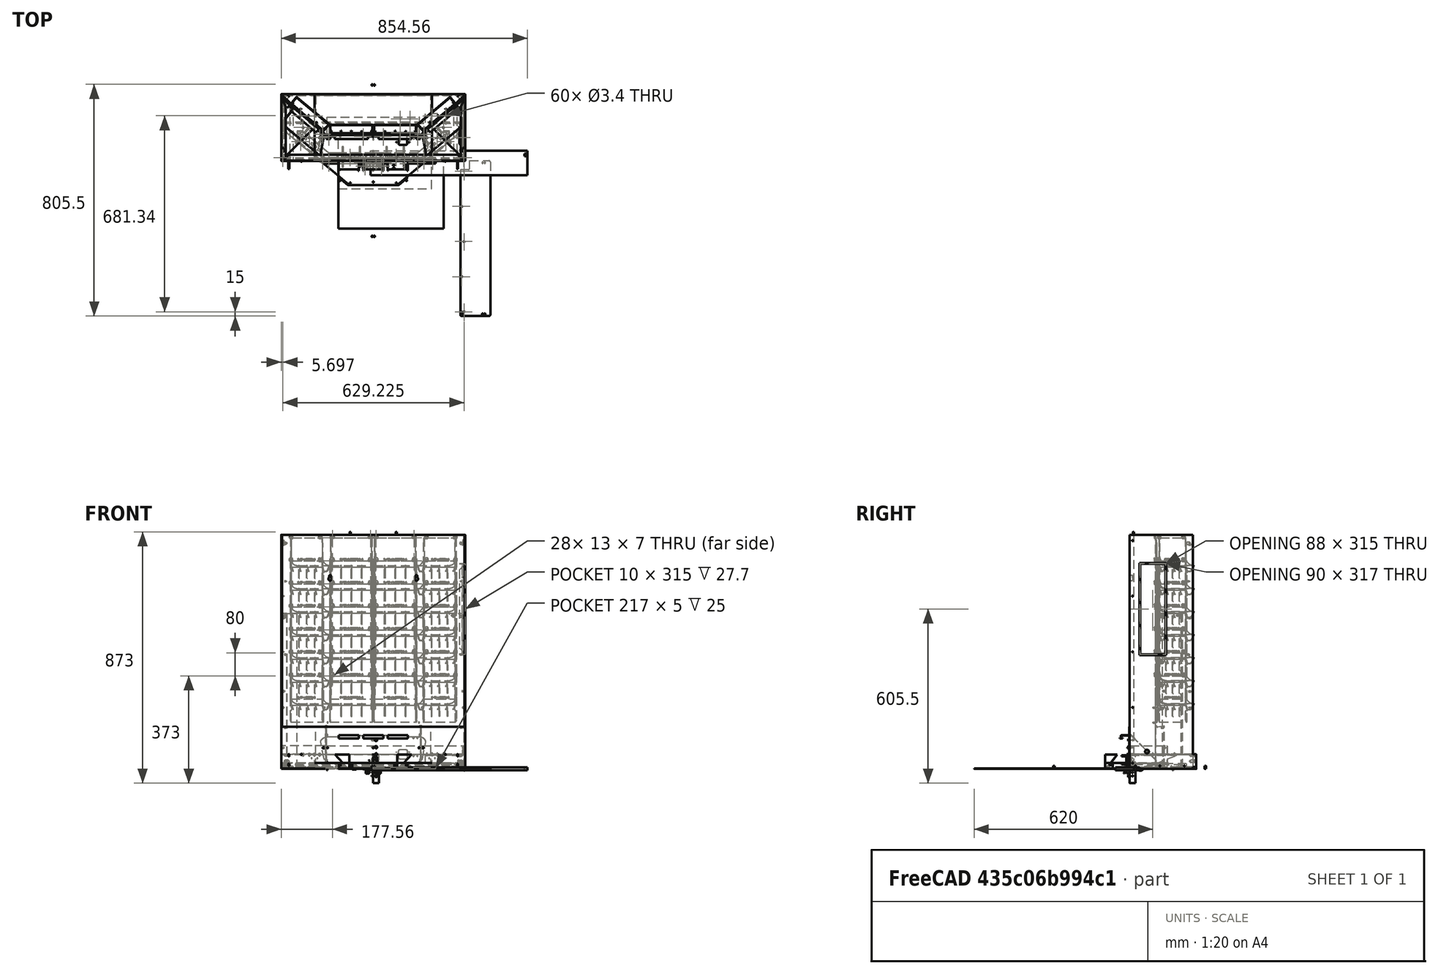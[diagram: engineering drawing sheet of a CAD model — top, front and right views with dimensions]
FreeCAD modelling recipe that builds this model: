
FCSTD DOCUMENT  (FreeCAD 0.22R37100 (Git))
Label: composit_stand10
License: All rights reserved
LicenseURL: http://en.wikipedia.org/wiki/All_rights_reserved
objects: Part::FeaturePython×149, Sketcher::SketchObject×121, PartDesign::CoordinateSystem×34, Part::Compound×33, PartDesign::SubShapeBinder×30, Part::Mirroring×28, Part::Extrusion×27, PartDesign::FeaturePython×26, PartDesign::Body×23, PartDesign::Boolean×23, PartDesign::Pocket×23, TechDraw::DrawViewDimension×21, PartDesign::Pad×18, App::DocumentObjectGroup×18, Path::FeaturePython×13, TechDraw::DrawViewPart×12, Part::Cylinder×5, PartDesign::Mirrored×5, TechDraw::DrawViewBalloon×5, TechDraw::DrawPage×5, +15 more types
note: 661 computed .brp shape members not serialized (recipe doc carries the construction recipe); baked Part::Feature solids carry a one-line shape summary decoded from their .brp
EXTERNAL_REF file=../module.FCStd obj=Spreadsheet
EXTERNAL_REF file=../module.FCStd obj=Sketch
EXTERNAL_REF file=../dropper.FCStd obj=Sketch007
EXTERNAL_REF file=../dropper.FCStd obj=Sketch008
EXTERNAL_REF file=../dropper.FCStd obj=Connect
EXTERNAL_REF file=../ULZ-P03-10W.FCStd obj=Sketch
EXTERNAL_REF file=../dropper.FCStd obj=Sketch
EXTERNAL_REF file=../magnet_fix.FCStd obj=Spreadsheet
EXTERNAL_REF file=../magnet_fix.FCStd obj=Sketch002
EXTERNAL_REF file=../module.FCStd obj=Body
EXTERNAL_REF file=../composit_electric_shield.FCStd obj=Body002
EXTERNAL_REF file=../composit_electric_shield.FCStd obj=Extrude002
EXTERNAL_REF file=composit_stand10_model.FCStd obj=Assembly
EXTERNAL_REF file=../magnet_fix.FCStd obj=Sketch006

FEATURE [Sketcher::SketchObject] Sketch
  FullyConstrained = true
  expr: Constraints[17] = module#<<Properties>>.module_width + 2 mm
  sketch-geometry (12):
    g0: LineSegment StartX=1 StartY=0 StartZ=0 EndX=151 EndY=0 EndZ=0
    g1: LineSegment StartX=151 StartY=0 StartZ=0 EndX=151 EndY=36 EndZ=0
    g2: LineSegment StartX=151 StartY=36 StartZ=0 EndX=1 EndY=36 EndZ=0
    g3: LineSegment StartX=1 StartY=36 StartZ=0 EndX=1 EndY=0 EndZ=0
    g4: LineSegment StartX=175.08 StartY=8.76442 StartZ=0 EndX=289.987 EndY=105.183 EndZ=0
    g5: LineSegment StartX=289.987 StartY=105.183 StartZ=0 EndX=266.846 EndY=132.76 EndZ=0
    g6: LineSegment StartX=266.846 StartY=132.76 StartZ=0 EndX=151.94 EndY=36.342 EndZ=0
    g7: LineSegment StartX=151.94 StartY=36.342 StartZ=0 EndX=175.08 EndY=8.76442 EndZ=0
    g8: LineSegment StartX=151 StartY=36 StartZ=0 EndX=151.532 EndY=36 EndZ=0
    g9: LineSegment StartX=151.94 StartY=36.342 StartZ=0 EndX=151.532 EndY=36 EndZ=0
    g10: LineSegment StartX=151 StartY=0 StartZ=0 EndX=164.635 EndY=0 EndZ=0
    g11: LineSegment StartX=175.08 StartY=8.76442 StartZ=0 EndX=164.635 EndY=0 EndZ=0
  constraints (34):
    c: Coincident(g0,g1)
    c: Coincident(g1,g2)
    c: Coincident(g2,g3)
    c: Coincident(g3,g0)
    c: Horizontal(g0)
    c: Horizontal(g2)
    c: Vertical(g1)
    c: Vertical(g3)
    c: Coincident(g4,g5)
    c: Coincident(g5,g6)
    c: Coincident(g6,g7)
    c: Coincident(g7,g4)
    c: Parallel(g4,g6)
    c: Parallel(g5,g7)
    c: Perpendicular(g5,g4)
    c: Equal(g2,g6)
    c: Equal(g1,g7)
    c: DistanceX(g2,g2) = 150
    c: DistanceY(g3,g3) = 36
    c: Coincident(g8,g1)
    c: Horizontal(g8)
    c: Coincident(g9,g6)
    c: Coincident(g9,g8)
    c: Coincident(g10,g0)
    c: Horizontal(g10)
    c: Coincident(g11,g4)
    c: Coincident(g11,g10)
    c: Parallel(g11,g4)
    c: Equal(g11,g10)
    c: Parallel(g9,g6)
    c: Angle(g4) = 0.698132
    c: DistanceX(g0) = 1
    c: Distance(g1,g6) = 1
    c: PointOnObject(g0,g-1)
FEATURE [Sketcher::SketchObject] Sketch001  label="base_sketch"
  ExternalGeometry = -> [Sketch]
  FullyConstrained = true
  sketch-geometry (4):
    g0: LineSegment StartX=0 StartY=0 StartZ=0 EndX=164.635 EndY=0 EndZ=0
    g1: LineSegment StartX=164.635 StartY=0 StartZ=0 EndX=319.563 EndY=130 EndZ=0
    g2: GeomPoint X=-164.635 Y=0 Z=0
    g3: GeomPoint X=-319.563 Y=130 Z=0
  constraints (12):
    c: PointOnObject(g0,g-2)
    c: Horizontal(g0)
    c: Coincident(g1,g0)
    c: PointOnObject(g-4,g1)
    c: PointOnObject(g-4,g1)
    c: PointOnObject(g-3,g0)
    c: Symmetric(g2,g0,g-2)
    c: DistanceX(g2,g0) = 329.27  'face_width'
    c: Symmetric(g3,g1,g-2)
    c: DistanceX(g3,g1) = 639.126  'total_width'
    c: DistanceY(g1) = 130  'total_depth'
    c: DistanceY(g0,g1) = 130
FEATURE [PartDesign::SubShapeBinder] Binder
  BindCopyOnChange = 0
  BindMode = 0
  ClaimChildren = true
  Context = -> Body [Binder.]
  Fuse = false
  MakeFace = true
  OffsetFill = false
  OffsetIntersection = false
  OffsetJoinType = 0
  OffsetOpenResult = false
  PartialLoad = false
  Relative = false
  Support = -> [Connect]
  _Version = 2
FEATURE [PartDesign::FeaturePython] BaseBend  # WARN: FeaturePython — macro-defined, semantics opaque (R4)
  BendSide = 0
  BendSketch = -> Binder
  MidPlane = false
  Reverse = false
  Suppressed = false
  length = 813
  radius = 0.1
  thickness = 0.3
FEATURE [PartDesign::SubShapeBinder] Binder001
  BindCopyOnChange = 0
  BindMode = 0
  ClaimChildren = true
  Context = -> Body001 [Binder001.]
  Fuse = false
  MakeFace = true
  OffsetFill = false
  OffsetIntersection = false
  OffsetJoinType = 0
  OffsetOpenResult = false
  PartialLoad = false
  Relative = false
  Support = -> [Connect001]
  _Version = 2
FEATURE [PartDesign::FeaturePython] BaseBend001  # WARN: FeaturePython — macro-defined, semantics opaque (R4)
  BendSide = 1
  BendSketch = -> Binder001
  MidPlane = false
  Reverse = false
  Suppressed = false
  length = 813
  radius = 0.1
  thickness = 0.3
  expr: length = <<BaseBend>>.length
FEATURE [Part::FeaturePython] Placment  # WARN: FeaturePython — macro-defined, semantics opaque (R4)
  AttacherType = Attacher::AttachEngine3D
  AttachmentOffset = pos=(0,0,0) rot=(-0.57735,-0.57735,-0.57735;2.0944rad)
  ExposePlacement = true
  MapMode = 45
  MarkerShape = 1
  MarkerSize = 50
  NumElements = 1
  Placement = pos=(76,0,0) rot=(0,0,1;0rad)
  Type = lattice2AttachablePlacement.AttachablePlacement
  isLattice = 1
FEATURE [Part::FeaturePython] Placment001  # WARN: FeaturePython — macro-defined, semantics opaque (R4)
  AttacherType = Attacher::AttachEngine3D
  AttachmentOffset = pos=(0,0,0) rot=(-0.57735,-0.57735,-0.57735;2.0944rad)
  ExposePlacement = true
  MapMode = 45
  MarkerShape = 1
  MarkerSize = 50
  NumElements = 1
  Placement = pos=(232.533,56.9735,0) rot=(0,0,1;0.698132rad)
  Type = lattice2AttachablePlacement.AttachablePlacement
  isLattice = 1
FEATURE [Part::FeaturePython] LinearArray002  # WARN: FeaturePython — macro-defined, semantics opaque (R4)
  Alignment = 0
  CellStart = A1
  Count = 2
  Dir = (1,0,0)
  DirIsDriven = true
  DistributionLaw = 0
  DrivenProperty = 1
  EndInclusive = true
  ExposePlacement = false
  GeneratorMode = 0
  MarkerShape = 1
  MarkerSize = 0
  NumElements = 2
  OrientMode = 1
  Placement = pos=(-30,13.8,0) rot=(0,0,1;0rad)
  Point = (0,0,0)
  PointIsDriven = true
  Reverse = false
  SpanEnd = 60
  SpanStart = 0
  Step = 60
  Type = lattice2LinearArray.LinearArray
  VSGVersion = 1
  Values = 0.0 | 60.0
  ValuesSource = 2
  isLattice = 1
  expr: .Placement.Base.x = -SpanEnd / 2
FEATURE [PartDesign::SubShapeBinder] Binder002
  BindCopyOnChange = 0
  BindMode = 0
  ClaimChildren = false
  Fuse = false
  MakeFace = true
  OffsetFill = false
  OffsetIntersection = false
  OffsetJoinType = 0
  OffsetOpenResult = false
  PartialLoad = false
  Relative = true
  Support = -> [<external ../module.FCStd>#Sketch]
  _Version = 2
  expr: Support = module#<<module_holes>>._self
FEATURE [Part::Extrusion] Extrude
  Base = -> Binder002
  Dir = (0,0,1)
  DirMode = 2
  FaceMakerClass = Part::FaceMakerBullseye
  LengthFwd = 3
  LengthRev = 0
  Reversed = true
  Solid = false
  Symmetric = false
FEATURE [Part::FeaturePython] LinearArray  # WARN: FeaturePython — macro-defined, semantics opaque (R4)
  Alignment = 0
  CellStart = A1
  Count = 7
  Dir = (0,-1,0)
  DirIsDriven = true
  DistributionLaw = 0
  DrivenProperty = 1
  EndInclusive = true
  ExposePlacement = false
  GeneratorMode = 1
  MarkerShape = 1
  MarkerSize = 0
  NumElements = 7
  OrientMode = 0
  Placement = pos=(0,0,0) rot=(0,0.707107,0.707107;3.14159rad)
  Point = (0,0,0)
  PointIsDriven = true
  Reverse = false
  SpanEnd = 50
  SpanStart = 0
  Step = 80
  Type = lattice2LinearArray.LinearArray
  VSGVersion = 1
  Values = 0.0 | 80.0 | 160.0 | 240.0 | 320.0 | 400.0 | 480.0
  ValuesSource = 2
  isLattice = 1
FEATURE [Part::FeaturePython] Placment002  # WARN: FeaturePython — macro-defined, semantics opaque (R4)
  AttacherType = Attacher::AttachEngine3D
  ExposePlacement = true
  MarkerShape = 1
  MarkerSize = 50
  NumElements = 1
  Placement = pos=(-76,0,0) rot=(0,0,1;0rad)
  Type = lattice2AttachablePlacement.AttachablePlacement
  isLattice = 1
  expr: .Placement.Base.x = -<<Placment>>.Placement.Base.x
  expr: .Placement.Base.y = <<Placment>>.Placement.Base.y
FEATURE [Part::FeaturePython] Placment003  # WARN: FeaturePython — macro-defined, semantics opaque (R4)
  AttacherType = Attacher::AttachEngine3D
  ExposePlacement = true
  MarkerShape = 1
  MarkerSize = 50
  NumElements = 1
  Placement = pos=(-232.533,56.9735,0) rot=(0,0,-1;0.698132rad)
  Type = lattice2AttachablePlacement.AttachablePlacement
  isLattice = 1
  expr: .Placement.Base.x = -<<Placment001>>.Placement.Base.x
  expr: .Placement.Base.y = <<Placment001>>.Placement.Base.y
  expr: .Placement.Rotation.Angle = -<<Placment001>>.Placement.Rotation.Angle
  expr: .Placement.Rotation.Axis = <<Placment001>>.Placement.Rotation.Axis
FEATURE [Part::FeaturePython] Join  # WARN: FeaturePython — macro-defined, semantics opaque (R4)
  ExposePlacement = false
  Interleave = false
  Links = -> [Placment,Placment001,Placment002,Placment003]
  MarkerShape = 1
  MarkerSize = 0
  NumElements = 4
  Type = lattice2JoinArrays.JoinArrays
  isLattice = 1
FEATURE [Part::FeaturePython] Populate  label="Populate Join with LinearArray"  # WARN: FeaturePython — macro-defined, semantics opaque (R4)
  Copying = 0
  ExposePlacement = false
  MarkerShape = 1
  MarkerSize = 0
  NumElements = 28
  Object = -> LinearArray
  OutputCompounding = 0
  Placement = pos=(0,90,803) rot=(0,0,1;0rad)
  PlacementsTo = -> Join
  Referencing = 0
  Type = lattice2PopulateCopies.LatticePopulateCopies
  isLattice = 1
  expr: .Placement.Base.y = <<Dimensions_sketch>>.Constraints.offset
  expr: .Placement.Base.z = <<BaseBend>>.length - 10 mm
FEATURE [Part::FeaturePython] Populate001  label="Populate Populate Join with LinearArray with Extrude"  # WARN: FeaturePython — macro-defined, semantics opaque (R4)
  Copying = 0
  ExposePlacement = false
  MarkerShape = 1
  MarkerSize = 0
  NumElements = 0
  Object = -> Extrude
  OutputCompounding = 1
  PlacementsTo = -> Populate
  Referencing = 0
  Type = lattice2PopulateCopies.LatticePopulateCopies
  isLattice = 0
FEATURE [PartDesign::SubShapeBinder] Binder003
  BindCopyOnChange = 0
  BindMode = 0
  ClaimChildren = true
  Fuse = false
  MakeFace = true
  OffsetFill = false
  OffsetIntersection = false
  OffsetJoinType = 0
  OffsetOpenResult = false
  PartialLoad = false
  Relative = true
  Support = -> [<external ../dropper.FCStd>#Sketch007]
  _Version = 2
  expr: Support = <<dropper>>#<<base>>._self
FEATURE [PartDesign::SubShapeBinder] Binder004
  BindCopyOnChange = 0
  BindMode = 0
  ClaimChildren = false
  Fuse = false
  MakeFace = true
  OffsetFill = false
  OffsetIntersection = false
  OffsetJoinType = 0
  OffsetOpenResult = false
  PartialLoad = false
  Relative = true
  Support = -> [<external ../dropper.FCStd>#Sketch008]
  _Version = 2
  expr: Support = dropper#<<feed>>._self
FEATURE [PartDesign::SubShapeBinder] Binder005
  BindCopyOnChange = 0
  BindMode = 0
  ClaimChildren = false
  Fuse = false
  MakeFace = true
  OffsetFill = false
  OffsetIntersection = false
  OffsetJoinType = 0
  OffsetOpenResult = false
  PartialLoad = false
  Relative = true
  Support = -> [<external ../dropper.FCStd>#Connect]
  _Version = 2
  expr: Support = dropper#<<fix>>._self
FEATURE [Part::Extrusion] Extrude001
  Base = -> Binder003
  Dir = (0,0,1)
  DirMode = 2
  FaceMakerClass = Part::FaceMakerBullseye
  LengthFwd = 5
  LengthRev = 0
  Solid = false
  Symmetric = false
FEATURE [Part::Extrusion] Extrude002
  Base = -> Binder005
  Dir = (0,0,1)
  DirMode = 2
  FaceMakerClass = Part::FaceMakerBullseye
  LengthFwd = 2.5
  LengthRev = 0
  Solid = false
  Symmetric = false
FEATURE [Part::Extrusion] Extrude003
  Base = -> Binder004
  Dir = (0,0,1)
  DirMode = 2
  FaceMakerClass = Part::FaceMakerBullseye
  LengthFwd = 5
  LengthRev = 0
  Solid = false
  Symmetric = false
FEATURE [Part::FeaturePython] Populate002  label="Populate Join with LinearArray002"  # WARN: FeaturePython — macro-defined, semantics opaque (R4)
  Copying = 0
  ExposePlacement = false
  MarkerShape = 1
  MarkerSize = 0
  NumElements = 8
  Object = -> LinearArray002
  OutputCompounding = 0
  PlacementsTo = -> Join
  Referencing = 0
  Type = lattice2PopulateCopies.LatticePopulateCopies
  isLattice = 1
FEATURE [Part::FeaturePython] Populate003  label="Populate Populate Join with LinearArray002 with Fusion"  # WARN: FeaturePython — macro-defined, semantics opaque (R4)
  Copying = 0
  ExposePlacement = false
  MarkerShape = 1
  MarkerSize = 0
  NumElements = 0
  Object = -> Extrude001
  OutputCompounding = 1
  PlacementsTo = -> Populate002
  Referencing = 0
  Type = lattice2PopulateCopies.LatticePopulateCopies
  isLattice = 0
FEATURE [PartDesign::FeaturePython] Extend  # WARN: FeaturePython — macro-defined, semantics opaque (R4)
  BaseFeature = -> BaseBend
  Offset = 0.02
  Refine = true
  Suppressed = false
  UseSubtraction = false
  baseObject = -> BaseBend [Face1]
  gap1 = 0
  gap2 = 0
  length = 0
FEATURE [PartDesign::FeaturePython] Bend  # WARN: FeaturePython — macro-defined, semantics opaque (R4)
  AutoMiter = false
  BaseFeature = -> Extend
  BendType = 0
  LengthList = [0.1]
  LengthSpec = 0
  ReliefFactor = 0.7
  Suppressed = false
  UseReliefFactor = false
  angle = 90
  baseObject = -> Extend [Edge4,Edge17,Edge75,Edge46,Edge63]
  bendAList = [90]
  extend1 = 0
  extend2 = 0
  gap1 = 0
  gap2 = 0
  invert = true
  kfactor = 0.5
  length = 0.1
  maxExtendDist = 2.5
  minGap = 0.1
  minReliefGap = 1.5
  miterangle1 = 0
  miterangle2 = 0
  offset = 0
  radius = 0.1
  reliefType = 0
  reliefd = 1
  reliefw = 0.8
  sketchflip = false
  sketchinvert = false
  unfold = false
  expr: radius = BaseBend.radius
FEATURE [Sketcher::SketchObject] Sketch007
  ExternalGeometry = -> [Sketch001]
  FullyConstrained = true
  sketch-geometry (9):
    g0: LineSegment StartX=299.876 StartY=113.48 StartZ=0 EndX=319.563 EndY=130 EndZ=0
    g1: LineSegment StartX=319.563 StartY=130 StartZ=0 EndX=274.703 EndY=183.462 EndZ=0
    g2: LineSegment StartX=274.703 StartY=183.462 StartZ=0 EndX=264.242 EndY=179.655 EndZ=0
    g3: LineSegment StartX=264.482 StartY=178.997 StartZ=0 EndX=274.482 EndY=182.637 EndZ=0
    g4: LineSegment StartX=274.482 StartY=182.637 StartZ=0 EndX=319.477 EndY=129.014 EndZ=0
    g5: LineSegment StartX=319.477 StartY=129.014 StartZ=0 EndX=300.326 EndY=112.944 EndZ=0
    g6: LineSegment StartX=300.326 StartY=112.944 StartZ=0 EndX=299.876 EndY=113.48 EndZ=0
    g7: LineSegment StartX=264.482 StartY=178.997 StartZ=0 EndX=264.242 EndY=179.655 EndZ=0
    g8: LineSegment StartX=319.477 StartY=129.014 StartZ=0 EndX=320.013 EndY=129.464 EndZ=0
  constraints (26):
    c: Coincident(g0,g1)
    c: Coincident(g1,g2)
    c: Coincident(g0,g-3)
    c: PointOnObject(g0,g-3)
    c: Angle(g1) = 2.26893
    c: Angle(g2,g1) = 1.91986
    c: Coincident(g3,g4)
    c: Coincident(g4,g5)
    c: Coincident(g5,g6)
    c: Coincident(g6,g0)
    c: Coincident(g3,g7)
    c: Coincident(g7,g2)
    c: Perpendicular(g2,g7)
    c: Perpendicular(g3,g7)
    c: Perpendicular(g5,g6)
    c: Perpendicular(g0,g6)
    c: Distance(g6) = 0.7
    c: Coincident(g8,g4)
    c: PointOnObject(g8,g1)
    c: Perpendicular(g4,g8)
    c: Equal(g7,g8)
    c: Equal(g8,g6)
    c: Distance(g5) = 25
    c: DistanceX(g3,g3) = 10
    c: Parallel(g4,g1)
    c: Distance(g4) = 70
FEATURE [PartDesign::SubShapeBinder] Binder006
  BindCopyOnChange = 0
  BindMode = 0
  ClaimChildren = true
  Context = -> Body003 [Binder006.]
  Fuse = false
  MakeFace = true
  OffsetFill = false
  OffsetIntersection = false
  OffsetJoinType = 0
  OffsetOpenResult = false
  PartialLoad = false
  Relative = false
  Support = -> [Sketch007]
  _Version = 2
FEATURE [PartDesign::FeaturePython] BaseBend002  # WARN: FeaturePython — macro-defined, semantics opaque (R4)
  BendSide = 1
  BendSketch = -> Binder006
  MidPlane = false
  Reverse = false
  Suppressed = false
  length = 540
  radius = 2
  thickness = 0.7
FEATURE [PartDesign::SubShapeBinder] Binder007
  BindCopyOnChange = 0
  BindMode = 0
  ClaimChildren = true
  Context = -> Body004 [Binder007.]
  Fuse = false
  MakeFace = true
  OffsetFill = false
  OffsetIntersection = false
  OffsetJoinType = 0
  OffsetOpenResult = false
  PartialLoad = false
  Relative = false
  Support = -> [Connect006]
  _Version = 2
FEATURE [PartDesign::Pad] Pad
  Direction = (0,0,1)
  Length = 5
  Length2 = 10
  Profile = -> Binder007
  Suppressed = false
  Type = 0
FEATURE [Sketcher::SketchObject] Sketch008  label="dropper_fix_composit_base_sketch"
  ExternalGeometry = -> [Sketch001]
  FullyConstrained = true
  expr: Constraints[31] = -<<Dimensions_sketch>>.Constraints.offset + 5.4 mm
  sketch-geometry (10):
    g0: LineSegment StartX=0 StartY=-84.6 StartZ=0 EndX=83.1036 EndY=-84.6 EndZ=0
    g1: LineSegment StartX=83.1036 StartY=-84.6 StartZ=0 EndX=313.563 EndY=108.778 EndZ=0
    g2: LineSegment StartX=313.563 StartY=108.778 StartZ=0 EndX=313.563 EndY=130 EndZ=0
    g3: LineSegment StartX=313.563 StartY=130 StartZ=0 EndX=0 EndY=130 EndZ=0
    g4: LineSegment StartX=164.635 StartY=0 StartZ=0 EndX=164.635 EndY=-3 EndZ=0
    g5: LineSegment StartX=164.635 StartY=-3 StartZ=0 EndX=164.635 EndY=-4 EndZ=0
    g6: LineSegment StartX=164.635 StartY=-4 StartZ=0 EndX=164.635 EndY=-7.4 EndZ=0
    g7: LineSegment StartX=164.635 StartY=-7.4 StartZ=0 EndX=164.635 EndY=-12.4 EndZ=0
    g8: LineSegment StartX=0 StartY=0 StartZ=0 EndX=0 EndY=-12.4 EndZ=0
    g9: LineSegment StartX=164.635 StartY=0 StartZ=0 EndX=172.606 EndY=-9.49895 EndZ=0
  constraints (33):
    c: PointOnObject(g0,g-2)
    c: Horizontal(g0)
    c: Coincident(g1,g2)
    c: Vertical(g2)
    c: Coincident(g2,g3)
    c: PointOnObject(g3,g-2)
    c: Horizontal(g3)
    c: PointOnObject(g-3,g3)
    c: Parallel(g1,g-3)
    c: Coincident(g4,g-3)
    c: Coincident(g5,g4)
    c: Vertical(g5)
    c: Coincident(g6,g5)
    c: Coincident(g7,g6)
    c: Vertical(g7)
    c: Vertical(g6)
    c: Vertical(g4)
    c: DistanceY(g4,g4) = 3
    c: DistanceY(g6,g6) = 3.4
    c: DistanceY(g5,g5) = 1
    c: DistanceY(g7,g7) = 5
    c: Vertical(g8)
    c: Horizontal(g4,g8)
    c: Coincident(g9,g4)
    c: Equal(g9,g8)
    c: DistanceX(g2,g-3) = 6
    c: Angle(g1) = 0.698132  'angle'
    c: PointOnObject(g9,g1)
    c: Perpendicular(g1,g9)
    c: Coincident(g0,g1)
    c: Horizontal(g8,g7)
    c: DistanceY(g0) = -84.6
    c: PointOnObject(g8,g-2)
FEATURE [PartDesign::Body] Body005  label="dummy_body"
  Origin = -> Origin005
FEATURE [Part::Extrusion] Extrude004
  Base = -> Binder003
  Dir = (0,0,1)
  DirMode = 2
  FaceMakerClass = Part::FaceMakerBullseye
  LengthFwd = 2.5
  LengthRev = 0
  Solid = false
  Symmetric = false
FEATURE [Part::Mirroring] Part__Mirroring003  label="Sketch008 (Mirror #4)"
  Base = (0,0,0)
  Normal = (1,0,0)
  Source = -> Sketch008
FEATURE [Part::FeaturePython] Connect003  # WARN: FeaturePython — macro-defined, semantics opaque (R4)
  Objects = -> [Sketch008,Part__Mirroring003]
  Tolerance = 0
FEATURE [PartDesign::SubShapeBinder] Binder008
  BindCopyOnChange = 0
  BindMode = 0
  ClaimChildren = true
  Context = -> Body006 [Binder008.]
  Fuse = false
  MakeFace = true
  OffsetFill = false
  OffsetIntersection = false
  OffsetJoinType = 0
  OffsetOpenResult = false
  PartialLoad = false
  Relative = false
  Support = -> [Connect003]
  _Version = 2
FEATURE [PartDesign::FeaturePython] BaseBend003  # WARN: FeaturePython — macro-defined, semantics opaque (R4)
  BendSide = 0
  BendSketch = -> Binder008
  MidPlane = false
  Reverse = false
  Suppressed = false
  length = 100
  radius = 0.1
  thickness = 0.3
FEATURE [PartDesign::FeaturePython] Extend001  # WARN: FeaturePython — macro-defined, semantics opaque (R4)
  BaseFeature = -> BaseBend003
  Offset = 0.02
  Refine = true
  Suppressed = false
  UseSubtraction = false
  baseObject = -> BaseBend003 [Face1]
  gap1 = 0
  gap2 = 0
  length = 0
FEATURE [PartDesign::FeaturePython] Bend001  # WARN: FeaturePython — macro-defined, semantics opaque (R4)
  AutoMiter = true
  BaseFeature = -> Extend001
  BendType = 0
  LengthList = [20]
  LengthSpec = 0
  ReliefFactor = 0.7
  Suppressed = false
  UseReliefFactor = false
  angle = 90
  baseObject = -> Extend001 [Edge11,Edge9,Edge8,Edge6]
  bendAList = [90]
  extend1 = 0
  extend2 = 0
  gap1 = 0
  gap2 = 0
  invert = true
  kfactor = 0.5
  length = 20
  maxExtendDist = 5
  minGap = 0.2
  minReliefGap = 1
  miterangle1 = 0
  miterangle2 = 0
  offset = 0
  radius = 0.1
  reliefType = 0
  reliefd = 1
  reliefw = 0.8
  sketchflip = false
  sketchinvert = false
  unfold = false
  expr: radius = BaseBend003.radius
FEATURE [Sketcher::SketchObject] Sketch011
  FullyConstrained = true
  sketch-geometry (3):
    g0: ArcOfCircle CenterX=-2 CenterY=-2 CenterZ=0 NormalX=0 NormalY=0 NormalZ=1 AngleXU=0 Radius=2 StartAngle=0 EndAngle=1.5708
    g1: LineSegment StartX=-2 StartY=0 StartZ=0 EndX=0 EndY=0 EndZ=0
    g2: LineSegment StartX=0 StartY=0 StartZ=0 EndX=0 EndY=-2 EndZ=0
  constraints (7):
    c: PointOnObject(g0,g-2)
    c: PointOnObject(g0,g-1)
    c: Coincident(g1,g2)
    c: Tangent(g2,g0) = 1.5708
    c: Tangent(g0,g1) = 1.5708
    c: Coincident(g1,g-1)
    c: Radius(g0) = 2
FEATURE [Part::Extrusion] Extrude005
  Base = -> Sketch011
  Dir = (0,0,1)
  DirMode = 2
  FaceMakerClass = Part::FaceMakerBullseye
  LengthFwd = 10
  LengthRev = 0
  Solid = true
  Symmetric = true
FEATURE [Part::FeaturePython] Placment004  # WARN: FeaturePython — macro-defined, semantics opaque (R4)
  AttacherType = Attacher::AttachEngine3D
  AttachmentOffset = pos=(0,0,0) rot=(-0.707107,0,0.707107;3.14159rad)
  ExposePlacement = true
  MapMode = 7
  MarkerShape = 1
  MarkerSize = 20
  NumElements = 1
  Placement = pos=(264.242,179.655,0) rot=(-0.123724,0.701674,-0.701674;2.8954rad)
  Type = lattice2AttachablePlacement.AttachablePlacement
  isLattice = 1
FEATURE [Part::FeaturePython] Placment005  # WARN: FeaturePython — macro-defined, semantics opaque (R4)
  AttacherType = Attacher::AttachEngine3D
  AttachmentOffset = pos=(0,0,0) rot=(0.707107,0,0.707107;3.14159rad)
  ExposePlacement = true
  MapMode = 7
  MarkerShape = 1
  MarkerSize = 10
  NumElements = 1
  Placement = pos=(299.876,113.48,0) rot=(-0.249244,0.684791,-0.684791;2.65306rad)
  Type = lattice2AttachablePlacement.AttachablePlacement
  isLattice = 1
FEATURE [Part::FeaturePython] Join001  # WARN: FeaturePython — macro-defined, semantics opaque (R4)
  ExposePlacement = false
  Interleave = false
  Links = -> [Placment004,Placment005]
  MarkerShape = 1
  MarkerSize = 0
  NumElements = 2
  Type = lattice2JoinArrays.JoinArrays
  isLattice = 1
FEATURE [Part::FeaturePython] Populate005  label="Populate Join001 with Extrude005"  # WARN: FeaturePython — macro-defined, semantics opaque (R4)
  Copying = 0
  ExposePlacement = false
  MarkerShape = 1
  MarkerSize = 0
  NumElements = 0
  Object = -> Extrude005
  OutputCompounding = 1
  PlacementsTo = -> Join001
  Referencing = 0
  Type = lattice2PopulateCopies.LatticePopulateCopies
  isLattice = 0
FEATURE [Part::FeaturePython] Mirror  label="Mirror of Populate Join001 with Extrude005"  # WARN: FeaturePython — macro-defined, semantics opaque (R4)
  ExposePlacement = false
  FlipX = false
  FlipY = false
  FlipZ = true
  MarkerShape = 1
  MarkerSize = 0
  NumElements = 0
  Object = -> Populate005
  ObjectTraversal = 0
  PivotPlacement = pos=(0,0,270) rot=(0,0,1;0rad)
  Type = lattice2Mirror.LatticeMirror
  isLattice = 0
  expr: .PivotPlacement.Base.z = <<BaseBend002>>.length / 2
FEATURE [PartDesign::SubShapeBinder] Binder010
  BindCopyOnChange = 0
  BindMode = 0
  ClaimChildren = false
  Fuse = false
  MakeFace = true
  OffsetFill = false
  OffsetIntersection = false
  OffsetJoinType = 0
  OffsetOpenResult = false
  PartialLoad = false
  Relative = true
  Support = -> [<external ../ULZ-P03-10W.FCStd>#Sketch]
  _Version = 2
  expr: Support = <<ULZ-P03-10W>>#<<Sketch>>._self
FEATURE [Sketcher::SketchObject] Sketch012
  ExternalGeometry = -> [Binder010]
  FullyConstrained = true
  sketch-geometry (12):
    g0: ArcOfCircle CenterX=3.95 CenterY=-263.8 CenterZ=0 NormalX=0 NormalY=0 NormalZ=1 AngleXU=0 Radius=1.7 StartAngle=3.14159 EndAngle=6.28319
    g1: ArcOfCircle CenterX=3.95 CenterY=-262.2 CenterZ=0 NormalX=0 NormalY=0 NormalZ=1 AngleXU=0 Radius=1.7 StartAngle=2.911e-13 EndAngle=3.14159
    g2: LineSegment StartX=2.25 StartY=-263.8 StartZ=0 EndX=2.25 EndY=-262.2 EndZ=0
    g3: LineSegment StartX=5.65 StartY=-263.8 StartZ=0 EndX=5.65 EndY=-262.2 EndZ=0
    g4: GeomPoint X=3.95 Y=-260.5 Z=0
    g5: GeomPoint X=3.95 Y=-265.5 Z=0
    g6: ArcOfCircle CenterX=-3.95 CenterY=262.2 CenterZ=0 NormalX=0 NormalY=0 NormalZ=1 AngleXU=0 Radius=1.7 StartAngle=3.14159 EndAngle=6.28319
    g7: ArcOfCircle CenterX=-3.95 CenterY=263.8 CenterZ=0 NormalX=0 NormalY=0 NormalZ=1 AngleXU=0 Radius=1.7 StartAngle=1.26e-14 EndAngle=3.14159
    g8: LineSegment StartX=-5.65 StartY=262.2 StartZ=0 EndX=-5.65 EndY=263.8 EndZ=0
    g9: LineSegment StartX=-2.25 StartY=262.2 StartZ=0 EndX=-2.25 EndY=263.8 EndZ=0
    g10: GeomPoint X=-3.95 Y=265.5 Z=0
    g11: GeomPoint X=-3.95 Y=260.5 Z=0
  constraints (26):
    c: Tangent(g0,g2) = 1.5708
    c: Tangent(g0,g3) = -1.5708
    c: Tangent(g1,g2) = 1.5708
    c: Tangent(g1,g3) = -1.5708
    c: Equal(g0,g1)
    c: Vertical(g2)
    c: Symmetric(g0,g1,g-4)
    c: Equal(g1,g-4)
    c: PointOnObject(g4,g1)
    c: PointOnObject(g5,g0)
    c: Vertical(g5,g0)
    c: Vertical(g4,g1)
    c: DistanceY(g5,g4) = 5
    c: Tangent(g6,g8) = 1.5708
    c: Tangent(g6,g9) = -1.5708
    c: Tangent(g7,g8) = 1.5708
    c: Tangent(g7,g9) = -1.5708
    c: Equal(g6,g7)
    c: Vertical(g8)
    c: Symmetric(g6,g7,g-3)
    c: PointOnObject(g10,g7)
    c: PointOnObject(g11,g6)
    c: Vertical(g11,g-3)
    c: Vertical(g-3,g10)
    c: Equal(g-3,g7)
    c: DistanceY(g11,g10) = 5
FEATURE [Part::Extrusion] Extrude006
  Base = -> Sketch012
  Dir = (0,0,1)
  DirMode = 2
  FaceMakerClass = Part::FaceMakerBullseye
  LengthFwd = 10
  LengthRev = 0
  Solid = true
  Symmetric = false
FEATURE [Part::Mirroring] Part__Mirroring004  label="Extrude006 (Mirror #5)"
  Base = (0,0,0)
  Normal = (1,0,0)
  Source = -> Extrude006
FEATURE [Part::Compound] Compound005
  Links = -> [Extrude006,Part__Mirroring004]
FEATURE [Part::FeaturePython] Placment006  # WARN: FeaturePython — macro-defined, semantics opaque (R4)
  AttacherType = Attacher::AttachEngine3D
  AttachmentOffset = pos=(0,270,13) rot=(0,-1,0;1.5708rad)
  ExposePlacement = true
  MapMode = 7
  MarkerShape = 1
  MarkerSize = 20
  NumElements = 1
  Placement = pos=(283.059,173.504,270) rot=(0.834817,-0.389282,-0.389282;1.75037rad)
  Type = lattice2AttachablePlacement.AttachablePlacement
  isLattice = 1
  expr: .AttachmentOffset.Base.y = <<BaseBend002>>.length / 2
FEATURE [Part::FeaturePython] Populate006  label="Populate Placment006 with Compound005"  # WARN: FeaturePython — macro-defined, semantics opaque (R4)
  Copying = 0
  ExposePlacement = false
  MarkerShape = 1
  MarkerSize = 0
  NumElements = 0
  Object = -> Compound005
  OutputCompounding = 2
  PlacementsTo = -> Placment006
  Referencing = 0
  Type = lattice2PopulateCopies.LatticePopulateCopies
  isLattice = 0
FEATURE [Part::FeaturePython] Placment007  # WARN: FeaturePython — macro-defined, semantics opaque (R4)
  AttacherType = Attacher::AttachEngine3D
  ExposePlacement = true
  MarkerShape = 1
  MarkerSize = 50
  NumElements = 1
  Placement = pos=(0,13,0) rot=(0,0,1;0rad)
  Type = lattice2AttachablePlacement.AttachablePlacement
  isLattice = 1
FEATURE [Part::FeaturePython] Placment008  # WARN: FeaturePython — macro-defined, semantics opaque (R4)
  AttacherType = Attacher::AttachEngine3D
  ExposePlacement = true
  MarkerShape = 1
  MarkerSize = 50
  NumElements = 1
  Placement = pos=(127.5,21,0) rot=(0,0,1;0rad)
  Type = lattice2AttachablePlacement.AttachablePlacement
  isLattice = 1
  expr: .Placement.Base.x = <<LinearArray003>>.Step / 2
FEATURE [Part::FeaturePython] Join002  # WARN: FeaturePython — macro-defined, semantics opaque (R4)
  ExposePlacement = false
  Interleave = false
  Links = -> [Placment007,Placment008]
  MarkerShape = 1
  MarkerSize = 0
  NumElements = 2
  Type = lattice2JoinArrays.JoinArrays
  isLattice = 1
FEATURE [Part::FeaturePython] LinearArray003  # WARN: FeaturePython — macro-defined, semantics opaque (R4)
  Alignment = 0
  CellStart = A1
  Count = 3
  Dir = (1,0,0)
  DirIsDriven = true
  DistributionLaw = 0
  DrivenProperty = 1
  EndInclusive = true
  ExposePlacement = false
  GeneratorMode = 0
  MarkerShape = 1
  MarkerSize = 0
  NumElements = 3
  OrientMode = 1
  Point = (0,0,0)
  PointIsDriven = true
  Reverse = false
  SpanEnd = 525
  SpanStart = 15
  Step = 255
  Type = lattice2LinearArray.LinearArray
  VSGVersion = 1
  Values = 15.0 | 270.0 | 525.0
  ValuesSource = 2
  isLattice = 1
  expr: SpanEnd = <<BaseBend002>>.length - 15 mm
FEATURE [Part::Box] Box  label="Cube"
  AttacherType = Attacher::AttachEngine3D
  Height = 10
  Length = 545
  Placement = pos=(-10,-50,-5) rot=(0,0,1;0rad)
  Width = 84
  expr: Length = <<LinearArray003>>.SpanEnd + 20 mm
FEATURE [Part::FeaturePython] Populate007  label="Populate LinearArray003 with Join002"  # WARN: FeaturePython — macro-defined, semantics opaque (R4)
  Copying = 0
  ExposePlacement = false
  MarkerShape = 1
  MarkerSize = 0
  NumElements = 6
  Object = -> Join002
  OutputCompounding = 0
  PlacementsTo = -> LinearArray003
  Referencing = 0
  Type = lattice2PopulateCopies.LatticePopulateCopies
  isLattice = 1
FEATURE [Part::FeaturePython] ArrayFilter  # WARN: FeaturePython — macro-defined, semantics opaque (R4)
  Base = -> Populate007
  ExposePlacement = false
  FilterType = 2
  Invert = false
  MarkerShape = 1
  MarkerSize = 0
  NumElements = 5
  Stencil = -> Box
  Type = lattice2ArrayFilter.LatticeArrayFilter
  WindowFrom = 0
  WindowTo = 1
  isLattice = 1
FEATURE [Part::FeaturePython] Placment009  # WARN: FeaturePython — macro-defined, semantics opaque (R4)
  AttacherType = Attacher::AttachEngine3D
  AttachmentOffset = pos=(-1,0,0) rot=(0.57735,0.57735,0.57735;2.0944rad)
  ExposePlacement = true
  MapMode = 7
  MarkerShape = 1
  MarkerSize = 20
  NumElements = 1
  Placement = pos=(318.92,130.766,0) rot=(0.671543,-0.313146,0.671543;2.53465rad)
  Type = lattice2AttachablePlacement.AttachablePlacement
  isLattice = 1
FEATURE [Part::FeaturePython] Populate008  label="Populate Placment009 with ArrayFilter"  # WARN: FeaturePython — macro-defined, semantics opaque (R4)
  Copying = 0
  ExposePlacement = false
  MarkerShape = 1
  MarkerSize = 0
  NumElements = 5
  Object = -> ArrayFilter
  OutputCompounding = 0
  PlacementsTo = -> Placment009
  Referencing = 0
  Type = lattice2PopulateCopies.LatticePopulateCopies
  isLattice = 1
FEATURE [Part::Cylinder] Cylinder001
  Angle = 360
  AttacherType = Attacher::AttachEngine3D
  FirstAngle = 0
  Height = 10
  Radius = 1.7
  SecondAngle = 0
FEATURE [Part::FeaturePython] Populate009  label="Populate Populate Placment009 with ArrayFilter with Cylinder001"  # WARN: FeaturePython — macro-defined, semantics opaque (R4)
  Copying = 0
  ExposePlacement = false
  MarkerShape = 1
  MarkerSize = 0
  NumElements = 0
  Object = -> Cylinder001
  OutputCompounding = 1
  PlacementsTo = -> Populate008
  Referencing = 0
  Type = lattice2PopulateCopies.LatticePopulateCopies
  isLattice = 0
FEATURE [Part::FeaturePython] LinearArray004  # WARN: FeaturePython — macro-defined, semantics opaque (R4)
  Alignment = 0
  CellStart = A1
  Count = 2
  Dir = (1,0,0)
  DirIsDriven = true
  DistributionLaw = 0
  DrivenProperty = 1
  EndInclusive = true
  ExposePlacement = false
  GeneratorMode = 0
  MarkerShape = 1
  MarkerSize = 0
  NumElements = 2
  OrientMode = 1
  Placement = pos=(0,20,0) rot=(0,0,1;0rad)
  Point = (0,0,0)
  PointIsDriven = true
  Reverse = false
  SpanEnd = 530
  SpanStart = 10
  Step = 520
  Type = lattice2LinearArray.LinearArray
  VSGVersion = 1
  Values = 10.0 | 530.0
  ValuesSource = 2
  isLattice = 1
  expr: SpanEnd = <<BaseBend002>>.length - SpanStart
FEATURE [Part::Cylinder] Cylinder002
  Angle = 360
  AttacherType = Attacher::AttachEngine3D
  FirstAngle = 0
  Height = 10
  Radius = 4
  SecondAngle = 0
FEATURE [Part::FeaturePython] Populate010  label="Populate Placment009 with LinearArray004"  # WARN: FeaturePython — macro-defined, semantics opaque (R4)
  Copying = 0
  ExposePlacement = false
  MarkerShape = 1
  MarkerSize = 0
  NumElements = 2
  Object = -> LinearArray004
  OutputCompounding = 0
  PlacementsTo = -> Placment009
  Referencing = 0
  Type = lattice2PopulateCopies.LatticePopulateCopies
  isLattice = 1
FEATURE [Part::FeaturePython] Populate011  label="Populate Populate Placment009 with LinearArray004 with Cylinder002"  # WARN: FeaturePython — macro-defined, semantics opaque (R4)
  Copying = 0
  ExposePlacement = false
  MarkerShape = 1
  MarkerSize = 0
  NumElements = 0
  Object = -> Cylinder002
  OutputCompounding = 1
  PlacementsTo = -> Populate010
  Referencing = 0
  Type = lattice2PopulateCopies.LatticePopulateCopies
  isLattice = 0
FEATURE [Part::Compound] Compound004
  Links = -> [Populate005,Mirror,Populate006,Populate009,Populate011]
FEATURE [PartDesign::Boolean] Boolean003
  BaseFeature = -> BaseBend002
  Group = -> [Compound004]
  Suppressed = false
  Type = 1
  UsePlacement = true
FEATURE [Sketcher::SketchObject] Sketch013  label="pump_holder_base_sketch"
  FullyConstrained = true
  Placement = pos=(0,0,0) rot=(0.57735,0.57735,0.57735;2.0944rad)
  sketch-geometry (7):
    g0: LineSegment StartX=0 StartY=116 StartZ=0 EndX=5 EndY=116 EndZ=0
    g1: LineSegment StartX=5 StartY=116 StartZ=0 EndX=90 EndY=31 EndZ=0
    g2: LineSegment StartX=90 StartY=31 StartZ=0 EndX=90 EndY=0 EndZ=0
    g3: LineSegment StartX=90 StartY=0 StartZ=0 EndX=151 EndY=0 EndZ=0
    g4: LineSegment StartX=-2e-16 StartY=0 StartZ=0 EndX=10 EndY=-10 EndZ=0
    g5: ArcOfCircle CenterX=-1.90919 CenterY=-1.90919 CenterZ=0 NormalX=0 NormalY=0 NormalZ=1 AngleXU=0 Radius=2.7 StartAngle=0.785398 EndAngle=1.5708
    g6: LineSegment StartX=-2.00919 StartY=0.790812 StartZ=0 EndX=-1.90919 EndY=0.790812 EndZ=0
  constraints (24):
    c: Horizontal(g0)
    c: Coincident(g0,g1)
    c: Coincident(g1,g2)
    c: PointOnObject(g2,g-1)
    c: Vertical(g2)
    c: Coincident(g2,g3)
    c: PointOnObject(g3,g-1)
    c: DistanceX(g3,g3) = 61
    c: DistanceY(g0) = 116
    c: DistanceX(g2) = 90
    c: DistanceY(g1) = 31
    c: Angle(g1,g-1) = 0.785398  'angle'
    c: Coincident(g4,g-1)
    c: Parallel(g4,g1)
    c: DistanceX(g4) = 10
    c: Radius(g5) = 2.7
    c: Tangent(g5,g4) = 1.5708
    c: Horizontal(g6)
    c: Tangent(g6,g5) = 1.5708
    c: DistanceX(g6,g6) = 0.1
    c: DistanceX(g6,g5) = 2.00919  'bend_length'
    c: DistanceY(g5,g6) = 0.790812  'bend_height'
    c: DistanceX(g0) = 5
    c: DistanceX(g0) = 0
FEATURE [PartDesign::SubShapeBinder] Binder011
  BindCopyOnChange = 0
  BindMode = 0
  ClaimChildren = true
  Context = -> Body008 [Binder011.]
  Fuse = false
  MakeFace = true
  OffsetFill = false
  OffsetIntersection = false
  OffsetJoinType = 0
  OffsetOpenResult = false
  PartialLoad = false
  Placement = pos=(0,0,0) rot=(0.57735,0.57735,0.57735;2.0944rad)
  Relative = false
  Support = -> [Sketch013]
  _Version = 2
  expr: Placement = <<pump_holder_base_sketch>>.Placement
FEATURE [PartDesign::FeaturePython] BaseBend005  label="pump_holder_BaseBend"  # WARN: FeaturePython — macro-defined, semantics opaque (R4)
  BendSide = 1
  BendSketch = -> Binder011
  MidPlane = true
  Reverse = false
  Suppressed = false
  length = 322
  radius = 2
  thickness = 0.7
FEATURE [Part::FeaturePython] Placment010  # WARN: FeaturePython — macro-defined, semantics opaque (R4)
  AttacherType = Attacher::AttachEngine3D
  AttachmentOffset = pos=(0,0,0) rot=(-0.57735,0.57735,0.57735;2.0944rad)
  AttachmentSupport = -> [Sketch013]
  ExposePlacement = true
  MapMode = 7
  MarkerShape = 1
  MarkerSize = 20
  NumElements = 1
  Placement = pos=(0,151,0) rot=(0,0,1;1.5708rad)
  Type = lattice2AttachablePlacement.AttachablePlacement
  isLattice = 1
FEATURE [Part::FeaturePython] Placment011  # WARN: FeaturePython — macro-defined, semantics opaque (R4)
  AttacherType = Attacher::AttachEngine3D
  AttachmentOffset = pos=(0,0,0) rot=(0.57735,-0.57735,0.57735;2.0944rad)
  AttachmentSupport = -> [Sketch013]
  ExposePlacement = true
  MapMode = 7
  MarkerShape = 1
  MarkerSize = 5
  NumElements = 1
  Placement = pos=(0,0,116) rot=(0.707107,-0.707107,0;3.14159rad)
  Type = lattice2AttachablePlacement.AttachablePlacement
  isLattice = 1
FEATURE [Part::FeaturePython] Join003  # WARN: FeaturePython — macro-defined, semantics opaque (R4)
  ExposePlacement = false
  Interleave = false
  Links = -> [Placment010,Placment011]
  MarkerShape = 1
  MarkerSize = 0
  NumElements = 2
  Type = lattice2JoinArrays.JoinArrays
  isLattice = 1
FEATURE [Part::FeaturePython] Populate012  label="Populate Join003 with Extrude005"  # WARN: FeaturePython — macro-defined, semantics opaque (R4)
  Copying = 0
  ExposePlacement = false
  MarkerShape = 1
  MarkerSize = 0
  NumElements = 0
  Object = -> Extrude005
  OutputCompounding = 1
  Placement = pos=(-161,0,0) rot=(0,0,1;0rad)
  PlacementsTo = -> Join003
  Referencing = 0
  Type = lattice2PopulateCopies.LatticePopulateCopies
  isLattice = 0
  expr: .Placement.Base.x = -<<pump_holder_BaseBend>>.length / 2
FEATURE [Part::FeaturePython] Mirror001  label="Mirror001 of Populate Join003 with Extrude005"  # WARN: FeaturePython — macro-defined, semantics opaque (R4)
  ExposePlacement = false
  FlipX = true
  FlipY = false
  FlipZ = false
  MarkerShape = 1
  MarkerSize = 0
  NumElements = 0
  Object = -> Populate012
  ObjectTraversal = 0
  Type = lattice2Mirror.LatticeMirror
  isLattice = 0
FEATURE [Sketcher::SketchObject] Sketch015
  AttachmentOffset = pos=(161,0,42) rot=(0,0.707107,0.707107;3.14159rad)
  FullyConstrained = true
  MapMode = 7
  Placement = pos=(205,43.3015,70.6985) rot=(0,0.382683,0.92388;3.14159rad)
  expr: .AttachmentOffset.Base.x = <<pump_holder_BaseBend>>.length / 2
  sketch-geometry (8):
    g0: LineSegment StartX=19 StartY=-25 StartZ=0 EndX=19 EndY=0 EndZ=0
    g1: LineSegment StartX=0 StartY=0 StartZ=0 EndX=0 EndY=-35 EndZ=0
    g2: LineSegment StartX=19 StartY=0 StartZ=0 EndX=0 EndY=0 EndZ=0
    g3: GeomPoint X=19 Y=0 Z=0
    g4: LineSegment StartX=5 StartY=-30 StartZ=0 EndX=14 EndY=-30 EndZ=0
    g5: ArcOfCircle CenterX=5 CenterY=-35 CenterZ=0 NormalX=0 NormalY=0 NormalZ=1 AngleXU=0 Radius=5 StartAngle=1.5708 EndAngle=3.14159
    g6: ArcOfCircle CenterX=14 CenterY=-25 CenterZ=0 NormalX=0 NormalY=0 NormalZ=1 AngleXU=0 Radius=5 StartAngle=4.71239 EndAngle=6.28319
    g7: GeomPoint X=19 Y=-30 Z=0
  constraints (20):
    c: Vertical(g0)
    c: Vertical(g1)
    c: DistanceX(g1,g7) = 19
    c: Horizontal(g2)
    c: PointOnObject(g3,g0)
    c: PointOnObject(g3,g2)
    c: Coincident(g1,g2)
    c: Horizontal(g4)
    c: Tangent(g1,g5) = -1.5708
    c: Tangent(g5,g4) = 1.5708
    c: PointOnObject(g1,g-2)
    c: Coincident(g0,g2)
    c: Tangent(g0,g6) = -1.5708
    c: Tangent(g4,g6) = -1.5708
    c: Equal(g6,g5)
    c: Radius(g6) = 5
    c: PointOnObject(g7,g4)
    c: PointOnObject(g7,g0)
    c: DistanceY(g7,g0) = 30
    c: PointOnObject(g0,g-1)
FEATURE [App::FeaturePython] SetupSheet  # Path/CAM operation (typed FeaturePython)
  ClearanceHeightExpression = OpStockZMax+SetupSheet.ClearanceHeightOffset
  ClearanceHeightOffset = 5
  CoolantMode = 0
  CoolantModes = None | Flood | Mist
  FinalDepthExpression = -0.1 mm
  HorizRapid = 0
  ProfileDirection = 1
  ProfileSide = 0
  ProfileUseComp = true
  ProfileprocessCircles = true
  ProfileprocessHoles = true
  ProfileprocessPerimeter = true
  SafeHeightExpression = OpStockZMax+SetupSheet.SafeHeightOffset
  SafeHeightOffset = 3
  StartDepthExpression = 3 mm
  StepDownExpression = 4 mm
  VertRapid = 0
FEATURE [Part::FeaturePython] ToolBit  label="3.175mm Endmill"  # Path/CAM toolbit (typed FeaturePython)
  BitPropertyNames = Chipload | CuttingEdgeHeight | Diameter | Flutes | Length | Material | ShankDiameter | SpindleDirection
  BitShape = <path>
  Chipload = 0
  CuttingEdgeHeight = 30
  Diameter = 3.175
  Flutes = 0
  Length = 10
  Material = 0
  ShankDiameter = 3
  ShapeName = endmill
  SpindleDirection = 0
FEATURE [Path::FeaturePython] __175mm_Endmill  label="3.175mm Endmill001"  # Path/CAM operation (typed FeaturePython)
  HorizFeed = 33.3333
  HorizRapid = 0
  SpindleDir = 0
  SpindleSpeed = 18000
  Tool = -> ToolBit
  ToolNumber = 1
  VertFeed = 8.33333
  VertRapid = 0
  expr: HorizRapid = SetupSheet.HorizRapid
  expr: VertRapid = SetupSheet.VertRapid
FEATURE [App::DocumentObjectGroup] Tools
  Group = -> [__175mm_Endmill]
FEATURE [App::FeaturePython] SetupSheet001  # Path/CAM operation (typed FeaturePython)
  ClearanceHeightExpression = OpStockZMax+SetupSheet001.ClearanceHeightOffset
  ClearanceHeightOffset = 5
  CoolantMode = 0
  CoolantModes = None | Flood | Mist
  DeburrExtraDepth = 0
  DeburrWidth = 2.7
  FinalDepthExpression = 0.6 mm
  HorizRapid = 0
  ProfileDirection = 1
  ProfileprocessCircles = true
  ProfileprocessHoles = true
  ProfileprocessPerimeter = true
  SafeHeightExpression = OpStockZMax+SetupSheet001.SafeHeightOffset
  SafeHeightOffset = 3
  StartDepthExpression = 3 mm
  StepDownExpression = OpToolDiameter
  VertRapid = 0
FEATURE [Part::FeaturePython] ToolBit001  label="NZV6109015"  # Path/CAM toolbit (typed FeaturePython)
  BitPropertyNames = Chipload | CuttingEdgeAngle | CuttingEdgeHeight | Diameter | Flutes | Length | Material | ShankDiameter | TipDiameter
  BitShape = <path>
  Chipload = 0
  CuttingEdgeAngle = 90
  CuttingEdgeHeight = 4
  Diameter = 10
  Flutes = 0
  Length = 50
  Material = 0
  ShankDiameter = 6
  ShapeName = chamfer
  TipDiameter = 1
FEATURE [Path::FeaturePython] NZV6109015  label="NZV6109016"  # Path/CAM operation (typed FeaturePython)
  HorizFeed = 51.6667
  HorizRapid = 0
  SpindleDir = 0
  SpindleSpeed = 18000
  Tool = -> ToolBit001
  ToolNumber = 2
  VertFeed = 16.6667
  VertRapid = 0
  expr: HorizRapid = SetupSheet001.HorizRapid
  expr: VertRapid = SetupSheet001.VertRapid
FEATURE [App::DocumentObjectGroup] Tools001
  Group = -> [NZV6109015]
FEATURE [Part::FeaturePython] Placment012  label="electric_shield_placement"  # WARN: FeaturePython — macro-defined, semantics opaque (R4)
  AttacherType = Attacher::AttachEngine3D
  ExposePlacement = true
  MarkerShape = 1
  MarkerSize = 100
  NumElements = 1
  Placement = pos=(319.563,80,555.5) rot=(0.57735,0.57735,0.57735;2.0944rad)
  Type = lattice2AttachablePlacement.AttachablePlacement
  isLattice = 1
  expr: .Placement.Base.x = <<Dimensions_sketch>>.Constraints.total_width / 2
FEATURE [Sketcher::SketchObject] Sketch016
  ExternalGeometry = -> [Sketch001,Sketch]
  FullyConstrained = true
  sketch-geometry (20):
    g0: LineSegment StartX=319.563 StartY=130 StartZ=0 EndX=319.563 EndY=0 EndZ=0
    g1: LineSegment StartX=166.259 StartY=0.709717 StartZ=0 EndX=318.972 EndY=128.852 EndZ=0
    g2: LineSegment StartX=164.635 StartY=0 StartZ=0 EndX=225.255 EndY=-72.2441 EndZ=0
    g3: LineSegment StartX=225.255 StartY=-72.2441 StartZ=0 EndX=319.563 EndY=-72.2441 EndZ=0
    g4: LineSegment StartX=319.563 StartY=130 StartZ=0 EndX=225.255 EndY=-72.2441 EndZ=0
    g5: LineSegment StartX=166.259 StartY=0.709717 StartZ=0 EndX=175.579 EndY=-10.3979 EndZ=0
    g6: LineSegment StartX=304.472 StartY=97.7563 StartZ=0 EndX=318.972 EndY=128.852 EndZ=0
    g7: LineSegment StartX=164.635 StartY=0 StartZ=0 EndX=165.937 EndY=1.09274 EndZ=0
    g8: LineSegment StartX=165.937 StartY=1.09274 StartZ=0 EndX=166.259 EndY=0.709717 EndZ=0
    g9: LineSegment StartX=175.579 StartY=-10.3979 StartZ=0 EndX=185.871 EndY=-1.76207 EndZ=0
    g10: LineSegment StartX=185.871 StartY=-1.76207 StartZ=0 EndX=178.157 EndY=7.43047 EndZ=0
    g11: LineSegment StartX=178.157 StartY=7.43047 StartZ=0 EndX=190.414 EndY=17.7151 EndZ=0
    g12: LineSegment StartX=190.414 StartY=17.7151 StartZ=0 EndX=198.128 EndY=8.52254 EndZ=0
    g13: LineSegment StartX=298.479 StartY=92.7277 StartZ=0 EndX=304.472 EndY=97.7563 EndZ=0
    g14: LineSegment StartX=290.766 StartY=101.92 StartZ=0 EndX=298.479 EndY=92.7277 EndZ=0
    g15: LineSegment StartX=278.509 StartY=91.6356 StartZ=0 EndX=290.766 EndY=101.92 EndZ=0
    g16: LineSegment StartX=198.128 StartY=8.52254 StartZ=0 EndX=286.223 EndY=82.4431 EndZ=0
    g17: LineSegment StartX=286.223 StartY=82.4431 StartZ=0 EndX=278.509 EndY=91.6356 EndZ=0
    g18: LineSegment StartX=175.08 StartY=8.76442 StartZ=0 EndX=178.157 EndY=7.43047 EndZ=0
    g19: LineSegment StartX=290.766 StartY=101.92 StartZ=0 EndX=289.987 EndY=105.183 EndZ=0
  constraints (56):
    c: Coincident(g0,g-3)
    c: PointOnObject(g0,g-1)
    c: Vertical(g0)
    c: Parallel(g1,g-3)
    c: Coincident(g3,g2)
    c: Horizontal(g3)
    c: PointOnObject(g3,g0)
    c: Perpendicular(g-3,g2)
    c: Equal(g2,g3)
    c: Coincident(g4,g0)
    c: Coincident(g4,g2)
    c: Coincident(g5,g1)
    c: Coincident(g9,g5)
    c: Coincident(g6,g13)
    c: Coincident(g6,g1)
    c: Parallel(g6,g4)
    c: Distance(g13,g4) = 0.05
    c: Coincident(g2,g-3)
    c: Coincident(g2,g7)
    c: PointOnObject(g7,g-3)
    c: Coincident(g7,g8)
    c: Coincident(g8,g1)
    c: Distance(g7) = 1.7
    c: Perpendicular(g7,g8)
    c: Distance(g8) = 0.5
    c: Perpendicular(g1,g5)
    c: Distance(g5,g-3) = 15
    c: Coincident(g9,g10)
    c: Perpendicular(g5,g9)
    c: Coincident(g10,g11)
    c: Coincident(g11,g12)
    c: Perpendicular(g5,g11)
    c: Coincident(g12,g16)
    c: Coincident(g14,g13)
    c: Perpendicular(g5,g13)
    c: Coincident(g15,g14)
    c: Coincident(g17,g15)
    c: Perpendicular(g5,g15)
    c: Coincident(g16,g17)
    c: Perpendicular(g5,g16)
    c: Perpendicular(g17,g15)
    c: Perpendicular(g14,g15)
    c: PointOnObject(g16,g13)
    c: Perpendicular(g10,g11)
    c: Perpendicular(g12,g11)
    c: Distance(g-4,g11) = 3
    c: PointOnObject(g11,g15)
    c: PointOnObject(g9,g16)
    c: Equal(g11,g15)
    c: Coincident(g18,g10)
    c: Coincident(g19,g14)
    c: Coincident(g19,g-4)
    c: Equal(g19,g18)
    c: Distance(g10,g14) = 147
    c: Distance(g11,g15) = 115
    c: Coincident(g18,g-4)
FEATURE [Sketcher::SketchObject] Sketch017
  ExternalGeometry = -> [Sketch001,Sketch]
  FullyConstrained = true
  sketch-geometry (13):
    g0: LineSegment StartX=0 StartY=-0.5 StartZ=0 EndX=0 EndY=-3 EndZ=0
    g1: LineSegment StartX=162.935 StartY=-15 StartZ=0 EndX=162.935 EndY=-0.5 EndZ=0
    g2: LineSegment StartX=162.935 StartY=-0.5 StartZ=0 EndX=0 EndY=-0.5 EndZ=0
    g3: LineSegment StartX=0 StartY=-3 StartZ=0 EndX=2.5 EndY=-3 EndZ=0
    g4: LineSegment StartX=2.5 StartY=-3 StartZ=0 EndX=18.5 EndY=-3 EndZ=0
    g5: LineSegment StartX=18.5 StartY=-3 StartZ=0 EndX=18.5 EndY=-15 EndZ=0
    g6: LineSegment StartX=18.5 StartY=-15 StartZ=0 EndX=133.5 EndY=-15 EndZ=0
    g7: LineSegment StartX=133.5 StartY=-15 StartZ=0 EndX=133.5 EndY=-3 EndZ=0
    g8: LineSegment StartX=133.5 StartY=-3 StartZ=0 EndX=149.5 EndY=-3 EndZ=0
    g9: LineSegment StartX=149.5 StartY=-3 StartZ=0 EndX=149.5 EndY=-15 EndZ=0
    g10: LineSegment StartX=149.5 StartY=-15 StartZ=0 EndX=162.935 EndY=-15 EndZ=0
    g11: LineSegment StartX=151 StartY=0 StartZ=0 EndX=149.5 EndY=-3 EndZ=0
    g12: LineSegment StartX=2.5 StartY=-3 StartZ=0 EndX=1 EndY=0 EndZ=0
  constraints (37):
    c: Coincident(g0,g3)
    c: Coincident(g10,g1)
    c: Coincident(g1,g2)
    c: Coincident(g2,g0)
    c: Vertical(g0)
    c: Vertical(g1)
    c: Horizontal(g2)
    c: PointOnObject(g0,g-2)
    c: DistanceY(g2,g-3) = 0.5
    c: DistanceX(g1,g-3) = 1.7
    c: Horizontal(g3)
    c: Coincident(g4,g5)
    c: Horizontal(g4)
    c: Coincident(g5,g6)
    c: Coincident(g6,g7)
    c: Horizontal(g6)
    c: Coincident(g7,g8)
    c: Coincident(g8,g9)
    c: Horizontal(g8)
    c: Coincident(g9,g10)
    c: Horizontal(g10)
    c: Perpendicular(g5,g4)
    c: Perpendicular(g7,g8)
    c: Perpendicular(g9,g8)
    c: Coincident(g11,g-4)
    c: Coincident(g11,g8)
    c: Coincident(g12,g-4)
    c: Equal(g12,g11)
    c: DistanceY(g4,g12) = 3
    c: Distance(g4,g8) = 147
    c: Equal(g8,g4)
    c: Horizontal(g4,g7)
    c: DistanceX(g4,g7) = 115
    c: Horizontal(g6,g9)
    c: DistanceY(g5) = -15
    c: Coincident(g3,g4)
    c: Coincident(g3,g12)
FEATURE [Sketcher::SketchObject] Sketch019
  ExternalGeometry = -> [Sketch001]
  FullyConstrained = true
  expr: Constraints[3] = 3.4 / 2 + 3 + 1
  sketch-geometry (2):
    g0: LineSegment StartX=319.563 StartY=130 StartZ=0 EndX=319.563 EndY=0 EndZ=0
    g1: Circle CenterX=313.863 CenterY=10 CenterZ=0 NormalX=0 NormalY=0 NormalZ=1 AngleXU=0 Radius=1.7
  constraints (6):
    c: Coincident(g0,g-3)
    c: PointOnObject(g0,g-1)
    c: Vertical(g0)
    c: DistanceX(g1,g0) = 5.7
    c: Diameter(g1) = 3.4
    c: DistanceY(g1) = 10
FEATURE [Sketcher::SketchObject] Sketch021
  ExternalGeometry = -> [Sketch008,Populate002]
  FullyConstrained = true
  expr: Constraints[11] = <<dropper>>#<<fix_sketch>>.Constraints.length
  expr: Constraints[12] = <<dropper>>#<<base>>.Constraints.r * 2
  sketch-geometry (19):
    g0: LineSegment StartX=0 StartY=-10 StartZ=0 EndX=167.341 EndY=-10 EndZ=0
    g1: LineSegment StartX=264.568 StartY=103.413 StartZ=0 EndX=246.496 EndY=103.413 EndZ=0
    g2: LineSegment StartX=154.953 StartY=26.6 StartZ=0 EndX=0 EndY=26.6 EndZ=0
    g3: LineSegment StartX=167.341 StartY=-84.6 StartZ=0 EndX=167.341 EndY=-10 EndZ=0
    g4: LineSegment StartX=167.341 StartY=-10 StartZ=0 EndX=169.27 EndY=-12.2981 EndZ=0
    g5: Ellipse CenterX=246.644 CenterY=86.8285 CenterZ=0 NormalX=0 NormalY=0 NormalZ=1 MajorRadius=19.75 MinorRadius=11.8 AngleXU=0.698132
    g6: LineSegment StartX=261.774 StartY=99.5236 StartZ=0 EndX=231.515 EndY=74.1335 EndZ=0
    g7: LineSegment StartX=239.059 StartY=95.8679 StartZ=0 EndX=254.229 EndY=77.7892 EndZ=0
    g8: GeomPoint X=258.776 Y=97.0086 Z=0
    g9: GeomPoint X=234.512 Y=76.6485 Z=0
    g10: LineSegment StartX=263.568 StartY=94.1261 StartZ=0 EndX=264.568 EndY=94.1261 EndZ=0
    g11: GeomPoint X=263.568 Y=94.1261 Z=0
    g12: LineSegment StartX=239.059 StartY=95.8679 StartZ=0 EndX=238.417 EndY=96.6339 EndZ=0
    g13: LineSegment StartX=254.569 StartY=102.413 StartZ=0 EndX=254.569 EndY=103.413 EndZ=0
    g14: GeomPoint X=254.569 Y=102.413 Z=0
    g15: LineSegment StartX=46 StartY=2 StartZ=0 EndX=46 EndY=25.6 EndZ=0
    g16: LineSegment StartX=154.953 StartY=26.6 StartZ=0 EndX=246.496 EndY=103.413 EndZ=0
    g17: LineSegment StartX=264.568 StartY=103.413 StartZ=0 EndX=264.568 EndY=71.5833 EndZ=0
    g18: LineSegment StartX=264.568 StartY=71.5833 StartZ=0 EndX=167.341 EndY=-10 EndZ=0
  constraints (48):
    c: PointOnObject(g0,g-2)
    c: Horizontal(g0)
    c: Horizontal(g1)
    c: PointOnObject(g2,g-2)
    c: Horizontal(g2)
    c: Coincident(g3,g0)
    c: Coincident(g3,g4)
    c: InternalAlignment(g6-g9 -> g5) x4
    c: Distance(g6) = 39.5
    c: Distance(g7) = 23.6
    c: PointOnObject(g10,g5)
    c: PointOnObject(g11,g5)
    c: PointOnObject(g11,g10)
    c: Perpendicular(g5,g10,g11) = 4.71239
    c: Coincident(g12,g7)
    c: Equal(g12,g10)
    c: PointOnObject(g13,g5)
    c: PointOnObject(g13,g1)
    c: Vertical(g13)
    c: PointOnObject(g14,g5)
    c: PointOnObject(g14,g13)
    c: Perpendicular(g5,g13,g14) = 4.71239
    c: Equal(g13,g12)
    c: Vertical(g15)
    c: Equal(g15,g7)
    c: DistanceY(g15,g2) = 1
    c: Coincident(g2,g16)
    c: Coincident(g16,g1)
    c: PointOnObject(g12,g16)
    c: Perpendicular(g16,g12)
    c: Parallel(g6,g-3)
    c: Coincident(g1,g17)
    c: Vertical(g17)
    c: Coincident(g17,g18)
    c: Coincident(g18,g0)
    c: Coincident(g5,g-4)
    c: PointOnObject(g10,g17)
    c: Perpendicular(g17,g10)
    c: DistanceY(g13,g13) = 1
    c: Parallel(g-3,g18)
    c: Parallel(g16,g-3)
    c: Vertical(g3)
    c: Symmetric(g15,g15,g-5)
    c: Horizontal(g3,g-3)
    c: PointOnObject(g4,g-3)
    c: Perpendicular(g-3,g4)
    c: Distance(g4) = 3
    c: DistanceY(g0) = -10
FEATURE [Sketcher::SketchObject] Sketch020
  ExternalGeometry = -> [Sketch001,Sketch021]
  FullyConstrained = true
  sketch-geometry (10):
    g0: Circle CenterX=175.959 CenterY=2.06142 CenterZ=0 NormalX=0 NormalY=0 NormalZ=1 AngleXU=0 Radius=1.7
    g1: Circle CenterX=252.564 CenterY=66.3402 CenterZ=0 NormalX=0 NormalY=0 NormalZ=1 AngleXU=0 Radius=1.7
    g2: LineSegment StartX=164.635 StartY=0 StartZ=0 EndX=168.299 EndY=-4.36645 EndZ=0
    g3: LineSegment StartX=168.299 StartY=-4.36645 StartZ=0 EndX=175.959 EndY=2.06142 EndZ=0
    g4: LineSegment StartX=175.959 StartY=2.06142 StartZ=0 EndX=252.564 EndY=66.3402 EndZ=0
    g5: LineSegment StartX=248.9 StartY=70.7066 StartZ=0 EndX=252.564 EndY=66.3402 EndZ=0
    g6: LineSegment StartX=252.564 StartY=66.3402 StartZ=0 EndX=264.568 EndY=66.3402 EndZ=0
    g7: Circle CenterX=154.635 CenterY=-5.7 CenterZ=0 NormalX=0 NormalY=0 NormalZ=1 AngleXU=0 Radius=1.7
    g8: Circle CenterX=35 CenterY=-5.7 CenterZ=0 NormalX=0 NormalY=0 NormalZ=1 AngleXU=0 Radius=1.7
    g9: LineSegment StartX=154.635 StartY=0 StartZ=0 EndX=154.635 EndY=-5.7 EndZ=0
  constraints (28):
    c: Diameter(g0) = 3.4
    c: Equal(g0,g1)
    c: Coincident(g-3,g2)
    c: Coincident(g2,g3)
    c: Coincident(g3,g0)
    c: Coincident(g3,g4)
    c: Coincident(g4,g1)
    c: Perpendicular(g3,g2)
    c: Parallel(g3,g4)
    c: Perpendicular(g-3,g2)
    c: Distance(g2,g0) = 10
    c: Distance(g4) = 100
    c: Distance(g2) = 5.7
    c: PointOnObject(g5,g-3)
    c: Coincident(g5,g1)
    c: Coincident(g5,g6)
    c: PointOnObject(g6,g-4)
    c: Horizontal(g6)
    c: Perpendicular(g-3,g5)
    c: PointOnObject(g9,g-1)
    c: Coincident(g9,g7)
    c: Vertical(g9)
    c: Equal(g9,g2)
    c: Equal(g0,g7)
    c: Equal(g7,g8)
    c: Horizontal(g8,g7)
    c: DistanceX(g9,g2) = 10
    c: DistanceX(g8) = 35
FEATURE [Part::Mirroring] Part__Mirroring008  label="Sketch021 (Mirror #9)"
  Base = (0,0,0)
  Normal = (1,0,0)
  Source = -> Sketch021
FEATURE [Part::FeaturePython] Connect006  # WARN: FeaturePython — macro-defined, semantics opaque (R4)
  Objects = -> [Sketch021,Part__Mirroring008]
  Tolerance = 0
FEATURE [Sketcher::SketchObject] Sketch022
  ExternalGeometry = -> [Binder008]
  FullyConstrained = true
  MapMode = 5
  sketch-geometry (5):
    g0: LineSegment StartX=313.563 StartY=108.778 StartZ=0 EndX=313.82 EndY=108.472 EndZ=0
    g1: LineSegment StartX=313.82 StartY=108.472 StartZ=0 EndX=313.563 EndY=108.256 EndZ=0
    g2: LineSegment StartX=313.563 StartY=108.256 StartZ=0 EndX=313.563 EndY=108.778 EndZ=0
    g3: LineSegment StartX=313.563 StartY=108.256 StartZ=0 EndX=313.306 EndY=108.563 EndZ=0
    g4: LineSegment StartX=313.306 StartY=108.563 StartZ=0 EndX=313.563 EndY=108.778 EndZ=0
  constraints (13):
    c: Coincident(g0,g-3)
    c: Coincident(g1,g0)
    c: Coincident(g2,g1)
    c: Coincident(g2,g0)
    c: Vertical(g2)
    c: Distance(g0) = 0.4
    c: Coincident(g1,g3)
    c: PointOnObject(g3,g-3)
    c: Coincident(g3,g4)
    c: Coincident(g4,g0)
    c: Perpendicular(g4,g3)
    c: Perpendicular(g0,g1)
    c: Perpendicular(g0,g4)
FEATURE [Sketcher::SketchObject] Sketch023
  AttachmentSupport = -> [XY_Plane006]
  ExternalGeometry = -> [Binder008]
  FullyConstrained = true
  MapMode = 5
  sketch-geometry (7):
    g0: LineSegment StartX=313.563 StartY=108.778 StartZ=0 EndX=313.563 EndY=127 EndZ=0
    g1: LineSegment StartX=313.563 StartY=127 StartZ=0 EndX=310.563 EndY=127 EndZ=0
    g2: LineSegment StartX=310.563 StartY=127 StartZ=0 EndX=310.563 EndY=106.261 EndZ=0
    g3: LineSegment StartX=310.563 StartY=106.261 StartZ=0 EndX=310.82 EndY=105.955 EndZ=0
    g4: LineSegment StartX=310.82 StartY=105.955 StartZ=0 EndX=313.563 EndY=108.256 EndZ=0
    g5: LineSegment StartX=313.563 StartY=108.256 StartZ=0 EndX=313.563 EndY=108.778 EndZ=0
    g6: LineSegment StartX=313.563 StartY=127 StartZ=0 EndX=313.563 EndY=130 EndZ=0
  constraints (19):
    c: Coincident(g-4,g0)
    c: PointOnObject(g0,g-3)
    c: Coincident(g0,g1)
    c: Coincident(g1,g2)
    c: PointOnObject(g2,g-4)
    c: Vertical(g2)
    c: Coincident(g2,g3)
    c: Coincident(g3,g4)
    c: Coincident(g4,g5)
    c: Coincident(g5,g0)
    c: DistanceY(g0,g-3) = 3
    c: Coincident(g6,g0)
    c: Coincident(g6,g-3)
    c: Equal(g6,g1)
    c: Distance(g3) = 0.4
    c: Vertical(g5)
    c: Horizontal(g1)
    c: Perpendicular(g4,g3)
    c: Perpendicular(g-4,g3)
FEATURE [Sketcher::SketchObject] Sketch024  label="cap_base_sketch"
  ExternalGeometry = -> [Sketch001]
  FullyConstrained = true
  expr: .Constraints.depth = <<Dimensions_sketch>>.Constraints.total_depth + 11 mm
  expr: Constraints[10] = .Constraints.depth / 2 - 0.05 mm
  sketch-geometry (5):
    g0: LineSegment StartX=204.113 StartY=0 StartZ=0 EndX=319.563 EndY=0 EndZ=0
    g1: LineSegment StartX=319.563 StartY=0 StartZ=0 EndX=319.563 EndY=231 EndZ=0
    g2: LineSegment StartX=319.563 StartY=231 StartZ=0 EndX=0 EndY=231 EndZ=0
    g3: GeomPoint X=-204.113 Y=0 Z=0
    g4: GeomPoint X=-319.563 Y=231 Z=0
  constraints (14):
    c: PointOnObject(g0,g-1)
    c: PointOnObject(g0,g-1)
    c: Coincident(g0,g1)
    c: Vertical(g1)
    c: Coincident(g1,g2)
    c: PointOnObject(g2,g-2)
    c: Horizontal(g2)
    c: Symmetric(g3,g0,g-2)
    c: Symmetric(g4,g1,g-2)
    c: DistanceY(g1,g1) = 231  'depth'
    c: DistanceX(g0,g0) = 115.45
    c: DistanceX(g4,g1) = 639.126  'total_width'
    c: PointOnObject(g-3,g1)
    c: DistanceX(g3,g0) = 408.226  'inner_width'
FEATURE [Sketcher::SketchObject] Sketch025
  ExternalGeometry = -> [Sketch024]
  FullyConstrained = true
  Placement = pos=(0,0,0) rot=(0.57735,0.57735,0.57735;2.0944rad)
  expr: Constraints[8] = <<cap_outer_BaseBend>>.length + 0.4 mm
  sketch-geometry (3):
    g0: LineSegment StartX=0 StartY=0 StartZ=0 EndX=0 EndY=50.4 EndZ=0
    g1: LineSegment StartX=0 StartY=50.4 StartZ=0 EndX=231 EndY=50.4 EndZ=0
    g2: LineSegment StartX=231 StartY=50.4 StartZ=0 EndX=231 EndY=0 EndZ=0
  constraints (9):
    c: Coincident(g-1,g0)
    c: PointOnObject(g0,g-2)
    c: Coincident(g0,g1)
    c: Horizontal(g1)
    c: Coincident(g1,g2)
    c: PointOnObject(g2,g-1)
    c: Vertical(g2)
    c: PointOnObject(g-3,g2)
    c: DistanceY(g2,g2) = 50.4
FEATURE [Part::FeaturePython] BaseBend006  # WARN: FeaturePython — macro-defined, semantics opaque (R4)
  BendSide = 0
  BendSketch = -> Sketch025
  MidPlane = true
  Reverse = false
  length = 408.176
  radius = 0.1
  thickness = 0.3
  expr: length = <<cap_base_sketch>>.Constraints.inner_width - 0.05 mm
FEATURE [Part::Mirroring] Part__Mirroring009  label="cap_base_sketch (Mirror #9)"
  Base = (0,0,0)
  Normal = (1,0,0)
  Source = -> Sketch024
FEATURE [Part::FeaturePython] Connect007  # WARN: FeaturePython — macro-defined, semantics opaque (R4)
  Objects = -> [Sketch024,Part__Mirroring009]
  Tolerance = 0
FEATURE [PartDesign::SubShapeBinder] Binder012
  BindCopyOnChange = 0
  BindMode = 0
  ClaimChildren = true
  Context = -> Body010 [Binder012.]
  Fuse = false
  MakeFace = true
  OffsetFill = false
  OffsetIntersection = false
  OffsetJoinType = 0
  OffsetOpenResult = false
  PartialLoad = false
  Relative = false
  Support = -> [Connect007]
  _Version = 2
FEATURE [PartDesign::FeaturePython] BaseBend007  label="cap_outer_BaseBend"  # WARN: FeaturePython — macro-defined, semantics opaque (R4)
  BendSide = 1
  BendSketch = -> Binder012
  MidPlane = false
  Reverse = false
  Suppressed = false
  length = 50
  radius = 0.1
  thickness = 0.3
FEATURE [PartDesign::FeaturePython] Extend002  # WARN: FeaturePython — macro-defined, semantics opaque (R4)
  BaseFeature = -> BaseBend007
  Offset = 0.02
  Refine = true
  Suppressed = false
  UseSubtraction = false
  baseObject = -> BaseBend007 [Face1]
  gap1 = 0
  gap2 = 0
  length = 0
FEATURE [PartDesign::FeaturePython] Bend005  # WARN: FeaturePython — macro-defined, semantics opaque (R4)
  AutoMiter = true
  BaseFeature = -> Extend002
  BendType = 0
  LengthList = [115.5]
  LengthSpec = 1
  ReliefFactor = 0.7
  Suppressed = false
  UseReliefFactor = false
  angle = 90
  baseObject = -> Extend002 [Edge14,Edge29,Edge76,Edge58,Edge73]
  bendAList = [90]
  extend1 = 0
  extend2 = 0
  gap1 = 0
  gap2 = 0
  invert = true
  kfactor = 0.5
  length = 115.5
  maxExtendDist = 5
  minGap = 0.025
  minReliefGap = 0.2
  miterangle1 = 0
  miterangle2 = 0
  offset = 0
  radius = 0.1
  reliefType = 0
  reliefd = 1
  reliefw = 0.8
  sketchflip = false
  sketchinvert = false
  unfold = false
  expr: length = <<cap_base_sketch>>.Constraints.depth / 2
  expr: radius = BaseBend007.radius
FEATURE [PartDesign::Boolean] Boolean008
  BaseFeature = -> Bend005
  Group = -> [BaseBend006]
  Refine = true
  Suppressed = false
  Type = 0
  UsePlacement = true
FEATURE [Sketcher::SketchObject] Sketch026
  ExternalGeometry = -> [Sketch024]
  FullyConstrained = true
  sketch-geometry (14):
    g0: LineSegment StartX=319.563 StartY=231 StartZ=0 EndX=204.063 EndY=115.5 EndZ=0
    g1: LineSegment StartX=204.063 StartY=115.5 StartZ=0 EndX=319.563 EndY=0 EndZ=0
    g2: Circle CenterX=204.063 CenterY=115.5 CenterZ=0 NormalX=0 NormalY=0 NormalZ=1 AngleXU=0 Radius=2
    g3: Circle CenterX=244.063 CenterY=115.5 CenterZ=0 NormalX=0 NormalY=0 NormalZ=1 AngleXU=0 Radius=1.7
    g4: LineSegment StartX=204.063 StartY=115.5 StartZ=0 EndX=204.063 EndY=0 EndZ=0
    g5: LineSegment StartX=204.063 StartY=0 StartZ=0 EndX=261.813 EndY=0 EndZ=0
    g6: LineSegment StartX=261.813 StartY=0 StartZ=0 EndX=319.563 EndY=0 EndZ=0
    g7: LineSegment StartX=204.063 StartY=115.5 StartZ=0 EndX=221.952 EndY=79.7229 EndZ=0
    g8: LineSegment StartX=204.063 StartY=115.5 StartZ=0 EndX=244.063 EndY=115.5 EndZ=0
    g9: LineSegment StartX=204.063 StartY=115.5 StartZ=0 EndX=204.063 EndY=155.5 EndZ=0
    g10: Circle CenterX=204.063 CenterY=155.5 CenterZ=0 NormalX=0 NormalY=0 NormalZ=1 AngleXU=0 Radius=1.7
    g11: Circle CenterX=221.952 CenterY=79.7229 CenterZ=0 NormalX=0 NormalY=0 NormalZ=1 AngleXU=0 Radius=1.7
    g12: LineSegment StartX=204.063 StartY=115.5 StartZ=0 EndX=186.174 EndY=79.7229 EndZ=0
    g13: Circle CenterX=186.174 CenterY=79.7229 CenterZ=0 NormalX=0 NormalY=0 NormalZ=1 AngleXU=0 Radius=1.7
  constraints (34):
    c: Coincident(g-3,g0)
    c: Coincident(g0,g1)
    c: Coincident(g1,g-3)
    c: Equal(g1,g0)
    c: Perpendicular(g0,g1)
    c: Coincident(g2,g0)
    c: Diameter(g2) = 4
    c: Coincident(g4,g2)
    c: PointOnObject(g4,g-1)
    c: Vertical(g4)
    c: Coincident(g5,g4)
    c: Coincident(g6,g5)
    c: Equal(g6,g5)
    c: Coincident(g6,g1)
    c: PointOnObject(g5,g-1)
    c: Coincident(g7,g2)
    c: Coincident(g8,g2)
    c: Coincident(g8,g3)
    c: Horizontal(g8)
    c: Coincident(g9,g2)
    c: Vertical(g9)
    c: Coincident(g10,g9)
    c: Coincident(g11,g7)
    c: PointOnObject(g5,g7)
    c: Equal(g11,g3)
    c: Equal(g11,g10)
    c: Diameter(g11) = 3.4
    c: Equal(g7,g8)
    c: Equal(g8,g9)
    c: DistanceX(g8,g8) = 40
    c: Coincident(g12,g2)
    c: Coincident(g13,g12)
    c: Equal(g13,g11)
    c: Symmetric(g13,g11,g4)
FEATURE [Part::Extrusion] Extrude011
  Base = -> Sketch026
  Dir = (0,0,1)
  DirMode = 2
  FaceMakerClass = Part::FaceMakerBullseye
  LengthFwd = 10
  LengthRev = 0
  Placement = pos=(0,0,44) rot=(0,0,1;0rad)
  Solid = true
  Symmetric = false
  expr: .Placement.Base.z = <<cap_outer_BaseBend>>.length - 6 mm
FEATURE [Sketcher::SketchObject] Sketch027
  FullyConstrained = true
  Placement = pos=(0,0,0) rot=(1,0,0;1.5708rad)
  expr: Constraints[1] = <<cap_base_sketch>>.Constraints.inner_width / 2
  expr: Constraints[2] = <<cap_outer_BaseBend>>.length - 3 mm
  sketch-geometry (7):
    g0: Circle CenterX=194.113 CenterY=10 CenterZ=0 NormalX=0 NormalY=0 NormalZ=1 AngleXU=0 Radius=1.7
    g1: Circle CenterX=214.113 CenterY=10 CenterZ=0 NormalX=0 NormalY=0 NormalZ=1 AngleXU=0 Radius=1.7
    g2: LineSegment StartX=204.113 StartY=0 StartZ=0 EndX=204.113 EndY=10 EndZ=0
    g3: LineSegment StartX=204.113 StartY=10 StartZ=0 EndX=204.113 EndY=37 EndZ=0
    g4: LineSegment StartX=204.113 StartY=37 StartZ=0 EndX=204.113 EndY=47 EndZ=0
    g5: Circle CenterX=214.113 CenterY=37 CenterZ=0 NormalX=0 NormalY=0 NormalZ=1 AngleXU=0 Radius=1.7
    g6: Circle CenterX=194.113 CenterY=37 CenterZ=0 NormalX=0 NormalY=0 NormalZ=1 AngleXU=0 Radius=1.7
  constraints (20):
    c: PointOnObject(g2,g-1)
    c: DistanceX(g4) = 204.113
    c: DistanceY(g4) = 47
    c: Coincident(g2,g3)
    c: Vertical(g2)
    c: Coincident(g3,g4)
    c: Vertical(g3)
    c: Vertical(g4)
    c: Symmetric(g1,g0,g2)
    c: Horizontal(g1,g2)
    c: Vertical(g1,g5)
    c: Symmetric(g5,g6,g3)
    c: Horizontal(g5,g3)
    c: Equal(g5,g6)
    c: Equal(g5,g0)
    c: Equal(g5,g1)
    c: Diameter(g5) = 3.4
    c: DistanceX(g6,g5) = 20
    c: Equal(g2,g4)
    c: DistanceY(g2,g2) = 10
FEATURE [Part::Extrusion] Extrude012
  Base = -> Sketch027
  Dir = (0,-1,2e-16)
  DirMode = 2
  FaceMakerClass = Part::FaceMakerBullseye
  LengthFwd = 10
  LengthRev = 0
  Reversed = true
  Solid = true
  Symmetric = false
FEATURE [Part::Compound] Compound012
  Links = -> [Extrude012,Extrude011]
FEATURE [Part::Mirroring] Part__Mirroring010  label="Extrude011 (Mirror #10)"
  Base = (0,0,0)
  Normal = (1,0,0)
  Source = -> Compound012
FEATURE [Part::Compound] Compound011
  Links = -> [Compound012,Part__Mirroring010]
FEATURE [PartDesign::Boolean] Boolean009
  BaseFeature = -> Boolean008
  Group = -> [Compound011]
  Suppressed = false
  Type = 1
  UsePlacement = true
FEATURE [Sketcher::SketchObject] Sketch028
  ExternalGeometry = -> [Sketch024]
  FullyConstrained = true
  sketch-geometry (6):
    g0: LineSegment StartX=179.563 StartY=163 StartZ=0 EndX=179.563 EndY=3 EndZ=0
    g1: LineSegment StartX=179.563 StartY=3 StartZ=0 EndX=316.563 EndY=3 EndZ=0
    g2: LineSegment StartX=316.563 StartY=3 StartZ=0 EndX=316.563 EndY=163 EndZ=0
    g3: LineSegment StartX=316.563 StartY=163 StartZ=0 EndX=179.563 EndY=163 EndZ=0
    g4: LineSegment StartX=319.563 StartY=0 StartZ=0 EndX=204.063 EndY=115.5 EndZ=0
    g5: LineSegment StartX=204.063 StartY=115.5 StartZ=0 EndX=319.563 EndY=231 EndZ=0
  constraints (17):
    c: Coincident(g0,g1)
    c: Coincident(g1,g2)
    c: Coincident(g2,g3)
    c: Coincident(g3,g0)
    c: Vertical(g0)
    c: Vertical(g2)
    c: Horizontal(g1)
    c: Horizontal(g3)
    c: Coincident(g-3,g4)
    c: Coincident(g4,g5)
    c: Coincident(g5,g-3)
    c: Perpendicular(g5,g4)
    c: Equal(g4,g5)
    c: DistanceX(g1,g4) = 3
    c: DistanceY(g1,g4) = -3
    c: DistanceX(g0,g2) = 137
    c: DistanceY(g0,g2) = 160
FEATURE [PartDesign::SubShapeBinder] Binder013
  BindCopyOnChange = 0
  BindMode = 0
  ClaimChildren = true
  Context = -> Body011 [Binder013.]
  Fuse = false
  MakeFace = true
  OffsetFill = false
  OffsetIntersection = false
  OffsetJoinType = 0
  OffsetOpenResult = false
  PartialLoad = false
  Placement = pos=(0,0,47.1) rot=(0,0,1;0rad)
  Relative = true
  Support = -> [Sketch028]
  _Version = 2
  expr: .Placement.Base.z = <<cap_outer_BaseBend>>.length + <<cap_outer_BaseBend>>.radius - 3 mm
FEATURE [PartDesign::FeaturePython] BaseBend008  # WARN: FeaturePython — macro-defined, semantics opaque (R4)
  BendSide = 0
  BendSketch = -> Binder013
  MidPlane = false
  Reverse = false
  Suppressed = false
  length = 100
  radius = 0.1
  thickness = 0.3
FEATURE [PartDesign::FeaturePython] Bend006  # WARN: FeaturePython — macro-defined, semantics opaque (R4)
  AutoMiter = false
  BaseFeature = -> BaseBend008
  BendType = 1
  LengthList = [47]
  LengthSpec = 0
  ReliefFactor = 0.7
  Suppressed = false
  UseReliefFactor = false
  angle = 90
  baseObject = -> BaseBend008 [Edge7,Edge10]
  bendAList = [90]
  extend1 = 0
  extend2 = 0
  gap1 = 0.4
  gap2 = 3
  invert = true
  kfactor = 0.5
  length = 47
  maxExtendDist = 5
  minGap = 0.2
  minReliefGap = 1
  miterangle1 = 0
  miterangle2 = 0
  offset = 0
  radius = 0.1
  reliefType = 0
  reliefd = 1
  reliefw = 0.8
  sketchflip = false
  sketchinvert = false
  unfold = false
  expr: length = <<cap_outer_BaseBend>>.length - 3 mm
  expr: radius = <<cap_outer_BaseBend>>.radius
FEATURE [Part::Compound] Compound013
  Links = -> [Compound012]
FEATURE [PartDesign::SubShapeBinder] Binder014
  BindCopyOnChange = 0
  BindMode = 0
  ClaimChildren = true
  Context = -> Body011 [Binder014.]
  Fuse = false
  MakeFace = true
  OffsetFill = false
  OffsetIntersection = false
  OffsetJoinType = 0
  OffsetOpenResult = false
  PartialLoad = false
  Relative = true
  Support = -> [Sketch009]
  _Version = 2
FEATURE [Sketcher::SketchObject] Sketch029
  AttachmentOffset = pos=(0,0,316.563) rot=(0,0,1;0rad)
  AttachmentSupport = -> [YZ_Plane011]
  ExternalGeometry = -> [Binder014]
  FullyConstrained = true
  MapMode = 5
  Placement = pos=(316.563,0,0) rot=(0.57735,0.57735,0.57735;2.0944rad)
  expr: .AttachmentOffset.Base.z = <<cap_base_sketch>>.Constraints.total_width / 2 - 3 mm
  sketch-geometry (10):
    g0: LineSegment StartX=30 StartY=0 StartZ=0 EndX=45 EndY=0 EndZ=0
    g1: LineSegment StartX=45 StartY=0 StartZ=0 EndX=45 EndY=-3 EndZ=0
    g2: LineSegment StartX=45 StartY=-3 StartZ=0 EndX=42 EndY=-6 EndZ=0
    g3: LineSegment StartX=42 StartY=-6 StartZ=0 EndX=33 EndY=-6 EndZ=0
    g4: LineSegment StartX=33 StartY=-6 StartZ=0 EndX=30 EndY=-3 EndZ=0
    g5: LineSegment StartX=30 StartY=-3 StartZ=0 EndX=30 EndY=0 EndZ=0
    g6: LineSegment StartX=30 StartY=-3 StartZ=0 EndX=37.5 EndY=-3 EndZ=0
    g7: LineSegment StartX=37.5 StartY=-3 StartZ=0 EndX=45 EndY=-3 EndZ=0
    g8: LineSegment StartX=37.5 StartY=-3 StartZ=0 EndX=42 EndY=-6 EndZ=0
    g9: LineSegment StartX=33 StartY=-6 StartZ=0 EndX=37.5 EndY=-3 EndZ=0
  constraints (25):
    c: Coincident(g0,g-3)
    c: Coincident(g0,g-4)
    c: Coincident(g0,g1)
    c: Vertical(g1)
    c: Coincident(g1,g2)
    c: Coincident(g2,g3)
    c: Horizontal(g3)
    c: Coincident(g3,g4)
    c: Coincident(g4,g5)
    c: Coincident(g5,g0)
    c: Vertical(g5)
    c: Equal(g5,g1)
    c: Coincident(g4,g6)
    c: Horizontal(g6)
    c: Coincident(g6,g7)
    c: Coincident(g7,g1)
    c: Coincident(g6,g8)
    c: Coincident(g8,g2)
    c: Coincident(g3,g9)
    c: Coincident(g9,g6)
    c: Equal(g7,g6)
    c: Equal(g9,g8)
    c: DistanceY(g1,g1) = 3
    c: DistanceY(g2,g1) = 3
    c: Angle(g2) = -2.35619
FEATURE [PartDesign::Pad] Pad001
  BaseFeature = -> Bend006
  Direction = (1,0,0)
  Length = 0.3
  Length2 = 10
  Profile = -> Sketch029
  ReferenceAxis = -> Sketch029 [N_Axis]
  Refine = true
  Reversed = true
  Suppressed = false
  Type = 0
FEATURE [Sketcher::SketchObject] Sketch030
  AttachmentOffset = pos=(0,0,316.563) rot=(0,0,1;0rad)
  ExternalGeometry = -> [Sketch029,Binder013]
  FullyConstrained = true
  MapMode = 5
  Placement = pos=(316.563,0,0) rot=(0.57735,0.57735,0.57735;2.0944rad)
  expr: AttachmentOffset = <<Sketch029>>.AttachmentOffset
  sketch-geometry (3):
    g0: LineSegment StartX=163 StartY=46.7 StartZ=0 EndX=45 EndY=0 EndZ=0
    g1: LineSegment StartX=45 StartY=0 StartZ=0 EndX=163 EndY=0 EndZ=0
    g2: LineSegment StartX=163 StartY=0 StartZ=0 EndX=163 EndY=46.7 EndZ=0
  constraints (8):
    c: Coincident(g0,g-3)
    c: Coincident(g0,g1)
    c: PointOnObject(g1,g-1)
    c: Coincident(g1,g2)
    c: Vertical(g2)
    c: Coincident(g2,g0)
    c: DistanceX(g0,g-4) = 0
    c: DistanceY(g0,g-4) = 0.4
FEATURE [PartDesign::Pocket] Pocket002
  BaseFeature = -> Pad001
  Direction = (-1,-1e-16,1e-16)
  Length = 5
  Length2 = 5
  Profile = -> Sketch030
  ReferenceAxis = -> Sketch030 [N_Axis]
  Suppressed = false
  Type = 0
FEATURE [PartDesign::Boolean] Boolean010
  BaseFeature = -> Pocket002
  Group = -> [Compound013]
  Suppressed = false
  Type = 1
  UsePlacement = true
FEATURE [Sketcher::SketchObject] Sketch031
  AttachmentOffset = pos=(0,813,0) rot=(0,0,1;0rad)
  AttachmentSupport = -> [YZ_Plane001]
  FullyConstrained = true
  MapMode = 5
  Placement = pos=(0,0,813) rot=(0.57735,0.57735,0.57735;2.0944rad)
  expr: .AttachmentOffset.Base.y = <<BaseBend001>>.length
  expr: Constraints[10] = <<back_base_sketch>>.Constraints.side
  sketch-geometry (4):
    g0: LineSegment StartX=3 StartY=0 StartZ=0 EndX=3 EndY=-3 EndZ=0
    g1: LineSegment StartX=3 StartY=-3 StartZ=0 EndX=15 EndY=-3 EndZ=0
    g2: LineSegment StartX=15 StartY=-3 StartZ=0 EndX=15 EndY=0 EndZ=0
    g3: LineSegment StartX=15 StartY=0 StartZ=0 EndX=3 EndY=0 EndZ=0
  constraints (12):
    c: Coincident(g0,g1)
    c: Coincident(g1,g2)
    c: Coincident(g2,g3)
    c: Coincident(g3,g0)
    c: Vertical(g0)
    c: Vertical(g2)
    c: Horizontal(g1)
    c: Horizontal(g3)
    c: PointOnObject(g0,g-1)
    c: DistanceX(g0) = 3
    c: DistanceX(g2) = 15
    c: DistanceY(g0) = -3
FEATURE [Part::FeaturePython] Placment013  label="lamp_holder_placement"  # WARN: FeaturePython — macro-defined, semantics opaque (R4)
  AttacherType = Attacher::AttachEngine3D
  ExposePlacement = true
  MarkerShape = 1
  MarkerSize = 50
  NumElements = 1
  Placement = pos=(0,90,254) rot=(0,0,1;0rad)
  Type = lattice2AttachablePlacement.AttachablePlacement
  isLattice = 1
  expr: .Placement.Base.y = <<Dimensions_sketch>>.Constraints.offset
FEATURE [Part::Box] Box001  label="Cube001"
  AttacherType = Attacher::AttachEngine3D
  Height = 10
  Length = 10
  Placement = pos=(525,15,-5) rot=(0,0,1;0rad)
  Width = 10
  expr: .Placement.Base.x = <<LinearArray004>>.SpanEnd - 5 mm
  expr: .Placement.Base.y = <<LinearArray004>>.Placement.Base.y - 5 mm
FEATURE [Part::FeaturePython] ArrayFilter001  # WARN: FeaturePython — macro-defined, semantics opaque (R4)
  Base = -> LinearArray004
  ExposePlacement = false
  FilterType = 2
  Invert = false
  MarkerShape = 1
  MarkerSize = 5
  NumElements = 1
  Stencil = -> Box001
  Type = lattice2ArrayFilter.LatticeArrayFilter
  WindowFrom = 0
  WindowTo = 1
  isLattice = 1
FEATURE [Part::FeaturePython] Populate016  label="Populate Placment009 with ArrayFilter001"  # WARN: FeaturePython — macro-defined, semantics opaque (R4)
  Copying = 0
  ExposePlacement = false
  MarkerShape = 1
  MarkerSize = 20
  NumElements = 1
  Object = -> ArrayFilter001
  OutputCompounding = 0
  PlacementsTo = -> Placment009
  Referencing = 0
  Type = lattice2PopulateCopies.LatticePopulateCopies
  isLattice = 1
FEATURE [Part::FeaturePython] Populate017  label="Populate Populate Placment009 with ArrayFilter001 with Cylinder002"  # WARN: FeaturePython — macro-defined, semantics opaque (R4)
  Copying = 0
  ExposePlacement = false
  MarkerShape = 1
  MarkerSize = 0
  NumElements = 0
  Object = -> Cylinder002
  OutputCompounding = 1
  PlacementsTo = -> Populate016
  Referencing = 0
  Type = lattice2PopulateCopies.LatticePopulateCopies
  isLattice = 0
FEATURE [Part::Compound] Compound014  label="lamp_holder_face_placement"
  Links = -> [Populate009,Populate017]
FEATURE [Part::Mirroring] Part__Mirroring011  label="lamp_holder_face_placement (Mirror #11)"
  Base = (0,0,0)
  Normal = (1,0,0)
  Source = -> Compound014
FEATURE [Part::Compound] Compound015
  Links = -> [Compound014,Part__Mirroring011]
FEATURE [Part::FeaturePython] Populate015  label="Populate lamp_holder_placement with Compound015"  # WARN: FeaturePython — macro-defined, semantics opaque (R4)
  Copying = 0
  ExposePlacement = false
  MarkerShape = 1
  MarkerSize = 0
  NumElements = 0
  Object = -> Compound015
  OutputCompounding = 2
  PlacementsTo = -> Placment013
  Referencing = 0
  Type = lattice2PopulateCopies.LatticePopulateCopies
  isLattice = 0
FEATURE [Sketcher::SketchObject] Sketch033
  ExternalGeometry = -> [Sketch001]
  FullyConstrained = true
  sketch-geometry (5):
    g0: LineSegment StartX=0 StartY=0 StartZ=0 EndX=200 EndY=0 EndZ=0
    g1: LineSegment StartX=200 StartY=0 StartZ=0 EndX=200 EndY=29.6747 EndZ=0
    g2: LineSegment StartX=200 StartY=29.6747 StartZ=0 EndX=0 EndY=29.6747 EndZ=0
    g3: LineSegment StartX=0 StartY=29.6747 StartZ=0 EndX=0 EndY=0 EndZ=0
    g4: LineSegment StartX=200 StartY=29.6747 StartZ=0 EndX=316.563 EndY=127.483 EndZ=0
  constraints (14):
    c: Coincident(g0,g1)
    c: Coincident(g1,g2)
    c: Coincident(g2,g3)
    c: Coincident(g3,g0)
    c: Horizontal(g0)
    c: Horizontal(g2)
    c: Vertical(g1)
    c: Vertical(g3)
    c: Coincident(g0,g-1)
    c: PointOnObject(g1,g-3)
    c: DistanceX(g0) = 200
    c: Coincident(g4,g1)
    c: PointOnObject(g4,g-3)
    c: DistanceX(g4,g-3) = 3
FEATURE [Sketcher::SketchObject] Sketch032  label="side_cut_sketch"
  AttachmentOffset = pos=(0,0,0) rot=(0,1,0;1.5708rad)
  AttachmentSupport = -> [Sketch001]
  ExternalGeometry = -> [Sketch033]
  FullyConstrained = true
  MapMode = 7
  Placement = pos=(164.635,0,0) rot=(0.889126,0.323616,0.323616;1.68804rad)
  expr: .Constraints.cut_height = <<sink_placement>>.Placement.Base.z + 5 mm
  sketch-geometry (10):
    g0: LineSegment StartX=-1.5 StartY=0 StartZ=0 EndX=198.328 EndY=-7.6e-15 EndZ=0
    g1: LineSegment StartX=-1.5 StartY=150 StartZ=0 EndX=-1.5 EndY=0 EndZ=0
    g2: LineSegment StartX=46.1657 StartY=148 StartZ=0 EndX=10.5778 EndY=145.017 EndZ=0
    g3: ArcOfCircle CenterX=1.5 CenterY=145 CenterZ=0 NormalX=0 NormalY=0 NormalZ=1 AngleXU=0 Radius=5 StartAngle=0.523599 EndAngle=1.5708
    g4: ArcOfCircle CenterX=10.1603 CenterY=150 CenterZ=0 NormalX=0 NormalY=0 NormalZ=1 AngleXU=0 Radius=5 StartAngle=3.66519 EndAngle=4.796
    g5: LineSegment StartX=-1.5 StartY=150 StartZ=0 EndX=1.5 EndY=150 EndZ=0
    g6: LineSegment StartX=0 StartY=145 StartZ=0 EndX=198.328 EndY=145 EndZ=0
    g7: LineSegment StartX=46.1657 StartY=6 StartZ=0 EndX=46.1657 EndY=148 EndZ=0
    g8: LineSegment StartX=198.328 StartY=-7.6e-15 StartZ=0 EndX=198.328 EndY=6 EndZ=0
    g9: LineSegment StartX=198.328 StartY=6 StartZ=0 EndX=46.1657 EndY=6 EndZ=0
  constraints (29):
    c: Coincident(g0,g8)
    c: Vertical(g1)
    c: Coincident(g2,g7)
    c: Tangent(g2,g4) = 1.5708
    c: Tangent(g4,g3) = 1.5708
    c: Coincident(g5,g1)
    c: Horizontal(g5)
    c: Tangent(g3,g5) = 1.5708
    c: PointOnObject(g6,g-2)
    c: Horizontal(g6)
    c: Tangent(g6,g4)
    c: DistanceY(g6) = 145  'cut_height'
    c: PointOnObject(g3,g6)
    c: DistanceX(g5,g5) = 3
    c: Radius(g3) = 5  'big_r'
    c: Radius(g4) = 5  'small_r'
    c: DistanceY(g6,g7) = 3
    c: Coincident(g0,g1)
    c: PointOnObject(g0,g-1)
    c: DistanceX(g0,g-1) = 1.5
    c: Coincident(g9,g7)
    c: Vertical(g7)
    c: Coincident(g8,g9)
    c: Vertical(g8)
    c: PointOnObject(g6,g8)
    c: Vertical(g7,g-3)
    c: DistanceY(g-3,g7) = 6
    c: Horizontal(g9)
    c: Coincident(g0,g-3)
FEATURE [Part::Extrusion] Extrude014
  Base = -> Sketch032
  Dir = (0.642788,-0.766044,0)
  DirMode = 2
  FaceMakerClass = Part::FaceMakerBullseye
  LengthFwd = 1
  LengthRev = 0
  Solid = true
  Symmetric = true
FEATURE [Sketcher::SketchObject] Sketch034
  ExternalGeometry = -> [Sketch001]
  FullyConstrained = true
  Placement = pos=(0,0,0) rot=(1,0,0;1.5708rad)
  expr: .Constraints.cut_height = <<side_cut_sketch>>.Constraints.cut_height
  expr: Constraints[12] = <<side_cut_sketch>>.Constraints.small_r
  sketch-geometry (7):
    g0: LineSegment StartX=166.135 StartY=150 StartZ=0 EndX=163.135 EndY=150 EndZ=0
    g1: LineSegment StartX=0 StartY=0 StartZ=0 EndX=166.135 EndY=0 EndZ=0
    g2: LineSegment StartX=166.135 StartY=0 StartZ=0 EndX=166.135 EndY=150 EndZ=0
    g3: LineSegment StartX=166.135 StartY=145 StartZ=0 EndX=154.475 EndY=145 EndZ=0
    g4: LineSegment StartX=154.475 StartY=145 StartZ=0 EndX=0 EndY=145 EndZ=0
    g5: ArcOfCircle CenterX=154.475 CenterY=150 CenterZ=0 NormalX=0 NormalY=0 NormalZ=1 AngleXU=0 Radius=5 StartAngle=4.71239 EndAngle=5.75959
    g6: ArcOfCircle CenterX=163.135 CenterY=145 CenterZ=0 NormalX=0 NormalY=0 NormalZ=1 AngleXU=0 Radius=5 StartAngle=1.5708 EndAngle=2.61799
  constraints (20):
    c: Horizontal(g0)
    c: PointOnObject(g4,g-2)
    c: Coincident(g-1,g1)
    c: Coincident(g3,g4)
    c: Horizontal(g3)
    c: Horizontal(g4)
    c: PointOnObject(g6,g3)
    c: DistanceY(g3) = 145  'cut_height'
    c: Tangent(g5,g4) = 1.5708
    c: Tangent(g6,g5) = 1.5708
    c: Tangent(g6,g0) = -1.5708
    c: DistanceX(g0,g0) = 3
    c: Radius(g5) = 5
    c: Coincident(g1,g2)
    c: PointOnObject(g1,g-1)
    c: Vertical(g2)
    c: Coincident(g0,g2)
    c: DistanceX(g-3,g1) = 1.5
    c: Radius(g6) = 5
    c: PointOnObject(g3,g2)
FEATURE [Part::Mirroring] Part__Mirroring012  label="Sketch034 (Mirror #12)"
  Base = (0,0,0)
  Normal = (1,0,0)
  Source = -> Sketch034
FEATURE [Part::FeaturePython] Connect008  # WARN: FeaturePython — macro-defined, semantics opaque (R4)
  Objects = -> [Sketch034,Part__Mirroring012]
  Tolerance = 0
FEATURE [Part::Extrusion] Extrude015
  Base = -> Connect008
  Dir = (0,1,0)
  DirMode = 2
  FaceMakerClass = Part::FaceMakerBullseye
  LengthFwd = 0.7
  LengthRev = 0
  Reversed = true
  Solid = true
  Symmetric = true
FEATURE [Part::Mirroring] Part__Mirroring013  label="Extrude014 (Mirror #13)"
  Base = (0,0,0)
  Normal = (1,0,0)
  Source = -> Extrude014
FEATURE [Part::MultiFuse] Fusion
  Placement = pos=(0,90,0) rot=(0,0,1;0rad)
  Refine = true
  Shapes = -> [Extrude014,Extrude015,Part__Mirroring013]
  expr: .Placement.Base.y = <<Dimensions_sketch>>.Constraints.offset
FEATURE [Sketcher::SketchObject] Sketch036
  AttachmentSupport = -> [XY_Plane006]
  ExternalGeometry = -> [Binder008]
  FullyConstrained = true
  MapMode = 5
  sketch-geometry (8):
    g0: LineSegment StartX=83.2492 StartY=-85 StartZ=0 EndX=86.8245 EndY=-82 EndZ=0
    g1: LineSegment StartX=82.0117 StartY=-81.6 StartZ=0 EndX=82.0117 EndY=-85 EndZ=0
    g2: LineSegment StartX=82.0117 StartY=-85 StartZ=0 EndX=83.2492 EndY=-85 EndZ=0
    g3: LineSegment StartX=83.1036 StartY=-85 StartZ=0 EndX=83.1036 EndY=-84.6 EndZ=0
    g4: LineSegment StartX=83.1036 StartY=-84.6 StartZ=0 EndX=83.3608 EndY=-84.9064 EndZ=0
    g5: LineSegment StartX=82.0117 StartY=-81.6 StartZ=0 EndX=83.2492 EndY=-85 EndZ=0
    g6: LineSegment StartX=86.8245 StartY=-82 StartZ=0 EndX=86.5674 EndY=-81.6936 EndZ=0
    g7: LineSegment StartX=86.5674 StartY=-81.6936 StartZ=0 EndX=82.0117 EndY=-81.6 EndZ=0
  constraints (23):
    c: Coincident(g7,g1)
    c: Vertical(g1)
    c: Coincident(g1,g2)
    c: Coincident(g2,g0)
    c: Horizontal(g2)
    c: Parallel(g0,g-3)
    c: DistanceY(g1,g1) = 3.4
    c: Distance(g0,g-3) = 0.4
    c: PointOnObject(g3,g2)
    c: Coincident(g3,g-3)
    c: Coincident(g3,g4)
    c: PointOnObject(g4,g0)
    c: Equal(g3,g4)
    c: Vertical(g3)
    c: Perpendicular(g-3,g4)
    c: Coincident(g5,g1)
    c: Coincident(g5,g0)
    c: PointOnObject(g3,g5)
    c: DistanceY(g0,g6) = 3
    c: Coincident(g0,g6)
    c: Coincident(g6,g7)
    c: Perpendicular(g-3,g6)
    c: PointOnObject(g6,g-3)
FEATURE [Sketcher::SketchObject] Sketch037
  FullyConstrained = true
  sketch-geometry (9):
    g0: LineSegment StartX=-24 StartY=-17 StartZ=0 EndX=24 EndY=-17 EndZ=0
    g1: LineSegment StartX=24 StartY=-17 StartZ=0 EndX=24 EndY=17 EndZ=0
    g2: LineSegment StartX=24 StartY=17 StartZ=0 EndX=-24 EndY=17 EndZ=0
    g3: LineSegment StartX=-24 StartY=17 StartZ=0 EndX=-24 EndY=-17 EndZ=0
    g4: GeomPoint X=0 Y=0 Z=0
    g5: Circle CenterX=24 CenterY=17 CenterZ=0 NormalX=0 NormalY=0 NormalZ=1 AngleXU=0 Radius=1.7
    g6: Circle CenterX=24 CenterY=-17 CenterZ=0 NormalX=0 NormalY=0 NormalZ=1 AngleXU=0 Radius=1.7
    g7: Circle CenterX=-24 CenterY=-17 CenterZ=0 NormalX=0 NormalY=0 NormalZ=1 AngleXU=0 Radius=1.7
    g8: Circle CenterX=-24 CenterY=17 CenterZ=0 NormalX=0 NormalY=0 NormalZ=1 AngleXU=0 Radius=1.7
  constraints (20):
    c: Coincident(g0,g1)
    c: Coincident(g1,g2)
    c: Coincident(g2,g3)
    c: Coincident(g3,g0)
    c: Horizontal(g0)
    c: Horizontal(g2)
    c: Vertical(g1)
    c: Vertical(g3)
    c: Symmetric(g2,g0,g4)
    c: Coincident(g4,g-1)
    c: Coincident(g5,g1)
    c: Coincident(g6,g0)
    c: Coincident(g7,g0)
    c: Coincident(g8,g2)
    c: Equal(g8,g5)
    c: Equal(g8,g6)
    c: Equal(g8,g7)
    c: Diameter(g8) = 3.4
    c: DistanceX(g0,g0) = 48
    c: DistanceY(g1,g1) = 34
FEATURE [Part::FeaturePython] Placment014  # WARN: FeaturePython — macro-defined, semantics opaque (R4)
  AttacherType = Attacher::AttachEngine3D
  AttachmentOffset = pos=(-111,0,0) rot=(-0.57735,-0.57735,-0.57735;2.0944rad)
  ExposePlacement = true
  MapMode = 45
  MarkerShape = 1
  MarkerSize = 20
  NumElements = 1
  Placement = pos=(111,120.5,0) rot=(0,0,1;1.5708rad)
  Type = lattice2AttachablePlacement.AttachablePlacement
  isLattice = 1
  expr: .AttachmentOffset.Base.x = -(<<pump_holder_BaseBend>>.length / 2 - 50 mm)
FEATURE [Part::Extrusion] Extrude016
  Base = -> Sketch037
  Dir = (0,0,1)
  DirMode = 2
  FaceMakerClass = Part::FaceMakerBullseye
  LengthFwd = 10
  LengthRev = 0
  Solid = true
  Symmetric = false
FEATURE [Part::FeaturePython] Populate018  label="Populate Placment014 with Extrude016"  # WARN: FeaturePython — macro-defined, semantics opaque (R4)
  Copying = 0
  ExposePlacement = false
  MarkerShape = 1
  MarkerSize = 0
  NumElements = 0
  Object = -> Extrude016
  OutputCompounding = 2
  PlacementsTo = -> Placment014
  Referencing = 0
  Type = lattice2PopulateCopies.LatticePopulateCopies
  isLattice = 0
FEATURE [Sketcher::SketchObject] Sketch038
  FullyConstrained = true
  sketch-geometry (2):
    g0: Circle CenterX=0 CenterY=-74 CenterZ=0 NormalX=0 NormalY=0 NormalZ=1 AngleXU=0 Radius=2
    g1: Circle CenterX=0 CenterY=74 CenterZ=0 NormalX=0 NormalY=0 NormalZ=1 AngleXU=0 Radius=2
  constraints (5):
    c: PointOnObject(g1,g-2)
    c: Symmetric(g1,g0,g-1)
    c: DistanceY(g0,g1) = 148
    c: Equal(g1,g0)
    c: Diameter(g1) = 4
FEATURE [Part::Extrusion] Extrude017
  Base = -> Sketch038
  Dir = (0,0,1)
  DirMode = 2
  FaceMakerClass = Part::FaceMakerBullseye
  LengthFwd = 10
  LengthRev = 0
  Solid = true
  Symmetric = false
FEATURE [Part::FeaturePython] Placment015  # WARN: FeaturePython — macro-defined, semantics opaque (R4)
  AttacherType = Attacher::AttachEngine3D
  AttachmentOffset = pos=(-40,1,0) rot=(0.57735,-0.57735,0.57735;2.0944rad)
  AttachmentSupport = -> [Sketch013]
  ExposePlacement = true
  MapMode = 45
  MarkerShape = 1
  MarkerSize = 20
  NumElements = 1
  Placement = pos=(-40,91,15.5) rot=(0.57735,-0.57735,0.57735;2.0944rad)
  Type = lattice2AttachablePlacement.AttachablePlacement
  isLattice = 1
FEATURE [Part::FeaturePython] Populate019  label="Populate Placment015 with Extrude017"  # WARN: FeaturePython — macro-defined, semantics opaque (R4)
  Copying = 0
  ExposePlacement = false
  MarkerShape = 1
  MarkerSize = 0
  NumElements = 0
  Object = -> Extrude017
  OutputCompounding = 2
  PlacementsTo = -> Placment015
  Referencing = 0
  Type = lattice2PopulateCopies.LatticePopulateCopies
  isLattice = 0
FEATURE [Sketcher::SketchObject] Sketch039
  AttachmentOffset = pos=(0,0,69.9077) rot=(0,0,1;0rad)
  ExternalGeometry = -> [Sketch015]
  FullyConstrained = true
  MapMode = 5
  Placement = pos=(0,0,69.9077) rot=(0,0,1;0rad)
  expr: .AttachmentOffset.Base.z = <<Sketch015>>.Placement.Base.z - <<pump_holder_base_sketch>>.Constraints.bend_height
  expr: Constraints[21] = <<pump_holder_base_sketch>>.Constraints.bend_length
  sketch-geometry (12):
    g0: LineSegment StartX=187 StartY=45.3107 StartZ=0 EndX=187 EndY=62.4357 EndZ=0
    g1: LineSegment StartX=190.75 StartY=62.4357 StartZ=0 EndX=190.75 EndY=56.3107 EndZ=0
    g2: LineSegment StartX=205 StartY=45.3107 StartZ=0 EndX=205 EndY=62.4357 EndZ=0
    g3: LineSegment StartX=201.25 StartY=62.4357 StartZ=0 EndX=201.25 EndY=56.3107 EndZ=0
    g4: ArcOfCircle CenterX=196 CenterY=56.3107 CenterZ=0 NormalX=0 NormalY=0 NormalZ=1 AngleXU=0 Radius=5.25 StartAngle=3.14159 EndAngle=6.28319
    g5: ArcOfCircle CenterX=203.125 CenterY=62.4357 CenterZ=0 NormalX=0 NormalY=0 NormalZ=1 AngleXU=0 Radius=1.875 StartAngle=-9e-16 EndAngle=3.14159
    g6: ArcOfCircle CenterX=188.875 CenterY=62.4357 CenterZ=0 NormalX=0 NormalY=0 NormalZ=1 AngleXU=0 Radius=1.875 StartAngle=-1.8e-15 EndAngle=3.14159
    g7: LineSegment StartX=203.125 StartY=64.3107 StartZ=0 EndX=188.875 EndY=64.3107 EndZ=0
    g8: LineSegment StartX=205 StartY=45.3107 StartZ=0 EndX=187 EndY=45.3107 EndZ=0
    g9: LineSegment StartX=186 StartY=43.3015 StartZ=0 EndX=186 EndY=45.3107 EndZ=0
    g10: LineSegment StartX=186 StartY=45.3107 StartZ=0 EndX=187 EndY=45.3107 EndZ=0
    g11: LineSegment StartX=205 StartY=43.3015 StartZ=0 EndX=205 EndY=45.3107 EndZ=0
  constraints (30):
    c: Tangent(g4,g3) = 1.5708
    c: Tangent(g4,g1) = -1.5708
    c: Tangent(g6,g0) = 1.5708
    c: Tangent(g6,g1) = 1.5708
    c: Tangent(g5,g3) = -1.5708
    c: Tangent(g5,g2) = -1.5708
    c: Equal(g6,g5)
    c: Diameter(g4) = 10.5
    c: Tangent(g7,g5) = -1.5708
    c: Coincident(g0,g8)
    c: Distance(g4,g7) = 8
    c: Parallel(g2,g0)
    c: Parallel(g0,g3)
    c: Parallel(g3,g1)
    c: Perpendicular(g2,g7)
    c: Perpendicular(g2,g8)
    c: Tangent(g7,g6) = -1.5708
    c: Coincident(g2,g8)
    c: Coincident(g-3,g9)
    c: Coincident(g9,g10)
    c: Coincident(g10,g0)
    c: DistanceY(g9,g9) = 2.00919
    c: Perpendicular(g10,g9)
    c: Parallel(g10,g8)
    c: Coincident(g11,g-3)
    c: Coincident(g2,g11)
    c: Equal(g11,g9)
    c: Parallel(g11,g9)
    c: Distance(g10) = 1
    c: Distance(g4,g8) = 11
FEATURE [Sketcher::SketchObject] Sketch040
  AttachmentOffset = pos=(0,0,0) rot=(1,0,0;1.5708rad)
  AttachmentSupport = -> [Binder011]
  FullyConstrained = true
  MapMode = 7
  Placement = pos=(0,90,31) rot=(1,0,0;2.35619rad)
  sketch-geometry (4):
    g0: ArcOfCircle CenterX=140 CenterY=18 CenterZ=0 NormalX=0 NormalY=0 NormalZ=1 AngleXU=0 Radius=1.5 StartAngle=3.14159 EndAngle=6.28319
    g1: ArcOfCircle CenterX=140 CenterY=21 CenterZ=0 NormalX=0 NormalY=0 NormalZ=1 AngleXU=0 Radius=1.5 StartAngle=1.1e-15 EndAngle=3.14159
    g2: LineSegment StartX=138.5 StartY=18 StartZ=0 EndX=138.5 EndY=21 EndZ=0
    g3: LineSegment StartX=141.5 StartY=18 StartZ=0 EndX=141.5 EndY=21 EndZ=0
  constraints (10):
    c: Tangent(g0,g2) = 1.5708
    c: Tangent(g0,g3) = -1.5708
    c: Tangent(g1,g2) = 1.5708
    c: Tangent(g1,g3) = -1.5708
    c: Equal(g0,g1)
    c: Vertical(g3)
    c: Radius(g1) = 1.5
    c: DistanceY(g3,g3) = 3
    c: DistanceX(g0) = 140
    c: DistanceY(g0) = 18
FEATURE [PartDesign::LinearPattern] LinearPattern
  Direction = -> Sketch040 [H_Axis]
  Length = 13
  Mode = 0
  Occurrences = 2
  Offset = 13
  Suppressed = false
FEATURE [PartDesign::LinearPattern] LinearPattern001
  Direction = -> Sketch040 [V_Axis]
  Length = 88
  Mode = 0
  Occurrences = 2
  Offset = 88
  Suppressed = false
FEATURE [Sketcher::SketchObject] Sketch041
  AttachmentSupport = -> [YZ_Plane008]
  ExternalGeometry = -> [Binder011,Sketch039]
  FullyConstrained = true
  MapMode = 5
  Placement = pos=(0,0,0) rot=(0.57735,0.57735,0.57735;2.0944rad)
  sketch-geometry (1):
    g0: LineSegment StartX=5 StartY=116 StartZ=0 EndX=5 EndY=0 EndZ=0
  constraints (5):
    c: Coincident(g0,g-3)
    c: PointOnObject(g0,g-1)
    c: Vertical(g0)
    c: Distance(g-4,g0) = 57.4357
    c: Distance(g-5,g0) = 46.0607
FEATURE [TechDraw::DrawSVGTemplate] Template
  Height = 210
  Orientation = 1
  Template = <path>
  Width = 297
FEATURE [TechDraw::DrawViewPart] View002
  CoarseView = false
  Direction = (0,0,1)
  Focus = 100
  HardHidden = false
  IsoCount = 0
  IsoHidden = false
  IsoVisible = false
  LockPosition = false
  Perspective = false
  Rotation = 0
  ScaleType = 0
  ScrubCount = 0
  SeamHidden = false
  SeamVisible = true
  SmoothHidden = false
  SmoothVisible = true
  Source = -> [Boolean003]
  X = 159.627
  XDirection = (1,0,0)
  Y = 94.8196
FEATURE [PartDesign::SubShapeBinder] Binder015
  BindCopyOnChange = 0
  BindMode = 0
  ClaimChildren = true
  Context = -> Body012 [Binder015.]
  Fuse = false
  MakeFace = true
  OffsetFill = false
  OffsetIntersection = false
  OffsetJoinType = 0
  OffsetOpenResult = false
  PartialLoad = false
  Relative = false
  Support = -> [Sketch001]
  _Version = 2
FEATURE [Part::Cylinder] Cylinder003  label="hole_3.4mm"
  Angle = 360
  AttacherType = Attacher::AttachEngine3D
  FirstAngle = 0
  Height = 9
  Radius = 1.7
  SecondAngle = 0
FEATURE [PartDesign::CoordinateSystem] Local_CS
  AttacherType = Attacher::AttachEngine3D
  AttachmentOffset = pos=(0,0,0) rot=(0,1,0;1.5708rad)
  AttachmentSupport = -> [Binder015]
  MapMode = 7
  Placement = pos=(164.635,0,0) rot=(0.889126,0.323616,0.323616;1.68804rad)
FEATURE [PartDesign::CoordinateSystem] Local_CS001
  AttacherType = Attacher::AttachEngine3D
  AttachmentOffset = pos=(0,0,0) rot=(1,0,0;0.152649rad)
  AttachmentSupport = -> [XY_Plane012]
  MapMode = 5
  Placement = pos=(0,0,0) rot=(1,0,0;0.152649rad)
  expr: .AttachmentOffset.Rotation.Angle = <<sink_front_bend_sketch>>.Constraints.angle
FEATURE [PartDesign::CoordinateSystem] Local_CS004  label="sink_LCS"
  AttacherType = Attacher::AttachEngine3D
  AttachmentSupport = -> [XY_Plane012]
  MapMode = 5
FEATURE [Part::FeaturePython] Placment018  # WARN: FeaturePython — macro-defined, semantics opaque (R4)
  AttacherType = Attacher::AttachEngine3D
  ExposePlacement = true
  MarkerShape = 1
  MarkerSize = 20
  NumElements = 1
  Placement = pos=(0,0.5,73) rot=(1,0,0;1.5708rad)
  Type = lattice2AttachablePlacement.AttachablePlacement
  isLattice = 1
FEATURE [Sketcher::SketchObject] Sketch005  label="sink_side_line"
  AttachmentSupport = -> [Local_CS]
  ExternalGeometry = -> [Binder015]
  FullyConstrained = true
  MapMode = 5
  Placement = pos=(164.635,0,0) rot=(0.889126,0.323616,0.323616;1.68804rad)
  sketch-geometry (1):
    g0: LineSegment StartX=-2.84e-14 StartY=0 StartZ=0 EndX=202.244 EndY=20 EndZ=0
  constraints (4):
    c: Coincident(g0,g-3)
    c: Vertical(g0,g-3)
    c: DistanceY(g0) = 20  'height'
    c: Angle(g0) = 0.0985699  'angle'
FEATURE [Sketcher::SketchObject] Sketch006  label="sink_front_bend_sketch"
  AttachmentSupport = -> [YZ_Plane012]
  ExternalGeometry = -> [Sketch005]
  FullyConstrained = true
  MapMode = 5
  Placement = pos=(0,0,0) rot=(0.57735,0.57735,0.57735;2.0944rad)
  sketch-geometry (3):
    g0: LineSegment StartX=0 StartY=2.91403 StartZ=0 EndX=-4e-15 EndY=0 EndZ=0
    g1: LineSegment StartX=-4e-15 StartY=0 StartZ=0 EndX=2.88014 EndY=0.443099 EndZ=0
    g2: ArcOfCircle CenterX=2.5 CenterY=2.91403 CenterZ=0 NormalX=0 NormalY=0 NormalZ=1 AngleXU=0 Radius=2.5 StartAngle=3.14159 EndAngle=4.86504
  constraints (8):
    c: PointOnObject(g0,g-2)
    c: Coincident(g0,g-3)
    c: Coincident(g0,g1)
    c: Tangent(g2,g1) = -1.5708
    c: Tangent(g2,g0) = -1.5708
    c: Radius(g2) = 2.5
    c: Angle(g1) = 0.152649  'angle'
    c: PointOnObject(g1,g-3)
FEATURE [Sketcher::SketchObject] Sketch044
  AttachmentSupport = -> [Sketch005]
  ExternalGeometry = -> [Binder015]
  FullyConstrained = true
  MapMode = 7
  Placement = pos=(164.635,0,-1.8e-15) rot=(0.846388,-0.394677,-0.357572;1.83324rad)
  sketch-geometry (3):
    g0: ArcOfCircle CenterX=-2.5 CenterY=2.81034 CenterZ=0 NormalX=0 NormalY=0 NormalZ=1 AngleXU=0 Radius=2.5 StartAngle=4.59564 EndAngle=6.28319
    g1: LineSegment StartX=-2.79121 StartY=0.327355 StartZ=0 EndX=0 EndY=0 EndZ=0
    g2: LineSegment StartX=0 StartY=0 StartZ=0 EndX=0 EndY=2.81034 EndZ=0
  constraints (7):
    c: PointOnObject(g0,g-2)
    c: Coincident(g1,g-1)
    c: Coincident(g2,g1)
    c: Tangent(g2,g0) = -1.5708
    c: Tangent(g1,g0) = -1.5708
    c: PointOnObject(g0,g-3)
    c: Radius(g0) = 2.5
FEATURE [Sketcher::SketchObject] Sketch045  label="sink_plane_sketch"
  AttachmentSupport = -> [Local_CS001]
  ExternalGeometry = -> [Sketch006,Sketch005,Sketch044]
  FullyConstrained = true
  MapMode = 5
  Placement = pos=(0,0,0) rot=(1,0,0;0.152649rad)
  sketch-geometry (4):
    g0: LineSegment StartX=-163.725 StartY=2.91403 StartZ=0 EndX=163.725 EndY=2.91403 EndZ=0
    g1: LineSegment StartX=163.725 StartY=2.91403 StartZ=0 EndX=317.576 EndY=133.529 EndZ=0
    g2: LineSegment StartX=317.576 StartY=133.529 StartZ=0 EndX=-317.576 EndY=133.529 EndZ=0
    g3: LineSegment StartX=-317.576 StartY=133.529 StartZ=0 EndX=-163.725 EndY=2.91403 EndZ=0
  constraints (14):
    c: Coincident(g0,g1)
    c: Coincident(g1,g2)
    c: Coincident(g2,g3)
    c: Coincident(g3,g0)
    c: Symmetric(g0,g0,g-2)
    c: Symmetric(g2,g1,g-2)
    c: Parallel(g1,g-4)
    c: PointOnObject(g-5,g1)
    c: PointOnObject(g-3,g0)
    c: Distance(g1) = 201.818  'rigth_side'
    c: Distance(g0) = 327.45  'front'
    c: Distance(g2) = 635.153  'end'
    c: Distance(g3) = 201.818  'left_side'
    c: DistanceY(g-4,g1) = 2
FEATURE [PartDesign::Pad] Pad003
  Direction = (0,-0.152057,0.988372)
  Length = 0.5
  Length2 = 10
  Placement = pos=(0,0,0) rot=(1,0,0;0.152649rad)
  Profile = -> Sketch045
  ReferenceAxis = -> Sketch045 [N_Axis]
  Suppressed = false
  Type = 0
FEATURE [Sketcher::SketchObject] Sketch046
  AttachmentSupport = -> [Sketch006]
  ExternalGeometry = -> [Sketch006]
  FullyConstrained = true
  MapMode = 2
  Placement = pos=(0,0,0) rot=(0.57735,0.57735,0.57735;2.0944rad)
  sketch-geometry (4):
    g0: ArcOfCircle CenterX=2.5 CenterY=2.91403 CenterZ=0 NormalX=0 NormalY=0 NormalZ=1 AngleXU=0 Radius=2.5 StartAngle=3.14159 EndAngle=4.86504
    g1: LineSegment StartX=2.88014 StartY=0.443099 StartZ=0 EndX=2.80411 EndY=0.937285 EndZ=0
    g2: LineSegment StartX=0 StartY=2.91403 StartZ=0 EndX=0.5 EndY=2.91403 EndZ=0
    g3: ArcOfCircle CenterX=2.5 CenterY=2.91403 CenterZ=0 NormalX=0 NormalY=0 NormalZ=1 AngleXU=0 Radius=2 StartAngle=3.14159 EndAngle=4.86504
  constraints (10):
    c: Coincident(g0,g-3)
    c: Tangent(g0,g-3) = -1.5708
    c: Coincident(g0,g1)
    c: Coincident(g0,g2)
    c: Coincident(g3,g0)
    c: Coincident(g3,g2)
    c: Coincident(g3,g1)
    c: Perpendicular(g3,g1)
    c: Distance(g1) = 0.5
    c: Perpendicular(g3,g2)
FEATURE [Sketcher::SketchObject] Sketch047
  AttachmentSupport = -> [Sketch045]
  ExternalGeometry = -> [Sketch044]
  FullyConstrained = true
  MapMode = 7
  Placement = pos=(163.725,2.88014,0.443099) rot=(0.846388,-0.394677,-0.357572;1.83324rad)
  sketch-geometry (4):
    g0: ArcOfCircle CenterX=0.291206 CenterY=2.48298 CenterZ=0 NormalX=0 NormalY=0 NormalZ=1 AngleXU=0 Radius=2.5 StartAngle=4.59564 EndAngle=6.28319
    g1: LineSegment StartX=3.47e-14 StartY=1.55e-14 StartZ=0 EndX=0.0582413 EndY=0.496596 EndZ=0
    g2: LineSegment StartX=2.79121 StartY=2.48298 StartZ=0 EndX=2.29121 EndY=2.48298 EndZ=0
    g3: ArcOfCircle CenterX=0.291206 CenterY=2.48298 CenterZ=0 NormalX=0 NormalY=0 NormalZ=1 AngleXU=0 Radius=2 StartAngle=4.59564 EndAngle=6.28319
  constraints (10):
    c: Coincident(g0,g-3)
    c: Tangent(g0,g-3) = -1.5708
    c: Coincident(g1,g0)
    c: Coincident(g2,g0)
    c: Coincident(g3,g0)
    c: Coincident(g3,g1)
    c: Coincident(g3,g2)
    c: Distance(g1) = 0.5
    c: Perpendicular(g3,g1)
    c: Perpendicular(g3,g2)
FEATURE [PartDesign::Pad] Pad004
  BaseFeature = -> Pad003
  Direction = (-0.762326,-0.639667,-0.0984104)
  Length = 201.818
  Length2 = 10
  Placement = pos=(0,0,0) rot=(1,0,0;0.152649rad)
  Profile = -> Sketch047
  ReferenceAxis = -> Sketch047 [N_Axis]
  Reversed = true
  Suppressed = false
  Type = 0
  expr: Length = <<sink_plane_sketch>>.Constraints.rigth_side
FEATURE [Sketcher::SketchObject] Sketch048
  AttachmentSupport = -> [Sketch045]
  ExternalGeometry = -> [Sketch045]
  FullyConstrained = true
  MapMode = 7
  Placement = pos=(-163.725,2.88014,0.443099) rot=(-0.298783,0.640743,0.707232;3.7787rad)
  sketch-geometry (4):
    g0: ArcOfCircle CenterX=0.291206 CenterY=2.48298 CenterZ=0 NormalX=0 NormalY=0 NormalZ=1 AngleXU=0 Radius=2 StartAngle=4.59564 EndAngle=6.28319
    g1: ArcOfCircle CenterX=0.291206 CenterY=2.48298 CenterZ=0 NormalX=0 NormalY=0 NormalZ=1 AngleXU=0 Radius=2.5 StartAngle=4.59564 EndAngle=6.28319
    g2: LineSegment StartX=-4e-16 StartY=0 StartZ=0 EndX=0.0582413 EndY=0.496596 EndZ=0
    g3: LineSegment StartX=2.29121 StartY=2.48298 StartZ=0 EndX=2.79121 EndY=2.48298 EndZ=0
  constraints (12):
    c: Coincident(g1,g0)
    c: Coincident(g1,g-1)
    c: Coincident(g2,g1)
    c: Coincident(g2,g0)
    c: Coincident(g3,g0)
    c: Coincident(g3,g1)
    c: Perpendicular(g0,g3)
    c: Perpendicular(g0,g2)
    c: Perpendicular(g2,g-3)
    c: Horizontal(g3)
    c: Radius(g0) = 2
    c: Distance(g2) = 0.5
FEATURE [PartDesign::Pad] Pad005
  BaseFeature = -> Pad004
  Direction = (-0.762326,0.639667,0.0984104)
  Length = 201.818
  Length2 = 10
  Placement = pos=(0,0,0) rot=(1,0,0;0.152649rad)
  Profile = -> Sketch048
  ReferenceAxis = -> Sketch048 [N_Axis]
  Suppressed = false
  Type = 0
  expr: Length = <<sink_plane_sketch>>.Constraints.left_side
FEATURE [PartDesign::Pad] Pad006
  BaseFeature = -> Pad005
  Direction = (1,0,0)
  Length = 327.45
  Length2 = 10
  Midplane = true
  Placement = pos=(0,0,0) rot=(1,0,0;0.152649rad)
  Profile = -> Sketch046
  ReferenceAxis = -> Sketch046 [N_Axis]
  Suppressed = false
  Type = 0
  expr: Length = <<sink_plane_sketch>>.Constraints.front
FEATURE [Sketcher::SketchObject] Sketch050
  AttachmentSupport = -> [XZ_Plane012]
  ExternalGeometry = -> [Sketch045,Sketch046]
  FullyConstrained = true
  MapMode = 5
  Placement = pos=(0,0,0) rot=(1,0,0;1.5708rad)
  sketch-geometry (6):
    g0: LineSegment StartX=-163.725 StartY=2.91403 StartZ=0 EndX=-163.725 EndY=80 EndZ=0
    g1: LineSegment StartX=-163.725 StartY=80 StartZ=0 EndX=163.725 EndY=80 EndZ=0
    g2: LineSegment StartX=163.725 StartY=80 StartZ=0 EndX=163.725 EndY=2.91403 EndZ=0
    g3: LineSegment StartX=163.725 StartY=2.91403 StartZ=0 EndX=-163.725 EndY=2.91403 EndZ=0
    g4: LineSegment StartX=-163.725 StartY=0.443099 StartZ=0 EndX=-163.725 EndY=2.91403 EndZ=0
    g5: LineSegment StartX=163.725 StartY=0.443099 StartZ=0 EndX=163.725 EndY=2.91403 EndZ=0
  constraints (16):
    c: Vertical(g0)
    c: Coincident(g0,g1)
    c: Horizontal(g1)
    c: Coincident(g1,g2)
    c: Vertical(g2)
    c: Coincident(g2,g3)
    c: Coincident(g3,g0)
    c: Horizontal(g3)
    c: PointOnObject(g-4,g3)
    c: Coincident(g4,g-3)
    c: Coincident(g4,g0)
    c: Perpendicular(g3,g4)
    c: Coincident(g5,g-3)
    c: Coincident(g5,g2)
    c: Perpendicular(g3,g5)
    c: DistanceY(g1) = 80
FEATURE [PartDesign::Pad] Pad007
  BaseFeature = -> Pad006
  Direction = (0,-1,2e-16)
  Length = 0.5
  Length2 = 10
  Placement = pos=(0,0,0) rot=(1,0,0;0.152649rad)
  Profile = -> Sketch050
  ReferenceAxis = -> Sketch050 [N_Axis]
  Reversed = true
  Suppressed = false
  Type = 0
FEATURE [Sketcher::SketchObject] Sketch049
  AttachmentSupport = -> [Local_CS]
  ExternalGeometry = -> [Sketch045,Sketch047,Sketch050]
  FullyConstrained = true
  MapMode = 5
  Placement = pos=(164.635,0,0) rot=(0.889126,0.323616,0.323616;1.68804rad)
  sketch-geometry (4):
    g0: LineSegment StartX=0.909926 StartY=2.91403 StartZ=0 EndX=201.749 EndY=22.775 EndZ=0
    g1: LineSegment StartX=0.909926 StartY=2.91403 StartZ=0 EndX=0.909926 EndY=80 EndZ=0
    g2: LineSegment StartX=0.909926 StartY=80 StartZ=0 EndX=201.749 EndY=80 EndZ=0
    g3: LineSegment StartX=201.749 StartY=80 StartZ=0 EndX=201.749 EndY=22.775 EndZ=0
  constraints (11):
    c: Coincident(g0,g-4)
    c: Parallel(g-3,g0)
    c: Equal(g0,g-3)
    c: Coincident(g0,g1)
    c: Vertical(g1)
    c: Coincident(g1,g2)
    c: Horizontal(g2)
    c: Coincident(g2,g3)
    c: Coincident(g3,g0)
    c: Vertical(g3)
    c: Horizontal(g-5,g1)
FEATURE [PartDesign::Pad] Pad008
  BaseFeature = -> Pad007
  Direction = (0.642788,-0.766044,-3e-16)
  Length = 0.5
  Length2 = 10
  Placement = pos=(0,0,0) rot=(1,0,0;0.152649rad)
  Profile = -> Sketch049
  ReferenceAxis = -> Sketch049 [N_Axis]
  Reversed = true
  Suppressed = false
  Type = 0
FEATURE [Sketcher::SketchObject] Sketch051
  AttachmentSupport = -> [XY_Plane012]
  ExternalGeometry = -> [Binder015]
  FullyConstrained = true
  MapMode = 5
  sketch-geometry (1):
    g0: LineSegment StartX=-319.563 StartY=130 StartZ=0 EndX=-164.635 EndY=0 EndZ=0
  constraints (2):
    c: Symmetric(g0,g-3,g-2)
    c: Symmetric(g0,g-3,g-2)
FEATURE [PartDesign::CoordinateSystem] Local_CS003
  AttacherType = Attacher::AttachEngine3D
  AttachmentOffset = pos=(0,0,0) rot=(0,1,0;1.5708rad)
  AttachmentSupport = -> [Sketch051]
  MapMode = 7
  Placement = pos=(-164.635,0,0) rot=(-0.889126,0.323616,0.323616;4.59514rad)
FEATURE [Sketcher::SketchObject] Sketch052
  AttachmentSupport = -> [Local_CS003]
  ExternalGeometry = -> [Sketch045,Sketch048,Sketch050]
  FullyConstrained = true
  MapMode = 5
  Placement = pos=(-164.635,-1.42e-14,0) rot=(0.889126,-0.323616,-0.323616;1.68804rad)
  sketch-geometry (5):
    g0: LineSegment StartX=-201.749 StartY=22.775 StartZ=0 EndX=-0.909926 EndY=2.91403 EndZ=0
    g1: LineSegment StartX=-0.909926 StartY=2.91403 StartZ=0 EndX=-0.909926 EndY=80 EndZ=0
    g2: LineSegment StartX=-0.909926 StartY=80 StartZ=0 EndX=-201.749 EndY=80 EndZ=0
    g3: LineSegment StartX=-201.749 StartY=80 StartZ=0 EndX=-201.749 EndY=22.775 EndZ=0
    g4: LineSegment StartX=-201.993 StartY=20.3041 StartZ=0 EndX=-201.749 EndY=22.775 EndZ=0
  constraints (13):
    c: Coincident(g0,g-4)
    c: Coincident(g1,g0)
    c: Vertical(g1)
    c: Coincident(g1,g2)
    c: Horizontal(g2)
    c: Coincident(g2,g3)
    c: Coincident(g3,g0)
    c: Vertical(g3)
    c: Coincident(g4,g-3)
    c: Coincident(g4,g0)
    c: Perpendicular(g-3,g4)
    c: Parallel(g-3,g0)
    c: Horizontal(g1,g-5)
FEATURE [PartDesign::Pad] Pad009
  BaseFeature = -> Pad008
  Direction = (-0.642788,-0.766044,1e-16)
  Length = 0.5
  Length2 = 10
  Placement = pos=(0,0,0) rot=(1,0,0;0.152649rad)
  Profile = -> Sketch052
  ReferenceAxis = -> Sketch052 [N_Axis]
  Reversed = true
  Suppressed = false
  Type = 0
FEATURE [Sketcher::SketchObject] Sketch053
  AttachmentSupport = -> [Local_CS001]
  ExternalGeometry = -> [Pad009]
  FullyConstrained = true
  MapMode = 5
  Placement = pos=(0,0,0) rot=(1,0,0;0.152649rad)
  sketch-geometry (28):
    g0: LineSegment StartX=0 StartY=2 StartZ=0 EndX=40.9313 EndY=2 EndZ=0
    g1: LineSegment StartX=40.9313 StartY=2 StartZ=0 EndX=81.8625 EndY=2 EndZ=0
    g2: LineSegment StartX=81.8625 StartY=2 StartZ=0 EndX=122.794 EndY=2 EndZ=0
    g3: LineSegment StartX=122.794 StartY=2 StartZ=0 EndX=163.725 EndY=2 EndZ=0
    g4: ArcOfCircle CenterX=-17 CenterY=2 CenterZ=0 NormalX=0 NormalY=0 NormalZ=1 AngleXU=0 Radius=3 StartAngle=1.5708 EndAngle=4.71239
    g5: ArcOfCircle CenterX=17 CenterY=2 CenterZ=0 NormalX=0 NormalY=0 NormalZ=1 AngleXU=0 Radius=3 StartAngle=4.71239 EndAngle=7.85398
    g6: LineSegment StartX=-17 StartY=5 StartZ=0 EndX=17 EndY=5 EndZ=0
    g7: LineSegment StartX=-17 StartY=-1 StartZ=0 EndX=17 EndY=-1 EndZ=0
    g8: GeomPoint X=-20 Y=2 Z=0
    g9: GeomPoint X=20 Y=2 Z=0
    g10: ArcOfCircle CenterX=106 CenterY=2 CenterZ=0 NormalX=0 NormalY=0 NormalZ=1 AngleXU=0 Radius=3 StartAngle=1.5708 EndAngle=4.71239
    g11: ArcOfCircle CenterX=140 CenterY=2 CenterZ=0 NormalX=0 NormalY=0 NormalZ=1 AngleXU=0 Radius=3 StartAngle=4.71239 EndAngle=7.85398
    g12: LineSegment StartX=106 StartY=5 StartZ=0 EndX=140 EndY=5 EndZ=0
    g13: LineSegment StartX=106 StartY=-1 StartZ=0 EndX=140 EndY=-1 EndZ=0
    g14: ArcOfCircle CenterX=-140 CenterY=2 CenterZ=0 NormalX=0 NormalY=0 NormalZ=1 AngleXU=0 Radius=3 StartAngle=1.5708 EndAngle=4.71239
    g15: ArcOfCircle CenterX=-106 CenterY=2 CenterZ=0 NormalX=0 NormalY=0 NormalZ=1 AngleXU=0 Radius=3 StartAngle=4.71239 EndAngle=7.85398
    g16: LineSegment StartX=-140 StartY=5 StartZ=0 EndX=-106 EndY=5 EndZ=0
    g17: LineSegment StartX=-140 StartY=-1 StartZ=0 EndX=-106 EndY=-1 EndZ=0
    g18: ArcOfCircle CenterX=-78.5 CenterY=2 CenterZ=0 NormalX=0 NormalY=0 NormalZ=1 AngleXU=0 Radius=3 StartAngle=1.5708 EndAngle=4.71239
    g19: ArcOfCircle CenterX=-44.5 CenterY=2 CenterZ=0 NormalX=0 NormalY=0 NormalZ=1 AngleXU=0 Radius=3 StartAngle=4.71239 EndAngle=7.85398
    g20: LineSegment StartX=-78.5 StartY=5 StartZ=0 EndX=-44.5 EndY=5 EndZ=0
    g21: LineSegment StartX=-78.5 StartY=-1 StartZ=0 EndX=-44.5 EndY=-1 EndZ=0
    g22: ArcOfCircle CenterX=44.5 CenterY=2 CenterZ=0 NormalX=0 NormalY=0 NormalZ=1 AngleXU=0 Radius=3 StartAngle=1.5708 EndAngle=4.71239
    g23: ArcOfCircle CenterX=78.5 CenterY=2 CenterZ=0 NormalX=0 NormalY=0 NormalZ=1 AngleXU=0 Radius=3 StartAngle=4.71239 EndAngle=7.85398
    g24: LineSegment StartX=44.5 StartY=5 StartZ=0 EndX=78.5 EndY=5 EndZ=0
    g25: LineSegment StartX=44.5 StartY=-1 StartZ=0 EndX=78.5 EndY=-1 EndZ=0
    g26: LineSegment StartX=17 StartY=-1 StartZ=0 EndX=44.5 EndY=-1 EndZ=0
    g27: LineSegment StartX=78.5 StartY=-1 StartZ=0 EndX=106 EndY=-1 EndZ=0
  constraints (67):
    c: PointOnObject(g0,g-2)
    c: Coincident(g0,g1)
    c: Horizontal(g1)
    c: Coincident(g1,g2)
    c: Coincident(g2,g3)
    c: Horizontal(g3)
    c: Vertical(g-3,g3)
    c: Horizontal(g0)
    c: Equal(g0,g1)
    c: Equal(g1,g2)
    c: Equal(g2,g3)
    c: DistanceY(g0) = 2
    c: Horizontal(g2)
    c: Tangent(g4,g6) = 1.5708
    c: Tangent(g4,g7) = -1.5708
    c: Tangent(g5,g6) = 1.5708
    c: Tangent(g5,g7) = -1.5708
    c: Equal(g4,g5)
    c: PointOnObject(g5,g0)
    c: Symmetric(g4,g5,g-2)
    c: Radius(g5) = 3
    c: PointOnObject(g8,g4)
    c: PointOnObject(g9,g5)
    c: Horizontal(g9,g8)
    c: Horizontal(g8,g0)
    c: DistanceX(g8,g9) = 40
    c: Tangent(g10,g12) = 1.5708
    c: Tangent(g10,g13) = -1.5708
    c: Tangent(g11,g12) = 1.5708
    c: Tangent(g11,g13) = -1.5708
    c: Equal(g10,g11)
    c: Tangent(g14,g16) = 1.5708
    c: Tangent(g14,g17) = -1.5708
    c: Tangent(g15,g16) = 1.5708
    c: Tangent(g15,g17) = -1.5708
    c: Equal(g14,g15)
    c: Tangent(g18,g20) = 1.5708
    c: Tangent(g18,g21) = -1.5708
    c: Tangent(g19,g20) = 1.5708
    c: Tangent(g19,g21) = -1.5708
    c: Equal(g18,g19)
    c: Tangent(g22,g24) = 1.5708
    c: Tangent(g22,g25) = -1.5708
    c: Tangent(g23,g24) = 1.5708
    c: Tangent(g23,g25) = -1.5708
    c: Equal(g22,g23)
    c: Horizontal(g14,g15)
    c: Horizontal(g18,g19)
    c: Horizontal(g22,g23)
    c: Horizontal(g10,g11)
    c: Equal(g11,g23)
    c: Equal(g23,g5)
    c: Equal(g5,g19)
    c: Equal(g19,g15)
    c: Equal(g16,g20)
    c: Equal(g20,g6)
    c: Equal(g6,g24)
    c: Equal(g12,g24)
    c: Horizontal(g10,g22)
    c: Symmetric(g19,g22,g-2)
    c: Symmetric(g10,g15,g-2)
    c: Tangent(g26,g5) = -1.5708
    c: Coincident(g26,g22)
    c: Coincident(g27,g23)
    c: Coincident(g27,g10)
    c: Equal(g26,g27)
    c: DistanceX(g11) = 140
FEATURE [Sketcher::SketchObject] Sketch054
  AttachmentSupport = -> [Local_CS]
  ExternalGeometry = -> [Sketch049]
  FullyConstrained = true
  MapMode = 5
  Placement = pos=(164.635,0,0) rot=(0.889126,0.323616,0.323616;1.68804rad)
  sketch-geometry (6):
    g0: LineSegment StartX=0.909926 StartY=78 StartZ=0 EndX=0.909926 EndY=80 EndZ=0
    g1: LineSegment StartX=0.909926 StartY=80 StartZ=0 EndX=2.90993 EndY=80 EndZ=0
    g2: LineSegment StartX=199.749 StartY=80 StartZ=0 EndX=201.749 EndY=80 EndZ=0
    g3: LineSegment StartX=201.749 StartY=80 StartZ=0 EndX=201.749 EndY=78 EndZ=0
    g4: ArcOfCircle CenterX=2.90993 CenterY=78 CenterZ=0 NormalX=0 NormalY=0 NormalZ=1 AngleXU=0 Radius=2 StartAngle=1.5708 EndAngle=3.14159
    g5: ArcOfCircle CenterX=199.749 CenterY=78 CenterZ=0 NormalX=0 NormalY=0 NormalZ=1 AngleXU=0 Radius=2 StartAngle=1.5e-15 EndAngle=1.5708
  constraints (14):
    c: Coincident(g0,g-3)
    c: Vertical(g0)
    c: Coincident(g0,g1)
    c: PointOnObject(g1,g-3)
    c: Coincident(g2,g-3)
    c: Coincident(g2,g3)
    c: Tangent(g5,g3) = 1.5708
    c: Tangent(g5,g2) = 1.5708
    c: Equal(g4,g5)
    c: Radius(g5) = 2
    c: Vertical(g3)
    c: PointOnObject(g2,g-3)
    c: Tangent(g4,g0) = 1.5708
    c: Tangent(g1,g4) = 1.5708
FEATURE [Sketcher::SketchObject] Sketch055
  AttachmentSupport = -> [Local_CS003]
  ExternalGeometry = -> [Sketch052]
  FullyConstrained = true
  MapMode = 2
  Placement = pos=(-164.635,-1.42e-14,0) rot=(0.889126,-0.323616,-0.323616;1.68804rad)
  sketch-geometry (6):
    g0: ArcOfCircle CenterX=-2.90993 CenterY=78 CenterZ=0 NormalX=0 NormalY=0 NormalZ=1 AngleXU=0 Radius=2 StartAngle=6.28318 EndAngle=7.85398
    g1: ArcOfCircle CenterX=-199.749 CenterY=78 CenterZ=0 NormalX=0 NormalY=0 NormalZ=1 AngleXU=0 Radius=2 StartAngle=1.5708 EndAngle=3.14159
    g2: LineSegment StartX=-201.749 StartY=78 StartZ=0 EndX=-201.749 EndY=80 EndZ=0
    g3: LineSegment StartX=-201.749 StartY=80 StartZ=0 EndX=-199.749 EndY=80 EndZ=0
    g4: LineSegment StartX=-2.90993 StartY=80 StartZ=0 EndX=-0.909926 EndY=80 EndZ=0
    g5: LineSegment StartX=-0.909926 StartY=80 StartZ=0 EndX=-0.909926 EndY=78 EndZ=0
  constraints (15):
    c: PointOnObject(g1,g-3)
    c: Coincident(g2,g3)
    c: Vertical(g2)
    c: Tangent(g1,g2) = 1.5708
    c: Tangent(g3,g1) = 1.5708
    c: Coincident(g4,g5)
    c: Coincident(g5,g0)
    c: Tangent(g5,g0)
    c: Tangent(g0,g4) = 1.5708
    c: Coincident(g4,g-3)
    c: Equal(g0,g1)
    c: Radius(g0) = 2
    c: Coincident(g2,g-3)
    c: PointOnObject(g0,g-3)
    c: Vertical(g5)
FEATURE [Sketcher::SketchObject] Sketch056
  AttachmentSupport = -> [XZ_Plane012]
  ExternalGeometry = -> [Sketch050]
  FullyConstrained = true
  MapMode = 5
  Placement = pos=(0,0,0) rot=(1,0,0;1.5708rad)
  sketch-geometry (6):
    g0: LineSegment StartX=161.725 StartY=80 StartZ=0 EndX=163.725 EndY=80 EndZ=0
    g1: LineSegment StartX=163.725 StartY=80 StartZ=0 EndX=163.725 EndY=78 EndZ=0
    g2: LineSegment StartX=-163.725 StartY=78 StartZ=0 EndX=-163.725 EndY=80 EndZ=0
    g3: LineSegment StartX=-163.725 StartY=80 StartZ=0 EndX=-161.725 EndY=80 EndZ=0
    g4: ArcOfCircle CenterX=-161.725 CenterY=78 CenterZ=0 NormalX=0 NormalY=0 NormalZ=1 AngleXU=0 Radius=2 StartAngle=1.5708 EndAngle=3.14159
    g5: ArcOfCircle CenterX=161.725 CenterY=78 CenterZ=0 NormalX=0 NormalY=0 NormalZ=1 AngleXU=0 Radius=2 StartAngle=-4.4e-15 EndAngle=1.5708
  constraints (14):
    c: Coincident(g0,g-3)
    c: Coincident(g0,g1)
    c: Coincident(g2,g-3)
    c: Coincident(g2,g3)
    c: Tangent(g5,g1) = 1.5708
    c: Tangent(g5,g0) = 1.5708
    c: Tangent(g4,g2) = 1.5708
    c: Tangent(g4,g3) = 1.5708
    c: Equal(g5,g4)
    c: Radius(g5) = 2
    c: PointOnObject(g3,g-3)
    c: Vertical(g2)
    c: PointOnObject(g0,g-3)
    c: Vertical(g1)
FEATURE [Sketcher::SketchObject] Sketch057
  AttachmentOffset = pos=(-0.5,0,0) rot=(0,1,0;1.5708rad)
  ExternalGeometry = -> [Sketch001]
  FullyConstrained = true
  MapMode = 7
  Placement = pos=(164.314,0.383022,0) rot=(0.889126,0.323616,0.323616;1.68804rad)
  sketch-geometry (6):
    g0: LineSegment StartX=-14.0901 StartY=73 StartZ=0 EndX=5.90993 EndY=73 EndZ=0
    g1: LineSegment StartX=5.90993 StartY=73 StartZ=0 EndX=5.90993 EndY=88 EndZ=0
    g2: LineSegment StartX=171.749 StartY=73 StartZ=0 EndX=191.749 EndY=73 EndZ=0
    g3: LineSegment StartX=191.749 StartY=73 StartZ=0 EndX=191.749 EndY=88 EndZ=0
    g4: LineSegment StartX=0 StartY=0 StartZ=0 EndX=5.90993 EndY=0 EndZ=0
    g5: LineSegment StartX=202.244 StartY=-7.8e-15 StartZ=0 EndX=191.749 EndY=-7.8e-15 EndZ=0
  constraints (20):
    c: Horizontal(g0)
    c: Coincident(g0,g1)
    c: Vertical(g1)
    c: Horizontal(g2)
    c: Coincident(g2,g3)
    c: Vertical(g3)
    c: Horizontal(g2,g0)
    c: Equal(g1,g3)
    c: Equal(g0,g2)
    c: DistanceY(g0) = 73
    c: PointOnObject(g4,g1)
    c: Horizontal(g4)
    c: PointOnObject(g5,g3)
    c: Horizontal(g5)
    c: DistanceX(g4,g4) = 5.90993
    c: DistanceX(g2,g2) = 20
    c: DistanceY(g3,g3) = 15
    c: DistanceX(g5,g5) = 10.4955
    c: Coincident(g5,g-3)
    c: Coincident(g4,g-3)
FEATURE [Part::FeaturePython] Placment016  # WARN: FeaturePython — macro-defined, semantics opaque (R4)
  AttacherType = Attacher::AttachEngine3D
  AttachmentSupport = -> [Sketch057]
  ExposePlacement = true
  MapMode = 49
  MarkerShape = 1
  MarkerSize = 20
  NumElements = 1
  Placement = pos=(168.841,4.18185,73) rot=(0.889126,0.323616,0.323616;1.68804rad)
  Type = lattice2AttachablePlacement.AttachablePlacement
  isLattice = 1
FEATURE [Part::FeaturePython] PlacementSubsequence001  # WARN: FeaturePython — macro-defined, semantics opaque (R4)
  Base = -> Placment016
  CycleMode = 0
  ExposePlacement = false
  MarkerShape = 1
  MarkerSize = 0
  NumElements = 2
  Type = lattice2AttachablePlacement.AttachedPlacementSubsequence
  isLattice = 1
FEATURE [Part::FeaturePython] Mirror002  label="Mirror of Join002"  # WARN: FeaturePython — macro-defined, semantics opaque (R4)
  ExposePlacement = false
  FlipX = true
  FlipY = false
  FlipZ = false
  MarkerShape = 1
  MarkerSize = 0
  NumElements = 2
  Object = -> PlacementSubsequence001
  ObjectTraversal = 0
  Type = lattice2Mirror.LatticeMirror
  isLattice = 1
FEATURE [Sketcher::SketchObject] Sketch058
  ExternalGeometry = -> [Sketch050]
  FullyConstrained = true
  Placement = pos=(0,0.5,0) rot=(1,0,0;1.5708rad)
  sketch-geometry (4):
    g0: LineSegment StartX=138.725 StartY=73 StartZ=0 EndX=158.725 EndY=73 EndZ=0
    g1: LineSegment StartX=158.725 StartY=73 StartZ=0 EndX=158.725 EndY=113 EndZ=0
    g2: LineSegment StartX=138.725 StartY=21 StartZ=0 EndX=158.725 EndY=21 EndZ=0
    g3: LineSegment StartX=158.725 StartY=21 StartZ=0 EndX=158.725 EndY=61 EndZ=0
  constraints (15):
    c: Horizontal(g0)
    c: Coincident(g0,g1)
    c: Vertical(g1)
    c: DistanceY(g0) = 73
    c: DistanceX(g0,g-3) = 5
    c: DistanceX(g0,g0) = 20
    c: DistanceY(g1,g1) = 40
    c: DistanceY(g0,g-3) = 7
    c: Horizontal(g2)
    c: Coincident(g2,g3)
    c: Vertical(g3)
    c: Vertical(g2,g0)
    c: Equal(g2,g0)
    c: Equal(g3,g1)
    c: DistanceY(g2,g0) = 52
FEATURE [Part::FeaturePython] Placment017  # WARN: FeaturePython — macro-defined, semantics opaque (R4)
  AttacherType = Attacher::AttachEngine3D
  AttachmentSupport = -> [Sketch058]
  ExposePlacement = true
  MapMode = 49
  MarkerShape = 1
  MarkerSize = 20
  NumElements = 1
  Placement = pos=(158.725,0.5,73) rot=(1,0,0;1.5708rad)
  Type = lattice2AttachablePlacement.AttachablePlacement
  isLattice = 1
FEATURE [Part::FeaturePython] PlacementSubsequence002  # WARN: FeaturePython — macro-defined, semantics opaque (R4)
  Base = -> Placment017
  CycleMode = 0
  ExposePlacement = false
  MarkerShape = 1
  MarkerSize = 0
  NumElements = 2
  Type = lattice2AttachablePlacement.AttachedPlacementSubsequence
  isLattice = 1
FEATURE [Part::FeaturePython] Mirror003  label="Mirror001 of PlacementSubsequence002"  # WARN: FeaturePython — macro-defined, semantics opaque (R4)
  ExposePlacement = false
  FlipX = true
  FlipY = false
  FlipZ = false
  MarkerShape = 1
  MarkerSize = 20
  NumElements = 2
  Object = -> PlacementSubsequence002
  ObjectTraversal = 0
  Type = lattice2Mirror.LatticeMirror
  isLattice = 1
FEATURE [Part::FeaturePython] Join006  label="sink_front_fix"  # WARN: FeaturePython — macro-defined, semantics opaque (R4)
  ExposePlacement = false
  Interleave = false
  Links = -> [Placment018,Mirror003,PlacementSubsequence002]
  MarkerShape = 1
  MarkerSize = 0
  NumElements = 5
  Type = lattice2JoinArrays.JoinArrays
  isLattice = 1
FEATURE [Part::FeaturePython] Join004  # WARN: FeaturePython — macro-defined, semantics opaque (R4)
  ExposePlacement = false
  Interleave = false
  Links = -> [Mirror002,Join006,PlacementSubsequence001]
  MarkerShape = 1
  MarkerSize = 0
  NumElements = 9
  Type = lattice2JoinArrays.JoinArrays
  isLattice = 1
FEATURE [Part::FeaturePython] Populate020  label="Populate Join003 with hole_3.4mm"  # WARN: FeaturePython — macro-defined, semantics opaque (R4)
  Copying = 0
  ExposePlacement = false
  MarkerShape = 1
  MarkerSize = 0
  NumElements = 0
  Object = -> Cylinder003
  OutputCompounding = 1
  PlacementsTo = -> Join004
  Referencing = 0
  Type = lattice2PopulateCopies.LatticePopulateCopies
  isLattice = 0
FEATURE [Part::Compound] Compound016
  Links = -> [Populate020]
FEATURE [Sketcher::SketchObject] Sketch059
  AttachmentSupport = -> [YZ_Plane012]
  ExternalGeometry = -> [Sketch045]
  FullyConstrained = true
  MapMode = 5
  Placement = pos=(0,0,0) rot=(0.57735,0.57735,0.57735;2.0944rad)
  sketch-geometry (7):
    g0: ArcOfCircle CenterX=132.281 CenterY=18.3274 CenterZ=0 NormalX=0 NormalY=0 NormalZ=1 AngleXU=0 Radius=2 StartAngle=5e-16 EndAngle=1.72345
    g1: ArcOfCircle CenterX=132.281 CenterY=18.3274 CenterZ=0 NormalX=0 NormalY=0 NormalZ=1 AngleXU=0 Radius=2.5 StartAngle=4.587e-13 EndAngle=1.72345
    g2: LineSegment StartX=131.977 StartY=20.3041 StartZ=0 EndX=131.901 EndY=20.7983 EndZ=0
    g3: LineSegment StartX=134.281 StartY=18.3274 StartZ=0 EndX=134.281 EndY=10.8274 EndZ=0
    g4: LineSegment StartX=134.281 StartY=10.8274 StartZ=0 EndX=134.781 EndY=10.8274 EndZ=0
    g5: LineSegment StartX=134.781 StartY=10.8274 StartZ=0 EndX=134.781 EndY=18.3274 EndZ=0
    g6: LineSegment StartX=134.781 StartY=20.8274 StartZ=0 EndX=0 EndY=20.8274 EndZ=0
  constraints (19):
    c: Coincident(g1,g0)
    c: Coincident(g2,g1)
    c: Vertical(g3)
    c: Coincident(g4,g3)
    c: Horizontal(g4)
    c: Coincident(g5,g4)
    c: Vertical(g5)
    c: Tangent(g0,g-3) = 1.5708
    c: Perpendicular(g2,g-3)
    c: Distance(g2) = 0.5
    c: Coincident(g2,g0)
    c: Radius(g0) = 2
    c: Horizontal(g6)
    c: Tangent(g6,g1)
    c: PointOnObject(g6,g-2)
    c: PointOnObject(g6,g5)
    c: Tangent(g3,g0) = 1.5708
    c: DistanceY(g4,g6) = 10
    c: Tangent(g5,g1) = -1.5708
FEATURE [Sketcher::SketchObject] Sketch060
  AttachmentSupport = -> [XZ_Plane012]
  ExternalGeometry = -> [Sketch059]
  FullyConstrained = true
  MapMode = 5
  Placement = pos=(0,0,0) rot=(1,0,0;1.5708rad)
  expr: Constraints[5] = <<sink_plane_sketch>>.Constraints.end / 2
  sketch-geometry (3):
    g0: ArcOfCircle CenterX=315.576 CenterY=12.8274 CenterZ=0 NormalX=0 NormalY=0 NormalZ=1 AngleXU=0 Radius=2 StartAngle=4.71239 EndAngle=6.28318
    g1: LineSegment StartX=315.576 StartY=10.8274 StartZ=0 EndX=317.576 EndY=10.8274 EndZ=0
    g2: LineSegment StartX=317.576 StartY=10.8274 StartZ=0 EndX=317.576 EndY=12.8274 EndZ=0
  constraints (9):
    c: Coincident(g1,g2)
    c: Coincident(g2,g0)
    c: Tangent(g2,g0)
    c: Vertical(g2)
    c: Horizontal(g1)
    c: DistanceX(g1) = 317.576
    c: Radius(g0) = 2
    c: Tangent(g0,g1) = -1.5708
    c: Horizontal(g-3,g1)
FEATURE [PartDesign::FeaturePython] SketchOnSheet  # WARN: FeaturePython — macro-defined, semantics opaque (R4)
  BaseFeature = -> Pad009
  Sketch = -> Sketch053
  Suppressed = false
  baseObject = -> Pad009 [Face14]
  kfactor = 0.5
FEATURE [PartDesign::FeaturePython] CornerRelief  # WARN: FeaturePython — macro-defined, semantics opaque (R4)
  BaseFeature = -> SketchOnSheet
  ReliefSketch = 0
  Size = 5
  SizeRatio = 1
  Suppressed = false
  XOffset = 0
  YOffset = 0
  baseObject = -> SketchOnSheet [Edge56,Edge57]
  kfactor = 0.5
FEATURE [PartDesign::FeaturePython] CornerRelief001  # WARN: FeaturePython — macro-defined, semantics opaque (R4)
  BaseFeature = -> CornerRelief
  ReliefSketch = 0
  Size = 5
  SizeRatio = 1
  Suppressed = false
  XOffset = 0
  YOffset = 0
  baseObject = -> CornerRelief [Edge17,Edge14]
  kfactor = 0.5
  expr: Size = <<CornerRelief>>.Size
FEATURE [PartDesign::Pocket] Pocket008
  BaseFeature = -> CornerRelief001
  Direction = (-0.642788,0.766044,3e-16)
  Length = 5
  Length2 = 5
  Midplane = true
  Profile = -> Sketch054
  ReferenceAxis = -> Sketch054 [N_Axis]
  Suppressed = false
  Type = 1
FEATURE [PartDesign::Pocket] Pocket009
  BaseFeature = -> Pocket008
  Direction = (0.642788,0.766044,3e-16)
  Length = 5
  Length2 = 5
  Midplane = true
  Profile = -> Sketch055
  ReferenceAxis = -> Sketch055 [N_Axis]
  Suppressed = false
  Type = 0
FEATURE [PartDesign::Pocket] Pocket010
  BaseFeature = -> Pocket009
  Direction = (0,1,-2e-16)
  Length = 5
  Length2 = 5
  Midplane = true
  Profile = -> Sketch056
  ReferenceAxis = -> Sketch056 [N_Axis]
  Suppressed = false
  Type = 1
FEATURE [PartDesign::Pad] Pad017
  BaseFeature = -> Pocket010
  Direction = (1,0,0)
  Length = 635.153
  Length2 = 10
  Midplane = true
  Profile = -> Sketch059
  ReferenceAxis = -> Sketch059 [N_Axis]
  Suppressed = false
  Type = 0
  expr: Length = <<sink_plane_sketch>>.Constraints.end
FEATURE [PartDesign::Pocket] Pocket011
  BaseFeature = -> Pad017
  Direction = (0,1,-2e-16)
  Length = 5
  Length2 = 5
  Midplane = true
  Profile = -> Sketch060
  ReferenceAxis = -> Sketch060 [N_Axis]
  Suppressed = false
  Type = 1
FEATURE [PartDesign::Mirrored] Mirrored002
  BaseFeature = -> Pocket011
  MirrorPlane = -> Sketch060 [V_Axis]
  Originals = -> [Pocket011]
  Suppressed = false
FEATURE [PartDesign::Boolean] Boolean011
  BaseFeature = -> Mirrored002
  Group = -> [Compound016]
  Suppressed = false
  Type = 1
  UsePlacement = true
FEATURE [PartDesign::Body] Body012  label="sink"
  Group = -> [Binder015,Local_CS,Sketch005,Sketch006,Sketch044,Local_CS001,Sketch045,Sketch046,Sketch047,Sketch048,Pad003,Pad004,Pad005,Pad006,Sketch049,Sketch050,Pad007,Pad008,Sketch051,Local_CS003,Sketch052,Pad009,Sketch053,SketchOnSheet,CornerRelief,CornerRelief001,Sketch054,Sketch055,Sketch056,Pocket008,Pocket009,Pocket010,Local_CS004,Sketch059,Pad017,Sketch060,Pocket011,Mirrored002,Boolean011]
  Origin = -> Origin012
  Tip = -> Boolean011
FEATURE [Part::FeaturePython] Placment019  label="sink_placement"  # WARN: FeaturePython — macro-defined, semantics opaque (R4)
  AttacherType = Attacher::AttachEngine3D
  ExposePlacement = true
  MarkerShape = 1
  MarkerSize = 20
  NumElements = 1
  Placement = pos=(0,90,140) rot=(0,0,1;0rad)
  Type = lattice2AttachablePlacement.AttachablePlacement
  isLattice = 1
  expr: .Placement.Base.y = <<Dimensions_sketch>>.Constraints.offset
  expr: .Placement.Base.z = 113 + 12 + 5 + 10
FEATURE [Part::FeaturePython] Populate021  label="Populate Placment019 with Populate Join003 with hole_3.4mm"  # WARN: FeaturePython — macro-defined, semantics opaque (R4)
  Copying = 0
  ExposePlacement = false
  MarkerShape = 1
  MarkerSize = 0
  NumElements = 0
  Object = -> Populate020
  OutputCompounding = 2
  PlacementsTo = -> Placment019
  Referencing = 0
  Type = lattice2PopulateCopies.LatticePopulateCopies
  isLattice = 0
FEATURE [Sketcher::SketchObject] Sketch061
  FullyConstrained = true
  sketch-geometry (4):
    g0: ArcOfCircle CenterX=0 CenterY=0 CenterZ=0 NormalX=0 NormalY=0 NormalZ=1 AngleXU=0 Radius=6 StartAngle=5.44212 EndAngle=7.85398
    g1: ArcOfCircle CenterX=6 CenterY=-6.7082 CenterZ=0 NormalX=0 NormalY=0 NormalZ=1 AngleXU=0 Radius=3 StartAngle=2.30052 EndAngle=3.14159
    g2: ArcOfCircle CenterX=0 CenterY=-10 CenterZ=0 NormalX=0 NormalY=0 NormalZ=1 AngleXU=0 Radius=3 StartAngle=4.71239 EndAngle=6.28319
    g3: LineSegment StartX=3 StartY=-10 StartZ=0 EndX=3 EndY=-6.7082 EndZ=0
  constraints (12):
    c: Coincident(g0,g-1)
    c: PointOnObject(g0,g-2)
    c: PointOnObject(g2,g-2)
    c: PointOnObject(g2,g-2)
    c: Tangent(g3,g2) = -1.5708
    c: Tangent(g3,g1) = 1.5708
    c: Tangent(g1,g0) = 1.5708
    c: Vertical(g3)
    c: Diameter(g0) = 12
    c: Diameter(g2) = 6
    c: Radius(g1) = 3
    c: DistanceY(g2,g0) = 10
FEATURE [Part::Mirroring] Part__Mirroring014  label="Sketch061 (Mirror #14)"
  Base = (0,0,0)
  Normal = (1,0,0)
  Source = -> Sketch061
FEATURE [Part::FeaturePython] Connect009  # WARN: FeaturePython — macro-defined, semantics opaque (R4)
  Objects = -> [Sketch061,Part__Mirroring014]
  Tolerance = 0
FEATURE [Part::Extrusion] Extrude018
  Base = -> Connect009
  Dir = (0,0,1)
  DirMode = 2
  FaceMakerClass = Part::FaceMakerBullseye
  LengthFwd = 10
  LengthRev = 0
  Solid = true
  Symmetric = false
FEATURE [Part::FeaturePython] LinearArray005  # WARN: FeaturePython — macro-defined, semantics opaque (R4)
  Alignment = 0
  CellStart = A1
  Count = 2
  Dir = (1,0,0)
  DirIsDriven = true
  DistributionLaw = 0
  DrivenProperty = 1
  EndInclusive = true
  ExposePlacement = false
  GeneratorMode = 0
  MarkerShape = 1
  MarkerSize = 0
  NumElements = 2
  OrientMode = 1
  Placement = pos=(-150,0,660) rot=(-1,0,0;1.5708rad)
  Point = (0,0,0)
  PointIsDriven = true
  Reverse = false
  SpanEnd = 300
  SpanStart = 0
  Step = 300
  Type = lattice2LinearArray.LinearArray
  VSGVersion = 1
  Values = 0.0 | 300.0
  ValuesSource = 2
  isLattice = 1
  expr: .Placement.Base.x = -SpanEnd / 2
FEATURE [Part::FeaturePython] Populate022  label="Populate LinearArray005 with Extrude018"  # WARN: FeaturePython — macro-defined, semantics opaque (R4)
  Copying = 0
  ExposePlacement = false
  MarkerShape = 1
  MarkerSize = 0
  NumElements = 0
  Object = -> Extrude018
  OutputCompounding = 1
  PlacementsTo = -> LinearArray005
  Referencing = 0
  Type = lattice2PopulateCopies.LatticePopulateCopies
  isLattice = 0
FEATURE [Part::FeaturePython] LinearArray006  # WARN: FeaturePython — macro-defined, semantics opaque (R4)
  Alignment = 0
  CellStart = A1
  Count = 5
  Dir = (1,0,0)
  DirIsDriven = true
  DistributionLaw = 0
  DrivenProperty = 1
  EndInclusive = true
  ExposePlacement = false
  GeneratorMode = 0
  MarkerShape = 1
  MarkerSize = 0
  NumElements = 5
  OrientMode = 1
  Placement = pos=(319.563,10,0) rot=(0,-1,0;1.5708rad)
  Point = (0,0,0)
  PointIsDriven = true
  Reverse = false
  SpanEnd = 793
  SpanStart = 20
  Step = 193.25
  Type = lattice2LinearArray.LinearArray
  VSGVersion = 1
  Values = 20.0 | 213.25 | 406.5 | 599.75 | 793.0
  ValuesSource = 2
  isLattice = 1
  expr: .Placement.Base.x = <<base_sketch>>.Constraints.total_width / 2
  expr: SpanEnd = <<BaseBend>>.length - SpanStart
FEATURE [Part::FeaturePython] Mirror004  label="Mirror004 of LinearArray006"  # WARN: FeaturePython — macro-defined, semantics opaque (R4)
  ExposePlacement = false
  FlipX = true
  FlipY = false
  FlipZ = false
  MarkerShape = 1
  MarkerSize = 0
  NumElements = 5
  Object = -> LinearArray006
  ObjectTraversal = 0
  Type = lattice2Mirror.LatticeMirror
  isLattice = 1
FEATURE [Part::FeaturePython] Join007  # WARN: FeaturePython — macro-defined, semantics opaque (R4)
  ExposePlacement = false
  Interleave = false
  Links = -> [LinearArray006,Mirror004]
  MarkerShape = 1
  MarkerSize = 0
  NumElements = 10
  Type = lattice2JoinArrays.JoinArrays
  isLattice = 1
FEATURE [Part::FeaturePython] Populate023  label="Populate Join007 with hole_3.4mm"  # WARN: FeaturePython — macro-defined, semantics opaque (R4)
  Copying = 0
  ExposePlacement = false
  MarkerShape = 1
  MarkerSize = 0
  NumElements = 0
  Object = -> Cylinder003
  OutputCompounding = 1
  PlacementsTo = -> Join007
  Referencing = 0
  Type = lattice2PopulateCopies.LatticePopulateCopies
  isLattice = 0
FEATURE [Part::FeaturePython] LinearArray007  # WARN: FeaturePython — macro-defined, semantics opaque (R4)
  Alignment = 0
  CellStart = A1
  Count = 5
  Dir = (1,0,0)
  DirIsDriven = true
  DistributionLaw = 0
  DrivenProperty = 1
  EndInclusive = true
  ExposePlacement = false
  GeneratorMode = 0
  MarkerShape = 1
  MarkerSize = 0
  NumElements = 5
  OrientMode = 1
  Placement = pos=(-250,0,10) rot=(-1,0,0;1.5708rad)
  Point = (0,0,0)
  PointIsDriven = true
  Reverse = false
  SpanEnd = 500
  SpanStart = 0
  Step = 125
  Type = lattice2LinearArray.LinearArray
  VSGVersion = 1
  Values = 0.0 | 125.0 | 250.0 | 375.0 | 500.0
  ValuesSource = 2
  isLattice = 1
  expr: .Placement.Base.x = -SpanEnd / 2
FEATURE [Part::FeaturePython] LinearArray008  # WARN: FeaturePython — macro-defined, semantics opaque (R4)
  Alignment = 0
  CellStart = A1
  Count = 3
  Dir = (1,0,0)
  DirIsDriven = true
  DistributionLaw = 0
  DrivenProperty = 1
  EndInclusive = true
  ExposePlacement = false
  GeneratorMode = 0
  MarkerShape = 1
  MarkerSize = 0
  NumElements = 3
  OrientMode = 1
  Placement = pos=(319.563,0,10) rot=(0.57735,0.57735,-0.57735;4.18879rad)
  Point = (0,0,0)
  PointIsDriven = true
  Reverse = false
  SpanEnd = 190
  SpanStart = 20
  Step = 85
  Type = lattice2LinearArray.LinearArray
  VSGVersion = 1
  Values = 20.0 | 104.99999999995704 | 189.99999999991408
  ValuesSource = 2
  isLattice = 1
  expr: .Placement.Base.x = <<base_sketch>>.Constraints.total_width / 2
  expr: .Placement.Base.z = <<LinearArray007>>.Placement.Base.z
  expr: SpanEnd = <<Dimensions_sketch>>.Constraints.total_depth - 30 mm
FEATURE [Part::FeaturePython] Mirror005  label="Mirror005 of LinearArray008"  # WARN: FeaturePython — macro-defined, semantics opaque (R4)
  ExposePlacement = false
  FlipX = true
  FlipY = false
  FlipZ = false
  MarkerShape = 1
  MarkerSize = 0
  NumElements = 3
  Object = -> LinearArray008
  ObjectTraversal = 0
  Type = lattice2Mirror.LatticeMirror
  isLattice = 1
FEATURE [Part::FeaturePython] Populate024  label="Populate LinearArray007 with hole_3.4mm"  # WARN: FeaturePython — macro-defined, semantics opaque (R4)
  Copying = 0
  ExposePlacement = false
  MarkerShape = 1
  MarkerSize = 0
  NumElements = 0
  Object = -> Cylinder003
  OutputCompounding = 1
  PlacementsTo = -> LinearArray007
  Referencing = 0
  Type = lattice2PopulateCopies.LatticePopulateCopies
  isLattice = 0
FEATURE [Part::FeaturePython] Join008  # WARN: FeaturePython — macro-defined, semantics opaque (R4)
  ExposePlacement = false
  Interleave = false
  Links = -> [LinearArray008,Mirror005]
  MarkerShape = 1
  MarkerSize = 0
  NumElements = 6
  Type = lattice2JoinArrays.JoinArrays
  isLattice = 1
FEATURE [Part::FeaturePython] Populate025  label="Populate Join008 with hole_3.4mm"  # WARN: FeaturePython — macro-defined, semantics opaque (R4)
  Copying = 0
  ExposePlacement = false
  MarkerShape = 1
  MarkerSize = 0
  NumElements = 0
  Object = -> Cylinder003
  OutputCompounding = 1
  PlacementsTo = -> Join008
  Referencing = 0
  Type = lattice2PopulateCopies.LatticePopulateCopies
  isLattice = 0
FEATURE [Sketcher::SketchObject] Sketch063
  FullyConstrained = true
  expr: Constraints[17] = <<Dimensions_sketch>>.Constraints.total_depth + 6 mm
  sketch-geometry (6):
    g0: LineSegment StartX=0 StartY=3 StartZ=0 EndX=0 EndY=226 EndZ=0
    g1: LineSegment StartX=0 StartY=226 StartZ=0 EndX=6 EndY=226 EndZ=0
    g2: LineSegment StartX=6 StartY=226 StartZ=0 EndX=6 EndY=9 EndZ=0
    g3: LineSegment StartX=6 StartY=9 StartZ=0 EndX=18 EndY=9 EndZ=0
    g4: LineSegment StartX=0 StartY=3 StartZ=0 EndX=18 EndY=3 EndZ=0
    g5: LineSegment StartX=18 StartY=3 StartZ=0 EndX=18 EndY=9 EndZ=0
  constraints (20):
    c: PointOnObject(g0,g-2)
    c: Coincident(g0,g1)
    c: Horizontal(g1)
    c: Coincident(g1,g2)
    c: Vertical(g2)
    c: Coincident(g2,g3)
    c: Horizontal(g3)
    c: DistanceX(g1,g1) = 6
    c: DistanceX(g3,g3) = 12
    c: Coincident(g5,g4)
    c: Coincident(g5,g3)
    c: Vertical(g5)
    c: Equal(g5,g1)
    c: Coincident(g0,g4)
    c: Horizontal(g4)
    c: PointOnObject(g0,g-2)
    c: DistanceY(g0) = 3
    c: DistanceY(g0) = 226
    c: DistanceX(g4) = 18  'fix_length'
    c: Distance(g2) = 217  'plane_length'
FEATURE [PartDesign::SubShapeBinder] Binder018
  BindCopyOnChange = 0
  BindMode = 0
  ClaimChildren = true
  Context = -> Body014 [Binder018.]
  Fuse = false
  MakeFace = true
  OffsetFill = false
  OffsetIntersection = false
  OffsetJoinType = 0
  OffsetOpenResult = false
  PartialLoad = false
  Placement = pos=(0,0,0) rot=(0,-1,0;1.5708rad)
  Relative = false
  Support = -> [Sketch063]
  _Version = 2
FEATURE [PartDesign::FeaturePython] BaseBend010  # WARN: FeaturePython — macro-defined, semantics opaque (R4)
  BendSide = 0
  BendSketch = -> Binder018
  MidPlane = true
  Reverse = false
  Suppressed = false
  length = 639.126
  radius = 0.1
  thickness = 0.3
  expr: length = <<base_sketch>>.Constraints.total_width
FEATURE [Sketcher::SketchObject] Sketch064
  FullyConstrained = false
  Placement = pos=(316.563,6,0) rot=(1,0,0;1.5708rad)
  expr: .Placement.Base.x = <<base_sketch>>.Constraints.total_width / 2 - 3 mm
  expr: Constraints[4] = <<Sketch063>>.Constraints.fix_length
  sketch-geometry (2):
    g0: LineSegment StartX=0 StartY=18 StartZ=0 EndX=0 EndY=0 EndZ=0
    g1: LineSegment StartX=0 StartY=0 StartZ=0 EndX=-37.4181 EndY=0 EndZ=0
  constraints (5):
    c: PointOnObject(g0,g-2)
    c: Coincident(g0,g-1)
    c: Coincident(g0,g1)
    c: PointOnObject(g1,g-1)
    c: DistanceY(g0,g0) = 18
FEATURE [Part::FeaturePython] BaseBend011  # WARN: FeaturePython — macro-defined, semantics opaque (R4)
  BendSide = 0
  BendSketch = -> Sketch064
  MidPlane = false
  Reverse = true
  length = 191
  radius = 0.1
  thickness = 0.3
  expr: length = <<Sketch067>>.Constraints.bend_length - 4 mm
FEATURE [Sketcher::SketchObject] Sketch065
  ExternalGeometry = -> [Sketch064]
  FullyConstrained = true
  Placement = pos=(-316.563,6,0) rot=(1,0,0;1.5708rad)
  expr: .Placement.Base.x = -<<Sketch064>>.Placement.Base.x
  expr: .Placement.Base.y = <<Sketch064>>.Placement.Base.y
  expr: .Placement.Rotation.Angle = <<Sketch064>>.Placement.Rotation.Angle
  expr: .Placement.Rotation.Axis = <<Sketch064>>.Placement.Rotation.Axis
  sketch-geometry (2):
    g0: LineSegment StartX=0 StartY=18 StartZ=0 EndX=0 EndY=0 EndZ=0
    g1: LineSegment StartX=0 StartY=0 StartZ=0 EndX=37.4181 EndY=0 EndZ=0
  constraints (6):
    c: PointOnObject(g0,g-2)
    c: Coincident(g0,g-1)
    c: Coincident(g1,g0)
    c: PointOnObject(g1,g-1)
    c: Equal(g1,g-4)
    c: Equal(g-3,g0)
FEATURE [Part::FeaturePython] BaseBend012  # WARN: FeaturePython — macro-defined, semantics opaque (R4)
  BendSide = 1
  BendSketch = -> Sketch065
  MidPlane = false
  Reverse = true
  length = 191
  radius = 0.1
  thickness = 0.3
  expr: length = <<BaseBend011>>.length
FEATURE [Sketcher::SketchObject] Sketch066
  ExternalGeometry = -> [Sketch064]
  FullyConstrained = false
  Placement = pos=(310.563,9.1,6) rot=(1,0,0;1.5708rad)
  expr: .Placement.Base.x = <<base_sketch>>.Constraints.total_width / 2 - 9 mm
  sketch-geometry (2):
    g0: LineSegment StartX=0 StartY=12 StartZ=0 EndX=0 EndY=0 EndZ=0
    g1: LineSegment StartX=0 StartY=0 StartZ=0 EndX=-20.1122 EndY=0 EndZ=0
  constraints (5):
    c: PointOnObject(g0,g-2)
    c: Coincident(g0,g-1)
    c: Coincident(g1,g0)
    c: PointOnObject(g1,g-1)
    c: Horizontal(g0,g-3)
FEATURE [Sketcher::SketchObject] Sketch067
  AttachmentOffset = pos=(319.563,0,0) rot=(0,0,1;0rad)
  AttachmentSupport = -> [XY_Plane014]
  FullyConstrained = true
  MapMode = 5
  Placement = pos=(319.563,0,0) rot=(0,0,1;0rad)
  expr: .AttachmentOffset.Base.x = <<BaseBend010>>.length / 2
  expr: .Constraints.length = <<Dimensions_sketch>>.Constraints.total_depth
  sketch-geometry (8):
    g0: LineSegment StartX=0 StartY=3 StartZ=0 EndX=-6 EndY=3 EndZ=0
    g1: LineSegment StartX=-6 StartY=3 StartZ=0 EndX=-6 EndY=6 EndZ=0
    g2: LineSegment StartX=-6 StartY=6 StartZ=0 EndX=-3.4 EndY=6 EndZ=0
    g3: LineSegment StartX=-3 StartY=220 StartZ=0 EndX=0 EndY=220 EndZ=0
    g4: LineSegment StartX=0 StartY=220 StartZ=0 EndX=0 EndY=3 EndZ=0
    g5: LineSegment StartX=-3.4 StartY=6 StartZ=0 EndX=-3.4 EndY=201 EndZ=0
    g6: LineSegment StartX=-3.4 StartY=201 StartZ=0 EndX=-3 EndY=201 EndZ=0
    g7: LineSegment StartX=-3 StartY=201 StartZ=0 EndX=-3 EndY=220 EndZ=0
  constraints (24):
    c: PointOnObject(g0,g-2)
    c: Horizontal(g0)
    c: Coincident(g0,g1)
    c: Vertical(g1)
    c: Coincident(g1,g2)
    c: Horizontal(g2)
    c: Coincident(g2,g5)
    c: Coincident(g7,g3)
    c: PointOnObject(g3,g-2)
    c: Coincident(g3,g4)
    c: Coincident(g4,g0)
    c: DistanceY(g0) = 3
    c: DistanceY(g0,g2) = 3
    c: DistanceX(g0,g0) = 6
    c: DistanceX(g2) = -3.4
    c: Horizontal(g3)
    c: DistanceY(g3) = 220  'length'
    c: Coincident(g5,g6)
    c: Vertical(g5)
    c: Coincident(g6,g7)
    c: Vertical(g7)
    c: Horizontal(g6)
    c: DistanceY(g5,g5) = 195  'bend_length'
    c: DistanceX(g6,g6) = 0.4
FEATURE [PartDesign::Pocket] Pocket012
  BaseFeature = -> BaseBend010
  Direction = (0,0,-1)
  Length = 5
  Length2 = 5
  Midplane = true
  Profile = -> Sketch067
  ReferenceAxis = -> Sketch067 [N_Axis]
  Suppressed = false
  Type = 1
FEATURE [Sketcher::SketchObject] Sketch068
  AttachmentOffset = pos=(319.563,0,6) rot=(0,0,1;0rad)
  AttachmentSupport = -> [XY_Plane014]
  FullyConstrained = true
  MapMode = 5
  Placement = pos=(319.563,0,6) rot=(0,0,1;0rad)
  expr: .AttachmentOffset.Base.x = <<Sketch067>>.AttachmentOffset.Base.x
  expr: Constraints[16] = <<Sketch067>>.Constraints.length
  expr: Constraints[23] = <<Sketch067>>.Constraints.bend_length + 6 mm
  sketch-geometry (8):
    g0: LineSegment StartX=8.3238e-12 StartY=6 StartZ=0 EndX=-9.1 EndY=6 EndZ=0
    g1: LineSegment StartX=-9.1 StartY=6 StartZ=0 EndX=-9.1 EndY=9.1 EndZ=0
    g2: LineSegment StartX=-9.1 StartY=9.1 StartZ=0 EndX=-9.1 EndY=9.1 EndZ=0
    g3: LineSegment StartX=-3 StartY=220 StartZ=0 EndX=0 EndY=220 EndZ=0
    g4: LineSegment StartX=0 StartY=220 StartZ=0 EndX=8.3238e-12 EndY=6 EndZ=0
    g5: LineSegment StartX=-9.1 StartY=9.1 StartZ=0 EndX=-9.1 EndY=201 EndZ=0
    g6: LineSegment StartX=-9.1 StartY=201 StartZ=0 EndX=-3 EndY=201 EndZ=0
    g7: LineSegment StartX=-3 StartY=201 StartZ=0 EndX=-3 EndY=220 EndZ=0
  constraints (24):
    c: PointOnObject(g0,g-2)
    c: Horizontal(g0)
    c: Coincident(g0,g1)
    c: Coincident(g1,g2)
    c: Coincident(g2,g5)
    c: Coincident(g7,g3)
    c: PointOnObject(g3,g-2)
    c: Horizontal(g3)
    c: Coincident(g3,g4)
    c: Coincident(g4,g0)
    c: DistanceX(g0,g0) = 9.1
    c: Vertical(g1)
    c: DistanceY(g0) = 6
    c: DistanceY(g1,g1) = 3.1
    c: Horizontal(g2)
    c: DistanceX(g2) = -9.1
    c: DistanceY(g3) = 220
    c: Coincident(g5,g6)
    c: Vertical(g5)
    c: Coincident(g6,g7)
    c: Vertical(g7)
    c: Horizontal(g6)
    c: DistanceX(g3,g3) = 3
    c: DistanceY(g-1,g6) = 201
FEATURE [PartDesign::Pocket] Pocket013
  BaseFeature = -> Pocket012
  Direction = (0,0,-1)
  Length = 3
  Length2 = 100
  Profile = -> Sketch068
  ReferenceAxis = -> Sketch068 [N_Axis]
  Suppressed = false
  Type = 4
FEATURE [Part::FeaturePython] BaseBend013  # WARN: FeaturePython — macro-defined, semantics opaque (R4)
  BendSide = 1
  BendSketch = -> Sketch066
  MidPlane = false
  Reverse = true
  length = 188
  radius = 0.1
  thickness = 0.3
  expr: length = <<BaseBend011>>.length - 3 mm
FEATURE [PartDesign::Mirrored] Mirrored003
  BaseFeature = -> Pocket013
  MirrorPlane = -> YZ_Plane014
  Originals = -> [Pocket012,Pocket013]
  Suppressed = false
FEATURE [Sketcher::SketchObject] Sketch069
  ExternalGeometry = -> [Sketch066]
  FullyConstrained = true
  Placement = pos=(-310.563,9.1,6) rot=(1,0,0;1.5708rad)
  expr: .Placement.Base.x = -<<Sketch066>>.Placement.Base.x
  expr: .Placement.Base.y = <<Sketch066>>.Placement.Base.y
  expr: .Placement.Base.z = <<Sketch066>>.Placement.Base.z
  expr: .Placement.Rotation.Angle = <<Sketch066>>.Placement.Rotation.Angle
  expr: .Placement.Rotation.Axis = <<Sketch066>>.Placement.Rotation.Axis
  sketch-geometry (2):
    g0: LineSegment StartX=0 StartY=12 StartZ=0 EndX=0 EndY=0 EndZ=0
    g1: LineSegment StartX=0 StartY=0 StartZ=0 EndX=20.1122 EndY=0 EndZ=0
  constraints (6):
    c: PointOnObject(g0,g-2)
    c: Coincident(g0,g-1)
    c: Coincident(g1,g0)
    c: PointOnObject(g1,g-1)
    c: Horizontal(g-3,g0)
    c: Equal(g-4,g1)
FEATURE [Part::FeaturePython] BaseBend014  # WARN: FeaturePython — macro-defined, semantics opaque (R4)
  BendSide = 0
  BendSketch = -> Sketch069
  MidPlane = false
  Reverse = true
  length = 188
  radius = 0.1
  thickness = 0.3
  expr: length = <<BaseBend013>>.length
FEATURE [Part::Compound] Compound018
  Links = -> [BaseBend011,BaseBend012,BaseBend013,BaseBend014]
FEATURE [PartDesign::Boolean] Boolean013
  BaseFeature = -> Mirrored003
  Group = -> [Compound018]
  Refine = true
  Suppressed = false
  Type = 0
  UsePlacement = true
FEATURE [Part::Compound] Compound019
  Links = -> [Populate025,Populate024]
FEATURE [PartDesign::Boolean] Boolean014
  BaseFeature = -> Boolean013
  Group = -> [Compound019]
  Suppressed = false
  Type = 1
  UsePlacement = true
FEATURE [Part::FeaturePython] LinearArray009  # WARN: FeaturePython — macro-defined, semantics opaque (R4)
  Alignment = 0
  CellStart = A1
  Count = 3
  Dir = (1,0,0)
  DirIsDriven = true
  DistributionLaw = 0
  DrivenProperty = 1
  EndInclusive = true
  ExposePlacement = false
  GeneratorMode = 0
  MarkerShape = 1
  MarkerSize = 0
  NumElements = 3
  OrientMode = 1
  Point = (0,0,0)
  PointIsDriven = true
  Reverse = false
  SpanEnd = 207
  SpanStart = 10
  Step = 98.5
  Type = lattice2LinearArray.LinearArray
  VSGVersion = 1
  Values = 10.0 | 108.49999999995704 | 206.99999999991408
  ValuesSource = 2
  isLattice = 1
  expr: SpanEnd = <<Sketch063>>.Constraints.plane_length - SpanStart
FEATURE [Sketcher::SketchObject] Sketch070  label="rail_base_sketch"
  FullyConstrained = true
  expr: .Constraints.length = <<Sketch063>>.Constraints.plane_length
  sketch-geometry (5):
    g0: LineSegment StartX=217 StartY=10 StartZ=0 EndX=0 EndY=10 EndZ=0
    g1: LineSegment StartX=0 StartY=10 StartZ=0 EndX=0 EndY=-10 EndZ=0
    g2: LineSegment StartX=0 StartY=-10 StartZ=0 EndX=217 EndY=-10 EndZ=0
    g3: LineSegment StartX=217 StartY=-10 StartZ=0 EndX=217 EndY=10 EndZ=0
    g4: GeomPoint X=108.5 Y=0 Z=0
  constraints (13):
    c: Coincident(g0,g1)
    c: Coincident(g1,g2)
    c: Coincident(g2,g3)
    c: Coincident(g3,g0)
    c: Horizontal(g0)
    c: Horizontal(g2)
    c: Vertical(g1)
    c: Vertical(g3)
    c: Symmetric(g2,g0,g4)
    c: PointOnObject(g4,g-1)
    c: PointOnObject(g1,g-2)
    c: DistanceX(g0,g0) = 217  'length'
    c: DistanceY(g1,g1) = 20  'width'
FEATURE [Sketcher::SketchObject] Sketch071
  AttachmentOffset = pos=(0,-6,0) rot=(0,0,1;0rad)
  FullyConstrained = true
  MapMode = 5
  Placement = pos=(0,-1e-15,-6) rot=(1,0,0;1.5708rad)
  sketch-geometry (6):
    g0: LineSegment StartX=0 StartY=0 StartZ=0 EndX=4 EndY=0 EndZ=0
    g1: LineSegment StartX=4 StartY=0 StartZ=0 EndX=4 EndY=3 EndZ=0
    g2: LineSegment StartX=4 StartY=3 StartZ=0 EndX=1.7 EndY=3 EndZ=0
    g3: LineSegment StartX=1.7 StartY=3 StartZ=0 EndX=1.7 EndY=6 EndZ=0
    g4: LineSegment StartX=1.7 StartY=6 StartZ=0 EndX=0 EndY=6 EndZ=0
    g5: LineSegment StartX=0 StartY=6 StartZ=0 EndX=0 EndY=0 EndZ=0
  constraints (17):
    c: Coincident(g-1,g0)
    c: Horizontal(g0)
    c: Coincident(g0,g1)
    c: Vertical(g1)
    c: Coincident(g1,g2)
    c: Horizontal(g2)
    c: Coincident(g2,g3)
    c: Vertical(g3)
    c: Coincident(g3,g4)
    c: PointOnObject(g4,g-2)
    c: Horizontal(g4)
    c: Coincident(g4,g5)
    c: Coincident(g5,g0)
    c: DistanceY(g1) = 3
    c: DistanceY(g4) = 6
    c: DistanceX(g3) = 1.7
    c: DistanceX(g0) = 4
FEATURE [PartDesign::Revolution] Revolution
  Angle = 360
  Angle2 = 60
  Axis = (0,2e-16,1)
  Base = (0,-1e-15,-6)
  Placement = pos=(0,-1e-15,-6) rot=(1,0,0;1.5708rad)
  Profile = -> Sketch071
  ReferenceAxis = -> Sketch071 [V_Axis]
  Reversed = true
  Suppressed = false
  Type = 0
FEATURE [PartDesign::Body] Body015  label="Body"
  Group = -> [Sketch071,Revolution]
  Origin = -> Origin015
  Tip = -> Revolution
FEATURE [Part::FeaturePython] LinearArray010  # WARN: FeaturePython — macro-defined, semantics opaque (R4)
  Alignment = 0
  CellStart = A1
  Count = 3
  Dir = (0,1,0)
  DirIsDriven = true
  DistributionLaw = 0
  DrivenProperty = 1
  EndInclusive = true
  ExposePlacement = false
  GeneratorMode = 0
  MarkerShape = 1
  MarkerSize = 0
  NumElements = 3
  OrientMode = 0
  Placement = pos=(200,9,6) rot=(0,0,1;1.5708rad)
  Point = (0,0,0)
  PointIsDriven = true
  Reverse = false
  SpanEnd = 400
  SpanStart = 0
  Step = 200
  Type = lattice2LinearArray.LinearArray
  VSGVersion = 1
  Values = 0.0 | 200.0 | 400.0
  ValuesSource = 2
  isLattice = 1
  expr: .Placement.Base.x = SpanEnd / 2
FEATURE [PartDesign::SubShapeBinder] Binder019
  BindCopyOnChange = 0
  BindMode = 0
  ClaimChildren = true
  Context = -> Body016 [Binder019.]
  Fuse = false
  MakeFace = true
  OffsetFill = false
  OffsetIntersection = false
  OffsetJoinType = 0
  OffsetOpenResult = false
  PartialLoad = false
  Relative = false
  Support = -> [Sketch070]
  _Version = 2
FEATURE [PartDesign::Pad] Pad018
  Direction = (0,0,1)
  Length = 5
  Length2 = 10
  Profile = -> Binder019
  Suppressed = false
  Type = 0
FEATURE [Sketcher::SketchObject] Sketch072
  FullyConstrained = true
  MapMode = 5
  Placement = pos=(0,0,0) rot=(1,0,0;1.5708rad)
  sketch-geometry (6):
    g0: LineSegment StartX=0 StartY=0 StartZ=0 EndX=1.7 EndY=0 EndZ=0
    g1: LineSegment StartX=1.7 StartY=0 StartZ=0 EndX=1.7 EndY=2.5 EndZ=0
    g2: LineSegment StartX=1.7 StartY=2.5 StartZ=0 EndX=4 EndY=2.5 EndZ=0
    g3: LineSegment StartX=4 StartY=2.5 StartZ=0 EndX=4 EndY=5 EndZ=0
    g4: LineSegment StartX=4 StartY=5 StartZ=0 EndX=0 EndY=5 EndZ=0
    g5: LineSegment StartX=0 StartY=5 StartZ=0 EndX=0 EndY=0 EndZ=0
  constraints (17):
    c: Coincident(g-1,g0)
    c: PointOnObject(g0,g-1)
    c: Coincident(g0,g1)
    c: Vertical(g1)
    c: Coincident(g1,g2)
    c: Horizontal(g2)
    c: Coincident(g2,g3)
    c: Vertical(g3)
    c: Coincident(g3,g4)
    c: Horizontal(g4)
    c: Coincident(g4,g5)
    c: Coincident(g5,g0)
    c: Vertical(g5)
    c: DistanceX(g0) = 1.7
    c: DistanceY(g5,g5) = 5
    c: DistanceY(g1,g1) = 2.5
    c: DistanceX(g4,g4) = 4
FEATURE [PartDesign::Revolution] Revolution001
  Angle = 360
  Angle2 = 60
  Axis = (0,2e-16,1)
  Base = (0,0,0)
  Placement = pos=(0,0,0) rot=(1,0,0;1.5708rad)
  Profile = -> Sketch072
  ReferenceAxis = -> Sketch072 [V_Axis]
  Reversed = true
  Suppressed = false
  Type = 0
FEATURE [PartDesign::Body] Body017
  Group = -> [Sketch072,Revolution001]
  Origin = -> Origin017
  Tip = -> Revolution001
FEATURE [Part::FeaturePython] Populate028  label="Populate LinearArray009 with Body017"  # WARN: FeaturePython — macro-defined, semantics opaque (R4)
  Copying = 0
  ExposePlacement = false
  MarkerShape = 1
  MarkerSize = 0
  NumElements = 0
  Object = -> Body017
  OutputCompounding = 1
  PlacementsTo = -> LinearArray009
  Referencing = 0
  Type = lattice2PopulateCopies.LatticePopulateCopies
  isLattice = 0
FEATURE [Part::Compound] Compound020
  Links = -> [Populate028]
FEATURE [PartDesign::Boolean] Boolean015
  BaseFeature = -> Pad018
  Group = -> [Compound020]
  Suppressed = false
  Type = 1
  UsePlacement = true
FEATURE [PartDesign::SubShapeBinder] Binder020
  BindCopyOnChange = 0
  BindMode = 0
  ClaimChildren = true
  Fuse = false
  MakeFace = true
  OffsetFill = false
  OffsetIntersection = false
  OffsetJoinType = 0
  OffsetOpenResult = false
  PartialLoad = false
  Placement = pos=(0,90,0) rot=(0,0,1;0rad)
  Relative = true
  Support = -> [Sketch001]
  _Version = 2
  expr: Support = <<base_sketch>>._self
FEATURE [Sketcher::SketchObject] Sketch002  label="side_sketch"
  ExternalGeometry = -> [Binder020]
  FullyConstrained = true
  sketch-geometry (1):
    g0: LineSegment StartX=319.563 StartY=220 StartZ=0 EndX=319.563 EndY=0 EndZ=0
  constraints (3):
    c: PointOnObject(g0,g-1)
    c: Vertical(g0)
    c: Coincident(g0,g-3)
FEATURE [Part::Compound] Compound
  Links = -> [Sketch002,Binder020]
FEATURE [Part::Mirroring] Part__Mirroring  label="Compound (Mirror #1)"
  Base = (0,0,0)
  Normal = (1,0,0)
  Source = -> Compound
FEATURE [Part::FeaturePython] Connect  # WARN: FeaturePython — macro-defined, semantics opaque (R4)
  Objects = -> [Compound,Part__Mirroring]
  Tolerance = 0
FEATURE [Sketcher::SketchObject] Sketch003  label="back_base_sketch"
  ExternalGeometry = -> [Sketch002]
  FullyConstrained = true
  sketch-geometry (3):
    g0: LineSegment StartX=0 StartY=0 StartZ=0 EndX=316.563 EndY=0 EndZ=0
    g1: LineSegment StartX=316.563 StartY=0 StartZ=0 EndX=316.563 EndY=15 EndZ=0
    g2: GeomPoint X=-316.563 Y=0 Z=0
  constraints (8):
    c: Coincident(g-1,g0)
    c: PointOnObject(g0,g-1)
    c: Coincident(g0,g1)
    c: Vertical(g1)
    c: DistanceX(g0,g-3) = 3
    c: DistanceY(g1,g1) = 15  'side'
    c: Symmetric(g2,g0,g-2)
    c: DistanceX(g2,g0) = 633.126  'length'
FEATURE [Part::Mirroring] Part__Mirroring001  label="Sketch003 (Mirror #2)"
  Base = (0,0,0)
  Normal = (1,0,0)
  Source = -> Sketch003
FEATURE [Part::FeaturePython] Connect001  # WARN: FeaturePython — macro-defined, semantics opaque (R4)
  Objects = -> [Sketch003,Part__Mirroring001]
  Tolerance = 0
FEATURE [Sketcher::SketchObject] Sketch004
  ExternalGeometry = -> [Sketch002,Binder020]
  FullyConstrained = true
  sketch-geometry (8):
    g0: LineSegment StartX=319.063 StartY=3 StartZ=0 EndX=319.063 EndY=218.809 EndZ=0
    g1: LineSegment StartX=319.063 StartY=218.809 StartZ=0 EndX=304.563 EndY=187.714 EndZ=0
    g2: LineSegment StartX=304.563 StartY=187.714 StartZ=0 EndX=304.563 EndY=12 EndZ=0
    g3: LineSegment StartX=164.635 StartY=90 StartZ=0 EndX=225.255 EndY=17.7559 EndZ=0
    g4: LineSegment StartX=225.255 StartY=17.7559 StartZ=0 EndX=319.563 EndY=17.7559 EndZ=0
    g5: LineSegment StartX=225.255 StartY=17.7559 StartZ=0 EndX=319.563 EndY=220 EndZ=0
    g6: LineSegment StartX=304.563 StartY=12 StartZ=0 EndX=313.563 EndY=3 EndZ=0
    g7: LineSegment StartX=313.563 StartY=3 StartZ=0 EndX=319.063 EndY=3 EndZ=0
  constraints (23):
    c: Coincident(g0,g1)
    c: Coincident(g1,g2)
    c: Coincident(g2,g6)
    c: Coincident(g7,g0)
    c: Vertical(g0)
    c: Vertical(g2)
    c: DistanceX(g0,g-3) = 0.5
    c: DistanceX(g2,g-3) = 15
    c: Coincident(g4,g3)
    c: PointOnObject(g4,g-3)
    c: Perpendicular(g-3,g4)
    c: Equal(g4,g3)
    c: Coincident(g5,g3)
    c: Parallel(g1,g5)
    c: DistanceY(g-3,g0) = 3
    c: Distance(g1,g5) = 0.05
    c: Coincident(g5,g-4)
    c: Coincident(g3,g-4)
    c: Perpendicular(g-4,g3)
    c: Coincident(g6,g7)
    c: Horizontal(g7)
    c: DistanceX(g6,g-3) = 6
    c: Angle(g6) = -0.785398
FEATURE [Sketcher::SketchObject] Sketch009
  ExternalGeometry = -> [Sketch002]
  FullyConstrained = true
  sketch-geometry (8):
    g0: LineSegment StartX=316.563 StartY=45 StartZ=0 EndX=313.363 EndY=45 EndZ=0
    g1: LineSegment StartX=313.363 StartY=30 StartZ=0 EndX=316.563 EndY=30 EndZ=0
    g2: LineSegment StartX=313.363 StartY=41.8 StartZ=0 EndX=313.363 EndY=33.2 EndZ=0
    g3: LineSegment StartX=316.563 StartY=33.2 StartZ=0 EndX=316.563 EndY=41.8 EndZ=0
    g4: ArcOfCircle CenterX=316.563 CenterY=43.4 CenterZ=0 NormalX=0 NormalY=0 NormalZ=1 AngleXU=0 Radius=1.6 StartAngle=4.71239 EndAngle=7.85398
    g5: ArcOfCircle CenterX=313.363 CenterY=43.4 CenterZ=0 NormalX=0 NormalY=0 NormalZ=1 AngleXU=0 Radius=1.6 StartAngle=1.5708 EndAngle=4.71239
    g6: ArcOfCircle CenterX=313.363 CenterY=31.6 CenterZ=0 NormalX=0 NormalY=0 NormalZ=1 AngleXU=0 Radius=1.6 StartAngle=1.5708 EndAngle=4.71239
    g7: ArcOfCircle CenterX=316.563 CenterY=31.6 CenterZ=0 NormalX=0 NormalY=0 NormalZ=1 AngleXU=0 Radius=1.6 StartAngle=4.71239 EndAngle=7.85398
  constraints (24):
    c: Horizontal(g0)
    c: Horizontal(g1)
    c: DistanceX(g1,g-3) = 3
    c: Vertical(g2)
    c: Vertical(g3)
    c: Coincident(g4,g3)
    c: Coincident(g5,g2)
    c: Coincident(g6,g2)
    c: Coincident(g7,g3)
    c: Tangent(g7,g1) = -1.5708
    c: Tangent(g6,g1) = -1.5708
    c: Tangent(g4,g0) = -1.5708
    c: Tangent(g5,g0) = -1.5708
    c: Perpendicular(g7,g3)
    c: Perpendicular(g6,g2)
    c: Perpendicular(g4,g3)
    c: Perpendicular(g5,g2)
    c: Equal(g6,g7)
    c: Equal(g6,g4)
    c: Equal(g6,g5)
    c: Diameter(g6) = 3.2
    c: DistanceY(g1,g0) = 15
    c: DistanceY(g-3,g1) = 30
    c: DistanceX(g2,g3) = 3.2
FEATURE [Part::Mirroring] Part__Mirroring006  label="Sketch009 (Mirror #7)"
  Base = (0,0,0)
  Normal = (1,0,0)
  Source = -> Sketch009
FEATURE [Part::FeaturePython] Connect005  # WARN: FeaturePython — macro-defined, semantics opaque (R4)
  Objects = -> [Sketch009,Part__Mirroring006]
  Tolerance = 0
FEATURE [Part::Extrusion] Extrude009
  Base = -> Connect005
  Dir = (0,0,1)
  DirMode = 2
  FaceMakerClass = Part::FaceMakerBullseye
  LengthFwd = 10
  LengthRev = 0
  Solid = true
  Symmetric = false
FEATURE [Sketcher::SketchObject] Sketch018
  ExternalGeometry = -> [Sketch004,Binder020]
  FullyConstrained = true
  sketch-geometry (10):
    g0: LineSegment StartX=319.008 StartY=218.809 StartZ=0 EndX=318.651 EndY=219.235 EndZ=0
    g1: LineSegment StartX=318.651 StartY=219.235 StartZ=0 EndX=319.563 EndY=220 EndZ=0
    g2: LineSegment StartX=319.563 StartY=220 StartZ=0 EndX=319.563 EndY=218.809 EndZ=0
    g3: LineSegment StartX=319.563 StartY=218.809 StartZ=0 EndX=319.008 EndY=218.809 EndZ=0
    g4: LineSegment StartX=164.635 StartY=90 StartZ=0 EndX=162.935 EndY=90 EndZ=0
    g5: LineSegment StartX=162.935 StartY=90 StartZ=0 EndX=162.935 EndY=89.5 EndZ=0
    g6: LineSegment StartX=162.935 StartY=89.5 StartZ=0 EndX=164.817 EndY=89.5 EndZ=0
    g7: LineSegment StartX=164.817 StartY=89.5 StartZ=0 EndX=166.259 EndY=90.7097 EndZ=0
    g8: LineSegment StartX=166.259 StartY=90.7097 StartZ=0 EndX=165.937 EndY=91.0927 EndZ=0
    g9: LineSegment StartX=165.937 StartY=91.0927 StartZ=0 EndX=164.635 EndY=90 EndZ=0
  constraints (28):
    c: PointOnObject(g0,g-4)
    c: Coincident(g0,g1)
    c: Coincident(g1,g-4)
    c: Coincident(g1,g2)
    c: Vertical(g2)
    c: Coincident(g2,g3)
    c: Horizontal(g3)
    c: Perpendicular(g1,g0)
    c: Coincident(g3,g0)
    c: PointOnObject(g-3,g3)
    c: Equal(g3,g0)
    c: Coincident(g-4,g4)
    c: Horizontal(g4)
    c: Coincident(g4,g5)
    c: Vertical(g5)
    c: Coincident(g5,g6)
    c: Horizontal(g6)
    c: Coincident(g6,g7)
    c: Coincident(g7,g8)
    c: PointOnObject(g8,g-4)
    c: Coincident(g8,g9)
    c: Coincident(g9,g4)
    c: Equal(g9,g4)
    c: Perpendicular(g9,g8)
    c: Perpendicular(g8,g7)
    c: Equal(g5,g8)
    c: DistanceY(g5,g5) = 0.5
    c: Distance(g9) = 1.7
FEATURE [Part::Extrusion] Extrude010
  Base = -> Sketch018
  Dir = (0,0,1)
  DirMode = 2
  FaceMakerClass = Part::FaceMakerBullseye
  LengthFwd = 0.4
  LengthRev = 0
  Placement = pos=(0,0,813) rot=(0,0,1;0rad)
  Solid = true
  Symmetric = false
  expr: .Placement.Base.z = <<BaseBend>>.length
FEATURE [Part::Mirroring] Part__Mirroring007  label="Extrude010 (Mirror #8)"
  Base = (0,0,0)
  Normal = (1,0,0)
  Source = -> Extrude010
FEATURE [Sketcher::SketchObject] Sketch073  label="Dimensions_sketch"
  ExternalGeometry = -> [Binder020]
  FullyConstrained = true
  expr: .Constraints.angle = 40
  expr: .Constraints.face_width = <<base_sketch>>.Constraints.face_width
  expr: .Constraints.total_width = <<base_sketch>>.Constraints.total_width
  sketch-geometry (7):
    g0: LineSegment StartX=0 StartY=90 StartZ=0 EndX=164.635 EndY=90 EndZ=0
    g1: LineSegment StartX=164.635 StartY=90 StartZ=0 EndX=319.563 EndY=220 EndZ=0
    g2: LineSegment StartX=319.563 StartY=220 StartZ=0 EndX=319.563 EndY=0 EndZ=0
    g3: LineSegment StartX=319.563 StartY=0 StartZ=0 EndX=0 EndY=0 EndZ=0
    g4: GeomPoint X=-164.635 Y=90 Z=0
    g5: GeomPoint X=-319.563 Y=220 Z=0
    g6: GeomPoint X=-319.563 Y=0 Z=0
  constraints (17):
    c: PointOnObject(g0,g-2)
    c: Horizontal(g0)
    c: Coincident(g0,g1)
    c: Coincident(g1,g2)
    c: PointOnObject(g2,g-1)
    c: Vertical(g2)
    c: Coincident(g2,g3)
    c: Coincident(g3,g-1)
    c: Symmetric(g6,g2,g-2)
    c: Symmetric(g4,g0,g-2)
    c: Symmetric(g5,g1,g-2)
    c: DistanceX(g4,g0) = 329.27  'face_width'
    c: DistanceX(g6,g2) = 639.126  'total_width'
    c: Angle(g1) = 0.698132  'angle'
    c: Horizontal(g0,g-3)
    c: DistanceY(g2,g2) = 220  'total_depth'
    c: DistanceY(g0) = 90  'offset'
FEATURE [Part::Compound] Compound021
  Links = -> [Sketch016,Sketch017]
  Placement = pos=(0,90,0) rot=(0,0,1;0rad)
  expr: .Placement.Base.y = <<Dimensions_sketch>>.Constraints.offset
FEATURE [Part::Compound] Compound009
  Links = -> [Sketch004,Compound021]
FEATURE [Part::Mirroring] Part__Mirroring005  label="Compound009 (Mirror #6)"
  Base = (0,0,0)
  Normal = (1,0,0)
  Source = -> Compound009
FEATURE [Part::FeaturePython] Connect004  # WARN: FeaturePython — macro-defined, semantics opaque (R4)
  Objects = -> [Compound009,Part__Mirroring005]
  Tolerance = 0
FEATURE [Part::Extrusion] Extrude008
  Base = -> Connect004
  Dir = (0,0,1)
  DirMode = 2
  FaceMakerClass = Part::FaceMakerBullseye
  LengthFwd = 0.3
  LengthRev = 0
  Solid = true
  Symmetric = false
  expr: LengthFwd = <<BaseBend>>.thickness
FEATURE [App::DocumentObjectGroup] Group006  label="sketches"
  Group = -> [Sketch,Sketch057,Sketch058,Sketch073,Sketch033]
FEATURE [Part::Mirroring] Part__Mirroring016  label="Sketch020 (Mirror #16)"
  Base = (0,0,0)
  Normal = (1,0,0)
  Source = -> Sketch020
FEATURE [Part::Compound] Compound022
  Links = -> [Part__Mirroring016,Sketch020]
FEATURE [Part::Extrusion] Extrude019
  Base = -> Compound022
  Dir = (0,0,1)
  DirMode = 2
  FaceMakerClass = Part::FaceMakerBullseye
  LengthFwd = 10
  LengthRev = 0
  Solid = true
  Symmetric = false
FEATURE [Part::FeaturePython] Placment020  # WARN: FeaturePython — macro-defined, semantics opaque (R4)
  AttacherType = Attacher::AttachEngine3D
  ExposePlacement = true
  MarkerShape = 1
  MarkerSize = 20
  NumElements = 1
  Placement = pos=(0,90,0) rot=(0,0,1;0rad)
  Type = lattice2AttachablePlacement.AttachablePlacement
  isLattice = 1
  expr: .Placement.Base.y = <<Dimensions_sketch>>.Constraints.offset
FEATURE [Part::FeaturePython] Populate029  label="Populate Placment020 with Extrude019"  # WARN: FeaturePython — macro-defined, semantics opaque (R4)
  Copying = 0
  ExposePlacement = false
  MarkerShape = 1
  MarkerSize = 0
  NumElements = 0
  Object = -> Extrude019
  OutputCompounding = 2
  PlacementsTo = -> Placment020
  Referencing = 0
  Type = lattice2PopulateCopies.LatticePopulateCopies
  isLattice = 0
FEATURE [Part::Extrusion] Extrude020
  Base = -> Sketch019
  Dir = (0,0,1)
  DirMode = 2
  FaceMakerClass = Part::FaceMakerBullseye
  LengthFwd = 10
  LengthRev = 0
  Solid = true
  Symmetric = false
FEATURE [Sketcher::SketchObject] Sketch074
  AttachmentOffset = pos=(319.563,0,0) rot=(0,0,1;0rad)
  FullyConstrained = true
  MapMode = 5
  Placement = pos=(319.563,0,0) rot=(0,0,1;0rad)
  expr: .AttachmentOffset.Base.x = <<Sketch067>>.AttachmentOffset.Base.x
  sketch-geometry (4):
    g0: LineSegment StartX=0 StartY=0 StartZ=0 EndX=0 EndY=15 EndZ=0
    g1: LineSegment StartX=0 StartY=15 StartZ=0 EndX=-6 EndY=15 EndZ=0
    g2: LineSegment StartX=-6 StartY=15 StartZ=0 EndX=-6 EndY=0 EndZ=0
    g3: LineSegment StartX=-6 StartY=0 StartZ=0 EndX=0 EndY=0 EndZ=0
  constraints (11):
    c: Coincident(g0,g1)
    c: Coincident(g1,g2)
    c: Coincident(g2,g3)
    c: Coincident(g3,g0)
    c: Vertical(g0)
    c: Vertical(g2)
    c: Horizontal(g1)
    c: Horizontal(g3)
    c: Coincident(g0,g-1)
    c: DistanceY(g0) = 15
    c: DistanceX(g1) = -6
FEATURE [PartDesign::Pocket] Pocket014
  BaseFeature = -> Boolean014
  Direction = (0,0,-1)
  Length = 5
  Length2 = 5
  Midplane = true
  Profile = -> Sketch074
  ReferenceAxis = -> Sketch074 [N_Axis]
  Suppressed = false
  Type = 1
FEATURE [PartDesign::Mirrored] Mirrored004
  BaseFeature = -> Pocket014
  MirrorPlane = -> YZ_Plane014
  Originals = -> [Pocket014]
  Suppressed = false
FEATURE [Sketcher::SketchObject] Sketch076
  FullyConstrained = true
  expr: Constraints[6] = <<Dimensions_sketch>>.Constraints.angle
  expr: Constraints[7] = <<magnet_fix>>#<<Properties>>.width - 2 mm
  sketch-geometry (3):
    g0: LineSegment StartX=0 StartY=-14.6 StartZ=0 EndX=0 EndY=0 EndZ=0
    g1: LineSegment StartX=0 StartY=0 StartZ=0 EndX=17.3996 EndY=0 EndZ=0
    g2: LineSegment StartX=0 StartY=-14.6 StartZ=0 EndX=17.3996 EndY=1.8e-15 EndZ=0
  constraints (8):
    c: PointOnObject(g0,g-2)
    c: Coincident(g0,g-1)
    c: Coincident(g0,g1)
    c: PointOnObject(g1,g-1)
    c: Coincident(g2,g0)
    c: Coincident(g2,g1)
    c: Angle(g2) = 0.698132
    c: DistanceY(g0,g0) = 14.6
FEATURE [PartDesign::SubShapeBinder] Binder022
  BindCopyOnChange = 0
  BindMode = 0
  ClaimChildren = true
  Context = -> Body019 [Binder022.]
  Fuse = false
  MakeFace = true
  OffsetFill = false
  OffsetIntersection = false
  OffsetJoinType = 0
  OffsetOpenResult = false
  PartialLoad = false
  Relative = false
  Support = -> [Sketch076]
  _Version = 2
FEATURE [PartDesign::Pad] Pad019
  Direction = (0,0,1)
  Length = 41.3
  Length2 = 10
  Profile = -> Binder022
  Suppressed = false
  Type = 0
  expr: Length = <<magnet_fix>>#<<Properties>>.length
FEATURE [Sketcher::SketchObject] Sketch077
  FullyConstrained = true
  MapMode = 5
  Placement = pos=(0,0,0) rot=(1,0,0;1.5708rad)
  sketch-geometry (6):
    g0: LineSegment StartX=0 StartY=20 StartZ=0 EndX=4 EndY=20 EndZ=0
    g1: LineSegment StartX=4 StartY=20 StartZ=0 EndX=4 EndY=3 EndZ=0
    g2: LineSegment StartX=4 StartY=3 StartZ=0 EndX=1.7 EndY=3 EndZ=0
    g3: LineSegment StartX=1.7 StartY=3 StartZ=0 EndX=1.7 EndY=-3 EndZ=0
    g4: LineSegment StartX=1.7 StartY=-3 StartZ=0 EndX=0 EndY=-3 EndZ=0
    g5: LineSegment StartX=0 StartY=-3 StartZ=0 EndX=0 EndY=20 EndZ=0
  constraints (18):
    c: PointOnObject(g0,g-2)
    c: Horizontal(g0)
    c: Coincident(g0,g1)
    c: Vertical(g1)
    c: Coincident(g1,g2)
    c: Horizontal(g2)
    c: Coincident(g2,g3)
    c: Vertical(g3)
    c: Coincident(g3,g4)
    c: PointOnObject(g4,g-2)
    c: Horizontal(g4)
    c: Coincident(g4,g5)
    c: Coincident(g5,g0)
    c: DistanceY(g4) = -3
    c: DistanceX(g3) = 1.7
    c: DistanceY(g2) = 3
    c: DistanceX(g1) = 4
    c: DistanceY(g0) = 20
FEATURE [PartDesign::Revolution] Revolution002
  Angle = 360
  Angle2 = 60
  Axis = (0,2e-16,1)
  Base = (0,0,0)
  Placement = pos=(0,0,0) rot=(1,0,0;1.5708rad)
  Profile = -> Sketch077
  ReferenceAxis = -> Sketch077 [V_Axis]
  Reversed = true
  Suppressed = false
  Type = 0
FEATURE [PartDesign::Body] Body020
  Group = -> [Sketch077,Revolution002]
  Origin = -> Origin020
  Tip = -> Revolution002
FEATURE [Part::FeaturePython] Placment022  # WARN: FeaturePython — macro-defined, semantics opaque (R4)
  AttacherType = Attacher::AttachEngine3D
  AttachmentOffset = pos=(0,0,0) rot=(0.57735,0.57735,0.57735;2.0944rad)
  ExposePlacement = true
  MapMode = 45
  MarkerShape = 1
  MarkerSize = 10
  NumElements = 1
  Placement = pos=(8.6998,-7.3,0) rot=(-0.389282,-0.834817,-0.389282;1.75037rad)
  Type = lattice2AttachablePlacement.AttachablePlacement
  isLattice = 1
FEATURE [Part::FeaturePython] LinearArray013  # WARN: FeaturePython — macro-defined, semantics opaque (R4)
  Alignment = 0
  CellStart = A1
  Count = 2
  Dir = (1,0,0)
  DirIsDriven = true
  DistributionLaw = 0
  DrivenProperty = 1
  EndInclusive = true
  ExposePlacement = false
  GeneratorMode = 0
  MarkerShape = 1
  MarkerSize = 0
  NumElements = 2
  OrientMode = 1
  Point = (0,0,0)
  PointIsDriven = true
  Reverse = false
  SpanEnd = 31.3
  SpanStart = 10
  Step = 21.3
  Type = lattice2LinearArray.LinearArray
  VSGVersion = 1
  Values = 10.0 | 31.299999999999997
  ValuesSource = 2
  isLattice = 1
  expr: SpanEnd = <<Pad019>>.Length - SpanStart
FEATURE [Part::FeaturePython] Populate036  label="Populate Placment022 with LinearArray013"  # WARN: FeaturePython — macro-defined, semantics opaque (R4)
  Copying = 0
  ExposePlacement = false
  MarkerShape = 1
  MarkerSize = 0
  NumElements = 2
  Object = -> LinearArray013
  OutputCompounding = 0
  PlacementsTo = -> Placment022
  Referencing = 0
  Type = lattice2PopulateCopies.LatticePopulateCopies
  isLattice = 1
FEATURE [Part::FeaturePython] Populate037  label="Populate Populate Placment022 with LinearArray013 with Body020"  # WARN: FeaturePython — macro-defined, semantics opaque (R4)
  Copying = 0
  ExposePlacement = false
  MarkerShape = 1
  MarkerSize = 0
  NumElements = 0
  Object = -> Body020
  OutputCompounding = 1
  PlacementsTo = -> Populate036
  Referencing = 0
  Type = lattice2PopulateCopies.LatticePopulateCopies
  isLattice = 0
FEATURE [PartDesign::SubShapeBinder] Binder023
  BindCopyOnChange = 0
  BindMode = 0
  ClaimChildren = false
  Fuse = false
  MakeFace = true
  OffsetFill = false
  OffsetIntersection = false
  OffsetJoinType = 0
  OffsetOpenResult = false
  PartialLoad = false
  Relative = true
  Support = -> [<external ../magnet_fix.FCStd>#Sketch002]
  _Version = 2
  expr: Support = magnet_fix#Sketch002._self
FEATURE [Sketcher::SketchObject] Sketch078
  ExternalGeometry = -> [Binder023]
  FullyConstrained = true
  sketch-geometry (2):
    g0: Circle CenterX=17 CenterY=0 CenterZ=0 NormalX=0 NormalY=0 NormalZ=1 AngleXU=0 Radius=1
    g1: Circle CenterX=-17 CenterY=0 CenterZ=0 NormalX=0 NormalY=0 NormalZ=1 AngleXU=0 Radius=1
  constraints (5):
    c: PointOnObject(g0,g-1)
    c: Vertical(g0,g-3)
    c: Diameter(g0) = 2
    c: Equal(g0,g1)
    c: Symmetric(g1,g0,g-2)
FEATURE [Part::Extrusion] Extrude021
  Base = -> Sketch078
  Dir = (0,0,1)
  DirMode = 2
  FaceMakerClass = Part::FaceMakerBullseye
  LengthFwd = 10
  LengthRev = 0
  Placement = pos=(0,-7.3,20.65) rot=(0,1,0;1.5708rad)
  Solid = true
  Symmetric = false
FEATURE [Part::Compound] Compound026
  Links = -> [Populate037,Extrude021]
FEATURE [Sketcher::SketchObject] Sketch079
  ExternalGeometry = -> [Binder020]
  FullyConstrained = true
  sketch-geometry (2):
    g0: LineSegment StartX=319.563 StartY=220 StartZ=0 EndX=299.78 EndY=220 EndZ=0
    g1: LineSegment StartX=299.78 StartY=220 StartZ=0 EndX=299.78 EndY=203.4 EndZ=0
  constraints (7):
    c: Coincident(g-3,g0)
    c: Horizontal(g0)
    c: Coincident(g0,g1)
    c: PointOnObject(g1,g-3)
    c: Vertical(g1)
    c: DistanceY(g1,g1) = 16.6
    c: DistanceX(g1) = 299.78  'distance_x'
FEATURE [Part::FeaturePython] Placment023  label="face_magnet_fix_placement"  # WARN: FeaturePython — macro-defined, semantics opaque (R4)
  AttacherType = Attacher::AttachEngine3D
  AttachmentOffset = pos=(0,14.6,16) rot=(0,0,1;0rad)
  AttachmentSupport = -> [Sketch079]
  ExposePlacement = true
  MapMode = 1
  MarkerShape = 1
  MarkerSize = 20
  NumElements = 1
  Placement = pos=(299.78,218,16) rot=(0,0,1;0rad)
  Type = lattice2AttachablePlacement.AttachablePlacement
  isLattice = 1
  expr: .AttachmentOffset.Base.y = 14.6 mm
FEATURE [Part::FeaturePython] Populate038  label="Populate Placment023 with Populate Populate Placment022 with LinearArray013 with Body020"  # WARN: FeaturePython — macro-defined, semantics opaque (R4)
  Copying = 0
  ExposePlacement = false
  MarkerShape = 1
  MarkerSize = 0
  NumElements = 0
  Object = -> Populate037
  OutputCompounding = 2
  PlacementsTo = -> Placment023
  Referencing = 0
  Type = lattice2PopulateCopies.LatticePopulateCopies
  isLattice = 0
FEATURE [Part::FeaturePython] Mirror006  label="Mirror006 of Populate Placment023 with Populate Populate Placment022 with LinearArray013 with Body020"  # WARN: FeaturePython — macro-defined, semantics opaque (R4)
  ExposePlacement = false
  FlipX = true
  FlipY = false
  FlipZ = false
  MarkerShape = 1
  MarkerSize = 0
  NumElements = 0
  Object = -> Populate038
  ObjectTraversal = 0
  Type = lattice2Mirror.LatticeMirror
  isLattice = 0
FEATURE [Sketcher::SketchObject] Sketch080
  FullyConstrained = true
  expr: Constraints[3] = <<Dimensions_sketch>>.Constraints.total_width / 2
  sketch-geometry (1):
    g0: LineSegment StartX=0 StartY=0 StartZ=0 EndX=319.563 EndY=0 EndZ=0
  constraints (4):
    c: PointOnObject(g0,g-2)
    c: Horizontal(g0)
    c: PointOnObject(g0,g-1)
    c: DistanceX(g0,g0) = 319.563
FEATURE [Part::Mirroring] Part__Mirroring017  label="Sketch080 (Mirror #16)"
  Base = (0,0,0)
  Normal = (1,0,0)
  Source = -> Sketch080
FEATURE [Part::FeaturePython] Connect010  # WARN: FeaturePython — macro-defined, semantics opaque (R4)
  Objects = -> [Sketch080,Part__Mirroring017]
  Tolerance = 0
FEATURE [PartDesign::SubShapeBinder] Binder024
  BindCopyOnChange = 0
  BindMode = 0
  ClaimChildren = true
  Context = -> Body021 [Binder024.]
  Fuse = false
  MakeFace = true
  OffsetFill = false
  OffsetIntersection = false
  OffsetJoinType = 0
  OffsetOpenResult = false
  PartialLoad = false
  Relative = false
  Support = -> [Connect010]
  _Version = 2
FEATURE [PartDesign::FeaturePython] BaseBend016  # WARN: FeaturePython — macro-defined, semantics opaque (R4)
  BendSide = 0
  BendSketch = -> Binder024
  MidPlane = false
  Reverse = false
  Suppressed = false
  length = 146
  radius = 1
  thickness = 1
FEATURE [PartDesign::FeaturePython] Extend003  # WARN: FeaturePython — macro-defined, semantics opaque (R4)
  BaseFeature = -> BaseBend016
  Offset = 0.02
  Refine = true
  Suppressed = false
  UseSubtraction = false
  baseObject = -> BaseBend016 [Face1]
  gap1 = 0
  gap2 = 0
  length = 0
FEATURE [Part::FeaturePython] LinearArray015  # WARN: FeaturePython — macro-defined, semantics opaque (R4)
  Alignment = 0
  CellStart = A1
  Count = 2
  Dir = (1,0,0)
  DirIsDriven = true
  DistributionLaw = 0
  DrivenProperty = 1
  EndInclusive = true
  ExposePlacement = false
  GeneratorMode = 0
  MarkerShape = 1
  MarkerSize = 0
  NumElements = 2
  OrientMode = 1
  Placement = pos=(-250,-3,50) rot=(-1,0,0;1.5708rad)
  Point = (0,0,0)
  PointIsDriven = true
  Reverse = false
  SpanEnd = 500
  SpanStart = 0
  Step = 500
  Type = lattice2LinearArray.LinearArray
  VSGVersion = 1
  Values = 0.0 | 500.0
  ValuesSource = 2
  isLattice = 1
  expr: .Placement.Base.x = -SpanEnd / 2
FEATURE [Part::Cylinder] Cylinder  label="hole_4mm"
  Angle = 360
  AttacherType = Attacher::AttachEngine3D
  FirstAngle = 0
  Height = 10
  Radius = 2
  SecondAngle = 0
FEATURE [Part::FeaturePython] Populate040  label="Populate LinearArray015 with hole_3.4mm"  # WARN: FeaturePython — macro-defined, semantics opaque (R4)
  Copying = 0
  ExposePlacement = false
  MarkerShape = 1
  MarkerSize = 0
  NumElements = 0
  Object = -> Cylinder
  OutputCompounding = 1
  PlacementsTo = -> LinearArray015
  Referencing = 0
  Type = lattice2PopulateCopies.LatticePopulateCopies
  isLattice = 0
FEATURE [PartDesign::CoordinateSystem] Local_CS005  label="face_sink_LCS"
  AttacherType = Attacher::AttachEngine3D
  AttachmentOffset = pos=(0,90,140) rot=(0,0,1;0rad)
  AttachmentSupport = -> [XY_Plane]
  MapMode = 5
  Placement = pos=(0,90,140) rot=(0,0,1;0rad)
  expr: AttachmentOffset = <<sink_placement>>.Placement
FEATURE [PartDesign::CoordinateSystem] Local_CS006  label="face_lamp_holder_LCS"
  AttacherType = Attacher::AttachEngine3D
  AttachmentOffset = pos=(0,90,254) rot=(0,0,1;0rad)
  AttachmentSupport = -> [XY_Plane]
  MapMode = 5
  Placement = pos=(0,90,254) rot=(0,0,1;0rad)
  expr: AttachmentOffset = <<lamp_holder_placement>>.Placement
FEATURE [PartDesign::CoordinateSystem] Local_CS007  label="face_back_LCS"
  AttacherType = Attacher::AttachEngine3D
  AttachmentSupport = -> [XY_Plane]
  MapMode = 5
FEATURE [Part::FeaturePython] Placment024  label="top_placement"  # WARN: FeaturePython — macro-defined, semantics opaque (R4)
  AttacherType = Attacher::AttachEngine3D
  ExposePlacement = true
  MarkerShape = 1
  MarkerSize = 50
  NumElements = 1
  Placement = pos=(0,90,813.1) rot=(0,0,1;0rad)
  Type = lattice2AttachablePlacement.AttachablePlacement
  isLattice = 1
  expr: .Placement.Base.y = <<Dimensions_sketch>>.Constraints.offset
  expr: .Placement.Base.z = <<BaseBend>>.length + <<BaseBend>>.radius
FEATURE [Part::FeaturePython] Placment025  label="cap_placement"  # WARN: FeaturePython — macro-defined, semantics opaque (R4)
  AttacherType = Attacher::AttachEngine3D
  ExposePlacement = true
  MarkerShape = 1
  MarkerSize = 20
  NumElements = 1
  Placement = pos=(0,0,813) rot=(0,0,1;0rad)
  Type = lattice2AttachablePlacement.AttachablePlacement
  isLattice = 1
  expr: .Placement.Base.z = <<BaseBend>>.length
FEATURE [PartDesign::CoordinateSystem] Local_CS008  label="face_top_LCS"
  AttacherType = Attacher::AttachEngine3D
  AttachmentOffset = pos=(0,90,813.1) rot=(0,0,1;0rad)
  AttachmentSupport = -> [XY_Plane]
  MapMode = 5
  Placement = pos=(0,90,813.1) rot=(0,0,1;0rad)
  expr: AttachmentOffset = <<top_placement>>.Placement
FEATURE [PartDesign::CoordinateSystem] Local_CS009  label="face_cap_LCS"
  AttacherType = Attacher::AttachEngine3D
  AttachmentOffset = pos=(0,0,813) rot=(0,0,1;0rad)
  AttachmentSupport = -> [XY_Plane]
  MapMode = 5
  Placement = pos=(0,0,813) rot=(0,0,1;0rad)
  expr: AttachmentOffset = <<cap_placement>>.Placement
FEATURE [PartDesign::CoordinateSystem] Local_CS010  label="back_LCS"
  AttacherType = Attacher::AttachEngine3D
  AttachmentSupport = -> [XY_Plane001]
  MapMode = 5
FEATURE [PartDesign::CoordinateSystem] Local_CS011  label="back_electric_shield_LCS"
  AttacherType = Attacher::AttachEngine3D
  AttachmentOffset = pos=(319.563,80,555.5) rot=(0.57735,0.57735,0.57735;2.0944rad)
  AttachmentSupport = -> [XY_Plane001]
  MapMode = 5
  Placement = pos=(319.563,80,555.5) rot=(0.57735,0.57735,0.57735;2.0944rad)
  expr: AttachmentOffset = <<electric_shield_placement>>.Placement
FEATURE [PartDesign::CoordinateSystem] Local_CS012  label="lamp_holder_LCS"
  AttacherType = Attacher::AttachEngine3D
  AttachmentSupport = -> [XY_Plane003]
  MapMode = 5
FEATURE [PartDesign::CoordinateSystem] Local_CS013  label="dropper_fix_composit_LCS"
  AttacherType = Attacher::AttachEngine3D
  AttachmentSupport = -> [XY_Plane006]
  MapMode = 5
FEATURE [PartDesign::CoordinateSystem] Local_CS014  label="dr_fix_c_dr_fix_PP_LCS"
  AttacherType = Attacher::AttachEngine3D
  AttachmentOffset = pos=(0,0,3) rot=(0,0,1;0rad)
  AttachmentSupport = -> [XY_Plane006]
  MapMode = 5
  Placement = pos=(0,0,3) rot=(0,0,1;0rad)
FEATURE [PartDesign::CoordinateSystem] Local_CS015  label="cap_outer_LCS"
  AttacherType = Attacher::AttachEngine3D
  MapMode = 5
FEATURE [PartDesign::Body] Body010  label="cap_outer"
  Group = -> [Binder012,BaseBend007,Extend002,Bend005,Boolean008,Boolean009,Local_CS015]
  Origin = -> Origin010
  Tip = -> Boolean009
FEATURE [PartDesign::CoordinateSystem] Local_CS016  label="dropper_fix_PP_LCS"
  AttacherType = Attacher::AttachEngine3D
  AttachmentSupport = -> [XY_Plane004]
  MapMode = 5
FEATURE [PartDesign::CoordinateSystem] Local_CS018  label="bottom_composit_LCS"
  AttacherType = Attacher::AttachEngine3D
  AttachmentSupport = -> [XY_Plane014]
  MapMode = 5
FEATURE [PartDesign::CoordinateSystem] Local_CS020  label="face_LCS"
  AttacherType = Attacher::AttachEngine3D
  AttachmentSupport = -> [XY_Plane]
  MapMode = 5
FEATURE [Sketcher::SketchObject] Sketch081
  FullyConstrained = true
  sketch-geometry (10):
    g0: LineSegment StartX=-255 StartY=-82 StartZ=0 EndX=255 EndY=-82 EndZ=0
    g1: LineSegment StartX=265 StartY=-72 StartZ=0 EndX=265 EndY=72 EndZ=0
    g2: LineSegment StartX=255 StartY=82 StartZ=0 EndX=-255 EndY=82 EndZ=0
    g3: LineSegment StartX=-265 StartY=72 StartZ=0 EndX=-265 EndY=-72 EndZ=0
    g4: ArcOfCircle CenterX=-255 CenterY=-72 CenterZ=0 NormalX=0 NormalY=0 NormalZ=1 AngleXU=0 Radius=10 StartAngle=3.14159 EndAngle=4.71239
    g5: ArcOfCircle CenterX=255 CenterY=-72 CenterZ=0 NormalX=0 NormalY=0 NormalZ=1 AngleXU=0 Radius=10 StartAngle=4.71239 EndAngle=6.28319
    g6: ArcOfCircle CenterX=255 CenterY=72 CenterZ=0 NormalX=0 NormalY=0 NormalZ=1 AngleXU=0 Radius=10 StartAngle=5e-16 EndAngle=1.5708
    g7: ArcOfCircle CenterX=-255 CenterY=72 CenterZ=0 NormalX=0 NormalY=0 NormalZ=1 AngleXU=0 Radius=10 StartAngle=1.5708 EndAngle=3.14159
    g8: GeomPoint X=-265 Y=-82 Z=0
    g9: GeomPoint X=265 Y=82 Z=0
  constraints (23):
    c: Tangent(g0,g4) = -1.5708
    c: Tangent(g0,g5) = -1.5708
    c: Tangent(g1,g5) = -1.5708
    c: Tangent(g1,g6) = -1.5708
    c: Tangent(g2,g6) = -1.5708
    c: Tangent(g2,g7) = -1.5708
    c: Tangent(g3,g7) = -1.5708
    c: Tangent(g3,g4) = -1.5708
    c: Horizontal(g0)
    c: Horizontal(g2)
    c: Vertical(g1)
    c: Vertical(g3)
    c: Equal(g4,g5)
    c: Equal(g5,g6)
    c: Equal(g6,g7)
    c: PointOnObject(g8,g0)
    c: PointOnObject(g8,g3)
    c: PointOnObject(g9,g1)
    c: PointOnObject(g9,g2)
    c: Symmetric(g8,g9,g-1)
    c: Radius(g6) = 10
    c: DistanceX(g8,g9) = 530
    c: DistanceY(g8,g9) = 164
FEATURE [Sketcher::SketchObject] Sketch082
  FullyConstrained = true
  sketch-geometry (10):
    g0: LineSegment StartX=-220.5 StartY=-67.5 StartZ=0 EndX=220.5 EndY=-67.5 EndZ=0
    g1: LineSegment StartX=250.5 StartY=-37.5 StartZ=0 EndX=250.5 EndY=37.5 EndZ=0
    g2: LineSegment StartX=220.5 StartY=67.5 StartZ=0 EndX=-220.5 EndY=67.5 EndZ=0
    g3: LineSegment StartX=-250.5 StartY=37.5 StartZ=0 EndX=-250.5 EndY=-37.5 EndZ=0
    g4: ArcOfCircle CenterX=-220.5 CenterY=-37.5 CenterZ=0 NormalX=0 NormalY=0 NormalZ=1 AngleXU=0 Radius=30 StartAngle=3.14159 EndAngle=4.71239
    g5: ArcOfCircle CenterX=220.5 CenterY=-37.5 CenterZ=0 NormalX=0 NormalY=0 NormalZ=1 AngleXU=0 Radius=30 StartAngle=4.71239 EndAngle=6.28319
    g6: ArcOfCircle CenterX=220.5 CenterY=37.5 CenterZ=0 NormalX=0 NormalY=0 NormalZ=1 AngleXU=0 Radius=30 StartAngle=0 EndAngle=1.5708
    g7: ArcOfCircle CenterX=-220.5 CenterY=37.5 CenterZ=0 NormalX=0 NormalY=0 NormalZ=1 AngleXU=0 Radius=30 StartAngle=1.5708 EndAngle=3.14159
    g8: GeomPoint X=-250.5 Y=-67.5 Z=0
    g9: GeomPoint X=250.5 Y=67.5 Z=0
  constraints (23):
    c: Tangent(g0,g4) = -1.5708
    c: Tangent(g0,g5) = -1.5708
    c: Tangent(g1,g5) = -1.5708
    c: Tangent(g1,g6) = -1.5708
    c: Tangent(g2,g6) = -1.5708
    c: Tangent(g2,g7) = -1.5708
    c: Tangent(g3,g7) = -1.5708
    c: Tangent(g3,g4) = -1.5708
    c: Horizontal(g0)
    c: Horizontal(g2)
    c: Vertical(g1)
    c: Vertical(g3)
    c: Equal(g4,g5)
    c: Equal(g5,g6)
    c: Equal(g6,g7)
    c: PointOnObject(g8,g0)
    c: PointOnObject(g8,g3)
    c: PointOnObject(g9,g1)
    c: PointOnObject(g9,g2)
    c: Symmetric(g8,g9,g-1)
    c: DistanceX(g8,g9) = 501
    c: DistanceY(g8,g9) = 135
    c: Radius(g6) = 30
FEATURE [PartDesign::CoordinateSystem] Local_CS022  label="bottom_composit_basin_LCS"
  AttacherType = Attacher::AttachEngine3D
  AttachmentOffset = pos=(0,116.3,11) rot=(0,0,1;0rad)
  AttachmentSupport = -> [XY_Plane014]
  MapMode = 5
  Placement = pos=(0,116.3,11) rot=(0,0,1;0rad)
  expr: .AttachmentOffset.Base.z = 11 mm
FEATURE [Sketcher::SketchObject] Sketch083
  ExternalGeometry = -> [Sketch082]
  FullyConstrained = true
  sketch-geometry (12):
    g0: LineSegment StartX=-220.5 StartY=-60 StartZ=0 EndX=220.5 EndY=-60 EndZ=0
    g1: LineSegment StartX=243 StartY=-37.5 StartZ=0 EndX=243 EndY=37.5 EndZ=0
    g2: LineSegment StartX=220.5 StartY=60 StartZ=0 EndX=-220.5 EndY=60 EndZ=0
    g3: LineSegment StartX=-243 StartY=37.5 StartZ=0 EndX=-243 EndY=-37.5 EndZ=0
    g4: ArcOfCircle CenterX=-220.5 CenterY=-37.5 CenterZ=0 NormalX=0 NormalY=0 NormalZ=1 AngleXU=0 Radius=22.5 StartAngle=3.14159 EndAngle=4.71239
    g5: ArcOfCircle CenterX=220.5 CenterY=-37.5 CenterZ=0 NormalX=0 NormalY=0 NormalZ=1 AngleXU=0 Radius=22.5 StartAngle=4.71239 EndAngle=6.28319
    g6: ArcOfCircle CenterX=220.5 CenterY=37.5 CenterZ=0 NormalX=0 NormalY=0 NormalZ=1 AngleXU=0 Radius=22.5 StartAngle=0 EndAngle=1.5708
    g7: ArcOfCircle CenterX=-220.5 CenterY=37.5 CenterZ=0 NormalX=0 NormalY=0 NormalZ=1 AngleXU=0 Radius=22.5 StartAngle=1.5708 EndAngle=3.14159
    g8: GeomPoint X=-243 Y=-60 Z=0
    g9: GeomPoint X=243 Y=60 Z=0
    g10: LineSegment StartX=220.5 StartY=60 StartZ=0 EndX=220.5 EndY=67.5 EndZ=0
    g11: LineSegment StartX=243 StartY=37.5 StartZ=0 EndX=250.5 EndY=37.5 EndZ=0
  constraints (27):
    c: Tangent(g0,g4) = -1.5708
    c: Tangent(g0,g5) = -1.5708
    c: Tangent(g1,g5) = -1.5708
    c: Tangent(g1,g6) = -1.5708
    c: Tangent(g2,g6) = -1.5708
    c: Tangent(g2,g7) = -1.5708
    c: Tangent(g3,g7) = -1.5708
    c: Tangent(g3,g4) = -1.5708
    c: Horizontal(g0)
    c: Horizontal(g2)
    c: Vertical(g1)
    c: Vertical(g3)
    c: Equal(g4,g5)
    c: Equal(g5,g6)
    c: Equal(g6,g7)
    c: PointOnObject(g8,g0)
    c: PointOnObject(g8,g3)
    c: PointOnObject(g9,g1)
    c: PointOnObject(g9,g2)
    c: Symmetric(g8,g9,g-1)
    c: DistanceY(g8,g9) = 120
    c: Coincident(g10,g2)
    c: Vertical(g10)
    c: Coincident(g11,g1)
    c: Horizontal(g11)
    c: Coincident(g10,g-3)
    c: Coincident(g11,g-3)
FEATURE [PartDesign::CoordinateSystem] Local_CS023  label="bottom_composit_rails_LCS"
  AttacherType = Attacher::AttachEngine3D
  AttachmentOffset = pos=(200,9,6) rot=(0,0,1;1.5708rad)
  AttachmentSupport = -> [XY_Plane014]
  MapMode = 5
  Placement = pos=(200,9,6) rot=(0,0,1;1.5708rad)
  expr: AttachmentOffset = <<LinearArray010>>.Placement
FEATURE [PartDesign::CoordinateSystem] Local_CS024  label="rails_LCS"
  AttacherType = Attacher::AttachEngine3D
  MapMode = 5
FEATURE [PartDesign::Body] Body016  label="rail"
  Group = -> [Binder019,Pad018,Boolean015,Local_CS024]
  Origin = -> Origin016
  Tip = -> Boolean015
FEATURE [PartDesign::CoordinateSystem] Local_CS025  label="cap_inner_LCS"
  AttacherType = Attacher::AttachEngine3D
  AttachmentSupport = -> [XY_Plane011]
  MapMode = 5
FEATURE [PartDesign::Body] Body011  label="cap_inner"
  Group = -> [Binder013,BaseBend008,Bend006,Binder014,Sketch029,Pad001,Sketch030,Pocket002,Local_CS025,Boolean010]
  Origin = -> Origin011
  Tip = -> Boolean010
FEATURE [PartDesign::Fillet] Fillet
  Base = -> Pad019 [Edge1,Edge2,Edge3,Edge4,Edge5,Edge6,Edge7,Edge8,Edge9]
  BaseFeature = -> Pad019
  Radius = 2
  SupportTransform = false
  Suppressed = false
  UseAllEdges = true
FEATURE [PartDesign::Boolean] Boolean018
  BaseFeature = -> Fillet
  Group = -> [Compound026]
  Suppressed = false
  Type = 1
  UsePlacement = true
FEATURE [PartDesign::CoordinateSystem] Local_CS026  label="magnet_fix_LCS"
  AttacherType = Attacher::AttachEngine3D
  AttachmentSupport = -> [XY_Plane019]
  MapMode = 5
FEATURE [PartDesign::CoordinateSystem] Local_CS027
  AttacherType = Attacher::AttachEngine3D
  AttachmentOffset = pos=(299.78,218,16) rot=(0,0,1;0rad)
  AttachmentSupport = -> [XY_Plane]
  MapMode = 5
  Placement = pos=(299.78,218,16) rot=(0,0,1;0rad)
  expr: AttachmentOffset = <<face_magnet_fix_placement>>.Placement
FEATURE [PartDesign::CoordinateSystem] Local_CS028
  AttacherType = Attacher::AttachEngine3D
  AttachmentOffset = pos=(-7.3,20,0) rot=(0.707107,0.707107,0;3.14159rad)
  AttachmentSupport = -> [YZ_Plane019]
  MapMode = 5
  Placement = pos=(0,-7.3,20) rot=(0,1,0;4.71239rad)
FEATURE [PartDesign::Body] Body019  label="magnet_fix"
  Group = -> [Binder022,Pad019,Fillet,Boolean018,Local_CS026,Local_CS028]
  Origin = -> Origin019
  Tip = -> Boolean018
FEATURE [App::Link] Link  label="module_Body"
  LinkedObject = -> <external ../module.FCStd>#Body
  expr: LinkedObject = module#<<module_Body>>._self
FEATURE [Part::FeaturePython] Populate041  label="Populate Populate Join with LinearArray with module_Body"  # WARN: FeaturePython — macro-defined, semantics opaque (R4)
  Copying = 0
  ExposePlacement = false
  MarkerShape = 1
  MarkerSize = 0
  NumElements = 0
  Object = -> Link
  OutputCompounding = 1
  PlacementsTo = -> Populate
  Referencing = 0
  Type = lattice2PopulateCopies.LatticePopulateCopies
  isLattice = 0
FEATURE [PartDesign::CoordinateSystem] LCS_1  label="modules_LCS"
  AttacherType = Attacher::AttachEngine3D
  MapMode = 5
FEATURE [App::Part] Part  label="modules"
  Group = -> [Populate041,LCS_1]
  Origin = -> Origin023
FEATURE [PartDesign::CoordinateSystem] Local_CS029
  AttacherType = Attacher::AttachEngine3D
  AttachmentSupport = -> [XY_Plane021]
  MapMode = 5
FEATURE [PartDesign::CoordinateSystem] Local_CS030  label="bottom_composit_shield_LCS"
  AttacherType = Attacher::AttachEngine3D
  AttachmentOffset = pos=(0,223,6) rot=(0,0,1;0rad)
  AttachmentSupport = -> [XY_Plane014]
  MapMode = 5
  Placement = pos=(0,223,6) rot=(0,0,1;0rad)
  expr: .AttachmentOffset.Base.y = <<Dimensions_sketch>>.Constraints.total_depth + 3 mm
FEATURE [PartDesign::Body] Body014  label="bottom_composit"
  Group = -> [Binder018,BaseBend010,Sketch067,Pocket012,Sketch068,Pocket013,Mirrored003,Boolean013,Boolean014,Sketch074,Pocket014,Mirrored004,Local_CS018,Local_CS022,Local_CS023,Local_CS030]
  Origin = -> Origin014
  Tip = -> Mirrored004
FEATURE [Sketcher::SketchObject] Sketch084
  FullyConstrained = true
  MapMode = 5
  Placement = pos=(0,0,0) rot=(1,0,0;1.5708rad)
  sketch-geometry (5):
    g0: LineSegment StartX=-320 StartY=1 StartZ=0 EndX=-320 EndY=0 EndZ=0
    g1: LineSegment StartX=-320 StartY=0 StartZ=0 EndX=320 EndY=0 EndZ=0
    g2: LineSegment StartX=320 StartY=0 StartZ=0 EndX=320 EndY=1 EndZ=0
    g3: LineSegment StartX=320 StartY=1 StartZ=0 EndX=-320 EndY=1 EndZ=0
    g4: GeomPoint X=0 Y=0.5 Z=0
  constraints (13):
    c: Coincident(g0,g1)
    c: Coincident(g1,g2)
    c: Coincident(g2,g3)
    c: Coincident(g3,g0)
    c: Vertical(g0)
    c: Vertical(g2)
    c: Horizontal(g1)
    c: Horizontal(g3)
    c: Symmetric(g2,g0,g4)
    c: PointOnObject(g4,g-2)
    c: PointOnObject(g1,g-1)
    c: DistanceX(g1,g1) = 640
    c: DistanceY(g2,g2) = 1
FEATURE [Sketcher::SketchObject] Sketch085
  AttachmentSupport = -> [XZ_Plane021]
  FullyConstrained = true
  MapMode = 5
  Placement = pos=(0,0,0) rot=(1,0,0;1.5708rad)
  sketch-geometry (5):
    g0: LineSegment StartX=-202 StartY=0 StartZ=0 EndX=202 EndY=0 EndZ=0
    g1: LineSegment StartX=202 StartY=0 StartZ=0 EndX=202 EndY=1.5 EndZ=0
    g2: LineSegment StartX=202 StartY=1.5 StartZ=0 EndX=-202 EndY=1.5 EndZ=0
    g3: LineSegment StartX=-202 StartY=1.5 StartZ=0 EndX=-202 EndY=0 EndZ=0
    g4: GeomPoint X=0 Y=0.75 Z=0
  constraints (13):
    c: Coincident(g0,g1)
    c: Coincident(g1,g2)
    c: Coincident(g2,g3)
    c: Coincident(g3,g0)
    c: Horizontal(g0)
    c: Horizontal(g2)
    c: Vertical(g1)
    c: Vertical(g3)
    c: Symmetric(g2,g0,g4)
    c: PointOnObject(g4,g-2)
    c: PointOnObject(g0,g-1)
    c: DistanceY(g1,g1) = 1.5
    c: DistanceX(g0,g0) = 404
FEATURE [PartDesign::Pocket] Pocket015
  BaseFeature = -> Extend003
  Direction = (0,1,-2e-16)
  Length = 5
  Length2 = 5
  Midplane = true
  Profile = -> Sketch084
  ReferenceAxis = -> Sketch084 [N_Axis]
  Suppressed = false
  Type = 1
FEATURE [PartDesign::Pocket] Pocket016
  BaseFeature = -> Pocket015
  Direction = (0,1,-2e-16)
  Length = 5
  Length2 = 5
  Midplane = true
  Profile = -> Sketch085
  ReferenceAxis = -> Sketch085 [N_Axis]
  Suppressed = false
  Type = 1
FEATURE [Sketcher::SketchObject] Sketch086
  FullyConstrained = true
  sketch-geometry (6):
    g0: LineSegment StartX=-2.5 StartY=-35 StartZ=0 EndX=2.5 EndY=-35 EndZ=0
    g1: LineSegment StartX=2.5 StartY=-35 StartZ=0 EndX=2.5 EndY=35 EndZ=0
    g2: LineSegment StartX=2.5 StartY=35 StartZ=0 EndX=-2.5 EndY=35 EndZ=0
    g3: LineSegment StartX=-2.5 StartY=35 StartZ=0 EndX=-2.5 EndY=-35 EndZ=0
    g4: GeomPoint X=0 Y=0 Z=0
    g5: GeomPoint X=0 Y=4.1e-15 Z=0
  constraints (14):
    c: Coincident(g0,g1)
    c: Coincident(g1,g2)
    c: Coincident(g2,g3)
    c: Coincident(g3,g0)
    c: Horizontal(g0)
    c: Horizontal(g2)
    c: Vertical(g1)
    c: Vertical(g3)
    c: Coincident(g4,g-1)
    c: DistanceX(g2,g2) = 5
    c: DistanceY(g1,g1) = 70
    c: Symmetric(g0,g1,g5)
    c: PointOnObject(g5,g-2)
    c: DistanceY(g0,g4) = 35
FEATURE [Part::Extrusion] Extrude022
  Base = -> Sketch086
  Dir = (0,0,1)
  DirMode = 2
  FaceMakerClass = Part::FaceMakerBullseye
  LengthFwd = 2.5
  LengthRev = 0
  Solid = true
  Symmetric = false
FEATURE [Part::MultiFuse] Fusion001
  Refine = true
  Shapes = -> [Extrude003,Extrude002,Extrude004,Extrude022]
FEATURE [Part::FeaturePython] Populate004  label="Populate Populate Join with LinearArray002 with Fusion001"  # WARN: FeaturePython — macro-defined, semantics opaque (R4)
  Copying = 0
  ExposePlacement = false
  MarkerShape = 1
  MarkerSize = 0
  NumElements = 0
  Object = -> Fusion001
  OutputCompounding = 1
  PlacementsTo = -> Populate002
  Referencing = 0
  Type = lattice2PopulateCopies.LatticePopulateCopies
  isLattice = 0
FEATURE [Part::Compound] Compound002
  Links = -> [Populate004,Extrude019]
FEATURE [PartDesign::Boolean] Boolean001
  BaseFeature = -> Pad
  Group = -> [Compound002]
  Suppressed = false
  Type = 1
  UsePlacement = true
FEATURE [PartDesign::Body] Body004  label="dropper_fix_PP"
  Group = -> [Binder007,Pad,Boolean001,Local_CS016]
  Origin = -> Origin004
  Tip = -> Boolean001
FEATURE [PartDesign::FeaturePython] Extend004  # WARN: FeaturePython — macro-defined, semantics opaque (R4)
  BaseFeature = -> BaseBend001
  Offset = 0.02
  Refine = true
  Suppressed = false
  UseSubtraction = false
  baseObject = -> BaseBend001 [Face1]
  gap1 = 0
  gap2 = 0
  length = 0
FEATURE [PartDesign::FeaturePython] Bend009  # WARN: FeaturePython — macro-defined, semantics opaque (R4)
  AutoMiter = false
  BaseFeature = -> Extend004
  BendType = 0
  LengthList = [20]
  LengthSpec = 0
  ReliefFactor = 0.7
  Suppressed = false
  UseReliefFactor = false
  angle = 90
  baseObject = -> Extend004 [Edge44]
  bendAList = [90]
  extend1 = 0
  extend2 = 0
  gap1 = 3
  gap2 = 3
  invert = true
  kfactor = 0.5
  length = 20
  maxExtendDist = 5
  minGap = 0.2
  minReliefGap = 1
  miterangle1 = 45
  miterangle2 = 45
  offset = 0
  radius = 0.1
  reliefType = 0
  reliefd = 1
  reliefw = 0.8
  sketchflip = false
  sketchinvert = false
  unfold = false
  expr: radius = BaseBend.radius
FEATURE [PartDesign::Pocket] Pocket003
  BaseFeature = -> Bend009
  Direction = (-1,0,0)
  Length = 5
  Length2 = 5
  Midplane = true
  Profile = -> Sketch031
  ReferenceAxis = -> Sketch031 [N_Axis]
  Suppressed = false
  Type = 1
FEATURE [Sketcher::SketchObject] Sketch087
  ExternalGeometry = -> [Sketch008]
  FullyConstrained = true
  Placement = pos=(0,0,0.4) rot=(0,0,1;0rad)
  sketch-geometry (3):
    g0: LineSegment StartX=308.963 StartY=130.4 StartZ=0 EndX=313.963 EndY=130.4 EndZ=0
    g1: LineSegment StartX=313.963 StartY=130.4 StartZ=0 EndX=313.963 EndY=104.676 EndZ=0
    g2: LineSegment StartX=313.963 StartY=104.676 StartZ=0 EndX=302.472 EndY=95.0338 EndZ=0
  constraints (10):
    c: Horizontal(g0)
    c: Coincident(g0,g1)
    c: Vertical(g1)
    c: Coincident(g1,g2)
    c: DistanceX(g-3,g0) = 0.4
    c: DistanceX(g0,g0) = 5
    c: Distance(g1,g-4) = 3.4
    c: Parallel(g-4,g2)
    c: Distance(g2) = 15  'overlap'
    c: DistanceY(g-3,g0) = 0.4
FEATURE [Sketcher::SketchObject] Sketch088
  ExternalGeometry = -> [Sketch008]
  FullyConstrained = true
  Placement = pos=(0,0,0.4) rot=(0,0,1;0rad)
  sketch-geometry (2):
    g0: LineSegment StartX=73.1036 StartY=-85 StartZ=0 EndX=87.9164 EndY=-85 EndZ=0
    g1: LineSegment StartX=87.9164 StartY=-85 StartZ=0 EndX=118.558 EndY=-59.2885 EndZ=0
  constraints (7):
    c: Horizontal(g0)
    c: Coincident(g1,g0)
    c: DistanceY(g0,g-3) = 0.4
    c: Distance(g0,g-3) = 3.4
    c: Parallel(g1,g-3)
    c: Distance(g1) = 40
    c: DistanceX(g0,g-3) = 10
FEATURE [Part::FeaturePython] BaseBend017  # WARN: FeaturePython — macro-defined, semantics opaque (R4)
  BendSide = 0
  BendSketch = -> Sketch087
  MidPlane = false
  Reverse = false
  length = 20
  radius = 0.1
  thickness = 0.3
  expr: length = <<Bend001>>.length
FEATURE [Part::FeaturePython] BaseBend018  # WARN: FeaturePython — macro-defined, semantics opaque (R4)
  BendSide = 1
  BendSketch = -> Sketch088
  MidPlane = false
  Reverse = false
  length = 20
  radius = 0.1
  thickness = 0.3
  expr: length = <<BaseBend017>>.length
FEATURE [Part::Mirroring] Part__Mirroring018  label="Sketch087 (Mirror #17)"
  Base = (0,0,0)
  Normal = (1,0,0)
  Source = -> Sketch087
FEATURE [PartDesign::SubShapeBinder] Binder028
  BindCopyOnChange = 0
  BindMode = 0
  ClaimChildren = true
  Fuse = false
  MakeFace = true
  OffsetFill = false
  OffsetIntersection = false
  OffsetJoinType = 0
  OffsetOpenResult = false
  PartialLoad = false
  Relative = true
  Support = -> [Part__Mirroring018]
  _Version = 2
FEATURE [Part::FeaturePython] BaseBend019  # WARN: FeaturePython — macro-defined, semantics opaque (R4)
  BendSide = 1
  BendSketch = -> Binder028
  MidPlane = false
  Reverse = false
  length = 20
  radius = 0.1
  thickness = 0.3
  expr: length = <<BaseBend017>>.length
FEATURE [Part::Mirroring] Part__Mirroring019  label="Sketch088 (Mirror #18)"
  Base = (0,0,0)
  Normal = (1,0,0)
  Source = -> Sketch088
FEATURE [PartDesign::SubShapeBinder] Binder029
  BindCopyOnChange = 0
  BindMode = 0
  ClaimChildren = true
  Fuse = false
  MakeFace = true
  OffsetFill = false
  OffsetIntersection = false
  OffsetJoinType = 0
  OffsetOpenResult = false
  PartialLoad = false
  Relative = true
  Support = -> [Part__Mirroring019]
  _Version = 2
FEATURE [Part::FeaturePython] BaseBend020  # WARN: FeaturePython — macro-defined, semantics opaque (R4)
  BendSide = 0
  BendSketch = -> Binder029
  MidPlane = false
  Reverse = false
  length = 20
  radius = 0.1
  thickness = 0.3
  expr: length = <<BaseBend018>>.length
FEATURE [Part::Compound] Compound028
  Links = -> [BaseBend017,BaseBend018,BaseBend019,BaseBend020]
FEATURE [Sketcher::SketchObject] Sketch089
  AttachmentOffset = pos=(0,0,0) rot=(0,1,0;1.5708rad)
  AttachmentSupport = -> [Binder006]
  ExternalGeometry = -> [Binder006]
  FullyConstrained = true
  MapMode = 7
  Placement = pos=(299.876,113.48,0) rot=(0.889126,0.323616,0.323616;1.68804rad)
  sketch-geometry (8):
    g0: LineSegment StartX=5.46e-14 StartY=0 StartZ=0 EndX=32.7 EndY=0 EndZ=0
    g1: LineSegment StartX=5.46e-14 StartY=33 StartZ=0 EndX=5.46e-14 EndY=0 EndZ=0
    g2: LineSegment StartX=28.7 StartY=31 StartZ=0 EndX=2 EndY=31 EndZ=0
    g3: ArcOfCircle CenterX=2 CenterY=33 CenterZ=0 NormalX=0 NormalY=0 NormalZ=1 AngleXU=0 Radius=2 StartAngle=3.14159 EndAngle=4.71239
    g4: ArcOfCircle CenterX=28.7 CenterY=29 CenterZ=0 NormalX=0 NormalY=0 NormalZ=1 AngleXU=0 Radius=2 StartAngle=-2.176e-13 EndAngle=1.5708
    g5: GeomPoint X=30.7 Y=31 Z=0
    g6: LineSegment StartX=30.7 StartY=2 StartZ=0 EndX=30.7 EndY=29 EndZ=0
    g7: ArcOfCircle CenterX=32.7 CenterY=2 CenterZ=0 NormalX=0 NormalY=0 NormalZ=1 AngleXU=0 Radius=2 StartAngle=3.14159 EndAngle=4.71239
  constraints (19):
    c: Coincident(g1,g0)
    c: Horizontal(g0)
    c: Vertical(g1)
    c: Coincident(g0,g-1)
    c: Horizontal(g2)
    c: Tangent(g3,g2) = 1.5708
    c: Tangent(g3,g1) = -1.5708
    c: PointOnObject(g5,g2)
    c: Tangent(g2,g4) = -1.5708
    c: DistanceY(g5) = 31
    c: Equal(g4,g3)
    c: Vertical(g6)
    c: Tangent(g7,g0) = -1.5708
    c: Tangent(g7,g6) = 1.5708
    c: Radius(g4) = 2
    c: Tangent(g6,g4) = -1.5708
    c: Equal(g7,g4)
    c: DistanceX(g-3,g6) = 5
    c: PointOnObject(g5,g6)
FEATURE [PartDesign::Body] Body003  label="lamp_holder"
  Group = -> [Binder006,BaseBend002,Sketch089,Boolean003,Local_CS012]
  Origin = -> Origin003
  Tip = -> Boolean003
FEATURE [TechDraw::DrawViewPart] View003
  CoarseView = false
  Direction = (-0.707107,0,0.707107)
  Focus = 100
  HardHidden = false
  IsoCount = 0
  IsoHidden = false
  IsoVisible = false
  LockPosition = false
  Perspective = false
  Rotation = 0
  Scale = 0.4
  ScaleType = 2
  ScrubCount = 0
  SeamHidden = false
  SeamVisible = true
  SmoothHidden = false
  SmoothVisible = true
  Source = -> [Body003]
  X = 48.5
  XDirection = (0,-1,0)
  Y = 105
FEATURE [TechDraw::DrawViewBalloon] Balloon
  BubbleShape = 3
  EndType = 0
  EndTypeScale = 1
  KinkLength = 5
  LockPosition = false
  OriginX = 4.88037
  OriginY = 178.747
  Rotation = 0
  ScaleType = 0
  ShapeScale = 1
  SourceView = -> View003
  Text = Оборотная сторона
  TextWrapLen = -1
  X = 137.026
  Y = 219.126
FEATURE [Sketcher::SketchObject] Sketch090
  ExternalGeometry = -> [Binder020,Sketch033]
  FullyConstrained = true
  sketch-geometry (7):
    g0: LineSegment StartX=200 StartY=119.675 StartZ=0 EndX=316.563 EndY=217.483 EndZ=0
    g1: LineSegment StartX=200 StartY=226 StartZ=0 EndX=200 EndY=119.675 EndZ=0
    g2: LineSegment StartX=200 StartY=119.675 StartZ=0 EndX=202.571 EndY=116.611 EndZ=0
    g3: LineSegment StartX=202.571 StartY=116.611 StartZ=0 EndX=205.571 EndY=116.611 EndZ=0
    g4: LineSegment StartX=205.571 StartY=116.611 StartZ=0 EndX=205.571 EndY=9 EndZ=0
    g5: LineSegment StartX=205.571 StartY=9 StartZ=0 EndX=0 EndY=9 EndZ=0
    g6: LineSegment StartX=200 StartY=226 StartZ=0 EndX=0 EndY=226 EndZ=0
  constraints (22):
    c: PointOnObject(g0,g-3)
    c: PointOnObject(g0,g-3)
    c: Vertical(g0,g-4)
    c: Vertical(g-4,g0)
    c: Coincident(g1,g0)
    c: Coincident(g1,g2)
    c: Coincident(g2,g3)
    c: Horizontal(g3)
    c: Coincident(g3,g4)
    c: Vertical(g4)
    c: Coincident(g4,g5)
    c: PointOnObject(g5,g-2)
    c: Horizontal(g5)
    c: Coincident(g1,g6)
    c: PointOnObject(g6,g-2)
    c: Horizontal(g6)
    c: Vertical(g1)
    c: DistanceY(g-3,g1) = 6
    c: Perpendicular(g0,g2)
    c: Distance(g2) = 4
    c: DistanceX(g3,g3) = 3
    c: DistanceY(g5) = 9
FEATURE [Part::Mirroring] Part__Mirroring020  label="Sketch090 (Mirror #19)"
  Base = (0,0,0)
  Normal = (1,0,0)
  Source = -> Sketch090
FEATURE [Part::FeaturePython] Connect011  # WARN: FeaturePython — macro-defined, semantics opaque (R4)
  Objects = -> [Sketch090,Part__Mirroring020]
  Tolerance = 0
FEATURE [PartDesign::SubShapeBinder] Binder030
  BindCopyOnChange = 0
  BindMode = 0
  ClaimChildren = true
  Context = -> Body024 [Binder030.]
  Fuse = false
  MakeFace = true
  OffsetFill = false
  OffsetIntersection = false
  OffsetJoinType = 0
  OffsetOpenResult = false
  PartialLoad = false
  Relative = false
  Support = -> [Connect011]
  _Version = 2
FEATURE [PartDesign::Pad] Pad022
  Direction = (0,0,1)
  Length = 1.5
  Length2 = 10
  Profile = -> Binder030
  Refine = true
  Suppressed = false
  Type = 0
FEATURE [PartDesign::CoordinateSystem] Local_CS031
  AttacherType = Attacher::AttachEngine3D
  AttachmentSupport = -> [XY_Plane025]
  MapMode = 5
FEATURE [PartDesign::Body] Body024
  Group = -> [Binder030,Pad022,Local_CS031]
  Origin = -> Origin025
  Tip = -> Pad022
FEATURE [Sketcher::SketchObject] Sketch091
  FullyConstrained = true
  sketch-geometry (2):
    g0: Circle CenterX=80 CenterY=13 CenterZ=0 NormalX=0 NormalY=0 NormalZ=1 AngleXU=0 Radius=1.7
    g1: Circle CenterX=-80 CenterY=13 CenterZ=0 NormalX=0 NormalY=0 NormalZ=1 AngleXU=0 Radius=1.7
  constraints (5):
    c: Symmetric(g0,g1,g-2)
    c: Equal(g0,g1)
    c: Diameter(g0) = 3.4
    c: DistanceX(g0) = 80
    c: DistanceY(g0) = 13
FEATURE [Part::Extrusion] Extrude023
  Base = -> Sketch091
  Dir = (0,0,1)
  DirMode = 2
  FaceMakerClass = Part::FaceMakerBullseye
  LengthFwd = 10
  LengthRev = 0
  Solid = true
  Symmetric = false
FEATURE [Part::FeaturePython] Placment026  # WARN: FeaturePython — macro-defined, semantics opaque (R4)
  AttacherType = Attacher::AttachEngine3D
  ExposePlacement = true
  MarkerShape = 1
  MarkerSize = 10
  NumElements = 1
  Placement = pos=(0,-90,0) rot=(0,0,1;0rad)
  Type = lattice2AttachablePlacement.AttachablePlacement
  isLattice = 1
  expr: .Placement.Base.y = -<<Dimensions_sketch>>.Constraints.offset
FEATURE [Part::FeaturePython] Placment027  # WARN: FeaturePython — macro-defined, semantics opaque (R4)
  AttacherType = Attacher::AttachEngine3D
  ExposePlacement = true
  MarkerShape = 1
  MarkerSize = 10
  NumElements = 1
  Placement = pos=(0,0,813) rot=(0,0,1;0rad)
  Type = lattice2AttachablePlacement.AttachablePlacement
  isLattice = 1
  expr: .Placement.Base.z = <<BaseBend001>>.length
FEATURE [Part::FeaturePython] Populate042  label="Populate Placment026 with Extrude023"  # WARN: FeaturePython — macro-defined, semantics opaque (R4)
  Copying = 0
  ExposePlacement = false
  MarkerShape = 1
  MarkerSize = 0
  NumElements = 0
  Object = -> Extrude023
  OutputCompounding = 2
  PlacementsTo = -> Placment026
  Referencing = 0
  Type = lattice2PopulateCopies.LatticePopulateCopies
  isLattice = 0
FEATURE [Part::FeaturePython] Populate043  label="Populate Placment027 with Extrude023"  # WARN: FeaturePython — macro-defined, semantics opaque (R4)
  Copying = 0
  ExposePlacement = false
  MarkerShape = 1
  MarkerSize = 0
  NumElements = 0
  Object = -> Extrude023
  OutputCompounding = 2
  PlacementsTo = -> Placment027
  Referencing = 0
  Type = lattice2PopulateCopies.LatticePopulateCopies
  isLattice = 0
FEATURE [Sketcher::SketchObject] Sketch094
  FullyConstrained = true
  expr: Constraints[12] = <<Dimensions_sketch>>.Constraints.total_width / 2 - 3 mm
  expr: Constraints[13] = <<Dimensions_sketch>>.Constraints.total_depth
  expr: Constraints[14] = <<Dimensions_sketch>>.Constraints.total_width / 2
  expr: Constraints[15] = <<Dimensions_sketch>>.Constraints.total_depth + 6 mm
  sketch-geometry (5):
    g0: LineSegment StartX=0 StartY=226 StartZ=0 EndX=319.563 EndY=226 EndZ=0
    g1: LineSegment StartX=319.563 StartY=226 StartZ=0 EndX=319.563 EndY=220 EndZ=0
    g2: LineSegment StartX=319.563 StartY=220 StartZ=0 EndX=316.563 EndY=220 EndZ=0
    g3: LineSegment StartX=316.563 StartY=220 StartZ=0 EndX=316.563 EndY=3 EndZ=0
    g4: LineSegment StartX=316.563 StartY=3 StartZ=0 EndX=0 EndY=3 EndZ=0
  constraints (16):
    c: PointOnObject(g0,g-2)
    c: Horizontal(g0)
    c: Coincident(g0,g1)
    c: Vertical(g1)
    c: Coincident(g1,g2)
    c: Horizontal(g2)
    c: Coincident(g2,g3)
    c: Vertical(g3)
    c: Coincident(g3,g4)
    c: PointOnObject(g4,g-2)
    c: Horizontal(g4)
    c: DistanceY(g4) = 3
    c: DistanceX(g3) = 316.563
    c: DistanceY(g2) = 220
    c: DistanceX(g1) = 319.563
    c: DistanceY(g0) = 226
FEATURE [Part::Mirroring] Part__Mirroring021  label="Sketch094 (Mirror #20)"
  Base = (0,0,0)
  Normal = (1,0,0)
  Source = -> Sketch094
FEATURE [Part::FeaturePython] Connect012  # WARN: FeaturePython — macro-defined, semantics opaque (R4)
  Objects = -> [Sketch094,Part__Mirroring021]
  Tolerance = 0
FEATURE [PartDesign::SubShapeBinder] Binder031
  BindCopyOnChange = 0
  BindMode = 0
  ClaimChildren = true
  Context = -> Body025 [Binder031.]
  Fuse = false
  MakeFace = true
  OffsetFill = false
  OffsetIntersection = false
  OffsetJoinType = 0
  OffsetOpenResult = false
  PartialLoad = false
  Relative = false
  Support = -> [Connect012]
  _Version = 2
FEATURE [Sketcher::SketchObject] Sketch095  label="bottom_fix_base_sketch"
  FullyConstrained = false
  sketch-geometry (2):
    g0: LineSegment StartX=0 StartY=20.0162 StartZ=0 EndX=0 EndY=0 EndZ=0
    g1: LineSegment StartX=0 StartY=0 StartZ=0 EndX=20.3074 EndY=0 EndZ=0
  constraints (4):
    c: PointOnObject(g0,g-2)
    c: Coincident(g0,g-1)
    c: Coincident(g1,g0)
    c: PointOnObject(g1,g-1)
FEATURE [PartDesign::SubShapeBinder] Binder032
  BindCopyOnChange = 0
  BindMode = 0
  ClaimChildren = true
  Context = -> Body026 [Binder032.]
  Fuse = false
  MakeFace = true
  OffsetFill = false
  OffsetIntersection = false
  OffsetJoinType = 0
  OffsetOpenResult = false
  PartialLoad = false
  Relative = false
  Support = -> [Sketch095]
  _Version = 2
FEATURE [PartDesign::FeaturePython] BaseBend021  # WARN: FeaturePython — macro-defined, semantics opaque (R4)
  BendSide = 0
  BendSketch = -> Binder032
  MidPlane = true
  Reverse = false
  Suppressed = false
  length = 100
  radius = 0.1
  thickness = 0.3
FEATURE [Part::FeaturePython] Placment028  # WARN: FeaturePython — macro-defined, semantics opaque (R4)
  AttacherType = Attacher::AttachEngine3D
  ExposePlacement = true
  MarkerShape = 1
  MarkerSize = 10
  NumElements = 1
  Placement = pos=(3,10,0) rot=(0.57735,0.57735,-0.57735;4.18879rad)
  Type = lattice2AttachablePlacement.AttachablePlacement
  isLattice = 1
FEATURE [Part::FeaturePython] Placment029  # WARN: FeaturePython — macro-defined, semantics opaque (R4)
  AttacherType = Attacher::AttachEngine3D
  ExposePlacement = true
  MarkerShape = 1
  MarkerSize = 5
  NumElements = 1
  Placement = pos=(10,3,0) rot=(1,0,0;1.5708rad)
  Type = lattice2AttachablePlacement.AttachablePlacement
  isLattice = 1
FEATURE [Part::FeaturePython] LinearArray016  # WARN: FeaturePython — macro-defined, semantics opaque (R4)
  Alignment = 0
  CellStart = A1
  Count = 5
  Dir = (0,0,1)
  DirIsDriven = true
  DistributionLaw = 0
  DrivenProperty = 1
  EndInclusive = true
  ExposePlacement = false
  GeneratorMode = 0
  MarkerShape = 1
  MarkerSize = 0
  NumElements = 5
  OrientMode = 0
  Placement = pos=(0,0,-25) rot=(0,0,1;0rad)
  Point = (0,0,0)
  PointIsDriven = true
  Reverse = false
  SpanEnd = 50
  SpanStart = 0
  Step = 12.5
  Type = lattice2LinearArray.LinearArray
  VSGVersion = 1
  Values = 0.0 | 12.5 | 25.0 | 37.5 | 50.0
  ValuesSource = 2
  isLattice = 1
  expr: .Placement.Base.z = -SpanEnd / 2
FEATURE [Part::FeaturePython] Populate044  label="Populate Placment028 with hole_3.4mm"  # WARN: FeaturePython — macro-defined, semantics opaque (R4)
  Copying = 0
  ExposePlacement = false
  MarkerShape = 1
  MarkerSize = 0
  NumElements = 0
  Object = -> Cylinder003
  OutputCompounding = 2
  PlacementsTo = -> Placment028
  Referencing = 0
  Type = lattice2PopulateCopies.LatticePopulateCopies
  isLattice = 0
FEATURE [Sketcher::SketchObject] Sketch096
  FullyConstrained = true
  MapMode = 5
  Placement = pos=(0,0,0) rot=(0.57735,0.57735,0.57735;2.0944rad)
  sketch-geometry (6):
    g0: LineSegment StartX=0 StartY=0 StartZ=0 EndX=0 EndY=8 EndZ=0
    g1: LineSegment StartX=0 StartY=8 StartZ=0 EndX=4 EndY=8 EndZ=0
    g2: LineSegment StartX=4 StartY=8 StartZ=0 EndX=4 EndY=6 EndZ=0
    g3: LineSegment StartX=4 StartY=6 StartZ=0 EndX=1.7 EndY=6 EndZ=0
    g4: LineSegment StartX=1.7 StartY=6 StartZ=0 EndX=1.7 EndY=0 EndZ=0
    g5: LineSegment StartX=1.7 StartY=0 StartZ=0 EndX=0 EndY=0 EndZ=0
  constraints (17):
    c: Coincident(g-1,g0)
    c: PointOnObject(g0,g-2)
    c: Coincident(g0,g1)
    c: Horizontal(g1)
    c: Coincident(g1,g2)
    c: Vertical(g2)
    c: Coincident(g2,g3)
    c: Horizontal(g3)
    c: Coincident(g3,g4)
    c: PointOnObject(g4,g-1)
    c: Vertical(g4)
    c: Coincident(g4,g5)
    c: Coincident(g5,g0)
    c: DistanceX(g4) = 1.7
    c: DistanceY(g0) = 8
    c: DistanceX(g1,g1) = 4
    c: DistanceY(g2,g2) = 2
FEATURE [PartDesign::Revolution] Revolution003
  Angle = 360
  Angle2 = 60
  Axis = (1e-16,-1e-16,1)
  Base = (0,0,0)
  Placement = pos=(0,0,0) rot=(0.57735,0.57735,0.57735;2.0944rad)
  Profile = -> Sketch096
  ReferenceAxis = -> Sketch096 [V_Axis]
  Reversed = true
  Suppressed = false
  Type = 0
FEATURE [PartDesign::Body] Body027
  Group = -> [Sketch096,Revolution003]
  Origin = -> Origin028
  Tip = -> Revolution003
FEATURE [Part::FeaturePython] Populate045  label="Populate Placment029 with Body027"  # WARN: FeaturePython — macro-defined, semantics opaque (R4)
  Copying = 0
  ExposePlacement = false
  MarkerShape = 1
  MarkerSize = 0
  NumElements = 0
  Object = -> Body027
  OutputCompounding = 2
  PlacementsTo = -> Placment029
  Referencing = 0
  Type = lattice2PopulateCopies.LatticePopulateCopies
  isLattice = 0
FEATURE [Part::Compound] Compound030
  Links = -> [Populate044,Populate045]
FEATURE [Part::FeaturePython] Populate046  label="Populate LinearArray016 with Compound030"  # WARN: FeaturePython — macro-defined, semantics opaque (R4)
  Copying = 0
  ExposePlacement = false
  MarkerShape = 1
  MarkerSize = 0
  NumElements = 0
  Object = -> Compound030
  OutputCompounding = 1
  PlacementsTo = -> LinearArray016
  Referencing = 0
  Type = lattice2PopulateCopies.LatticePopulateCopies
  isLattice = 0
FEATURE [Part::FeaturePython] LinearArray017  # WARN: FeaturePython — macro-defined, semantics opaque (R4)
  Alignment = 0
  CellStart = A1
  Count = 5
  Dir = (0,0,1)
  DirIsDriven = true
  DistributionLaw = 0
  DrivenProperty = 1
  EndInclusive = true
  ExposePlacement = false
  GeneratorMode = 0
  MarkerShape = 1
  MarkerSize = 0
  NumElements = 5
  OrientMode = 0
  Point = (0,0,0)
  PointIsDriven = true
  Reverse = false
  SpanEnd = 100
  SpanStart = 0
  Step = 25
  Type = lattice2LinearArray.LinearArray
  VSGVersion = 1
  Values = 0.0 | 25.0 | 50.0 | 75.0 | 100.0
  ValuesSource = 2
  isLattice = 1
FEATURE [Part::FeaturePython] Populate047  label="Populate LinearArray017 with Compound030"  # WARN: FeaturePython — macro-defined, semantics opaque (R4)
  Copying = 0
  ExposePlacement = false
  MarkerShape = 1
  MarkerSize = 0
  NumElements = 0
  Object = -> Compound030
  OutputCompounding = 1
  PlacementsTo = -> LinearArray017
  Referencing = 0
  Type = lattice2PopulateCopies.LatticePopulateCopies
  isLattice = 0
FEATURE [Part::FeaturePython] LinearArray018  # WARN: FeaturePython — macro-defined, semantics opaque (R4)
  Alignment = 0
  CellStart = A1
  Count = 5
  Dir = (0,0,1)
  DirIsDriven = true
  DistributionLaw = 0
  DrivenProperty = 1
  EndInclusive = true
  ExposePlacement = false
  GeneratorMode = 0
  MarkerShape = 1
  MarkerSize = 0
  NumElements = 5
  OrientMode = 0
  Point = (0,0,0)
  PointIsDriven = true
  Reverse = false
  SpanEnd = 100
  SpanStart = 0
  Step = 25
  Type = lattice2LinearArray.LinearArray
  VSGVersion = 1
  Values = 0.0 | 25.0 | 50.0 | 75.0 | 100.0
  ValuesSource = 2
  isLattice = 1
FEATURE [Part::FeaturePython] Populate048  label="Populate LinearArray018 with Compound030"  # WARN: FeaturePython — macro-defined, semantics opaque (R4)
  Copying = 0
  ExposePlacement = false
  MarkerShape = 1
  MarkerSize = 0
  NumElements = 0
  Object = -> Compound030
  OutputCompounding = 1
  PlacementsTo = -> LinearArray018
  Referencing = 0
  Type = lattice2PopulateCopies.LatticePopulateCopies
  isLattice = 0
FEATURE [Part::Compound] Compound031
  Links = -> [Populate046]
FEATURE [PartDesign::Boolean] Boolean034
  BaseFeature = -> BaseBend021
  Group = -> [Compound031]
  Suppressed = false
  Type = 1
  UsePlacement = true
FEATURE [PartDesign::Body] Body026  label="bottom_fix_back"
  Group = -> [Binder032,BaseBend021,Boolean034]
  Origin = -> Origin027
  Tip = -> Boolean034
FEATURE [PartDesign::SubtractiveCylinder] Cylinder004
  Angle = 360
  AttacherType = Attacher::AttachEngine3D
  AttachmentOffset = pos=(0,-30,0) rot=(0,0,1;0rad)
  AttachmentSupport = -> [XY_Plane006]
  BaseFeature = -> Bend001
  FirstAngle = 0
  Height = 10
  MapMode = 5
  Placement = pos=(0,-30,0) rot=(0,0,1;0rad)
  Radius = 4
  SecondAngle = 0
  Suppressed = false
FEATURE [PartDesign::Pocket] Pocket
  BaseFeature = -> Cylinder004
  Direction = (0,0,-1)
  Length = 5
  Length2 = 5
  Midplane = true
  Placement = pos=(0,-30,0) rot=(0,0,1;0rad)
  Profile = -> Sketch022
  ReferenceAxis = -> Sketch022 [N_Axis]
  Suppressed = false
  Type = 1
FEATURE [PartDesign::Pocket] Pocket001
  BaseFeature = -> Pocket
  Direction = (0,0,-1)
  Length = 5
  Length2 = 5
  Midplane = true
  Placement = pos=(0,-30,0) rot=(0,0,1;0rad)
  Profile = -> Sketch023
  ReferenceAxis = -> Sketch023 [N_Axis]
  Suppressed = false
  Type = 1
FEATURE [PartDesign::Pocket] Pocket005
  BaseFeature = -> Pocket001
  Direction = (0,0,-1)
  Length = 5
  Length2 = 5
  Midplane = true
  Placement = pos=(0,-30,0) rot=(0,0,1;0rad)
  Profile = -> Sketch036
  ReferenceAxis = -> Sketch036 [N_Axis]
  Suppressed = false
  Type = 1
FEATURE [PartDesign::Mirrored] Mirrored
  BaseFeature = -> Pocket005
  MirrorPlane = -> YZ_Plane006
  Originals = -> [Pocket,Pocket005,Pocket001]
  Placement = pos=(0,-30,0) rot=(0,0,1;0rad)
  Suppressed = false
FEATURE [Sketcher::SketchObject] Sketch097
  FullyConstrained = true
  Placement = pos=(0,0,0) rot=(1,0,0;1.5708rad)
  sketch-geometry (3):
    g0: LineSegment StartX=-15 StartY=-15 StartZ=0 EndX=-15 EndY=0 EndZ=0
    g1: LineSegment StartX=-15 StartY=0 StartZ=0 EndX=15 EndY=0 EndZ=0
    g2: LineSegment StartX=15 StartY=0 StartZ=0 EndX=15 EndY=-15 EndZ=0
  constraints (9):
    c: PointOnObject(g0,g-1)
    c: Vertical(g0)
    c: Coincident(g0,g1)
    c: PointOnObject(g1,g-1)
    c: Coincident(g1,g2)
    c: Vertical(g2)
    c: Symmetric(g2,g0,g-2)
    c: DistanceX(g1,g1) = 30
    c: DistanceY(g2,g2) = 15
FEATURE [PartDesign::FeaturePython] BaseBend022  # WARN: FeaturePython — macro-defined, semantics opaque (R4)
  BendSide = 0
  BendSketch = -> Sketch097
  MidPlane = false
  Reverse = false
  Suppressed = false
  length = 100
  radius = 1
  thickness = 1
FEATURE [Sketcher::SketchObject] Sketch098
  FullyConstrained = true
  MapMode = 5
  Placement = pos=(0,0,0) rot=(0.57735,0.57735,0.57735;2.0944rad)
  expr: Constraints[16] = <<BaseBend022>>.thickness + <<BaseBend022>>.radius
  sketch-geometry (9):
    g0: LineSegment StartX=0 StartY=0 StartZ=0 EndX=-20 EndY=0 EndZ=0
    g1: LineSegment StartX=-20 StartY=0 StartZ=0 EndX=-20 EndY=-2 EndZ=0
    g2: LineSegment StartX=0 StartY=-15 StartZ=0 EndX=0 EndY=0 EndZ=0
    g3: LineSegment StartX=100 StartY=-150 StartZ=0 EndX=100 EndY=150 EndZ=0
    g4: LineSegment StartX=100 StartY=150 StartZ=0 EndX=-200 EndY=150 EndZ=0
    g5: LineSegment StartX=-200 StartY=150 StartZ=0 EndX=-200 EndY=-150 EndZ=0
    g6: LineSegment StartX=-200 StartY=-150 StartZ=0 EndX=100 EndY=-150 EndZ=0
    g7: LineSegment StartX=-20 StartY=-2 StartZ=0 EndX=-7 EndY=-15 EndZ=0
    g8: LineSegment StartX=-7 StartY=-15 StartZ=0 EndX=0 EndY=-15 EndZ=0
  constraints (26):
    c: Coincident(g-1,g0)
    c: PointOnObject(g0,g-1)
    c: Coincident(g0,g1)
    c: Vertical(g1)
    c: Coincident(g1,g7)
    c: PointOnObject(g8,g-2)
    c: Coincident(g8,g2)
    c: Coincident(g2,g0)
    c: Coincident(g3,g4)
    c: Coincident(g4,g5)
    c: Coincident(g5,g6)
    c: Coincident(g6,g3)
    c: Vertical(g3)
    c: Vertical(g5)
    c: Horizontal(g4)
    c: Horizontal(g6)
    c: DistanceY(g1,g1) = 2
    c: DistanceX(g0,g0) = 20
    c: DistanceX(g5,g3) = 300
    c: DistanceY(g5,g3) = 300
    c: DistanceX(g3) = 100
    c: DistanceY(g3) = 150
    c: Coincident(g7,g8)
    c: Horizontal(g8)
    c: Angle(g7) = -0.785398
    c: DistanceY(g2) = -15
FEATURE [PartDesign::Pocket] Pocket017
  BaseFeature = -> BaseBend022
  Direction = (-1,-1e-16,1e-16)
  Length = 5
  Length2 = 5
  Midplane = true
  Profile = -> Sketch098
  ReferenceAxis = -> Sketch098 [N_Axis]
  Suppressed = false
  Type = 1
FEATURE [PartDesign::FeaturePython] Bend010  # WARN: FeaturePython — macro-defined, semantics opaque (R4)
  AutoMiter = true
  BaseFeature = -> Pocket017
  BendType = 0
  LengthList = [10]
  LengthSpec = 0
  ReliefFactor = 0.7
  Suppressed = false
  UseReliefFactor = false
  angle = 90
  baseObject = -> Pocket017 [Edge34,Edge3]
  bendAList = [90]
  extend1 = 0
  extend2 = 0
  gap1 = 0
  gap2 = 0
  invert = false
  kfactor = 0.5
  length = 10
  maxExtendDist = 5
  minGap = 0.2
  minReliefGap = 1
  miterangle1 = 0
  miterangle2 = 0
  offset = 0
  radius = 1
  reliefType = 0
  reliefd = 1
  reliefw = 0.8
  sketchflip = false
  sketchinvert = false
  unfold = false
  expr: radius = BaseBend022.radius
FEATURE [Sketcher::SketchObject] Sketch099
  FullyConstrained = true
  MapMode = 5
  sketch-geometry (6):
    g0: ArcOfCircle CenterX=-7.5 CenterY=-2 CenterZ=0 NormalX=0 NormalY=0 NormalZ=1 AngleXU=0 Radius=2 StartAngle=0 EndAngle=1.5708
    g1: ArcOfCircle CenterX=7.5 CenterY=-2 CenterZ=0 NormalX=0 NormalY=0 NormalZ=1 AngleXU=0 Radius=2 StartAngle=1.5708 EndAngle=3.14159
    g2: LineSegment StartX=-5.5 StartY=-2 StartZ=0 EndX=-5.5 EndY=-7 EndZ=0
    g3: LineSegment StartX=5.5 StartY=-2 StartZ=0 EndX=5.5 EndY=-7 EndZ=0
    g4: ArcOfCircle CenterX=0 CenterY=-7 CenterZ=0 NormalX=0 NormalY=0 NormalZ=1 AngleXU=0 Radius=5.5 StartAngle=3.14159 EndAngle=6.28319
    g5: LineSegment StartX=-7.5 StartY=0 StartZ=0 EndX=7.5 EndY=0 EndZ=0
  constraints (15):
    c: PointOnObject(g4,g-2)
    c: DistanceY(g4) = -7
    c: PointOnObject(g0,g-1)
    c: PointOnObject(g1,g-1)
    c: Vertical(g3)
    c: Diameter(g4) = 11
    c: Tangent(g4,g2) = -1.5708
    c: Vertical(g2)
    c: Tangent(g2,g0) = 1.5708
    c: Tangent(g4,g3) = 1.5708
    c: Tangent(g3,g1) = -1.5708
    c: Equal(g1,g0)
    c: Radius(g1) = 2
    c: Tangent(g5,g0) = 1.5708
    c: Tangent(g5,g1) = 1.5708
FEATURE [PartDesign::Pocket] Pocket018
  BaseFeature = -> Bend010
  Direction = (0,0,-1)
  Length = 5
  Length2 = 5
  Midplane = true
  Profile = -> Sketch099
  ReferenceAxis = -> Sketch099 [N_Axis]
  Suppressed = false
  Type = 1
FEATURE [Part::FeaturePython] Placment030  # WARN: FeaturePython — macro-defined, semantics opaque (R4)
  AttacherType = Attacher::AttachEngine3D
  AttachmentOffset = pos=(-22,0,-10) rot=(0.57735,-0.57735,0.57735;2.0944rad)
  ExposePlacement = true
  MapMode = 7
  MarkerShape = 1
  MarkerSize = 5
  NumElements = 1
  Placement = pos=(-22,-12.9289,-9.07107) rot=(0.678598,-0.678598,0.281085;2.59356rad)
  Type = lattice2AttachablePlacement.AttachablePlacement
  isLattice = 1
FEATURE [Part::FeaturePython] Mirror008  label="Mirror008 of Placment030"  # WARN: FeaturePython — macro-defined, semantics opaque (R4)
  ExposePlacement = false
  FlipX = true
  FlipY = false
  FlipZ = false
  MarkerShape = 1
  MarkerSize = 10
  NumElements = 1
  Object = -> Placment030
  ObjectTraversal = 0
  Type = lattice2Mirror.LatticeMirror
  isLattice = 1
FEATURE [Part::FeaturePython] Join011  # WARN: FeaturePython — macro-defined, semantics opaque (R4)
  ExposePlacement = false
  Interleave = false
  Links = -> [Placment030,Mirror008]
  MarkerShape = 1
  MarkerSize = 0
  NumElements = 2
  Type = lattice2JoinArrays.JoinArrays
  isLattice = 1
FEATURE [Part::FeaturePython] Populate049  label="Populate Join011 with hole_3.4mm"  # WARN: FeaturePython — macro-defined, semantics opaque (R4)
  Copying = 0
  ExposePlacement = false
  MarkerShape = 1
  MarkerSize = 0
  NumElements = 0
  Object = -> Cylinder003
  OutputCompounding = 1
  PlacementsTo = -> Join011
  Referencing = 0
  Type = lattice2PopulateCopies.LatticePopulateCopies
  isLattice = 0
FEATURE [Part::Compound] Compound032
  Links = -> [Populate049]
FEATURE [PartDesign::Boolean] Boolean035
  BaseFeature = -> Pocket018
  Group = -> [Compound032]
  Suppressed = false
  Type = 1
  UsePlacement = true
FEATURE [Sketcher::SketchObject] Sketch100
  AttachmentSupport = -> [YZ_Plane008]
  ExternalGeometry = -> [Binder011]
  FullyConstrained = true
  MapMode = 5
  Placement = pos=(0,0,0) rot=(0.57735,0.57735,0.57735;2.0944rad)
  sketch-geometry (1):
    g0: LineSegment StartX=52 StartY=69 StartZ=0 EndX=52 EndY=0 EndZ=0
  constraints (4):
    c: PointOnObject(g0,g-3)
    c: PointOnObject(g0,g-1)
    c: Vertical(g0)
    c: DistanceY(g0) = 69
FEATURE [PartDesign::CoordinateSystem] Local_CS032
  AttacherType = Attacher::AttachEngine3D
  AttachmentOffset = pos=(103,0,0) rot=(1,0,0;-0.785398rad)
  AttachmentSupport = -> [Sketch100]
  MapMode = 1
  Placement = pos=(103,52,69) rot=(-1,0,0;0.785398rad)
FEATURE [PartDesign::CoordinateSystem] Local_CS033  label="pump_holder_orig_LCS"
  AttacherType = Attacher::AttachEngine3D
  AttachmentOffset = pos=(0,97,0) rot=(0,0,1;0rad)
  AttachmentSupport = -> [XY_Plane008]
  MapMode = 5
  Placement = pos=(0,97,0) rot=(0,0,1;0rad)
FEATURE [PartDesign::CoordinateSystem] Local_CS034
  AttacherType = Attacher::AttachEngine3D
  AttachmentOffset = pos=(0,-26,0) rot=(1,0,0;-0.785398rad)
  MapMode = 5
  Placement = pos=(0,-26,0) rot=(-1,0,0;0.785398rad)
FEATURE [Sketcher::SketchObject] Sketch101
  AttachmentSupport = -> [Local_CS032]
  FullyConstrained = true
  MapMode = 5
  Placement = pos=(103,52,69) rot=(-1,0,0;0.785398rad)
  sketch-geometry (2):
    g0: Circle CenterX=22 CenterY=15.6586 CenterZ=0 NormalX=0 NormalY=0 NormalZ=1 AngleXU=0 Radius=1.7
    g1: Circle CenterX=-22 CenterY=15.6586 CenterZ=0 NormalX=0 NormalY=0 NormalZ=1 AngleXU=0 Radius=1.7
  constraints (5):
    c: Symmetric(g1,g0,g-2)
    c: Equal(g0,g1)
    c: Diameter(g0) = 3.4
    c: DistanceX(g0) = 22
    c: DistanceY(g0) = 15.6586
FEATURE [PartDesign::CoordinateSystem] Local_CS035
  AttacherType = Attacher::AttachEngine3D
  AttachmentOffset = pos=(0,-7,-1) rot=(0,0,1;0rad)
  AttachmentSupport = -> [XY_Plane029]
  MapMode = 5
  Placement = pos=(0,-7,-1) rot=(0,0,1;0rad)
FEATURE [Sketcher::SketchObject] Sketch102
  AttachmentSupport = -> [Local_CS032]
  ExternalGeometry = -> [Binder011]
  FullyConstrained = true
  MapMode = 5
  Placement = pos=(103,52,69) rot=(-1,0,0;0.785398rad)
  sketch-geometry (11):
    g0: LineSegment StartX=-9.5 StartY=3 StartZ=0 EndX=9.5 EndY=3 EndZ=0
    g1: LineSegment StartX=14.5 StartY=8 StartZ=0 EndX=14.5 EndY=45.7401 EndZ=0
    g2: LineSegment StartX=9.5 StartY=50.7401 StartZ=0 EndX=-9.5 EndY=50.7401 EndZ=0
    g3: LineSegment StartX=-14.5 StartY=45.7401 StartZ=0 EndX=-14.5 EndY=8 EndZ=0
    g4: ArcOfCircle CenterX=-9.5 CenterY=8 CenterZ=0 NormalX=0 NormalY=0 NormalZ=1 AngleXU=0 Radius=5 StartAngle=3.14159 EndAngle=4.71239
    g5: ArcOfCircle CenterX=9.5 CenterY=8 CenterZ=0 NormalX=0 NormalY=0 NormalZ=1 AngleXU=0 Radius=5 StartAngle=4.71239 EndAngle=6.28319
    g6: ArcOfCircle CenterX=9.5 CenterY=45.7401 CenterZ=0 NormalX=0 NormalY=0 NormalZ=1 AngleXU=0 Radius=5 StartAngle=3e-16 EndAngle=1.5708
    g7: ArcOfCircle CenterX=-9.5 CenterY=45.7401 CenterZ=0 NormalX=0 NormalY=0 NormalZ=1 AngleXU=0 Radius=5 StartAngle=1.5708 EndAngle=3.14159
    g8: GeomPoint X=-14.5 Y=3 Z=0
    g9: GeomPoint X=14.5 Y=50.7401 Z=0
    g10: GeomPoint X=0 Y=26.8701 Z=0
  constraints (25):
    c: Tangent(g0,g4) = -1.5708
    c: Tangent(g0,g5) = -1.5708
    c: Tangent(g1,g5) = -1.5708
    c: Tangent(g1,g6) = -1.5708
    c: Tangent(g2,g6) = -1.5708
    c: Tangent(g2,g7) = -1.5708
    c: Tangent(g3,g7) = -1.5708
    c: Tangent(g3,g4) = -1.5708
    c: Horizontal(g0)
    c: Horizontal(g2)
    c: Vertical(g1)
    c: Vertical(g3)
    c: Equal(g4,g5)
    c: Equal(g5,g6)
    c: Equal(g6,g7)
    c: PointOnObject(g8,g0)
    c: PointOnObject(g8,g3)
    c: PointOnObject(g9,g1)
    c: PointOnObject(g9,g2)
    c: Radius(g6) = 5
    c: Symmetric(g8,g9,g10)
    c: DistanceX(g8,g9) = 29
    c: DistanceY(g9,g-3) = 3
    c: DistanceY(g8) = 3
    c: PointOnObject(g10,g-2)
FEATURE [Part::Feature] Unfold002  label="lamp_holder_Unfold"
  Placement = pos=(-2.84e-13,-1.12e-13,105.825) rot=(0.889126,0.323616,-0.323616;1.68804rad)
  shape: bbox 104 x 540 x 0.702 mm, 36 faces (baked)
FEATURE [Sketcher::SketchObject] Unfold_Sketch002  label="lamp_holder_Sketch"
  FullyConstrained = false
  sketch-geometry (36):
    g0: LineSegment StartX=335.362 StartY=-1e-16 StartZ=0 EndX=401.665 EndY=-1e-16 EndZ=0
    g1: ArcOfCircle CenterX=335.362 CenterY=-2 CenterZ=0 NormalX=0 NormalY=0 NormalZ=1 AngleXU=0 Radius=2 StartAngle=1.5708 EndAngle=3.14159
    g2: LineSegment StartX=333.362 StartY=-2 StartZ=0 EndX=333.362 EndY=-29 EndZ=0
    g3: ArcOfCircle CenterX=331.362 CenterY=-29 CenterZ=0 NormalX=0 NormalY=0 NormalZ=1 AngleXU=0 Radius=2 StartAngle=4.71239 EndAngle=6.28319
    g4: LineSegment StartX=331.362 StartY=-31 StartZ=0 EndX=329.353 EndY=-31 EndZ=0
    g5: BSplineCurve PolesCount=15 KnotsCount=13 Degree=3 IsPeriodic=0
    g6: LineSegment StartX=325.662 StartY=-31 StartZ=0 EndX=304.662 EndY=-31 EndZ=0
    g7: ArcOfCircle CenterX=304.662 CenterY=-33 CenterZ=0 NormalX=0 NormalY=0 NormalZ=1 AngleXU=0 Radius=2 StartAngle=1.5708 EndAngle=3.14159
    g8: LineSegment StartX=302.662 StartY=-33 StartZ=0 EndX=302.662 EndY=-535 EndZ=0
    g9: ArcOfCircle CenterX=307.662 CenterY=-535 CenterZ=0 NormalX=0 NormalY=0 NormalZ=1 AngleXU=3.14159 Radius=5 StartAngle=2.962e-13 EndAngle=1.5708
    g10: LineSegment StartX=307.662 StartY=-540 StartZ=0 EndX=401.665 EndY=-540 EndZ=0
    g11: ArcOfCircle CenterX=401.665 CenterY=-535 CenterZ=0 NormalX=0 NormalY=0 NormalZ=1 AngleXU=0 Radius=5 StartAngle=4.71239 EndAngle=6.28319
    g12: LineSegment StartX=406.665 StartY=-5 StartZ=0 EndX=406.665 EndY=-535 EndZ=0
    g13: ArcOfCircle CenterX=401.665 CenterY=-5 CenterZ=0 NormalX=0 NormalY=0 NormalZ=1 AngleXU=0 Radius=5 StartAngle=2.967e-13 EndAngle=1.5708
    g14: Circle CenterX=308.362 CenterY=-530 CenterZ=0 NormalX=0 NormalY=0 NormalZ=1 AngleXU=-1.5708 Radius=4
    g15: LineSegment StartX=377.793 StartY=-533.8 StartZ=0 EndX=377.793 EndY=-532.2 EndZ=0
    g16: ArcOfCircle CenterX=379.493 CenterY=-532.2 CenterZ=0 NormalX=0 NormalY=0 NormalZ=1 AngleXU=-2e-16 Radius=1.7 StartAngle=0 EndAngle=3.14159
    g17: LineSegment StartX=381.193 StartY=-533.8 StartZ=0 EndX=381.193 EndY=-532.2 EndZ=0
    g18: ArcOfCircle CenterX=379.493 CenterY=-533.8 CenterZ=0 NormalX=0 NormalY=0 NormalZ=1 AngleXU=-2e-16 Radius=1.7 StartAngle=3.14159 EndAngle=6.28319
    g19: LineSegment StartX=385.693 StartY=-533.8 StartZ=0 EndX=385.693 EndY=-532.2 EndZ=0
    g20: ArcOfCircle CenterX=387.393 CenterY=-532.2 CenterZ=0 NormalX=0 NormalY=0 NormalZ=1 AngleXU=3.14159 Radius=1.7 StartAngle=3.14159 EndAngle=6.28319
    g21: LineSegment StartX=389.093 StartY=-533.8 StartZ=0 EndX=389.093 EndY=-532.2 EndZ=0
    g22: ArcOfCircle CenterX=387.393 CenterY=-533.8 CenterZ=0 NormalX=0 NormalY=0 NormalZ=1 AngleXU=3.14159 Radius=1.7 StartAngle=0 EndAngle=3.14159
    g23: LineSegment StartX=377.793 StartY=-7.8 StartZ=0 EndX=377.793 EndY=-6.2 EndZ=0
    g24: ArcOfCircle CenterX=379.493 CenterY=-6.2 CenterZ=0 NormalX=0 NormalY=0 NormalZ=1 AngleXU=3.14159 Radius=1.7 StartAngle=3.14159 EndAngle=6.28319
    g25: LineSegment StartX=381.193 StartY=-7.8 StartZ=0 EndX=381.193 EndY=-6.2 EndZ=0
    g26: ArcOfCircle CenterX=379.493 CenterY=-7.8 CenterZ=0 NormalX=0 NormalY=0 NormalZ=1 AngleXU=3.14159 Radius=1.7 StartAngle=2.913e-13 EndAngle=3.14159
    g27: LineSegment StartX=385.693 StartY=-7.8 StartZ=0 EndX=385.693 EndY=-6.2 EndZ=0
    g28: ArcOfCircle CenterX=387.393 CenterY=-6.2 CenterZ=0 NormalX=0 NormalY=0 NormalZ=1 AngleXU=-2e-16 Radius=1.7 StartAngle=2.967e-13 EndAngle=3.14159
    g29: LineSegment StartX=389.093 StartY=-7.8 StartZ=0 EndX=389.093 EndY=-6.2 EndZ=0
    g30: ArcOfCircle CenterX=387.393 CenterY=-7.8 CenterZ=0 NormalX=0 NormalY=0 NormalZ=1 AngleXU=-2e-16 Radius=1.7 StartAngle=3.14159 EndAngle=6.28319
    g31: Circle CenterX=315.362 CenterY=-525 CenterZ=0 NormalX=0 NormalY=0 NormalZ=1 AngleXU=-1.5708 Radius=1.7
    g32: Circle CenterX=315.362 CenterY=-37 CenterZ=0 NormalX=0 NormalY=0 NormalZ=1 AngleXU=-1.5708 Radius=1.7
    g33: Circle CenterX=307.362 CenterY=-403 CenterZ=0 NormalX=0 NormalY=0 NormalZ=1 AngleXU=-1.5708 Radius=1.7
    g34: Circle CenterX=307.362 CenterY=-159 CenterZ=0 NormalX=0 NormalY=0 NormalZ=1 AngleXU=-1.5708 Radius=1.7
    g35: Circle CenterX=315.362 CenterY=-281 CenterZ=0 NormalX=0 NormalY=0 NormalZ=1 AngleXU=-1.5708 Radius=1.7
FEATURE [Sketcher::SketchObject] Unfold_Sketch_bends002  label="lamp_holder_Sketch_bends"
  FullyConstrained = false
  sketch-geometry (2):
    g0: LineSegment StartX=395.988 StartY=-540 StartZ=0 EndX=395.988 EndY=0 EndZ=0
    g1: LineSegment StartX=327.508 StartY=-540 StartZ=0 EndX=327.508 EndY=-31 EndZ=0
FEATURE [Part::Mirroring] Part__Mirroring023  label="lamp_holder (Mirror #22)"
  Base = (0,0,0)
  Normal = (1,0,0)
  Source = -> Body003
FEATURE [TechDraw::DrawViewPart] View004
  CoarseView = false
  Direction = (0,0,1)
  Focus = 100
  HardHidden = false
  IsoCount = 0
  IsoHidden = false
  IsoVisible = false
  LockPosition = false
  Perspective = false
  Rotation = 0
  ScaleType = 0
  ScrubCount = 0
  SeamHidden = false
  SeamVisible = true
  SmoothHidden = false
  SmoothVisible = true
  Source = -> [Part__Mirroring023]
  X = 148.5
  XDirection = (1,0,0)
  Y = 105
FEATURE [TechDraw::DrawViewPart] View005
  CoarseView = false
  Direction = (1.6428,0.766,1)
  Focus = 100
  HardHidden = false
  IsoCount = 0
  IsoHidden = false
  IsoVisible = false
  LockPosition = false
  Perspective = false
  Rotation = 0
  Scale = 0.375
  ScaleType = 2
  ScrubCount = 0
  SeamHidden = false
  SeamVisible = true
  SmoothHidden = false
  SmoothVisible = true
  Source = -> [Part__Mirroring023]
  X = 258.5
  XDirection = (-0.707107,0.707107,0)
  Y = 105
FEATURE [TechDraw::DrawViewBalloon] Balloon001
  BubbleShape = 3
  EndType = 0
  EndTypeScale = 1
  KinkLength = 5
  LockPosition = false
  OriginX = 34.6843
  OriginY = 194.122
  Rotation = 0
  ScaleType = 0
  ShapeScale = 1
  SourceView = -> View005
  Text = Оборотная сторона
  TextWrapLen = -1
  X = -179.207
  Y = 242.647
FEATURE [Sketcher::SketchObject] Sketch103
  ExternalGeometry = -> [Sketch013]
  FullyConstrained = true
  Placement = pos=(0,0,0) rot=(0.57735,0.57735,0.57735;2.0944rad)
  sketch-geometry (2):
    g0: LineSegment StartX=-30 StartY=106 StartZ=0 EndX=-30 EndY=116 EndZ=0
    g1: LineSegment StartX=-30 StartY=116 StartZ=0 EndX=0 EndY=116 EndZ=0
  constraints (6):
    c: Vertical(g0)
    c: Coincident(g1,g0)
    c: Horizontal(g1)
    c: DistanceX(g1,g1) = 30
    c: DistanceY(g0,g0) = 10
    c: Coincident(g1,g-3)
FEATURE [Part::FeaturePython] BaseBend023  # WARN: FeaturePython — macro-defined, semantics opaque (R4)
  BendSide = 1
  BendSketch = -> Sketch103
  MidPlane = true
  Reverse = false
  length = 70
  radius = 2
  thickness = 0.7
FEATURE [Part::FeaturePython] LinearArray019  # WARN: FeaturePython — macro-defined, semantics opaque (R4)
  Alignment = 0
  CellStart = A1
  Count = 2
  Dir = (1,0,0)
  DirIsDriven = true
  DistributionLaw = 0
  DrivenProperty = 1
  EndInclusive = true
  ExposePlacement = false
  GeneratorMode = 0
  MarkerShape = 1
  MarkerSize = 0
  NumElements = 2
  OrientMode = 1
  Placement = pos=(-85,0,0) rot=(0,0,1;0rad)
  Point = (0,0,0)
  PointIsDriven = true
  Reverse = false
  SpanEnd = 170
  SpanStart = 0
  Step = 170
  Type = lattice2LinearArray.LinearArray
  VSGVersion = 1
  Values = 0.0 | 170.0
  ValuesSource = 2
  isLattice = 1
  expr: .Placement.Base.x = -SpanEnd / 2
FEATURE [Part::FeaturePython] Populate050  label="Populate LinearArray019 with BaseBend023"  # WARN: FeaturePython — macro-defined, semantics opaque (R4)
  Copying = 0
  ExposePlacement = false
  MarkerShape = 1
  MarkerSize = 0
  NumElements = 0
  Object = -> BaseBend023
  OutputCompounding = 1
  PlacementsTo = -> LinearArray019
  Referencing = 0
  Type = lattice2PopulateCopies.LatticePopulateCopies
  isLattice = 0
FEATURE [Part::Compound] Compound033
  Links = -> [Populate050]
FEATURE [PartDesign::Boolean] Boolean036
  BaseFeature = -> BaseBend005
  Group = -> [Compound033]
  Refine = true
  Suppressed = false
  Type = 0
  UsePlacement = true
FEATURE [PartDesign::Pocket] Pocket007
  BaseFeature = -> Boolean036
  Direction = (0,0.707107,0.707107)
  Length = 5
  Length2 = 5
  Profile = -> Sketch040
  ReferenceAxis = -> Sketch040 [N_Axis]
  Suppressed = false
  Type = 0
FEATURE [PartDesign::MultiTransform] MultiTransform
  BaseFeature = -> Pocket007
  Originals = -> [Pocket007]
  Suppressed = false
  Transformations = -> [LinearPattern,LinearPattern001]
FEATURE [Sketcher::SketchObject] Sketch104
  AttachmentSupport = -> [XY_Plane008]
  FullyConstrained = true
  MapMode = 5
  sketch-geometry (4):
    g0: ArcOfCircle CenterX=110 CenterY=-16 CenterZ=0 NormalX=0 NormalY=0 NormalZ=1 AngleXU=0 Radius=1.6 StartAngle=1.5708 EndAngle=4.71239
    g1: ArcOfCircle CenterX=113 CenterY=-16 CenterZ=0 NormalX=0 NormalY=0 NormalZ=1 AngleXU=0 Radius=1.6 StartAngle=4.71239 EndAngle=7.85398
    g2: LineSegment StartX=110 StartY=-14.4 StartZ=0 EndX=113 EndY=-14.4 EndZ=0
    g3: LineSegment StartX=110 StartY=-17.6 StartZ=0 EndX=113 EndY=-17.6 EndZ=0
  constraints (10):
    c: Tangent(g0,g2) = 1.5708
    c: Tangent(g0,g3) = -1.5708
    c: Tangent(g1,g2) = 1.5708
    c: Tangent(g1,g3) = -1.5708
    c: Equal(g0,g1)
    c: Horizontal(g3)
    c: Diameter(g1) = 3.2
    c: DistanceY(g1) = -16
    c: DistanceX(g0,g1) = 3
    c: DistanceX(g1) = 113
FEATURE [PartDesign::LinearPattern] LinearPattern003
  Direction = -> Sketch104 [H_Axis]
  Length = 40
  Mode = 0
  Occurrences = 2
  Offset = 40
  Reversed = true
  Suppressed = false
FEATURE [PartDesign::LinearPattern] LinearPattern004
  Direction = -> Sketch104 [V_Axis]
  Length = 10
  Mode = 0
  Occurrences = 2
  Offset = 10
  Reversed = true
  Suppressed = false
FEATURE [Sketcher::SketchObject] Sketch105
  AttachmentOffset = pos=(26,0,0) rot=(-1,0,0;1.5708rad)
  AttachmentSupport = -> [Sketch098]
  ExternalGeometry = -> [Sketch098]
  FullyConstrained = true
  MapMode = 7
  Placement = pos=(26,-20,-2) rot=(-1,0,0;0.785398rad)
  sketch-geometry (6):
    g0: ArcOfCircle CenterX=-2 CenterY=2 CenterZ=0 NormalX=0 NormalY=0 NormalZ=1 AngleXU=0 Radius=2 StartAngle=4.71239 EndAngle=6.28319
    g1: ArcOfCircle CenterX=-2 CenterY=16.3848 CenterZ=0 NormalX=0 NormalY=0 NormalZ=1 AngleXU=0 Radius=2 StartAngle=5.49e-14 EndAngle=1.5708
    g2: LineSegment StartX=-2 StartY=18.3848 StartZ=0 EndX=-3.9813e-12 EndY=18.3848 EndZ=0
    g3: LineSegment StartX=-3.9813e-12 StartY=18.3848 StartZ=0 EndX=-3.9813e-12 EndY=16.3848 EndZ=0
    g4: LineSegment StartX=-2 StartY=0 StartZ=0 EndX=0 EndY=0 EndZ=0
    g5: LineSegment StartX=0 StartY=0 StartZ=0 EndX=0 EndY=2 EndZ=0
  constraints (15):
    c: PointOnObject(g0,g-1)
    c: Tangent(g0,g4) = -1.5708
    c: Tangent(g5,g0) = -1.5708
    c: Tangent(g3,g1) = 1.5708
    c: Tangent(g1,g2) = 1.5708
    c: Horizontal(g2)
    c: Equal(g1,g0)
    c: Radius(g0) = 2
    c: Coincident(g4,g5)
    c: Coincident(g4,g-1)
    c: PointOnObject(g0,g-2)
    c: Coincident(g2,g3)
    c: PointOnObject(g2,g-2)
    c: Vertical(g3)
    c: Horizontal(g2,g-3)
FEATURE [PartDesign::Pocket] Pocket022
  BaseFeature = -> Boolean035
  Direction = (0,-0.707107,-0.707107)
  Length = 5
  Length2 = 5
  Profile = -> Sketch105
  ReferenceAxis = -> Sketch105 [N_Axis]
  Suppressed = false
  Type = 0
FEATURE [PartDesign::Mirrored] Mirrored005
  BaseFeature = -> Pocket022
  MirrorPlane = -> YZ_Plane029
  Originals = -> [Pocket022]
  Suppressed = false
FEATURE [PartDesign::Body] Body028
  Group = -> [BaseBend022,Sketch098,Pocket017,Bend010,Sketch099,Pocket018,Boolean035,Local_CS034,Local_CS035,Sketch105,Pocket022,Mirrored005]
  Origin = -> Origin029
  Tip = -> Mirrored005
FEATURE [Part::FeaturePython] Placment031  # WARN: FeaturePython — macro-defined, semantics opaque (R4)
  AttacherType = Attacher::AttachEngine3D
  AttachmentOffset = pos=(-35,0,0) rot=(0,0.707107,0.707107;3.14159rad)
  AttachmentSupport = -> [Sketch103]
  ExposePlacement = true
  MapMode = 7
  MarkerShape = 1
  MarkerSize = 10
  NumElements = 1
  Placement = pos=(35,-30,106) rot=(1,0,0;4.71239rad)
  Type = lattice2AttachablePlacement.AttachablePlacement
  isLattice = 1
  expr: .AttachmentOffset.Base.x = -<<BaseBend023>>.length / 2
FEATURE [Part::FeaturePython] Populate051  label="Populate Placment031 with Extrude005"  # WARN: FeaturePython — macro-defined, semantics opaque (R4)
  Copying = 0
  ExposePlacement = false
  MarkerShape = 1
  MarkerSize = 0
  NumElements = 0
  Object = -> Extrude005
  OutputCompounding = 2
  PlacementsTo = -> Placment031
  Referencing = 0
  Type = lattice2PopulateCopies.LatticePopulateCopies
  isLattice = 0
FEATURE [Part::FeaturePython] Mirror009  label="Mirror009 of Populate Placment031 with Extrude005"  # WARN: FeaturePython — macro-defined, semantics opaque (R4)
  ExposePlacement = false
  FlipX = true
  FlipY = false
  FlipZ = false
  MarkerShape = 1
  MarkerSize = 0
  NumElements = 0
  Object = -> Populate051
  ObjectTraversal = 0
  Type = lattice2Mirror.LatticeMirror
  isLattice = 0
FEATURE [Part::Compound] Compound034
  Links = -> [Mirror009,Populate051]
FEATURE [Part::FeaturePython] Populate052  label="Populate LinearArray019 with Compound034"  # WARN: FeaturePython — macro-defined, semantics opaque (R4)
  Copying = 0
  ExposePlacement = false
  MarkerShape = 1
  MarkerSize = 0
  NumElements = 0
  Object = -> Compound034
  OutputCompounding = 1
  PlacementsTo = -> LinearArray019
  Referencing = 0
  Type = lattice2PopulateCopies.LatticePopulateCopies
  isLattice = 0
FEATURE [Part::Compound] Compound006
  Links = -> [Populate012,Mirror001,Populate018,Populate019,Populate052]
FEATURE [PartDesign::Boolean] Boolean004
  BaseFeature = -> MultiTransform
  Group = -> [Compound006]
  Suppressed = false
  Type = 1
  UsePlacement = true
FEATURE [PartDesign::Pocket] Pocket019
  BaseFeature = -> Boolean004
  Direction = (0,-0.707107,-0.707107)
  Length = 5
  Length2 = 5
  Midplane = true
  Profile = -> Sketch101
  ReferenceAxis = -> Sketch101 [N_Axis]
  Refine = true
  Suppressed = false
  Type = 0
FEATURE [PartDesign::Pocket] Pocket020
  BaseFeature = -> Pocket019
  Direction = (0,-0.707107,-0.707107)
  Length = 5
  Length2 = 5
  Midplane = true
  Profile = -> Sketch102
  ReferenceAxis = -> Sketch102 [N_Axis]
  Suppressed = false
  Type = 0
FEATURE [PartDesign::Pocket] Pocket021
  BaseFeature = -> Pocket020
  Direction = (0,0,-1)
  Length = 5
  Length2 = 5
  Midplane = true
  Profile = -> Sketch104
  ReferenceAxis = -> Sketch104 [N_Axis]
  Suppressed = false
  Type = 1
FEATURE [PartDesign::MultiTransform] MultiTransform001
  BaseFeature = -> Pocket021
  Originals = -> [Pocket021]
  Suppressed = false
  Transformations = -> [LinearPattern003,LinearPattern004]
FEATURE [Part::Feature] Unfold004
  shape: bbox 72.53 x 27.91 x 1 mm, 24 faces (baked)
FEATURE [Sketcher::SketchObject] Unfold_Sketch_Outline001
  FullyConstrained = false
  sketch-geometry (20):
    g0: LineSegment StartX=35.6791 StartY=-14.3229 StartZ=0 EndX=28.3562 EndY=-7 EndZ=0
    g1: LineSegment StartX=28.3562 StartY=3.1e-15 StartZ=0 EndX=28.3562 EndY=-7 EndZ=0
    g2: LineSegment StartX=7.5 StartY=-1.5e-15 StartZ=0 EndX=28.3562 EndY=3.1e-15 EndZ=0
    g3: ArcOfCircle CenterX=7.5 CenterY=-2 CenterZ=0 NormalX=0 NormalY=0 NormalZ=1 AngleXU=0 Radius=2 StartAngle=1.5708 EndAngle=3.14159
    g4: LineSegment StartX=5.5 StartY=-2 StartZ=0 EndX=5.5 EndY=-7 EndZ=0
    g5: ArcOfCircle CenterX=0 CenterY=-7 CenterZ=0 NormalX=0 NormalY=0 NormalZ=1 AngleXU=0 Radius=5.5 StartAngle=3.14159 EndAngle=6.28319
    g6: LineSegment StartX=-5.5 StartY=-2 StartZ=0 EndX=-5.5 EndY=-7 EndZ=0
    g7: ArcOfCircle CenterX=-7.5 CenterY=-2 CenterZ=0 NormalX=0 NormalY=0 NormalZ=1 AngleXU=0 Radius=2 StartAngle=0 EndAngle=1.5708
    g8: LineSegment StartX=-28.3562 StartY=0 StartZ=0 EndX=-7.5 EndY=0 EndZ=0
    g9: LineSegment StartX=-28.3562 StartY=3.1e-15 StartZ=0 EndX=-28.3562 EndY=-7 EndZ=0
    g10: LineSegment StartX=-35.6791 StartY=-14.3229 StartZ=0 EndX=-28.3562 EndY=-7 EndZ=0
    g11: ArcOfCircle CenterX=-34.2649 CenterY=-15.7371 CenterZ=0 NormalX=0 NormalY=0 NormalZ=1 AngleXU=-2.35619 Radius=2 StartAngle=4.71239 EndAngle=6.28319
    g12: LineSegment StartX=-35.6791 StartY=-17.1514 StartZ=0 EndX=-25.5076 EndY=-27.3229 EndZ=0
    g13: ArcOfCircle CenterX=-24.0933 CenterY=-25.9087 CenterZ=0 NormalX=0 NormalY=0 NormalZ=1 AngleXU=-2.35619 Radius=2 StartAngle=0 EndAngle=1.5708
    g14: LineSegment StartX=-22.6791 StartY=-27.3229 StartZ=0 EndX=-15.3562 EndY=-20 EndZ=0
    g15: LineSegment StartX=15.3562 StartY=-20 StartZ=0 EndX=-15.3562 EndY=-20 EndZ=0
    g16: LineSegment StartX=22.6791 StartY=-27.3229 StartZ=0 EndX=15.3562 EndY=-20 EndZ=0
    g17: ArcOfCircle CenterX=24.0933 CenterY=-25.9087 CenterZ=0 NormalX=0 NormalY=0 NormalZ=1 AngleXU=-0.785398 Radius=2 StartAngle=4.71239 EndAngle=6.28319
    g18: LineSegment StartX=25.5076 StartY=-27.3229 StartZ=0 EndX=35.6791 EndY=-17.1514 EndZ=0
    g19: ArcOfCircle CenterX=34.2649 CenterY=-15.7371 CenterZ=0 NormalX=0 NormalY=0 NormalZ=1 AngleXU=-0.785398 Radius=2 StartAngle=5.5e-14 EndAngle=1.5708
FEATURE [Sketcher::SketchObject] Unfold_Sketch_Internal001
  FullyConstrained = false
  sketch-geometry (2):
    g0: Circle CenterX=-28.336 CenterY=-18.8377 CenterZ=0 NormalX=0 NormalY=0 NormalZ=1 AngleXU=-0.785398 Radius=1.7
    g1: Circle CenterX=28.336 CenterY=-18.8377 CenterZ=0 NormalX=0 NormalY=0 NormalZ=1 AngleXU=-2.35619 Radius=1.7
FEATURE [Sketcher::SketchObject] Unfold_Sketch_bends004
  FullyConstrained = false
  sketch-geometry (4):
    g0: LineSegment StartX=29.1892 StartY=-7.83304 StartZ=0 EndX=16.1892 EndY=-20.833 EndZ=0
    g1: LineSegment StartX=14.1781 StartY=-20 StartZ=0 EndX=14.1781 EndY=0 EndZ=0
    g2: LineSegment StartX=-16.1892 StartY=-20.833 StartZ=0 EndX=-29.1892 EndY=-7.83304 EndZ=0
    g3: LineSegment StartX=-14.1781 StartY=-20 StartZ=0 EndX=-14.1781 EndY=0 EndZ=0
FEATURE [Sketcher::SketchObject] Unfold_Sketch004
  ExternalGeometry = -> [Unfold_Sketch_bends004]
  FullyConstrained = false
  sketch-geometry (30):
    g0: LineSegment StartX=35.6791 StartY=-14.3229 StartZ=0 EndX=28.3562 EndY=-7 EndZ=0
    g1: LineSegment StartX=28.3562 StartY=3.1e-15 StartZ=0 EndX=28.3562 EndY=-7 EndZ=0
    g2: LineSegment StartX=7.5 StartY=-1.5e-15 StartZ=0 EndX=28.3562 EndY=3.1e-15 EndZ=0
    g3: ArcOfCircle CenterX=7.5 CenterY=-2 CenterZ=0 NormalX=0 NormalY=0 NormalZ=1 AngleXU=0 Radius=2 StartAngle=1.5708 EndAngle=3.14159
    g4: LineSegment StartX=5.5 StartY=-2 StartZ=0 EndX=5.5 EndY=-7 EndZ=0
    g5: ArcOfCircle CenterX=0 CenterY=-7 CenterZ=0 NormalX=0 NormalY=0 NormalZ=1 AngleXU=0 Radius=5.5 StartAngle=3.14159 EndAngle=6.28319
    g6: LineSegment StartX=-5.5 StartY=-2 StartZ=0 EndX=-5.5 EndY=-7 EndZ=0
    g7: ArcOfCircle CenterX=-7.5 CenterY=-2 CenterZ=0 NormalX=0 NormalY=0 NormalZ=1 AngleXU=0 Radius=2 StartAngle=0 EndAngle=1.5708
    g8: LineSegment StartX=-28.3562 StartY=0 StartZ=0 EndX=-7.5 EndY=0 EndZ=0
    g9: LineSegment StartX=-28.3562 StartY=3.1e-15 StartZ=0 EndX=-28.3562 EndY=-7 EndZ=0
    g10: LineSegment StartX=-35.6791 StartY=-14.3229 StartZ=0 EndX=-28.3562 EndY=-7 EndZ=0
    g11: ArcOfCircle CenterX=-34.2649 CenterY=-15.7371 CenterZ=0 NormalX=0 NormalY=0 NormalZ=1 AngleXU=-2.35619 Radius=2 StartAngle=4.71239 EndAngle=6.28319
    g12: LineSegment StartX=-35.6791 StartY=-17.1514 StartZ=0 EndX=-25.5076 EndY=-27.3229 EndZ=0
    g13: ArcOfCircle CenterX=-24.0933 CenterY=-25.9087 CenterZ=0 NormalX=0 NormalY=0 NormalZ=1 AngleXU=-2.35619 Radius=2 StartAngle=0 EndAngle=1.5708
    g14: LineSegment StartX=-22.6791 StartY=-27.3229 StartZ=0 EndX=-15.3562 EndY=-20 EndZ=0
    g15: LineSegment StartX=15.3562 StartY=-20 StartZ=0 EndX=-15.3562 EndY=-20 EndZ=0
    g16: LineSegment StartX=22.6791 StartY=-27.3229 StartZ=0 EndX=15.3562 EndY=-20 EndZ=0
    g17: ArcOfCircle CenterX=24.0933 CenterY=-25.9087 CenterZ=0 NormalX=0 NormalY=0 NormalZ=1 AngleXU=-0.785398 Radius=2 StartAngle=4.71239 EndAngle=6.28319
    g18: LineSegment StartX=25.5076 StartY=-27.3229 StartZ=0 EndX=35.6791 EndY=-17.1514 EndZ=0
    g19: ArcOfCircle CenterX=34.2649 CenterY=-15.7371 CenterZ=0 NormalX=0 NormalY=0 NormalZ=1 AngleXU=-0.785398 Radius=2 StartAngle=5.5e-14 EndAngle=1.5708
    g20: Circle CenterX=28.336 CenterY=-18.8377 CenterZ=0 NormalX=0 NormalY=0 NormalZ=1 AngleXU=-2.35619 Radius=1.7
    g21: Circle CenterX=-28.336 CenterY=-18.8377 CenterZ=0 NormalX=0 NormalY=0 NormalZ=1 AngleXU=-0.785398 Radius=1.7
    g22: LineSegment StartX=-29.1892 StartY=-7.83304 StartZ=0 EndX=-27.775 EndY=-9.24725 EndZ=0
    g23: LineSegment StartX=-16.1892 StartY=-20.833 StartZ=0 EndX=-17.6034 EndY=-19.4188 EndZ=0
    g24: LineSegment StartX=-14.1781 StartY=-20 StartZ=0 EndX=-14.1781 EndY=-18 EndZ=0
    g25: LineSegment StartX=-14.1781 StartY=0 StartZ=0 EndX=-14.1781 EndY=-2 EndZ=0
    g26: LineSegment StartX=14.1781 StartY=0 StartZ=0 EndX=14.1781 EndY=-2 EndZ=0
    g27: LineSegment StartX=14.1781 StartY=-20 StartZ=0 EndX=14.1781 EndY=-18 EndZ=0
    g28: LineSegment StartX=16.1892 StartY=-20.833 StartZ=0 EndX=17.6034 EndY=-19.4188 EndZ=0
    g29: LineSegment StartX=29.1892 StartY=-7.83304 StartZ=0 EndX=27.775 EndY=-9.24725 EndZ=0
  constraints (24):
    c: Coincident(g22,g-4)
    c: PointOnObject(g22,g-4)
    c: Coincident(g23,g-4)
    c: PointOnObject(g23,g-4)
    c: Coincident(g24,g-5)
    c: PointOnObject(g24,g-5)
    c: Coincident(g25,g-5)
    c: PointOnObject(g25,g-5)
    c: Coincident(g26,g-6)
    c: PointOnObject(g26,g-6)
    c: Coincident(g27,g-6)
    c: PointOnObject(g27,g-6)
    c: Coincident(g28,g-3)
    c: PointOnObject(g28,g-3)
    c: Coincident(g29,g-3)
    c: PointOnObject(g29,g-3)
    c: Equal(g22,g23)
    c: Equal(g23,g24)
    c: Equal(g24,g25)
    c: Equal(g25,g26)
    c: Equal(g26,g27)
    c: Equal(g27,g28)
    c: Equal(g28,g29)
    c: DistanceY(g24,g24) = 2
FEATURE [TechDraw::DrawViewPart] View006
  CoarseView = false
  Direction = (0,-0.707107,0.707107)
  Focus = 100
  HardHidden = false
  IsoCount = 0
  IsoHidden = false
  IsoVisible = false
  LockPosition = false
  Perspective = false
  Rotation = 0
  ScaleType = 0
  ScrubCount = 0
  SeamHidden = false
  SeamVisible = true
  SmoothHidden = false
  SmoothVisible = true
  Source = -> [Body028]
  X = 68.5
  XDirection = (1,0,0)
  Y = 105
FEATURE [TechDraw::DrawViewPart] View007
  CoarseView = false
  Direction = (0.57735,0.57735,0.57735)
  Focus = 100
  HardHidden = false
  IsoCount = 0
  IsoHidden = false
  IsoVisible = false
  LockPosition = false
  Perspective = false
  Rotation = 0
  ScaleType = 0
  ScrubCount = 0
  SeamHidden = false
  SeamVisible = true
  SmoothHidden = false
  SmoothVisible = true
  Source = -> [Body028]
  X = 238.5
  XDirection = (-0.707107,0.707107,0)
  Y = 105
FEATURE [TechDraw::DrawViewPart] View008
  CoarseView = false
  Direction = (0,1,0)
  Focus = 100
  HardHidden = false
  IsoCount = 0
  IsoHidden = false
  IsoVisible = false
  LockPosition = false
  Perspective = false
  Rotation = 0
  ScaleType = 0
  ScrubCount = 0
  SeamHidden = false
  SeamVisible = true
  SmoothHidden = false
  SmoothVisible = true
  Source = -> [Body028]
  X = 148.5
  XDirection = (-1,0,0)
  Y = 105
FEATURE [TechDraw::DrawPage] Page003
  KeepUpdated = true
  NextBalloonIndex = 1
  ProjectionType = 0
  Template = -> Template
  Views = -> [View006,View007,View008]
FEATURE [App::DocumentObjectGroup] Group007  label="water_sensor_holder"
  Group = -> [Page003,Unfold004,Unfold_Sketch004,Unfold_Sketch_Outline001,Unfold_Sketch_Internal001,Unfold_Sketch_bends004]
FEATURE [Sketcher::SketchObject] Sketch106
  AttachmentOffset = pos=(0,0,0) rot=(0,1,0;1.5708rad)
  AttachmentSupport = -> [Sketch036]
  FullyConstrained = true
  MapMode = 7
  Placement = pos=(83.2492,-85,0) rot=(0.889126,0.323616,0.323616;1.68804rad)
  sketch-geometry (5):
    g0: LineSegment StartX=0 StartY=0 StartZ=0 EndX=6 EndY=0 EndZ=0
    g1: LineSegment StartX=6 StartY=0 StartZ=0 EndX=6 EndY=0.4 EndZ=0
    g2: LineSegment StartX=6 StartY=0.4 StartZ=0 EndX=65.111 EndY=50 EndZ=0
    g3: LineSegment StartX=65.111 StartY=50 StartZ=0 EndX=0 EndY=50 EndZ=0
    g4: LineSegment StartX=0 StartY=50 StartZ=0 EndX=0 EndY=0 EndZ=0
  constraints (14):
    c: Coincident(g-1,g0)
    c: PointOnObject(g0,g-1)
    c: Coincident(g0,g1)
    c: Vertical(g1)
    c: Coincident(g1,g2)
    c: Coincident(g2,g3)
    c: PointOnObject(g3,g-2)
    c: Horizontal(g3)
    c: Coincident(g3,g4)
    c: Coincident(g4,g0)
    c: DistanceY(g1) = 0.4
    c: Angle(g2) = 0.698132
    c: DistanceX(g0) = 6
    c: DistanceY(g3) = 50
FEATURE [Part::Extrusion] Extrude024
  Base = -> Sketch106
  Dir = (0.642788,-0.766044,1e-16)
  DirMode = 2
  FaceMakerClass = Part::FaceMakerBullseye
  LengthFwd = 0.4
  LengthRev = 0
  Reversed = true
  Solid = true
  Symmetric = false
FEATURE [Part::Mirroring] Part__Mirroring024  label="Extrude024 (Mirror #23)"
  Base = (0,0,0)
  Normal = (1,0,0)
  Source = -> Extrude024
FEATURE [Part::Compound] Compound035
  Links = -> [Extrude024,Part__Mirroring024]
FEATURE [PartDesign::Boolean] Boolean037
  BaseFeature = -> Mirrored
  Group = -> [Compound035]
  Suppressed = false
  Type = 1
  UsePlacement = true
FEATURE [PartDesign::Boolean] Boolean032
  BaseFeature = -> Boolean037
  Group = -> [Compound028]
  Refine = true
  Suppressed = false
  Type = 0
  UsePlacement = true
FEATURE [Sketcher::SketchObject] Sketch107
  AttachmentOffset = pos=(0,0,0) rot=(0,1,0;1.5708rad)
  AttachmentSupport = -> [Sketch008]
  ExternalGeometry = -> [Sketch008]
  FullyConstrained = true
  MapMode = 7
  Placement = pos=(83.1036,-84.6,0) rot=(0.889126,0.323616,0.323616;1.68804rad)
  sketch-geometry (2):
    g0: Circle CenterX=35 CenterY=15 CenterZ=0 NormalX=0 NormalY=0 NormalZ=1 AngleXU=0 Radius=1.7
    g1: Circle CenterX=288.843 CenterY=15 CenterZ=0 NormalX=0 NormalY=0 NormalZ=1 AngleXU=0 Radius=1.7
  constraints (6):
    c: Equal(g0,g1)
    c: Diameter(g0) = 3.4
    c: Horizontal(g0,g1)
    c: DistanceX(g0) = 35
    c: DistanceY(g0) = 15
    c: DistanceX(g1,g-3) = 12
FEATURE [Part::Extrusion] Extrude025
  Base = -> Sketch107
  Dir = (0.642788,-0.766044,-2e-16)
  DirMode = 2
  FaceMakerClass = Part::FaceMakerBullseye
  LengthFwd = 10
  LengthRev = 0
  Solid = true
  Symmetric = false
FEATURE [Part::Mirroring] Part__Mirroring025  label="Extrude025 (Mirror #24)"
  Base = (0,0,0)
  Normal = (1,0,0)
  Source = -> Extrude025
FEATURE [Part::Compound] Compound003
  Links = -> [Populate003,Extrude019,Populate042,Extrude025,Part__Mirroring025]
FEATURE [PartDesign::Boolean] Boolean002
  BaseFeature = -> Boolean032
  Group = -> [Compound003]
  Suppressed = false
  Type = 1
  UsePlacement = true
FEATURE [PartDesign::Body] Body006  label="dropper_fix_composit"
  Group = -> [Binder008,BaseBend003,Extend001,Bend001,Sketch022,Cylinder004,Pocket,Pocket001,Pocket005,Mirrored,Boolean037,Boolean032,Sketch023,Sketch036,Local_CS013,Local_CS014,Boolean002]
  Origin = -> Origin006
  Tip = -> Boolean037
FEATURE [Part::Mirroring] Part__Mirroring026  label="Extrude020 (Mirror #25)"
  Base = (0,0,0)
  Normal = (1,0,0)
  Source = -> Extrude020
FEATURE [Part::Compound] Compound023
  Links = -> [Populate029,Extrude020,Extrude009,Part__Mirroring026]
FEATURE [Part::Cut] Cut001
  Base = -> Extrude008
  Placement = pos=(0,0,813.1) rot=(0,0,1;0rad)
  Tool = -> Compound023
  expr: .Placement.Base.z = <<BaseBend>>.length + <<BaseBend>>.radius
FEATURE [Part::Compound] Compound010
  Links = -> [Cut001]
FEATURE [PartDesign::Boolean] Boolean007
  BaseFeature = -> Bend
  Group = -> [Compound010]
  Refine = true
  Suppressed = false
  Type = 0
  UsePlacement = true
FEATURE [Sketcher::SketchObject] Unfold_Sketch001  label="lamp_holder_Sketch001"
  FullyConstrained = false
  sketch-geometry (31):
    g0: LineSegment StartX=320.518 StartY=0 StartZ=0 EndX=414.521 EndY=0 EndZ=0
    g1: ArcOfCircle CenterX=320.518 CenterY=-5 CenterZ=0 NormalX=0 NormalY=0 NormalZ=1 AngleXU=-3.14159 Radius=5 StartAngle=4.71239 EndAngle=6.28319
    g2: LineSegment StartX=315.518 StartY=-5 StartZ=0 EndX=315.518 EndY=-535 EndZ=0
    g3: ArcOfCircle CenterX=320.518 CenterY=-535 CenterZ=0 NormalX=0 NormalY=0 NormalZ=1 AngleXU=-3.14159 Radius=5 StartAngle=2.958e-13 EndAngle=1.5708
    g4: LineSegment StartX=320.518 StartY=-540 StartZ=0 EndX=414.521 EndY=-540 EndZ=0
    g5: ArcOfCircle CenterX=414.521 CenterY=-535 CenterZ=0 NormalX=0 NormalY=0 NormalZ=1 AngleXU=0 Radius=5 StartAngle=4.71239 EndAngle=6.28319
    g6: LineSegment StartX=419.521 StartY=-5 StartZ=0 EndX=419.521 EndY=-535 EndZ=0
    g7: ArcOfCircle CenterX=414.521 CenterY=-5 CenterZ=0 NormalX=0 NormalY=0 NormalZ=1 AngleXU=0 Radius=5 StartAngle=2.967e-13 EndAngle=1.5708
    g8: Circle CenterX=321.218 CenterY=-10 CenterZ=0 NormalX=0 NormalY=0 NormalZ=1 AngleXU=-1.5708 Radius=4
    g9: Circle CenterX=321.218 CenterY=-530 CenterZ=0 NormalX=0 NormalY=0 NormalZ=1 AngleXU=-1.5708 Radius=4
    g10: LineSegment StartX=390.649 StartY=-7.8 StartZ=0 EndX=390.649 EndY=-6.2 EndZ=0
    g11: ArcOfCircle CenterX=392.349 CenterY=-6.2 CenterZ=0 NormalX=0 NormalY=0 NormalZ=1 AngleXU=-3.14159 Radius=1.7 StartAngle=3.14159 EndAngle=6.28319
    g12: LineSegment StartX=394.049 StartY=-7.8 StartZ=0 EndX=394.049 EndY=-6.2 EndZ=0
    g13: ArcOfCircle CenterX=392.349 CenterY=-7.8 CenterZ=0 NormalX=0 NormalY=0 NormalZ=1 AngleXU=-3.14159 Radius=1.7 StartAngle=2.913e-13 EndAngle=3.14159
    g14: LineSegment StartX=398.549 StartY=-7.8 StartZ=0 EndX=398.549 EndY=-6.2 EndZ=0
    g15: ArcOfCircle CenterX=400.249 CenterY=-6.2 CenterZ=0 NormalX=0 NormalY=0 NormalZ=1 AngleXU=0 Radius=1.7 StartAngle=2.949e-13 EndAngle=3.14159
    g16: LineSegment StartX=401.949 StartY=-7.8 StartZ=0 EndX=401.949 EndY=-6.2 EndZ=0
    g17: ArcOfCircle CenterX=400.249 CenterY=-7.8 CenterZ=0 NormalX=0 NormalY=0 NormalZ=1 AngleXU=0 Radius=1.7 StartAngle=3.14159 EndAngle=6.28319
    g18: LineSegment StartX=398.549 StartY=-533.8 StartZ=0 EndX=398.549 EndY=-532.2 EndZ=0
    g19: ArcOfCircle CenterX=400.249 CenterY=-532.2 CenterZ=0 NormalX=0 NormalY=0 NormalZ=1 AngleXU=-3.14159 Radius=1.7 StartAngle=3.14159 EndAngle=6.28319
    g20: LineSegment StartX=401.949 StartY=-533.8 StartZ=0 EndX=401.949 EndY=-532.2 EndZ=0
    g21: ArcOfCircle CenterX=400.249 CenterY=-533.8 CenterZ=0 NormalX=0 NormalY=0 NormalZ=1 AngleXU=-3.14159 Radius=1.7 StartAngle=0 EndAngle=3.14159
    g22: LineSegment StartX=390.649 StartY=-533.8 StartZ=0 EndX=390.649 EndY=-532.2 EndZ=0
    g23: ArcOfCircle CenterX=392.349 CenterY=-532.2 CenterZ=0 NormalX=0 NormalY=0 NormalZ=1 AngleXU=0 Radius=1.7 StartAngle=0 EndAngle=3.14159
    g24: LineSegment StartX=394.049 StartY=-533.8 StartZ=0 EndX=394.049 EndY=-532.2 EndZ=0
    g25: ArcOfCircle CenterX=392.349 CenterY=-533.8 CenterZ=0 NormalX=0 NormalY=0 NormalZ=1 AngleXU=0 Radius=1.7 StartAngle=3.14159 EndAngle=6.28319
    g26: Circle CenterX=328.218 CenterY=-525 CenterZ=0 NormalX=0 NormalY=0 NormalZ=1 AngleXU=-1.5708 Radius=1.7
    g27: Circle CenterX=328.218 CenterY=-15 CenterZ=0 NormalX=0 NormalY=0 NormalZ=1 AngleXU=-1.5708 Radius=1.7
    g28: Circle CenterX=320.218 CenterY=-397.5 CenterZ=0 NormalX=0 NormalY=0 NormalZ=1 AngleXU=-1.5708 Radius=1.7
    g29: Circle CenterX=320.218 CenterY=-142.5 CenterZ=0 NormalX=0 NormalY=0 NormalZ=1 AngleXU=-1.5708 Radius=1.7
    g30: Circle CenterX=328.218 CenterY=-270 CenterZ=0 NormalX=0 NormalY=0 NormalZ=1 AngleXU=-1.5708 Radius=1.7
FEATURE [Part::Mirroring] Part__Mirroring022  label="lamp_holder_Sketch (Mirror #21)"
  Base = (0,0,0)
  Normal = (1,0,0)
  Source = -> Unfold_Sketch001
FEATURE [App::Link] Link001  label="Body002composit_electric_shield_fix"
  LinkedObject = -> <external ../composit_electric_shield.FCStd>#Body002
  expr: LinkedObject = composit_electric_shield#<<composit_electric_shield_fix>>._self
FEATURE [Part::FeaturePython] Populate014  label="Populate electric_shield_placement with Body007"  # WARN: FeaturePython — macro-defined, semantics opaque (R4)
  Copying = 0
  ExposePlacement = false
  MarkerShape = 1
  MarkerSize = 0
  NumElements = 0
  Object = -> Link001
  OutputCompounding = 2
  PlacementsTo = -> Placment012
  Referencing = 0
  Type = lattice2PopulateCopies.LatticePopulateCopies
  isLattice = 0
FEATURE [Part::Compound] Compound029
  Links = -> [Populate014]
FEATURE [App::Link] Link002  label="Extrude026"
  LinkedObject = -> <external ../composit_electric_shield.FCStd>#Extrude002
  expr: LinkedObject = composit_electric_shield#<<electric_shield_cut>>._self
FEATURE [Part::FeaturePython] Populate013  label="Populate electric_shield_placement with Extrude007"  # WARN: FeaturePython — macro-defined, semantics opaque (R4)
  Copying = 0
  ExposePlacement = false
  MarkerShape = 1
  MarkerSize = 0
  NumElements = 0
  Object = -> Link002
  OutputCompounding = 2
  PlacementsTo = -> Placment012
  Referencing = 0
  Type = lattice2PopulateCopies.LatticePopulateCopies
  isLattice = 0
FEATURE [Part::Compound] Compound007
  Links = -> [Populate013,Populate023,Populate024,Populate043]
FEATURE [Sketcher::SketchObject] Sketch108
  AttachmentOffset = pos=(-161,0,0) rot=(0,0.707107,0.707107;3.14159rad)
  AttachmentSupport = -> [Binder011]
  FullyConstrained = true
  MapMode = 7
  Placement = pos=(-161,90,31) rot=(0,0.382683,0.92388;3.14159rad)
  expr: .AttachmentOffset.Base.x = -<<pump_holder_BaseBend>>.length / 2
  sketch-geometry (13):
    g0: LineSegment StartX=0 StartY=115 StartZ=0 EndX=0 EndY=1 EndZ=0
    g1: ArcOfCircle CenterX=0.911395 CenterY=90 CenterZ=0 NormalX=0 NormalY=0 NormalZ=1 AngleXU=0 Radius=20 StartAngle=6.15659 EndAngle=7.18856
    g2: GeomPoint X=24 Y=113 Z=0
    g3: LineSegment StartX=10.2224 StartY=4.74749 StartZ=0 EndX=20.7514 EndY=87.4749 EndZ=0
    g4: ArcOfCircle CenterX=8.23841 CenterY=5 CenterZ=0 NormalX=0 NormalY=0 NormalZ=1 AngleXU=0 Radius=2 StartAngle=4.71239 EndAngle=6.15659
    g5: LineSegment StartX=8.23841 StartY=3 StartZ=0 EndX=2 EndY=3 EndZ=0
    g6: GeomPoint X=10 Y=3 Z=0
    g7: ArcOfCircle CenterX=2 CenterY=1 CenterZ=0 NormalX=0 NormalY=0 NormalZ=1 AngleXU=0 Radius=2 StartAngle=1.5708 EndAngle=3.14159
    g8: ArcOfCircle CenterX=2 CenterY=115 CenterZ=0 NormalX=0 NormalY=0 NormalZ=1 AngleXU=0 Radius=2 StartAngle=3.14159 EndAngle=4.71239
    g9: LineSegment StartX=3.30889 StartY=113 StartZ=0 EndX=2 EndY=113 EndZ=0
    g10: LineSegment StartX=13.2592 StartY=105.733 StartZ=0 EndX=4.54367 EndY=112.573 EndZ=0
    g11: ArcOfCircle CenterX=3.30889 CenterY=111 CenterZ=0 NormalX=0 NormalY=0 NormalZ=1 AngleXU=0 Radius=2 StartAngle=0.905377 EndAngle=1.5708
    g12: GeomPoint X=4 Y=113 Z=0
  constraints (31):
    c: PointOnObject(g0,g-2)
    c: DistanceX(g2) = 24
    c: DistanceY(g2) = 113
    c: DistanceY(g0) = 1
    c: PointOnObject(g2,g3)
    c: Horizontal(g5)
    c: Tangent(g5,g4) = 1.5708
    c: Tangent(g4,g3) = -1.5708
    c: PointOnObject(g6,g5)
    c: PointOnObject(g6,g3)
    c: Tangent(g7,g0) = -1.5708
    c: Tangent(g7,g5) = -1.5708
    c: Equal(g7,g4)
    c: Radius(g7) = 2
    c: Tangent(g3,g1) = -1.5708
    c: DistanceX(g6) = 10
    c: Tangent(g8,g0) = -1.5708
    c: PointOnObject(g0,g-2)
    c: Radius(g8) = 2
    c: Horizontal(g9)
    c: PointOnObject(g2,g9)
    c: PointOnObject(g12,g9)
    c: PointOnObject(g12,g10)
    c: Tangent(g9,g11) = -1.5708
    c: Tangent(g10,g11) = -1.5708
    c: Equal(g11,g8)
    c: Tangent(g10,g1) = -1.5708
    c: Radius(g1) = 20
    c: DistanceX(g12) = 4
    c: DistanceY(g1) = 90
    c: Tangent(g8,g9) = 1.5708
FEATURE [PartDesign::Pad] Pad024
  BaseFeature = -> MultiTransform001
  Direction = (1e-16,0.707107,0.707107)
  Length = 0.7
  Length2 = 10
  Profile = -> Sketch108
  ReferenceAxis = -> Sketch108 [N_Axis]
  Suppressed = false
  Type = 0
  expr: Length = <<pump_holder_BaseBend>>.thickness
FEATURE [Part::Mirroring] Part__Mirroring027  label="Sketch108 (Mirror #26)"
  Base = (0,0,0)
  Normal = (1,0,0)
  Source = -> Sketch108
FEATURE [PartDesign::SubShapeBinder] Binder033
  BindCopyOnChange = 0
  BindMode = 0
  ClaimChildren = true
  Context = -> <external composit_stand10_model.FCStd>#Assembly [pump_holder.Binder033.]
  Fuse = false
  MakeFace = true
  OffsetFill = false
  OffsetIntersection = false
  OffsetJoinType = 0
  OffsetOpenResult = false
  PartialLoad = false
  Relative = false
  Support = -> [Part__Mirroring027]
  _Version = 2
FEATURE [PartDesign::Pad] Pad025
  BaseFeature = -> Pad024
  Direction = (3e-16,0.707107,0.707107)
  Length = 0.7
  Length2 = 10
  Profile = -> Binder033 [Face1]
  Refine = true
  Suppressed = false
  Type = 0
  expr: Length = <<Pad024>>.Length
FEATURE [TechDraw::DrawViewBalloon] Balloon003
  BubbleShape = 3
  EndType = 0
  EndTypeScale = 1
  KinkLength = 5
  LockPosition = false
  OriginX = 5.52207
  OriginY = 8.81174
  Rotation = 0
  ScaleType = 0
  ShapeScale = 1
  SourceView = -> View002
  Text = Лицевая сторона
  TextWrapLen = -1
  X = 52.8891
  Y = 44.6185
FEATURE [TechDraw::DrawViewBalloon] Balloon004
  BubbleShape = 3
  EndType = 0
  EndTypeScale = 1
  KinkLength = 5
  LockPosition = false
  OriginX = 5.50743
  OriginY = 7.57419
  Rotation = 0
  ScaleType = 0
  ShapeScale = 1
  SourceView = -> View002
  Text = Оборотная сторона
  TextWrapLen = -1
  X = -38.4826
  Y = -13.3118
FEATURE [TechDraw::DrawViewPart] View010
  CoarseView = false
  Direction = (0,1,0)
  Focus = 100
  HardHidden = false
  IsoCount = 0
  IsoHidden = false
  IsoVisible = false
  LockPosition = false
  Perspective = false
  Rotation = 0
  Scale = 0.4
  ScaleType = 2
  ScrubCount = 0
  SeamHidden = false
  SeamVisible = true
  SmoothHidden = false
  SmoothVisible = true
  Source = -> [Body012]
  X = 148.5
  XDirection = (-1,0,0)
  Y = 25
FEATURE [TechDraw::DrawViewPart] View012
  CoarseView = false
  Direction = (-0.762326,0.639667,0.09841)
  Focus = 100
  HardHidden = false
  IsoCount = 0
  IsoHidden = false
  IsoVisible = false
  LockPosition = false
  Perspective = false
  Rotation = 0
  Scale = 0.5
  ScaleType = 2
  ScrubCount = 0
  SeamHidden = false
  SeamVisible = true
  SmoothHidden = false
  SmoothVisible = true
  Source = -> [Body012]
  X = 188.5
  XDirection = (-0.642787,-0.766045,1.20347e-07)
  Y = 173
FEATURE [TechDraw::DrawViewPart] View013
  CoarseView = false
  Direction = (-1,0,0)
  Focus = 100
  HardHidden = false
  IsoCount = 0
  IsoHidden = false
  IsoVisible = false
  LockPosition = false
  Perspective = false
  Rotation = 0
  ScaleType = 0
  ScrubCount = 0
  SeamHidden = false
  SeamVisible = true
  SmoothHidden = false
  SmoothVisible = true
  Source = -> [Body012]
  X = 78.5
  XDirection = (0,-1,0)
  Y = 105
FEATURE [Part::Feature] Unfold
  shape: bbox 720.7 x 0.5564 x 223 mm, 84 faces (baked)
FEATURE [Sketcher::SketchObject] Unfold_Sketch_Outline003
  FullyConstrained = false
  sketch-geometry (34):
    g0: LineSegment StartX=-140.957 StartY=-317.576 StartZ=0 EndX=-131.579 EndY=-317.576 EndZ=0
    g1: LineSegment StartX=-128.685 StartY=-320.034 StartZ=0 EndX=-131.579 EndY=-317.576 EndZ=0
    g2: LineSegment StartX=-90.3069 StartY=-359.745 StartZ=0 EndX=-128.685 EndY=-320.034 EndZ=0
    g3: ArcOfCircle CenterX=-88.8687 CenterY=-358.355 CenterZ=0 NormalX=0 NormalY=0 NormalZ=1 AngleXU=0.76833 Radius=2 StartAngle=3.14159 EndAngle=4.71239
    g4: LineSegment StartX=54.0624 StartY=-223.003 StartZ=0 EndX=-87.4789 EndY=-359.793 EndZ=0
    g5: ArcOfCircle CenterX=52.6725 CenterY=-221.565 CenterZ=0 NormalX=0 NormalY=0 NormalZ=1 AngleXU=0.76833 Radius=2 StartAngle=4.71239 EndAngle=6.28319
    g6: LineSegment StartX=4.05254 StartY=-168.378 StartZ=0 EndX=54.1107 EndY=-220.175 EndZ=0
    g7: ArcOfCircle CenterX=0.975152 CenterY=-164.437 CenterZ=0 NormalX=0 NormalY=0 NormalZ=1 AngleXU=1.5708 Radius=5 StartAngle=2.81845 EndAngle=3.80458
    g8: BSplineCurve PolesCount=15 KnotsCount=13 Degree=3 IsPeriodic=0
    g9: ArcOfCircle CenterX=0.975152 CenterY=-164.437 CenterZ=0 NormalX=0 NormalY=0 NormalZ=1 AngleXU=1.5708 Radius=5 StartAngle=0.398217 EndAngle=2.03948
    g10: BSplineCurve PolesCount=15 KnotsCount=13 Degree=3 IsPeriodic=0
    g11: BSplineCurve PolesCount=15 KnotsCount=13 Degree=3 IsPeriodic=0
    g12: ArcOfCircle CenterX=0.975152 CenterY=-164.437 CenterZ=0 NormalX=0 NormalY=0 NormalZ=1 AngleXU=1.5708 Radius=5 StartAngle=4.85528 EndAngle=5.88497
    g13: LineSegment StartX=5.92419 StartY=-163.725 StartZ=0 EndX=78 EndY=-163.725 EndZ=0
    g14: ArcOfCircle CenterX=78 CenterY=-161.725 CenterZ=0 NormalX=0 NormalY=0 NormalZ=1 AngleXU=1.5708 Radius=2 StartAngle=3.14159 EndAngle=4.71239
    g15: LineSegment StartX=80 StartY=-161.725 StartZ=0 EndX=80 EndY=161.725 EndZ=0
    g16: ArcOfCircle CenterX=78 CenterY=161.725 CenterZ=0 NormalX=0 NormalY=0 NormalZ=1 AngleXU=1.5708 Radius=2 StartAngle=4.71239 EndAngle=6.28319
    g17: LineSegment StartX=78 StartY=163.725 StartZ=0 EndX=5.88592 EndY=163.725 EndZ=0
    g18: ArcOfCircle CenterX=0.934762 CenterY=164.422 CenterZ=0 NormalX=0 NormalY=0 NormalZ=1 AngleXU=1.5708 Radius=5 StartAngle=3.54859 EndAngle=4.57249
    g19: BSplineCurve PolesCount=15 KnotsCount=13 Degree=3 IsPeriodic=0
    g20: ArcOfCircle CenterX=0.934762 CenterY=164.422 CenterZ=0 NormalX=0 NormalY=0 NormalZ=1 AngleXU=1.5708 Radius=5 StartAngle=1.09337 EndAngle=2.75212
    g21: BSplineCurve PolesCount=15 KnotsCount=13 Degree=3 IsPeriodic=0
    g22: ArcOfCircle CenterX=0.934762 CenterY=164.422 CenterZ=0 NormalX=0 NormalY=0 NormalZ=1 AngleXU=1.5708 Radius=5 StartAngle=0 EndAngle=0.314428
    g23: ArcOfCircle CenterX=0.934762 CenterY=164.422 CenterZ=0 NormalX=0 NormalY=0 NormalZ=1 AngleXU=1.5708 Radius=5 StartAngle=5.61643 EndAngle=6.28319
    g24: LineSegment StartX=4.02697 StartY=168.351 StartZ=0 EndX=54.1107 EndY=220.175 EndZ=0
    g25: ArcOfCircle CenterX=52.6725 CenterY=221.565 CenterZ=0 NormalX=0 NormalY=0 NormalZ=1 AngleXU=2.37326 Radius=2 StartAngle=3.14159 EndAngle=4.71239
    g26: LineSegment StartX=54.0624 StartY=223.003 StartZ=0 EndX=-87.4789 EndY=359.793 EndZ=0
    g27: ArcOfCircle CenterX=-88.8687 CenterY=358.355 CenterZ=0 NormalX=0 NormalY=0 NormalZ=1 AngleXU=2.37326 Radius=2 StartAngle=4.71239 EndAngle=6.28319
    g28: LineSegment StartX=-90.3069 StartY=359.745 StartZ=0 EndX=-128.685 EndY=320.034 EndZ=0
    g29: LineSegment StartX=-131.579 StartY=317.576 StartZ=0 EndX=-128.685 EndY=320.034 EndZ=0
    g30: LineSegment StartX=-140.957 StartY=317.576 StartZ=0 EndX=-131.579 EndY=317.576 EndZ=0
    g31: ArcOfCircle CenterX=-140.957 CenterY=315.576 CenterZ=0 NormalX=0 NormalY=0 NormalZ=1 AngleXU=1.5708 Radius=2 StartAngle=3.31735e-06 EndAngle=1.5708
    g32: LineSegment StartX=-142.957 StartY=-315.576 StartZ=0 EndX=-142.957 EndY=315.576 EndZ=0
    g33: ArcOfCircle CenterX=-140.957 CenterY=-315.576 CenterZ=0 NormalX=0 NormalY=0 NormalZ=1 AngleXU=-1.5708 Radius=2 StartAngle=4.71239 EndAngle=6.28318
FEATURE [Sketcher::SketchObject] Unfold_Sketch_Internal003
  FullyConstrained = false
  sketch-geometry (49):
    g0: ArcOfCircle CenterX=-0.0496964 CenterY=140 CenterZ=0 NormalX=0 NormalY=0 NormalZ=1 AngleXU=1.5708 Radius=3 StartAngle=0.309598 EndAngle=1.5708
    g1: LineSegment StartX=-3.0497 StartY=106 StartZ=0 EndX=-3.0497 EndY=140 EndZ=0
    g2: ArcOfCircle CenterX=-0.0496964 CenterY=106 CenterZ=0 NormalX=0 NormalY=0 NormalZ=1 AngleXU=1.5708 Radius=3 StartAngle=1.5708 EndAngle=2.83199
    g3: BSplineCurve PolesCount=15 KnotsCount=13 Degree=3 IsPeriodic=0
    g4: ArcOfCircle CenterX=-0.0496964 CenterY=106 CenterZ=0 NormalX=0 NormalY=0 NormalZ=1 AngleXU=1.5708 Radius=3 StartAngle=4.55672 EndAngle=4.71239
    g5: LineSegment StartX=2.9503 StartY=106 StartZ=0 EndX=2.9503 EndY=140 EndZ=0
    g6: ArcOfCircle CenterX=-0.0496964 CenterY=140 CenterZ=0 NormalX=0 NormalY=0 NormalZ=1 AngleXU=1.5708 Radius=3 StartAngle=4.71239 EndAngle=4.86806
    g7: BSplineCurve PolesCount=15 KnotsCount=13 Degree=3 IsPeriodic=0
    g8: ArcOfCircle CenterX=-0.0496964 CenterY=-44.5 CenterZ=0 NormalX=0 NormalY=0 NormalZ=1 AngleXU=1.5708 Radius=3 StartAngle=0.309598 EndAngle=1.5708
    g9: LineSegment StartX=-3.0497 StartY=-78.5 StartZ=0 EndX=-3.0497 EndY=-44.5 EndZ=0
    g10: ArcOfCircle CenterX=-0.0496964 CenterY=-78.5 CenterZ=0 NormalX=0 NormalY=0 NormalZ=1 AngleXU=1.5708 Radius=3 StartAngle=1.5708 EndAngle=2.83199
    g11: BSplineCurve PolesCount=15 KnotsCount=13 Degree=3 IsPeriodic=0
    g12: ArcOfCircle CenterX=-0.0496964 CenterY=-78.5 CenterZ=0 NormalX=0 NormalY=0 NormalZ=1 AngleXU=1.5708 Radius=3 StartAngle=4.55672 EndAngle=4.71239
    g13: LineSegment StartX=2.9503 StartY=-78.5 StartZ=0 EndX=2.9503 EndY=-44.5 EndZ=0
    g14: ArcOfCircle CenterX=-0.0496964 CenterY=-44.5 CenterZ=0 NormalX=0 NormalY=0 NormalZ=1 AngleXU=1.5708 Radius=3 StartAngle=4.71239 EndAngle=4.86806
    g15: BSplineCurve PolesCount=15 KnotsCount=13 Degree=3 IsPeriodic=0
    g16: ArcOfCircle CenterX=-0.0496964 CenterY=78.5 CenterZ=0 NormalX=0 NormalY=0 NormalZ=1 AngleXU=1.5708 Radius=3 StartAngle=0.309598 EndAngle=1.5708
    g17: LineSegment StartX=-3.0497 StartY=44.5 StartZ=0 EndX=-3.0497 EndY=78.5 EndZ=0
    g18: ArcOfCircle CenterX=-0.0496964 CenterY=44.5 CenterZ=0 NormalX=0 NormalY=0 NormalZ=1 AngleXU=1.5708 Radius=3 StartAngle=1.5708 EndAngle=2.83199
    g19: BSplineCurve PolesCount=15 KnotsCount=13 Degree=3 IsPeriodic=0
    g20: ArcOfCircle CenterX=-0.0496964 CenterY=44.5 CenterZ=0 NormalX=0 NormalY=0 NormalZ=1 AngleXU=1.5708 Radius=3 StartAngle=4.55672 EndAngle=4.71239
    g21: LineSegment StartX=2.9503 StartY=44.5 StartZ=0 EndX=2.9503 EndY=78.5 EndZ=0
    g22: ArcOfCircle CenterX=-0.0496964 CenterY=78.5 CenterZ=0 NormalX=0 NormalY=0 NormalZ=1 AngleXU=1.5708 Radius=3 StartAngle=4.71239 EndAngle=4.86806
    g23: BSplineCurve PolesCount=15 KnotsCount=13 Degree=3 IsPeriodic=0
    g24: ArcOfCircle CenterX=-0.0496964 CenterY=-106 CenterZ=0 NormalX=0 NormalY=0 NormalZ=1 AngleXU=1.5708 Radius=3 StartAngle=0.309598 EndAngle=1.5708
    g25: LineSegment StartX=-3.0497 StartY=-140 StartZ=0 EndX=-3.0497 EndY=-106 EndZ=0
    g26: ArcOfCircle CenterX=-0.0496964 CenterY=-140 CenterZ=0 NormalX=0 NormalY=0 NormalZ=1 AngleXU=1.5708 Radius=3 StartAngle=1.5708 EndAngle=2.83199
    g27: BSplineCurve PolesCount=15 KnotsCount=13 Degree=3 IsPeriodic=0
    g28: ArcOfCircle CenterX=-0.0496964 CenterY=-140 CenterZ=0 NormalX=0 NormalY=0 NormalZ=1 AngleXU=1.5708 Radius=3 StartAngle=4.55672 EndAngle=4.71239
    g29: LineSegment StartX=2.9503 StartY=-140 StartZ=0 EndX=2.9503 EndY=-106 EndZ=0
    g30: ArcOfCircle CenterX=-0.0496964 CenterY=-106 CenterZ=0 NormalX=0 NormalY=0 NormalZ=1 AngleXU=1.5708 Radius=3 StartAngle=4.71239 EndAngle=4.86806
    g31: BSplineCurve PolesCount=15 KnotsCount=13 Degree=3 IsPeriodic=0
    g32: ArcOfCircle CenterX=-0.0496964 CenterY=17 CenterZ=0 NormalX=0 NormalY=0 NormalZ=1 AngleXU=1.5708 Radius=3 StartAngle=0.309598 EndAngle=1.5708
    g33: LineSegment StartX=-3.0497 StartY=-17 StartZ=0 EndX=-3.0497 EndY=17 EndZ=0
    g34: ArcOfCircle CenterX=-0.0496964 CenterY=-17 CenterZ=0 NormalX=0 NormalY=0 NormalZ=1 AngleXU=1.5708 Radius=3 StartAngle=1.5708 EndAngle=2.83199
    g35: BSplineCurve PolesCount=15 KnotsCount=13 Degree=3 IsPeriodic=0
    g36: ArcOfCircle CenterX=-0.0496964 CenterY=-17 CenterZ=0 NormalX=0 NormalY=0 NormalZ=1 AngleXU=1.5708 Radius=3 StartAngle=4.55672 EndAngle=4.71239
    g37: LineSegment StartX=2.9503 StartY=-17 StartZ=0 EndX=2.9503 EndY=17 EndZ=0
    g38: ArcOfCircle CenterX=-0.0496964 CenterY=17 CenterZ=0 NormalX=0 NormalY=0 NormalZ=1 AngleXU=1.5708 Radius=3 StartAngle=4.71239 EndAngle=4.86806
    g39: BSplineCurve PolesCount=15 KnotsCount=13 Degree=3 IsPeriodic=0
    g40: Circle CenterX=47.0406 CenterY=-220.054 CenterZ=0 NormalX=0 NormalY=0 NormalZ=-1 AngleXU=-0.76833 Radius=1.7
    g41: Circle CenterX=47.0406 CenterY=220.054 CenterZ=0 NormalX=0 NormalY=0 NormalZ=-1 AngleXU=0.76833 Radius=1.7
    g42: Circle CenterX=-86.5908 CenterY=-349.2 CenterZ=0 NormalX=0 NormalY=0 NormalZ=-1 AngleXU=-0.76833 Radius=1.7
    g43: Circle CenterX=-86.5908 CenterY=349.2 CenterZ=0 NormalX=0 NormalY=0 NormalZ=-1 AngleXU=0.76833 Radius=1.7
    g44: Circle CenterX=73 CenterY=0 CenterZ=0 NormalX=0 NormalY=0 NormalZ=-1 AngleXU=1.5708 Radius=1.7
    g45: Circle CenterX=73 CenterY=158.725 CenterZ=0 NormalX=0 NormalY=0 NormalZ=-1 AngleXU=1.5708 Radius=1.7
    g46: Circle CenterX=73 CenterY=-158.725 CenterZ=0 NormalX=0 NormalY=0 NormalZ=-1 AngleXU=-1.5708 Radius=1.7
    g47: Circle CenterX=21 CenterY=158.725 CenterZ=0 NormalX=0 NormalY=0 NormalZ=-1 AngleXU=1.5708 Radius=1.7
    g48: Circle CenterX=21 CenterY=-158.725 CenterZ=0 NormalX=0 NormalY=0 NormalZ=-1 AngleXU=-1.5708 Radius=1.7
FEATURE [Sketcher::SketchObject] Unfold_Sketch_bends  label="Unfold_Sketch_bends005"
  FullyConstrained = false
  sketch-geometry (9):
    g0: LineSegment StartX=-130.132 StartY=318.805 StartZ=0 EndX=-2.3012 EndY=168.234 EndZ=0
    g1: LineSegment StartX=0.975152 StartY=159.422 StartZ=0 EndX=0.975152 EndY=142.82 EndZ=0
    g2: LineSegment StartX=0.975152 StartY=103.18 StartZ=0 EndX=0.975152 EndY=81.3195 EndZ=0
    g3: LineSegment StartX=0.975152 StartY=41.6805 StartZ=0 EndX=0.975152 EndY=19.8195 EndZ=0
    g4: LineSegment StartX=0.975152 StartY=-19.8195 StartZ=0 EndX=0.975152 EndY=-41.6805 EndZ=0
    g5: LineSegment StartX=0.975152 StartY=-81.3195 StartZ=0 EndX=0.975152 EndY=-103.18 EndZ=0
    g6: LineSegment StartX=-130.132 StartY=-318.805 StartZ=0 EndX=-2.2915 EndY=-168.222 EndZ=0
    g7: LineSegment StartX=-133.518 StartY=317.576 StartZ=0 EndX=-133.518 EndY=-317.576 EndZ=0
    g8: LineSegment StartX=0.975152 StartY=-142.82 StartZ=0 EndX=0.975152 EndY=-159.437 EndZ=0
FEATURE [Sketcher::SketchObject] Unfold_Sketch  label="Unfold_Sketch005"
  ExternalGeometry = -> [Unfold_Sketch_bends]
  FullyConstrained = false
  sketch-geometry (61):
    g0: LineSegment StartX=-140.957 StartY=-317.576 StartZ=0 EndX=-131.579 EndY=-317.576 EndZ=0
    g1: LineSegment StartX=-128.685 StartY=-320.034 StartZ=0 EndX=-131.579 EndY=-317.576 EndZ=0
    g2: LineSegment StartX=-90.3069 StartY=-359.745 StartZ=0 EndX=-128.685 EndY=-320.034 EndZ=0
    g3: ArcOfCircle CenterX=-88.8687 CenterY=-358.355 CenterZ=0 NormalX=0 NormalY=0 NormalZ=1 AngleXU=0.76833 Radius=2 StartAngle=3.14159 EndAngle=4.71239
    g4: LineSegment StartX=54.0624 StartY=-223.003 StartZ=0 EndX=-87.4789 EndY=-359.793 EndZ=0
    g5: ArcOfCircle CenterX=52.6725 CenterY=-221.565 CenterZ=0 NormalX=0 NormalY=0 NormalZ=1 AngleXU=0.76833 Radius=2 StartAngle=4.71239 EndAngle=6.28319
    g6: LineSegment StartX=4.05254 StartY=-168.378 StartZ=0 EndX=54.1107 EndY=-220.175 EndZ=0
    g7: LineSegment StartX=5.92419 StartY=-163.725 StartZ=0 EndX=78 EndY=-163.725 EndZ=0
    g8: ArcOfCircle CenterX=78 CenterY=-161.725 CenterZ=0 NormalX=0 NormalY=0 NormalZ=1 AngleXU=1.5708 Radius=2 StartAngle=3.14159 EndAngle=4.71239
    g9: LineSegment StartX=80 StartY=-161.725 StartZ=0 EndX=80 EndY=161.725 EndZ=0
    g10: ArcOfCircle CenterX=78 CenterY=161.725 CenterZ=0 NormalX=0 NormalY=0 NormalZ=1 AngleXU=1.5708 Radius=2 StartAngle=4.71239 EndAngle=6.28319
    g11: LineSegment StartX=78 StartY=163.725 StartZ=0 EndX=5.88592 EndY=163.725 EndZ=0
    g12: LineSegment StartX=4.02697 StartY=168.351 StartZ=0 EndX=54.1107 EndY=220.175 EndZ=0
    g13: ArcOfCircle CenterX=52.6725 CenterY=221.565 CenterZ=0 NormalX=0 NormalY=0 NormalZ=1 AngleXU=2.37326 Radius=2 StartAngle=3.14159 EndAngle=4.71239
    g14: LineSegment StartX=54.0624 StartY=223.003 StartZ=0 EndX=-87.4789 EndY=359.793 EndZ=0
    g15: ArcOfCircle CenterX=-88.8687 CenterY=358.355 CenterZ=0 NormalX=0 NormalY=0 NormalZ=1 AngleXU=2.37326 Radius=2 StartAngle=4.71239 EndAngle=6.28319
    g16: LineSegment StartX=-90.3069 StartY=359.745 StartZ=0 EndX=-128.685 EndY=320.034 EndZ=0
    g17: LineSegment StartX=-131.579 StartY=317.576 StartZ=0 EndX=-128.685 EndY=320.034 EndZ=0
    g18: LineSegment StartX=-140.957 StartY=317.576 StartZ=0 EndX=-131.579 EndY=317.576 EndZ=0
    g19: ArcOfCircle CenterX=-140.957 CenterY=315.576 CenterZ=0 NormalX=0 NormalY=0 NormalZ=1 AngleXU=1.5708 Radius=2 StartAngle=3.31735e-06 EndAngle=1.5708
    g20: LineSegment StartX=-142.957 StartY=-315.576 StartZ=0 EndX=-142.957 EndY=315.576 EndZ=0
    g21: ArcOfCircle CenterX=-140.957 CenterY=-315.576 CenterZ=0 NormalX=0 NormalY=0 NormalZ=1 AngleXU=-1.5708 Radius=2 StartAngle=4.71239 EndAngle=6.28318
    g22: LineSegment StartX=2.9503 StartY=-78.5 StartZ=0 EndX=2.9503 EndY=-44.5 EndZ=0
    g23: LineSegment StartX=-3.0497 StartY=-78.5 StartZ=0 EndX=-3.0497 EndY=-44.5 EndZ=0
    g24: LineSegment StartX=2.9503 StartY=44.5 StartZ=0 EndX=2.9503 EndY=78.5 EndZ=0
    g25: LineSegment StartX=-3.0497 StartY=44.5 StartZ=0 EndX=-3.0497 EndY=78.5 EndZ=0
    g26: LineSegment StartX=2.9503 StartY=-140 StartZ=0 EndX=2.9503 EndY=-106 EndZ=0
    g27: LineSegment StartX=-3.0497 StartY=-140 StartZ=0 EndX=-3.0497 EndY=-106 EndZ=0
    g28: LineSegment StartX=2.9503 StartY=106 StartZ=0 EndX=2.9503 EndY=140 EndZ=0
    g29: LineSegment StartX=-3.0497 StartY=106 StartZ=0 EndX=-3.0497 EndY=140 EndZ=0
    g30: LineSegment StartX=2.9503 StartY=-17 StartZ=0 EndX=2.9503 EndY=17 EndZ=0
    g31: LineSegment StartX=-3.0497 StartY=-17 StartZ=0 EndX=-3.0497 EndY=17 EndZ=0
    g32: Circle CenterX=73 CenterY=0 CenterZ=0 NormalX=0 NormalY=0 NormalZ=-1 AngleXU=1.5708 Radius=1.7
    g33: Circle CenterX=47.0406 CenterY=220.054 CenterZ=0 NormalX=0 NormalY=0 NormalZ=-1 AngleXU=0.76833 Radius=1.7
    g34: Circle CenterX=-86.5908 CenterY=349.2 CenterZ=0 NormalX=0 NormalY=0 NormalZ=-1 AngleXU=0.76833 Radius=1.7
    g35: Circle CenterX=73 CenterY=-158.725 CenterZ=0 NormalX=0 NormalY=0 NormalZ=-1 AngleXU=-1.5708 Radius=1.7
    g36: Circle CenterX=73 CenterY=158.725 CenterZ=0 NormalX=0 NormalY=0 NormalZ=-1 AngleXU=1.5708 Radius=1.7
    g37: Circle CenterX=47.0406 CenterY=-220.054 CenterZ=0 NormalX=0 NormalY=0 NormalZ=-1 AngleXU=-0.76833 Radius=1.7
    g38: Circle CenterX=-86.5908 CenterY=-349.2 CenterZ=0 NormalX=0 NormalY=0 NormalZ=-1 AngleXU=-0.76833 Radius=1.7
    g39: Circle CenterX=21 CenterY=-158.725 CenterZ=0 NormalX=0 NormalY=0 NormalZ=-1 AngleXU=-1.5708 Radius=1.7
    g40: Circle CenterX=21 CenterY=158.725 CenterZ=0 NormalX=0 NormalY=0 NormalZ=-1 AngleXU=1.5708 Radius=1.7
    g41: ArcOfCircle CenterX=0.975152 CenterY=-164.437 CenterZ=0 NormalX=0 NormalY=0 NormalZ=1 AngleXU=0 Radius=5 StartAngle=0.142892 EndAngle=5.37538
    g42: ArcOfCircle CenterX=0.934762 CenterY=164.422 CenterZ=0 NormalX=0 NormalY=0 NormalZ=1 AngleXU=0 Radius=5 StartAngle=0.904038 EndAngle=6.14329
    g43: ArcOfCircle CenterX=-0.0496964 CenterY=-44.5 CenterZ=0 NormalX=0 NormalY=0 NormalZ=1 AngleXU=0 Radius=3 StartAngle=9e-16 EndAngle=3.14159
    g44: ArcOfCircle CenterX=-0.0496964 CenterY=-78.5 CenterZ=0 NormalX=0 NormalY=0 NormalZ=1 AngleXU=0 Radius=3 StartAngle=3.14159 EndAngle=6.28319
    g45: ArcOfCircle CenterX=-0.0496964 CenterY=-106 CenterZ=0 NormalX=0 NormalY=0 NormalZ=1 AngleXU=0 Radius=3 StartAngle=-1.8e-15 EndAngle=3.14159
    g46: ArcOfCircle CenterX=-0.0496964 CenterY=-140 CenterZ=0 NormalX=0 NormalY=0 NormalZ=1 AngleXU=0 Radius=3 StartAngle=3.14159 EndAngle=6.28319
    g47: ArcOfCircle CenterX=-0.0496964 CenterY=-17 CenterZ=0 NormalX=0 NormalY=0 NormalZ=1 AngleXU=0 Radius=3 StartAngle=3.14159 EndAngle=6.28319
    g48: ArcOfCircle CenterX=-0.0496964 CenterY=17 CenterZ=0 NormalX=0 NormalY=0 NormalZ=1 AngleXU=0 Radius=3 StartAngle=-9e-16 EndAngle=3.14159
    g49: ArcOfCircle CenterX=-0.0496964 CenterY=44.5 CenterZ=0 NormalX=0 NormalY=0 NormalZ=1 AngleXU=0 Radius=3 StartAngle=3.14159 EndAngle=6.28319
    g50: ArcOfCircle CenterX=-0.0496964 CenterY=78.5 CenterZ=0 NormalX=0 NormalY=0 NormalZ=1 AngleXU=0 Radius=3 StartAngle=9e-16 EndAngle=3.14159
    g51: ArcOfCircle CenterX=-0.0496964 CenterY=106 CenterZ=0 NormalX=0 NormalY=0 NormalZ=1 AngleXU=0 Radius=3 StartAngle=3.14159 EndAngle=6.28319
    g52: ArcOfCircle CenterX=-0.0496964 CenterY=140 CenterZ=0 NormalX=0 NormalY=0 NormalZ=1 AngleXU=0 Radius=3 StartAngle=-3.6e-15 EndAngle=3.14159
    g53: LineSegment StartX=-130.132 StartY=318.805 StartZ=0 EndX=-128.838 EndY=317.28 EndZ=0
    g54: LineSegment StartX=-133.518 StartY=317.576 StartZ=0 EndX=-133.518 EndY=315.576 EndZ=0
    g55: LineSegment StartX=-2.3012 StartY=168.234 StartZ=0 EndX=-3.59559 EndY=169.759 EndZ=0
    g56: LineSegment StartX=0.975152 StartY=159.422 StartZ=0 EndX=0.975152 EndY=157.422 EndZ=0
    g57: LineSegment StartX=0.975152 StartY=-159.437 StartZ=0 EndX=0.975152 EndY=-157.437 EndZ=0
    g58: LineSegment StartX=-2.2915 StartY=-168.222 StartZ=0 EndX=-3.58589 EndY=-169.747 EndZ=0
    g59: LineSegment StartX=-130.132 StartY=-318.805 StartZ=0 EndX=-128.838 EndY=-317.28 EndZ=0
    g60: LineSegment StartX=-133.518 StartY=-317.576 StartZ=0 EndX=-133.518 EndY=-315.576 EndZ=0
  constraints (84):
    c: Block(g6)
    c: Block(g7)
    c: Block(g11)
    c: Block(g12)
    c: Coincident(g41,g7)
    c: Coincident(g41,g6)
    c: Coincident(g42,g12)
    c: Coincident(g42,g11)
    c: Equal(g42,g41)
    c: Diameter(g41) = 10
    c: Block(g28)
    c: Block(g29)
    c: Block(g24)
    c: Block(g25)
    c: Block(g30)
    c: Block(g31)
    c: Block(g22)
    c: Block(g23)
    c: Block(g26)
    c: Block(g27)
    c: Coincident(g43,g23)
    c: Tangent(g43,g22) = -1.5708
    c: Coincident(g44,g22)
    c: Coincident(g45,g26)
    c: Coincident(g46,g26)
    c: Coincident(g47,g30)
    c: Coincident(g48,g30)
    c: Coincident(g49,g24)
    c: Coincident(g50,g24)
    c: Coincident(g51,g28)
    c: Tangent(g51,g29) = 1.5708
    c: Coincident(g52,g28)
    c: Tangent(g52,g29) = 1.5708
    c: Tangent(g50,g25) = 1.5708
    c: Tangent(g49,g25) = 1.5708
    c: Tangent(g48,g31) = 1.5708
    c: Tangent(g47,g31) = 1.5708
    c: Tangent(g44,g23) = 1.5708
    c: Tangent(g45,g27) = 1.5708
    c: Tangent(g46,g27) = 1.5708
    c: Coincident(g53,g-6)
    c: PointOnObject(g53,g-6)
    c: Coincident(g54,g-5)
    c: PointOnObject(g54,g-5)
    c: Coincident(g55,g-6)
    c: PointOnObject(g55,g-6)
    c: Coincident(g56,g-7)
    c: PointOnObject(g56,g-7)
    c: Coincident(g57,g-3)
    c: PointOnObject(g57,g-3)
    c: Coincident(g58,g-4)
    c: PointOnObject(g58,g-4)
    c: Coincident(g59,g-4)
    c: PointOnObject(g59,g-4)
    c: Coincident(g60,g-5)
    c: PointOnObject(g60,g-5)
    c: Equal(g60,g59)
    c: Equal(g59,g58)
    c: Equal(g58,g57)
    c: Equal(g57,g56)
    c: Equal(g56,g55)
    c: Equal(g55,g54)
    c: Equal(g54,g53)
    c: Distance(g54) = 2
    c: Coincident(g20,g21)
    c: Coincident(g19,g20)
    c: Coincident(g0,g21)
    c: Coincident(g18,g19)
    c: Coincident(g0,g1)
    c: Coincident(g17,g18)
    c: Coincident(g1,g2)
    c: Coincident(g16,g17)
    c: Coincident(g2,g3)
    c: Coincident(g15,g16)
    c: Coincident(g3,g4)
    c: Coincident(g14,g15)
    c: Coincident(g4,g5)
    c: Coincident(g13,g14)
    c: Coincident(g5,g6)
    c: Coincident(g12,g13)
    c: Coincident(g7,g8)
    c: Coincident(g10,g11)
    c: Coincident(g8,g9)
    c: Coincident(g9,g10)
FEATURE [Sketcher::SketchObject] Sketch109
  AttachmentOffset = pos=(316.563,0,-15) rot=(0,0,1;0rad)
  AttachmentSupport = -> [XZ_Plane026]
  FullyConstrained = true
  MapMode = 5
  Placement = pos=(316.563,15,-3.3e-15) rot=(1,0,0;1.5708rad)
  expr: .AttachmentOffset.Base.x = <<Sketch110>>.Constraints.back_width / 2 + 3 mm
  sketch-geometry (6):
    g0: ArcOfCircle CenterX=-3 CenterY=3 CenterZ=0 NormalX=0 NormalY=0 NormalZ=1 AngleXU=0 Radius=3 StartAngle=4.71239 EndAngle=6.28319
    g1: ArcOfCircle CenterX=-3 CenterY=3 CenterZ=0 NormalX=0 NormalY=0 NormalZ=1 AngleXU=0 Radius=1 StartAngle=4.71239 EndAngle=6.28319
    g2: LineSegment StartX=-3 StartY=0 StartZ=0 EndX=-3 EndY=2 EndZ=0
    g3: LineSegment StartX=-2 StartY=3 StartZ=0 EndX=-2 EndY=15 EndZ=0
    g4: LineSegment StartX=-2 StartY=15 StartZ=0 EndX=0 EndY=15 EndZ=0
    g5: LineSegment StartX=0 StartY=15 StartZ=0 EndX=0 EndY=3 EndZ=0
  constraints (16):
    c: PointOnObject(g0,g-2)
    c: Coincident(g1,g0)
    c: Coincident(g2,g0)
    c: Coincident(g2,g1)
    c: Tangent(g1,g3) = -1.5708
    c: Coincident(g3,g4)
    c: PointOnObject(g4,g-2)
    c: Horizontal(g4)
    c: Coincident(g4,g5)
    c: Tangent(g0,g-1) = -1.5708
    c: Tangent(g5,g0) = 1.5708
    c: Perpendicular(g0,g2)
    c: Parallel(g3,g5)
    c: DistanceY(g2,g2) = 2
    c: Radius(g1) = 1
    c: DistanceY(g4) = 15
FEATURE [Sketcher::SketchObject] Sketch110
  AttachmentSupport = -> [XY_Plane026]
  ExternalGeometry = -> [Binder031]
  FullyConstrained = true
  MapMode = 5
  sketch-geometry (12):
    g0: LineSegment StartX=-319.563 StartY=226 StartZ=0 EndX=319.563 EndY=226 EndZ=0
    g1: LineSegment StartX=319.563 StartY=226 StartZ=0 EndX=319.563 EndY=220 EndZ=0
    g2: LineSegment StartX=319.563 StartY=220 StartZ=0 EndX=316.563 EndY=220 EndZ=0
    g3: LineSegment StartX=316.563 StartY=220 StartZ=0 EndX=316.563 EndY=200 EndZ=0
    g4: LineSegment StartX=316.563 StartY=200 StartZ=0 EndX=313.563 EndY=200 EndZ=0
    g5: LineSegment StartX=313.563 StartY=200 StartZ=0 EndX=313.563 EndY=6 EndZ=0
    g6: LineSegment StartX=313.563 StartY=6 StartZ=0 EndX=-313.563 EndY=6 EndZ=0
    g7: LineSegment StartX=-313.563 StartY=6 StartZ=0 EndX=-313.563 EndY=200 EndZ=0
    g8: LineSegment StartX=-313.563 StartY=200 StartZ=0 EndX=-316.563 EndY=200 EndZ=0
    g9: LineSegment StartX=-316.563 StartY=200 StartZ=0 EndX=-316.563 EndY=220 EndZ=0
    g10: LineSegment StartX=-316.563 StartY=220 StartZ=0 EndX=-319.563 EndY=220 EndZ=0
    g11: LineSegment StartX=-319.563 StartY=220 StartZ=0 EndX=-319.563 EndY=226 EndZ=0
  constraints (31):
    c: Coincident(g0,g-3)
    c: Horizontal(g0)
    c: Coincident(g0,g1)
    c: Coincident(g1,g-3)
    c: Coincident(g1,g2)
    c: Coincident(g2,g-4)
    c: Coincident(g2,g3)
    c: PointOnObject(g3,g-4)
    c: Coincident(g3,g4)
    c: Horizontal(g4)
    c: Coincident(g4,g5)
    c: Vertical(g5)
    c: Coincident(g5,g6)
    c: Coincident(g6,g7)
    c: Coincident(g7,g8)
    c: Horizontal(g8)
    c: Coincident(g8,g9)
    c: Vertical(g9)
    c: Coincident(g9,g10)
    c: Horizontal(g10)
    c: Coincident(g10,g11)
    c: Coincident(g11,g0)
    c: Vertical(g11)
    c: Symmetric(g10,g1,g-2)
    c: Symmetric(g7,g4,g-2)
    c: Symmetric(g5,g6,g-2)
    c: DistanceX(g-4,g5) = -3
    c: DistanceY(g-4,g5) = 3
    c: DistanceY(g3,g3) = 20
    c: Equal(g2,g10)
    c: DistanceX(g6,g6) = 627.126  'back_width'
FEATURE [PartDesign::FeaturePython] BaseBend024  # WARN: FeaturePython — macro-defined, semantics opaque (R4)
  BendSide = 0
  BendSketch = -> Sketch110
  MidPlane = false
  Reverse = false
  Suppressed = false
  length = 100
  radius = 1
  thickness = 2
FEATURE [PartDesign::Pad] Pad026
  BaseFeature = -> BaseBend024
  Direction = (0,-1,2e-16)
  Length = 181
  Length2 = 10
  Profile = -> Sketch109
  ReferenceAxis = -> Sketch109 [N_Axis]
  Reversed = true
  Suppressed = false
  Type = 0
FEATURE [Part::Mirroring] Part__Mirroring028  label="Sketch109 (Mirror #27)"
  Base = (0,0,0)
  Normal = (1,0,0)
  Source = -> Sketch109
FEATURE [PartDesign::SubShapeBinder] Binder034
  BindCopyOnChange = 0
  BindMode = 0
  ClaimChildren = true
  Context = -> Body025 [Binder034.]
  Fuse = false
  MakeFace = true
  OffsetFill = false
  OffsetIntersection = false
  OffsetJoinType = 0
  OffsetOpenResult = false
  PartialLoad = false
  Relative = false
  Support = -> [Part__Mirroring028]
  _Version = 2
FEATURE [PartDesign::Pad] Pad027
  BaseFeature = -> Pad026
  Direction = (0,1,-3e-16)
  Length = 181
  Length2 = 10
  Profile = -> Binder034
  Suppressed = false
  Type = 0
  expr: Length = <<Pad026>>.Length
FEATURE [PartDesign::SubShapeBinder] Binder035
  BindCopyOnChange = 0
  BindMode = 0
  ClaimChildren = false
  Context = -> Body025 [Binder035.]
  Fuse = false
  MakeFace = true
  OffsetFill = false
  OffsetIntersection = false
  OffsetJoinType = 0
  OffsetOpenResult = false
  PartialLoad = false
  Placement = pos=(0,3,0) rot=(0.57735,-0.57735,-0.57735;2.0944rad)
  Relative = false
  Support = -> [Pad026[Sketch109.]]
  _Version = 2
FEATURE [PartDesign::Pad] Pad028
  BaseFeature = -> Pad027
  Direction = (-1,4e-16,-2e-16)
  Length = 621.126
  Length2 = 10
  Midplane = true
  Profile = -> Binder035
  Suppressed = false
  Type = 0
  expr: Length = <<Sketch110>>.Constraints.back_width - 6 mm
FEATURE [Part::Compound] Compound036
  Links = -> [Populate025,Populate024]
FEATURE [PartDesign::Boolean] Boolean038
  BaseFeature = -> Pad028
  Group = -> [Compound036]
  Suppressed = false
  Type = 1
  UsePlacement = true
FEATURE [PartDesign::Body] Body025
  Group = -> [Binder031,Sketch109,Sketch110,BaseBend024,Pad026,Binder034,Pad027,Binder035,Pad028,Boolean038]
  Origin = -> Origin026
  Tip = -> Boolean038
FEATURE [Path::FeaturePython] Engrave003  # Path/CAM operation (typed FeaturePython)
  Active = true
  ClearanceHeight = 6.7
  CoolantMode = 0
  CycleTime = Cycletime Error
  FinalDepth = -0.1
  OpFinalDepth = -3.3
  OpStartDepth = 0.7
  OpStockZMax = 1.7
  OpStockZMin = -2.8e-14
  OpToolDiameter = 3.175
  SafeHeight = 4.7
  StartDepth = 3
  StartVertex = 0
  StepDown = 4
  ToolController = -> __175mm_Endmill
  expr: ClearanceHeight = OpStockZMax + SetupSheet.ClearanceHeightOffset
  expr: FinalDepth = -0.1 mm
  expr: SafeHeight = OpStockZMax + SetupSheet.SafeHeightOffset
  expr: StartDepth = 3 mm
  expr: StepDown = 4 mm
FEATURE [Path::FeaturePython] Engrave004  # Path/CAM operation (typed FeaturePython)
  Active = true
  ClearanceHeight = 6.7
  CoolantMode = 0
  CycleTime = Cycletime Error
  FinalDepth = -0.1
  OpFinalDepth = -3.3
  OpStartDepth = 0.7
  OpStockZMax = 1.7
  OpStockZMin = -2.8e-14
  OpToolDiameter = 3.175
  SafeHeight = 4.7
  StartDepth = 3
  StartVertex = 0
  StepDown = 4
  ToolController = -> __175mm_Endmill
  expr: ClearanceHeight = OpStockZMax + SetupSheet.ClearanceHeightOffset
  expr: FinalDepth = -0.1 mm
  expr: SafeHeight = OpStockZMax + SetupSheet.SafeHeightOffset
  expr: StartDepth = 3 mm
  expr: StepDown = 4 mm
FEATURE [Part::Cylinder] Cylinder005  label="Cylinder"
  Angle = 360
  AttacherType = Attacher::AttachEngine3D
  FirstAngle = 0
  Height = 10
  Placement = pos=(319.563,60,60) rot=(0,-1,0;1.5708rad)
  Radius = 6.5
  SecondAngle = 0
  expr: .Placement.Base.x = <<Dimensions_sketch>>.Constraints.total_width / 2
FEATURE [Part::Compound] Compound001
  Links = -> [Populate001,Extrude010,Part__Mirroring007,Populate015,Populate021,Populate023,Populate025,Fusion,Populate038,Mirror006,Populate013,Cylinder005]
FEATURE [PartDesign::Boolean] Boolean
  BaseFeature = -> Boolean007
  Group = -> [Compound001]
  Suppressed = false
  Type = 1
  UsePlacement = true
FEATURE [PartDesign::Boolean] Boolean033
  BaseFeature = -> Boolean
  Group = -> [Compound029]
  Refine = true
  Suppressed = false
  Type = 0
  UsePlacement = true
FEATURE [PartDesign::CoordinateSystem] Local_CS036  label="face_electric_shield"
  AttacherType = Attacher::AttachEngine3D
  AttachmentOffset = pos=(319.563,80,555.5) rot=(0.57735,0.57735,0.57735;2.0944rad)
  AttachmentSupport = -> [XY_Plane]
  MapMode = 5
  Placement = pos=(319.563,80,555.5) rot=(0.57735,0.57735,0.57735;2.0944rad)
  expr: AttachmentOffset = <<electric_shield_placement>>.Placement
FEATURE [PartDesign::Body] Body  label="face"
  Group = -> [Binder,BaseBend,Extend,Bend,Boolean007,Local_CS005,Local_CS006,Local_CS007,Local_CS008,Local_CS009,Local_CS020,Local_CS027,Boolean,Boolean033,Local_CS036]
  Origin = -> Origin
  Tip = -> Boolean033
FEATURE [PartDesign::SubShapeBinder] Binder036
  BindCopyOnChange = 0
  BindMode = 0
  ClaimChildren = false
  Fuse = false
  MakeFace = true
  OffsetFill = false
  OffsetIntersection = false
  OffsetJoinType = 0
  OffsetOpenResult = false
  PartialLoad = false
  Relative = true
  Support = -> [<external ../magnet_fix.FCStd>#Sketch006]
  _Version = 2
  expr: Support = <<magnet_fix>>#<<magnet_fix_reply_holes>>._self
FEATURE [Part::FeaturePython] Placment032  # WARN: FeaturePython — macro-defined, semantics opaque (R4)
  AttacherType = Attacher::AttachEngine3D
  ExposePlacement = true
  MarkerShape = 1
  MarkerSize = 20
  NumElements = 1
  Placement = pos=(292.98,0,30.65) rot=(0.57735,-0.57735,0.57735;2.0944rad)
  Type = lattice2AttachablePlacement.AttachablePlacement
  isLattice = 1
  expr: .Placement.Base.x = <<Sketch079>>.Constraints.distance_x - 6.8 mm
  expr: .Placement.Base.z = 41.3 mm / 2 + <<face_magnet_fix_placement>>.Placement.Base.z - 6 mm
FEATURE [Part::Extrusion] Extrude026  label="Extrude027"
  Base = -> Binder036
  Dir = (0,0,1)
  DirMode = 2
  FaceMakerClass = Part::FaceMakerBullseye
  LengthFwd = 10
  LengthRev = 0
  Solid = false
  Symmetric = false
FEATURE [Part::FeaturePython] Mirror010  label="Mirror010 of Placment032"  # WARN: FeaturePython — macro-defined, semantics opaque (R4)
  ExposePlacement = false
  FlipX = true
  FlipY = false
  FlipZ = false
  MarkerShape = 1
  MarkerSize = 10
  NumElements = 1
  Object = -> Placment032
  ObjectTraversal = 0
  Type = lattice2Mirror.LatticeMirror
  isLattice = 1
FEATURE [Part::FeaturePython] Join012  # WARN: FeaturePython — macro-defined, semantics opaque (R4)
  ExposePlacement = false
  Interleave = false
  Links = -> [Placment032,Mirror010]
  MarkerShape = 1
  MarkerSize = 0
  NumElements = 2
  Type = lattice2JoinArrays.JoinArrays
  isLattice = 1
FEATURE [Part::FeaturePython] Populate053  label="magnet_reply_fix_new"  # WARN: FeaturePython — macro-defined, semantics opaque (R4)
  Copying = 0
  ExposePlacement = false
  MarkerShape = 1
  MarkerSize = 0
  NumElements = 0
  Object = -> Extrude026
  OutputCompounding = 1
  PlacementsTo = -> Join012
  Referencing = 0
  Type = lattice2PopulateCopies.LatticePopulateCopies
  isLattice = 0
FEATURE [Sketcher::SketchObject] Sketch111
  AttachmentSupport = -> [YZ_Plane001]
  FullyConstrained = true
  MapMode = 5
  Placement = pos=(0,0,0) rot=(0.57735,0.57735,0.57735;2.0944rad)
  sketch-geometry (4):
    g0: LineSegment StartX=15 StartY=0 StartZ=0 EndX=15 EndY=5 EndZ=0
    g1: LineSegment StartX=15 StartY=5 StartZ=0 EndX=3 EndY=5 EndZ=0
    g2: LineSegment StartX=3 StartY=5 StartZ=0 EndX=3 EndY=0 EndZ=0
    g3: LineSegment StartX=3 StartY=0 StartZ=0 EndX=15 EndY=0 EndZ=0
  constraints (12):
    c: Coincident(g0,g1)
    c: Coincident(g1,g2)
    c: Coincident(g2,g3)
    c: Coincident(g3,g0)
    c: Vertical(g0)
    c: Vertical(g2)
    c: Horizontal(g1)
    c: Horizontal(g3)
    c: PointOnObject(g0,g-1)
    c: DistanceX(g0) = 15
    c: DistanceX(g1) = 3
    c: DistanceY(g1) = 5
FEATURE [PartDesign::Pocket] Pocket023
  BaseFeature = -> Pocket003
  Direction = (-1,0,0)
  Length = 5
  Length2 = 5
  Midplane = true
  Profile = -> Sketch111
  ReferenceAxis = -> Sketch111 [N_Axis]
  Suppressed = false
  Type = 1
FEATURE [PartDesign::Boolean] Boolean005
  BaseFeature = -> Pocket023
  Group = -> [Compound007]
  Suppressed = false
  Type = 1
  UsePlacement = true
FEATURE [PartDesign::Body] Body001  label="back"
  Group = -> [Binder001,BaseBend001,Sketch031,Extend004,Bend009,Pocket003,Sketch111,Pocket023,Boolean005,Local_CS010,Local_CS011]
  Origin = -> Origin001
  Tip = -> Boolean005
FEATURE [Sketcher::SketchObject] Sketch112
  FullyConstrained = true
  sketch-geometry (2):
    g0: Circle CenterX=14.3 CenterY=0 CenterZ=0 NormalX=0 NormalY=0 NormalZ=1 AngleXU=0 Radius=1.7
    g1: Circle CenterX=-14.3 CenterY=0 CenterZ=0 NormalX=0 NormalY=0 NormalZ=1 AngleXU=0 Radius=1.7
  constraints (5):
    c: PointOnObject(g0,g-1)
    c: Symmetric(g0,g1,g-2)
    c: Equal(g0,g1)
    c: Diameter(g0) = 3.4
    c: DistanceX(g0) = 14.3
FEATURE [Part::Extrusion] Extrude027  label="Extrude028"
  Base = -> Sketch112
  Dir = (0,0,1)
  DirMode = 2
  FaceMakerClass = Part::FaceMakerBullseye
  LengthFwd = 28.6
  LengthRev = 0
  Solid = true
  Symmetric = false
FEATURE [Part::FeaturePython] Populate054  label="Populate Join012 with Extrude028"  # WARN: FeaturePython — macro-defined, semantics opaque (R4)
  Copying = 0
  ExposePlacement = false
  MarkerShape = 1
  MarkerSize = 0
  NumElements = 0
  Object = -> Extrude027
  OutputCompounding = 1
  PlacementsTo = -> Join012
  Referencing = 0
  Type = lattice2PopulateCopies.LatticePopulateCopies
  isLattice = 0
FEATURE [Part::Compound] Compound027
  Links = -> [Populate040,Populate054]
FEATURE [PartDesign::Boolean] Boolean031
  BaseFeature = -> Pocket016
  Group = -> [Compound027]
  Suppressed = false
  Type = 1
  UsePlacement = false
FEATURE [PartDesign::Body] Body021  label="front_shield"
  Group = -> [Binder024,BaseBend016,Extend003,Sketch084,Sketch085,Pocket015,Pocket016,Boolean031,Local_CS029]
  Origin = -> Origin021
  Tip = -> Boolean031
FEATURE [Sketcher::SketchObject] Sketch113
  AttachmentOffset = pos=(0,0,0) rot=(0,0.382683,0.92388;3.14159rad)
  AttachmentSupport = -> [XY_Plane008]
  FullyConstrained = false
  MapMode = 5
  Placement = pos=(0,0,0) rot=(0,0.382683,0.92388;3.14159rad)
  sketch-geometry (8):
    g0: LineSegment StartX=-163.961 StartY=71.3002 StartZ=0 EndX=-120.17 EndY=71.3002 EndZ=0
    g1: LineSegment StartX=-120.17 StartY=71.3002 StartZ=0 EndX=-120.17 EndY=98.7884 EndZ=0
    g2: LineSegment StartX=-120.17 StartY=98.7884 StartZ=0 EndX=-163.961 EndY=98.7884 EndZ=0
    g3: LineSegment StartX=-163.961 StartY=98.7884 StartZ=0 EndX=-163.961 EndY=71.3002 EndZ=0
    g4: LineSegment StartX=120.17 StartY=71.3002 StartZ=0 EndX=203.199 EndY=71.3002 EndZ=0
    g5: LineSegment StartX=203.199 StartY=71.3002 StartZ=0 EndX=203.199 EndY=143.396 EndZ=0
    g6: LineSegment StartX=203.199 StartY=143.396 StartZ=0 EndX=120.17 EndY=143.396 EndZ=0
    g7: LineSegment StartX=120.17 StartY=143.396 StartZ=0 EndX=120.17 EndY=71.3002 EndZ=0
  constraints (19):
    c: Coincident(g0,g1)
    c: Coincident(g1,g2)
    c: Coincident(g2,g3)
    c: Coincident(g3,g0)
    c: Horizontal(g0)
    c: Horizontal(g2)
    c: Vertical(g1)
    c: Vertical(g3)
    c: DistanceX(g0) = -120.17
    c: DistanceY(g0) = 71.3002
    c: Coincident(g4,g5)
    c: Coincident(g5,g6)
    c: Coincident(g6,g7)
    c: Coincident(g7,g4)
    c: Horizontal(g4)
    c: Horizontal(g6)
    c: Vertical(g5)
    c: Vertical(g7)
    c: Symmetric(g4,g0,g-2)
FEATURE [PartDesign::Pocket] Pocket024
  BaseFeature = -> Pad025
  Direction = (0,-0.707107,-0.707107)
  Length = 5
  Length2 = 5
  Profile = -> Sketch113
  ReferenceAxis = -> Sketch113 [N_Axis]
  Reversed = true
  Suppressed = false
  Type = 1
FEATURE [PartDesign::Body] Body008  label="pump_holder"
  Group = -> [Binder011,BaseBend005,Sketch015,Sketch039,Sketch040,Boolean036,Pocket007,MultiTransform,LinearPattern,LinearPattern001,Sketch041,Boolean004,Sketch100,Local_CS032,Local_CS033,Sketch101,Pocket019,Sketch102,Pocket020,Sketch104,Pocket021,MultiTransform001,LinearPattern003,LinearPattern004,Sketch108,Pad024,Binder033,Pad025,Sketch113,Pocket024]
  Origin = -> Origin008
  Tip = -> Pocket024
FEATURE [App::DocumentObjectGroup] Group001  label="parts"
  Group = -> [Body,Body001,Body003,Body006,Body004,Body010,Body011,Body008,Body012,Body014,Body016,Body021,Body019,Part,Body028]
FEATURE [TechDraw::DrawViewPart] View001
  CoarseView = false
  Direction = (0.57735,0.57735,0.57735)
  Focus = 100
  HardHidden = false
  IsoCount = 0
  IsoHidden = false
  IsoVisible = false
  LockPosition = false
  Perspective = false
  Rotation = 0
  Scale = 0.5
  ScaleType = 1
  ScrubCount = 0
  SeamHidden = false
  SeamVisible = true
  SmoothHidden = false
  SmoothVisible = true
  Source = -> [Body008]
  X = 92.9876
  XDirection = (-0.707107,0.707107,0)
  Y = 130.924
FEATURE [TechDraw::DrawViewBalloon] Balloon002
  BubbleShape = 3
  EndType = 0
  EndTypeScale = 1
  KinkLength = 5
  LockPosition = false
  OriginX = 98.5409
  OriginY = 73.8204
  Rotation = 0
  ScaleType = 0
  ShapeScale = 1
  SourceView = -> View001
  Text = Лицевая сторона
  TextWrapLen = -1
  X = 200.363
  Y = 73.1574
FEATURE [TechDraw::DrawViewPart] View
  CoarseView = false
  Direction = (-1,0,0)
  Focus = 100
  HardHidden = false
  IsoCount = 0
  IsoHidden = false
  IsoVisible = false
  LockPosition = false
  Perspective = false
  Rotation = 0
  ScaleType = 0
  ScrubCount = 0
  SeamHidden = false
  SeamVisible = true
  SmoothHidden = false
  SmoothVisible = true
  Source = -> [Body008]
  X = 198.5
  XDirection = (0,-1,0)
  Y = 75
FEATURE [Part::Feature] Unfold007  label="pump_holder_Unfold"
  shape: bbox 363.8 x 255.6 x 0.7 mm, 90 faces (baked)
FEATURE [PartDesign::FeatureBase] BaseFeature
  BaseFeature = -> Unfold007
  Suppressed = false
  expr: BaseFeature = <<pump_holder_Unfold>>._self
  expr: Placement = .BaseFeature.Placement
FEATURE [PartDesign::Body] Body009  label="pump_holder_Body"
  Group = -> [BaseFeature]
  Origin = -> Origin009
  Tip = -> BaseFeature
FEATURE [Part::FeaturePython] Clone  label="Model-Body009"  # Draft clone (typed FeaturePython)
  AttacherType = Attacher::AttachEngine3D
  Fuse = false
  Objects = -> [Body009]
  PathResource = Model
  Placement = pos=(-205,-63.2536,-2.8e-14) rot=(0,0,1;3.14159rad)
  Scale = (1,1,1)
FEATURE [App::DocumentObjectGroup] Model
  Group = -> [Clone]
FEATURE [Part::FeaturePython] Stock  # WARN: FeaturePython — macro-defined, semantics opaque (R4)
  Base = -> Model
  ExtXneg = 1
  ExtXpos = 1
  ExtYneg = 1
  ExtYpos = 1
  ExtZneg = 0
  ExtZpos = 1
  Placement = pos=(-120,-234.71,-2.8e-14) rot=(0,0,1;0rad)
  StockType = FromBase
FEATURE [Path::FeaturePython] Profile  # Path/CAM operation (typed FeaturePython)
  Active = true
  AreaParams:
    Tolerance = 1e-07
    FitArcs = True
    Simplify = False
    CleanDistance = 0.0
    Accuracy = 0.01
    Unit = 1.0
    MinArcPoints = 4
    MaxArcPoints = 100
    ClipperScale = 10000000.0
    Fill = 0
    Coplanar = 0
    Reorient = True
    Outline = False
    Explode = False
    OpenMode = 0
    Deflection = 0.01
    SubjectFill = 0
    ClipFill = 0
    Offset = -1.5875
    ExtraPass = 0
    Stepover = 0.0
    LastStepover = 0.0
    JoinType = 0
    EndType = 0
    MiterLimit = 2.0
    RoundPrecision = 0.0
    PocketMode = 0
    ToolRadius = 1.0
    PocketExtraOffset = 0.0
    PocketStepover = 0.0
    PocketLastStepover = 0.0
    FromCenter = False
    Angle = 45.0
    AngleShift = 0.0
    Shift = 0.0
    Thicken = False
    SectionCount = -1
    Stepdown = 1.0
    SectionOffset = 0.0
    SectionTolerance = 1e-06
    SectionMode = 2
    Project = False
  Base = -> [Clone]
  ClearanceHeight = 6.7
  CoolantMode = 0
  CycleTime = 00:00:00
  Direction = 1
  FinalDepth = -0.1
  HandleMultipleFeatures = 0
  JoinType = 0
  MiterLimit = 0.1
  OffsetExtra = 0
  OpFinalDepth = -2.84e-14
  OpStartDepth = 1.7
  OpStockZMax = 1.7
  OpStockZMin = -2.8e-14
  OpToolDiameter = 3.175
  PathParams = {'orientation': 1, 'feedrate': 33.333333333333336, 'feedrate_v': 8.333333333333334, 'verbose': True, 'resume_height': 4.700000000000363, 'retraction': 6.700000000000363, 'return_end': True, 'preamble': False, 'start': Vector (-383.9996834315583, -149.85735293202495, 6.700000000000363)}
  SafeHeight = 4.7
  Side = 1
  SplitArcs = false
  StartDepth = 3
  StartPoint = (0,0,0)
  StepDown = 4
  ToolController = -> __175mm_Endmill
  UseComp = true
  UseStartPoint = false
  processCircles = true
  processHoles = true
  processPerimeter = false
  expr: ClearanceHeight = OpStockZMax + SetupSheet.ClearanceHeightOffset
  expr: FinalDepth = -0.1 mm
  expr: SafeHeight = OpStockZMax + SetupSheet.SafeHeightOffset
  expr: StartDepth = 3 mm
  expr: StepDown = 4 mm
FEATURE [Path::FeaturePython] Profile001  # Path/CAM operation (typed FeaturePython)
  Active = true
  AreaParams:
    Tolerance = 1e-07
    FitArcs = True
    Simplify = False
    CleanDistance = 0.0
    Accuracy = 0.01
    Unit = 1.0
    MinArcPoints = 4
    MaxArcPoints = 100
    ClipperScale = 10000000.0
    Fill = 0
    Coplanar = 0
    Reorient = True
    Outline = False
    Explode = False
    OpenMode = 0
    Deflection = 0.01
    SubjectFill = 0
    ClipFill = 0
    Offset = 1.5875
    ExtraPass = 0
    Stepover = 0.0
    LastStepover = 0.0
    JoinType = 0
    EndType = 0
    MiterLimit = 2.0
    RoundPrecision = 0.0
    PocketMode = 0
    ToolRadius = 1.0
    PocketExtraOffset = 0.0
    PocketStepover = 0.0
    PocketLastStepover = 0.0
    FromCenter = False
    Angle = 45.0
    AngleShift = 0.0
    Shift = 0.0
    Thicken = False
    SectionCount = -1
    Stepdown = 1.0
    SectionOffset = 0.0
    SectionTolerance = 1e-06
    SectionMode = 2
    Project = False
  Base = -> [Clone]
  ClearanceHeight = 6.7
  CoolantMode = 0
  CycleTime = 00:00:00
  Direction = 1
  FinalDepth = -0.1
  HandleMultipleFeatures = 0
  JoinType = 0
  MiterLimit = 0.1
  OffsetExtra = 0
  OpFinalDepth = -2.84e-14
  OpStartDepth = 1.7
  OpStockZMax = 1.7
  OpStockZMin = -2.8e-14
  OpToolDiameter = 3.175
  PathParams = {'orientation': 0, 'feedrate': 33.333333333333336, 'feedrate_v': 8.333333333333334, 'verbose': True, 'resume_height': 4.700000000000363, 'retraction': 6.700000000000363, 'return_end': True, 'preamble': False, 'start': Vector (0.0, -199.0, 0.0)}
  SafeHeight = 4.7
  Side = 1
  SplitArcs = false
  StartDepth = 3
  StartPoint = (0,-199,0)
  StepDown = 4
  ToolController = -> __175mm_Endmill
  UseComp = true
  UseStartPoint = true
  processCircles = false
  processHoles = false
  processPerimeter = true
  expr: Base = <<Profile>>.Base
  expr: ClearanceHeight = OpStockZMax + SetupSheet.ClearanceHeightOffset
  expr: FinalDepth = -0.1 mm
  expr: SafeHeight = OpStockZMax + SetupSheet.SafeHeightOffset
  expr: StartDepth = 3 mm
  expr: StepDown = 4 mm
FEATURE [App::DocumentObjectGroup] Operations
  Group = -> [Profile,Profile001,Engrave003,Engrave004]
FEATURE [Path::FeaturePython] Job  # Path/CAM operation (typed FeaturePython)
  CycleTime = 00:00:00
  Fixtures = G54
  GeometryTolerance = 0.01
  JobType = 0
  LastPostProcessDate = 2024-02-26 16:12:20.243774
  LastPostProcessOutput = <userpath>/2CAF-B51C/Job-0.tap \n<userpath>/2CAF-B51C/Job-1.tap
  Model = -> Model
  Operations = -> Operations
  OrderOutputBy = 2
  PostProcessor = 3
  PostProcessorOutputFile = %j.tap
  SetupSheet = -> SetupSheet
  SplitOutput = true
  Stock = -> Stock
  Tools = -> Tools
FEATURE [Sketcher::SketchObject] Unfold_Sketch007  label="pump_holder_Sketch"
  FullyConstrained = false
  sketch-geometry (88):
    g0: ArcOfCircle CenterX=52 CenterY=-102.569 CenterZ=0 NormalX=0 NormalY=0 NormalZ=1 AngleXU=-3.14159 Radius=2 StartAngle=0 EndAngle=1.5708
    g1: LineSegment StartX=52 StartY=-104.569 StartZ=0 EndX=118 EndY=-104.569 EndZ=0
    g2: ArcOfCircle CenterX=118 CenterY=-102.569 CenterZ=0 NormalX=0 NormalY=0 NormalZ=1 AngleXU=0 Radius=2 StartAngle=4.71239 EndAngle=6.28319
    g3: LineSegment StartX=120 StartY=-102.569 StartZ=0 EndX=120 EndY=-64.8772 EndZ=0
    g4: LineSegment StartX=120 StartY=-64.8772 StartZ=0 EndX=120.17 EndY=-64.8772 EndZ=0
    g5: LineSegment StartX=120.17 StartY=-64.8772 StartZ=0 EndX=120.17 EndY=-52.4997 EndZ=0
    g6: LineSegment StartX=120.17 StartY=-52.4997 StartZ=0 EndX=162.722 EndY=-52.4997 EndZ=0
    g7: ArcOfCircle CenterX=163 CenterY=-54.4802 CenterZ=0 NormalX=0 NormalY=0 NormalZ=1 AngleXU=1e-16 Radius=2 StartAngle=1.5708 EndAngle=1.71042
    g8: LineSegment StartX=164.309 StartY=-52.4802 StartZ=0 EndX=163 EndY=-52.4802 EndZ=0
    g9: ArcOfCircle CenterX=164.309 CenterY=-50.4802 CenterZ=0 NormalX=0 NormalY=0 NormalZ=1 AngleXU=1e-16 Radius=2 StartAngle=4.71239 EndAngle=5.37781
    g10: LineSegment StartX=174.259 StartY=-45.2134 StartZ=0 EndX=165.544 EndY=-52.0535 EndZ=0
    g11: ArcOfCircle CenterX=161.911 CenterY=-29.4802 CenterZ=0 NormalX=0 NormalY=0 NormalZ=1 AngleXU=1e-16 Radius=20 StartAngle=5.37781 EndAngle=6.40978
    g12: LineSegment StartX=171.222 StartY=55.7723 StartZ=0 EndX=181.751 EndY=-26.9551 EndZ=0
    g13: ArcOfCircle CenterX=169.238 CenterY=55.5198 CenterZ=0 NormalX=0 NormalY=0 NormalZ=1 AngleXU=1e-16 Radius=2 StartAngle=0.126592 EndAngle=1.5708
    g14: LineSegment StartX=169.238 StartY=57.5198 StartZ=0 EndX=163 EndY=57.5198 EndZ=0
    g15: ArcOfCircle CenterX=163 CenterY=59.5198 CenterZ=0 NormalX=0 NormalY=0 NormalZ=1 AngleXU=1e-16 Radius=2 StartAngle=3.14159 EndAngle=4.71239
    g16: LineSegment StartX=161 StartY=59.5198 StartZ=0 EndX=161 EndY=149 EndZ=0
    g17: ArcOfCircle CenterX=159 CenterY=149 CenterZ=0 NormalX=0 NormalY=0 NormalZ=1 AngleXU=1.5708 Radius=2 StartAngle=4.71239 EndAngle=6.28319
    g18: LineSegment StartX=-159 StartY=151 StartZ=0 EndX=159 EndY=151 EndZ=0
    g19: ArcOfCircle CenterX=-159 CenterY=149 CenterZ=0 NormalX=0 NormalY=0 NormalZ=1 AngleXU=1.5708 Radius=2 StartAngle=0 EndAngle=1.5708
    g20: LineSegment StartX=-161 StartY=59.5198 StartZ=0 EndX=-161 EndY=149 EndZ=0
    g21: ArcOfCircle CenterX=-163 CenterY=59.5198 CenterZ=0 NormalX=0 NormalY=0 NormalZ=1 AngleXU=3.14159 Radius=2 StartAngle=1.5708 EndAngle=3.14159
    g22: LineSegment StartX=-169.238 StartY=57.5198 StartZ=0 EndX=-163 EndY=57.5198 EndZ=0
    g23: ArcOfCircle CenterX=-169.238 CenterY=55.5198 CenterZ=0 NormalX=0 NormalY=0 NormalZ=1 AngleXU=3.14159 Radius=2 StartAngle=4.71239 EndAngle=6.15659
    g24: LineSegment StartX=-171.222 StartY=55.7723 StartZ=0 EndX=-181.751 EndY=-26.9551 EndZ=0
    g25: ArcOfCircle CenterX=-161.911 CenterY=-29.4802 CenterZ=0 NormalX=0 NormalY=0 NormalZ=1 AngleXU=3.14159 Radius=20 StartAngle=6.15659 EndAngle=7.18856
    g26: LineSegment StartX=-174.259 StartY=-45.2134 StartZ=0 EndX=-165.544 EndY=-52.0535 EndZ=0
    g27: ArcOfCircle CenterX=-164.309 CenterY=-50.4802 CenterZ=0 NormalX=0 NormalY=0 NormalZ=1 AngleXU=3.14159 Radius=2 StartAngle=0.905377 EndAngle=1.5708
    g28: LineSegment StartX=-164.309 StartY=-52.4802 StartZ=0 EndX=-163 EndY=-52.4802 EndZ=0
    g29: ArcOfCircle CenterX=-163 CenterY=-54.4802 CenterZ=0 NormalX=0 NormalY=0 NormalZ=1 AngleXU=3.14159 Radius=2 StartAngle=4.57277 EndAngle=4.71239
    g30: LineSegment StartX=-162.722 StartY=-52.4997 StartZ=0 EndX=-120.17 EndY=-52.4997 EndZ=0
    g31: LineSegment StartX=-120.17 StartY=-52.4997 StartZ=0 EndX=-120.17 EndY=-64.8772 EndZ=0
    g32: LineSegment StartX=-120.17 StartY=-64.8772 StartZ=0 EndX=-120 EndY=-64.8772 EndZ=0
    g33: LineSegment StartX=-120 StartY=-102.569 StartZ=0 EndX=-120 EndY=-64.8772 EndZ=0
    g34: ArcOfCircle CenterX=-118 CenterY=-102.569 CenterZ=0 NormalX=0 NormalY=0 NormalZ=1 AngleXU=-3.14159 Radius=2 StartAngle=0 EndAngle=1.5708
    g35: LineSegment StartX=-118 StartY=-104.569 StartZ=0 EndX=-52 EndY=-104.569 EndZ=0
    g36: ArcOfCircle CenterX=-52 CenterY=-102.569 CenterZ=0 NormalX=0 NormalY=0 NormalZ=1 AngleXU=0 Radius=2 StartAngle=4.71239 EndAngle=6.28319
    g37: LineSegment StartX=-50 StartY=-102.569 StartZ=0 EndX=-50 EndY=-64.8772 EndZ=0
    g38: LineSegment StartX=-50 StartY=-64.8772 StartZ=0 EndX=50 EndY=-64.8772 EndZ=0
    g39: LineSegment StartX=50 StartY=-102.569 StartZ=0 EndX=50 EndY=-64.8772 EndZ=0
    g40: LineSegment StartX=93.5 StartY=9.77968 StartZ=0 EndX=112.5 EndY=9.77968 EndZ=0
    g41: ArcOfCircle CenterX=93.5 CenterY=14.7797 CenterZ=0 NormalX=0 NormalY=0 NormalZ=1 AngleXU=0 Radius=5 StartAngle=3.14159 EndAngle=4.71239
    g42: LineSegment StartX=88.5 StartY=52.5198 StartZ=0 EndX=88.5 EndY=14.7797 EndZ=0
    g43: ArcOfCircle CenterX=93.5 CenterY=52.5198 CenterZ=0 NormalX=0 NormalY=0 NormalZ=1 AngleXU=0 Radius=5 StartAngle=1.5708 EndAngle=3.14159
    g44: LineSegment StartX=112.5 StartY=57.5198 StartZ=0 EndX=93.5 EndY=57.5198 EndZ=0
    g45: ArcOfCircle CenterX=112.5 CenterY=52.5198 CenterZ=0 NormalX=0 NormalY=0 NormalZ=1 AngleXU=0 Radius=5 StartAngle=0 EndAngle=1.5708
    g46: LineSegment StartX=117.5 StartY=14.7797 StartZ=0 EndX=117.5 EndY=52.5198 EndZ=0
    g47: ArcOfCircle CenterX=112.5 CenterY=14.7797 CenterZ=0 NormalX=0 NormalY=0 NormalZ=1 AngleXU=0 Radius=5 StartAngle=4.71239 EndAngle=6.28319
    g48: ArcOfCircle CenterX=70 CenterY=-90.8772 CenterZ=0 NormalX=0 NormalY=0 NormalZ=1 AngleXU=0 Radius=1.6 StartAngle=1.5708 EndAngle=4.71239
    g49: LineSegment StartX=70 StartY=-89.2772 StartZ=0 EndX=73 EndY=-89.2772 EndZ=0
    g50: ArcOfCircle CenterX=73 CenterY=-90.8772 CenterZ=0 NormalX=0 NormalY=0 NormalZ=1 AngleXU=0 Radius=1.6 StartAngle=4.71239 EndAngle=7.85398
    g51: LineSegment StartX=70 StartY=-92.4772 StartZ=0 EndX=73 EndY=-92.4772 EndZ=0
    g52: ArcOfCircle CenterX=110 CenterY=-90.8772 CenterZ=0 NormalX=0 NormalY=0 NormalZ=1 AngleXU=0 Radius=1.6 StartAngle=1.5708 EndAngle=4.71239
    g53: LineSegment StartX=110 StartY=-89.2772 StartZ=0 EndX=113 EndY=-89.2772 EndZ=0
    g54: ArcOfCircle CenterX=113 CenterY=-90.8772 CenterZ=0 NormalX=0 NormalY=0 NormalZ=1 AngleXU=0 Radius=1.6 StartAngle=4.71239 EndAngle=7.85398
    g55: LineSegment StartX=110 StartY=-92.4772 StartZ=0 EndX=113 EndY=-92.4772 EndZ=0
    g56: ArcOfCircle CenterX=70 CenterY=-80.8772 CenterZ=0 NormalX=0 NormalY=0 NormalZ=1 AngleXU=0 Radius=1.6 StartAngle=1.5708 EndAngle=4.71239
    g57: LineSegment StartX=70 StartY=-79.2772 StartZ=0 EndX=73 EndY=-79.2772 EndZ=0
    g58: ArcOfCircle CenterX=73 CenterY=-80.8772 CenterZ=0 NormalX=0 NormalY=0 NormalZ=1 AngleXU=0 Radius=1.6 StartAngle=4.71239 EndAngle=7.85398
    g59: LineSegment StartX=70 StartY=-82.4772 StartZ=0 EndX=73 EndY=-82.4772 EndZ=0
    g60: ArcOfCircle CenterX=110 CenterY=-80.8772 CenterZ=0 NormalX=0 NormalY=0 NormalZ=1 AngleXU=0 Radius=1.6 StartAngle=1.5708 EndAngle=4.71239
    g61: LineSegment StartX=110 StartY=-79.2772 StartZ=0 EndX=113 EndY=-79.2772 EndZ=0
    g62: ArcOfCircle CenterX=113 CenterY=-80.8772 CenterZ=0 NormalX=0 NormalY=0 NormalZ=1 AngleXU=0 Radius=1.6 StartAngle=4.71239 EndAngle=7.85398
    g63: LineSegment StartX=110 StartY=-82.4772 StartZ=0 EndX=113 EndY=-82.4772 EndZ=0
    g64: LineSegment StartX=151.5 StartY=-48.4802 StartZ=0 EndX=151.5 EndY=-45.4802 EndZ=0
    g65: ArcOfCircle CenterX=153 CenterY=-45.4802 CenterZ=0 NormalX=0 NormalY=0 NormalZ=1 AngleXU=0 Radius=1.5 StartAngle=0 EndAngle=3.14159
    g66: LineSegment StartX=154.5 StartY=-48.4802 StartZ=0 EndX=154.5 EndY=-45.4802 EndZ=0
    g67: ArcOfCircle CenterX=153 CenterY=-48.4802 CenterZ=0 NormalX=0 NormalY=0 NormalZ=1 AngleXU=0 Radius=1.5 StartAngle=3.14159 EndAngle=6.28319
    g68: LineSegment StartX=138.5 StartY=-48.4802 StartZ=0 EndX=138.5 EndY=-45.4802 EndZ=0
    g69: ArcOfCircle CenterX=140 CenterY=-45.4802 CenterZ=0 NormalX=0 NormalY=0 NormalZ=1 AngleXU=0 Radius=1.5 StartAngle=0 EndAngle=3.14159
    g70: LineSegment StartX=141.5 StartY=-48.4802 StartZ=0 EndX=141.5 EndY=-45.4802 EndZ=0
    g71: ArcOfCircle CenterX=140 CenterY=-48.4802 CenterZ=0 NormalX=0 NormalY=0 NormalZ=1 AngleXU=0 Radius=1.5 StartAngle=3.14159 EndAngle=6.28319
    g72: LineSegment StartX=151.5 StartY=39.5198 StartZ=0 EndX=151.5 EndY=42.5198 EndZ=0
    g73: ArcOfCircle CenterX=153 CenterY=42.5198 CenterZ=0 NormalX=0 NormalY=0 NormalZ=1 AngleXU=0 Radius=1.5 StartAngle=0 EndAngle=3.14159
    g74: LineSegment StartX=154.5 StartY=39.5198 StartZ=0 EndX=154.5 EndY=42.5198 EndZ=0
    g75: ArcOfCircle CenterX=153 CenterY=39.5198 CenterZ=0 NormalX=0 NormalY=0 NormalZ=1 AngleXU=0 Radius=1.5 StartAngle=3.14159 EndAngle=6.28319
    g76: LineSegment StartX=138.5 StartY=39.5198 StartZ=0 EndX=138.5 EndY=42.5198 EndZ=0
    g77: ArcOfCircle CenterX=140 CenterY=42.5198 CenterZ=0 NormalX=0 NormalY=0 NormalZ=1 AngleXU=0 Radius=1.5 StartAngle=0 EndAngle=3.14159
    g78: LineSegment StartX=141.5 StartY=39.5198 StartZ=0 EndX=141.5 EndY=42.5198 EndZ=0
    g79: ArcOfCircle CenterX=140 CenterY=39.5198 CenterZ=0 NormalX=0 NormalY=0 NormalZ=1 AngleXU=0 Radius=1.5 StartAngle=3.14159 EndAngle=6.28319
    g80: Circle CenterX=34 CenterY=76.2086 CenterZ=0 NormalX=0 NormalY=0 NormalZ=1 AngleXU=-1.5708 Radius=2
    g81: Circle CenterX=-114 CenterY=76.2086 CenterZ=0 NormalX=0 NormalY=0 NormalZ=1 AngleXU=-1.5708 Radius=2
    g82: Circle CenterX=94 CenterY=96.5 CenterZ=0 NormalX=0 NormalY=0 NormalZ=-1 AngleXU=1.5708 Radius=1.7
    g83: Circle CenterX=125 CenterY=22.4383 CenterZ=0 NormalX=0 NormalY=0 NormalZ=1 AngleXU=0 Radius=1.7
    g84: Circle CenterX=81 CenterY=22.4383 CenterZ=0 NormalX=0 NormalY=0 NormalZ=1 AngleXU=0 Radius=1.7
    g85: Circle CenterX=128 CenterY=96.5 CenterZ=0 NormalX=0 NormalY=0 NormalZ=-1 AngleXU=1.5708 Radius=1.7
    g86: Circle CenterX=94 CenterY=144.5 CenterZ=0 NormalX=0 NormalY=0 NormalZ=-1 AngleXU=1.5708 Radius=1.7
    g87: Circle CenterX=128 CenterY=144.5 CenterZ=0 NormalX=0 NormalY=0 NormalZ=-1 AngleXU=1.5708 Radius=1.7
FEATURE [Sketcher::SketchObject] Unfold_Sketch_Outline005
  FullyConstrained = false
  sketch-geometry (40):
    g0: ArcOfCircle CenterX=52 CenterY=-102.569 CenterZ=0 NormalX=0 NormalY=0 NormalZ=1 AngleXU=-3.14159 Radius=2 StartAngle=0 EndAngle=1.5708
    g1: LineSegment StartX=52 StartY=-104.569 StartZ=0 EndX=118 EndY=-104.569 EndZ=0
    g2: ArcOfCircle CenterX=118 CenterY=-102.569 CenterZ=0 NormalX=0 NormalY=0 NormalZ=1 AngleXU=0 Radius=2 StartAngle=4.71239 EndAngle=6.28319
    g3: LineSegment StartX=120 StartY=-102.569 StartZ=0 EndX=120 EndY=-64.8772 EndZ=0
    g4: LineSegment StartX=120 StartY=-64.8772 StartZ=0 EndX=120.17 EndY=-64.8772 EndZ=0
    g5: LineSegment StartX=120.17 StartY=-64.8772 StartZ=0 EndX=120.17 EndY=-52.4997 EndZ=0
    g6: LineSegment StartX=120.17 StartY=-52.4997 StartZ=0 EndX=162.722 EndY=-52.4997 EndZ=0
    g7: ArcOfCircle CenterX=163 CenterY=-54.4802 CenterZ=0 NormalX=0 NormalY=0 NormalZ=1 AngleXU=1e-16 Radius=2 StartAngle=1.5708 EndAngle=1.71042
    g8: LineSegment StartX=164.309 StartY=-52.4802 StartZ=0 EndX=163 EndY=-52.4802 EndZ=0
    g9: ArcOfCircle CenterX=164.309 CenterY=-50.4802 CenterZ=0 NormalX=0 NormalY=0 NormalZ=1 AngleXU=1e-16 Radius=2 StartAngle=4.71239 EndAngle=5.37781
    g10: LineSegment StartX=174.259 StartY=-45.2134 StartZ=0 EndX=165.544 EndY=-52.0535 EndZ=0
    g11: ArcOfCircle CenterX=161.911 CenterY=-29.4802 CenterZ=0 NormalX=0 NormalY=0 NormalZ=1 AngleXU=1e-16 Radius=20 StartAngle=5.37781 EndAngle=6.40978
    g12: LineSegment StartX=171.222 StartY=55.7723 StartZ=0 EndX=181.751 EndY=-26.9551 EndZ=0
    g13: ArcOfCircle CenterX=169.238 CenterY=55.5198 CenterZ=0 NormalX=0 NormalY=0 NormalZ=1 AngleXU=1e-16 Radius=2 StartAngle=0.126592 EndAngle=1.5708
    g14: LineSegment StartX=169.238 StartY=57.5198 StartZ=0 EndX=163 EndY=57.5198 EndZ=0
    g15: ArcOfCircle CenterX=163 CenterY=59.5198 CenterZ=0 NormalX=0 NormalY=0 NormalZ=1 AngleXU=1e-16 Radius=2 StartAngle=3.14159 EndAngle=4.71239
    g16: LineSegment StartX=161 StartY=59.5198 StartZ=0 EndX=161 EndY=149 EndZ=0
    g17: ArcOfCircle CenterX=159 CenterY=149 CenterZ=0 NormalX=0 NormalY=0 NormalZ=1 AngleXU=1.5708 Radius=2 StartAngle=4.71239 EndAngle=6.28319
    g18: LineSegment StartX=-159 StartY=151 StartZ=0 EndX=159 EndY=151 EndZ=0
    g19: ArcOfCircle CenterX=-159 CenterY=149 CenterZ=0 NormalX=0 NormalY=0 NormalZ=1 AngleXU=1.5708 Radius=2 StartAngle=0 EndAngle=1.5708
    g20: LineSegment StartX=-161 StartY=59.5198 StartZ=0 EndX=-161 EndY=149 EndZ=0
    g21: ArcOfCircle CenterX=-163 CenterY=59.5198 CenterZ=0 NormalX=0 NormalY=0 NormalZ=1 AngleXU=3.14159 Radius=2 StartAngle=1.5708 EndAngle=3.14159
    g22: LineSegment StartX=-169.238 StartY=57.5198 StartZ=0 EndX=-163 EndY=57.5198 EndZ=0
    g23: ArcOfCircle CenterX=-169.238 CenterY=55.5198 CenterZ=0 NormalX=0 NormalY=0 NormalZ=1 AngleXU=3.14159 Radius=2 StartAngle=4.71239 EndAngle=6.15659
    g24: LineSegment StartX=-171.222 StartY=55.7723 StartZ=0 EndX=-181.751 EndY=-26.9551 EndZ=0
    g25: ArcOfCircle CenterX=-161.911 CenterY=-29.4802 CenterZ=0 NormalX=0 NormalY=0 NormalZ=1 AngleXU=3.14159 Radius=20 StartAngle=6.15659 EndAngle=7.18856
    g26: LineSegment StartX=-174.259 StartY=-45.2134 StartZ=0 EndX=-165.544 EndY=-52.0535 EndZ=0
    g27: ArcOfCircle CenterX=-164.309 CenterY=-50.4802 CenterZ=0 NormalX=0 NormalY=0 NormalZ=1 AngleXU=3.14159 Radius=2 StartAngle=0.905377 EndAngle=1.5708
    g28: LineSegment StartX=-164.309 StartY=-52.4802 StartZ=0 EndX=-163 EndY=-52.4802 EndZ=0
    g29: ArcOfCircle CenterX=-163 CenterY=-54.4802 CenterZ=0 NormalX=0 NormalY=0 NormalZ=1 AngleXU=3.14159 Radius=2 StartAngle=4.57277 EndAngle=4.71239
    g30: LineSegment StartX=-162.722 StartY=-52.4997 StartZ=0 EndX=-120.17 EndY=-52.4997 EndZ=0
    g31: LineSegment StartX=-120.17 StartY=-52.4997 StartZ=0 EndX=-120.17 EndY=-64.8772 EndZ=0
    g32: LineSegment StartX=-120.17 StartY=-64.8772 StartZ=0 EndX=-120 EndY=-64.8772 EndZ=0
    g33: LineSegment StartX=-120 StartY=-102.569 StartZ=0 EndX=-120 EndY=-64.8772 EndZ=0
    g34: ArcOfCircle CenterX=-118 CenterY=-102.569 CenterZ=0 NormalX=0 NormalY=0 NormalZ=1 AngleXU=-3.14159 Radius=2 StartAngle=0 EndAngle=1.5708
    g35: LineSegment StartX=-118 StartY=-104.569 StartZ=0 EndX=-52 EndY=-104.569 EndZ=0
    g36: ArcOfCircle CenterX=-52 CenterY=-102.569 CenterZ=0 NormalX=0 NormalY=0 NormalZ=1 AngleXU=0 Radius=2 StartAngle=4.71239 EndAngle=6.28319
    g37: LineSegment StartX=-50 StartY=-102.569 StartZ=0 EndX=-50 EndY=-64.8772 EndZ=0
    g38: LineSegment StartX=-50 StartY=-64.8772 StartZ=0 EndX=50 EndY=-64.8772 EndZ=0
    g39: LineSegment StartX=50 StartY=-102.569 StartZ=0 EndX=50 EndY=-64.8772 EndZ=0
FEATURE [Sketcher::SketchObject] Unfold_Sketch_Internal005
  FullyConstrained = false
  sketch-geometry (48):
    g0: LineSegment StartX=93.5 StartY=9.77968 StartZ=0 EndX=112.5 EndY=9.77968 EndZ=0
    g1: ArcOfCircle CenterX=112.5 CenterY=14.7797 CenterZ=0 NormalX=0 NormalY=0 NormalZ=1 AngleXU=0 Radius=5 StartAngle=4.71239 EndAngle=6.28319
    g2: LineSegment StartX=117.5 StartY=14.7797 StartZ=0 EndX=117.5 EndY=52.5198 EndZ=0
    g3: ArcOfCircle CenterX=112.5 CenterY=52.5198 CenterZ=0 NormalX=0 NormalY=0 NormalZ=1 AngleXU=0 Radius=5 StartAngle=0 EndAngle=1.5708
    g4: LineSegment StartX=112.5 StartY=57.5198 StartZ=0 EndX=93.5 EndY=57.5198 EndZ=0
    g5: ArcOfCircle CenterX=93.5 CenterY=52.5198 CenterZ=0 NormalX=0 NormalY=0 NormalZ=1 AngleXU=0 Radius=5 StartAngle=1.5708 EndAngle=3.14159
    g6: LineSegment StartX=88.5 StartY=52.5198 StartZ=0 EndX=88.5 EndY=14.7797 EndZ=0
    g7: ArcOfCircle CenterX=93.5 CenterY=14.7797 CenterZ=0 NormalX=0 NormalY=0 NormalZ=1 AngleXU=0 Radius=5 StartAngle=3.14159 EndAngle=4.71239
    g8: ArcOfCircle CenterX=110 CenterY=-80.8772 CenterZ=0 NormalX=0 NormalY=0 NormalZ=1 AngleXU=0 Radius=1.6 StartAngle=1.5708 EndAngle=4.71239
    g9: LineSegment StartX=110 StartY=-82.4772 StartZ=0 EndX=113 EndY=-82.4772 EndZ=0
    g10: ArcOfCircle CenterX=113 CenterY=-80.8772 CenterZ=0 NormalX=0 NormalY=0 NormalZ=1 AngleXU=0 Radius=1.6 StartAngle=4.71239 EndAngle=7.85398
    g11: LineSegment StartX=110 StartY=-79.2772 StartZ=0 EndX=113 EndY=-79.2772 EndZ=0
    g12: ArcOfCircle CenterX=70 CenterY=-80.8772 CenterZ=0 NormalX=0 NormalY=0 NormalZ=1 AngleXU=0 Radius=1.6 StartAngle=1.5708 EndAngle=4.71239
    g13: LineSegment StartX=70 StartY=-82.4772 StartZ=0 EndX=73 EndY=-82.4772 EndZ=0
    g14: ArcOfCircle CenterX=73 CenterY=-80.8772 CenterZ=0 NormalX=0 NormalY=0 NormalZ=1 AngleXU=0 Radius=1.6 StartAngle=4.71239 EndAngle=7.85398
    g15: LineSegment StartX=70 StartY=-79.2772 StartZ=0 EndX=73 EndY=-79.2772 EndZ=0
    g16: ArcOfCircle CenterX=110 CenterY=-90.8772 CenterZ=0 NormalX=0 NormalY=0 NormalZ=1 AngleXU=0 Radius=1.6 StartAngle=1.5708 EndAngle=4.71239
    g17: LineSegment StartX=110 StartY=-92.4772 StartZ=0 EndX=113 EndY=-92.4772 EndZ=0
    g18: ArcOfCircle CenterX=113 CenterY=-90.8772 CenterZ=0 NormalX=0 NormalY=0 NormalZ=1 AngleXU=0 Radius=1.6 StartAngle=4.71239 EndAngle=7.85398
    g19: LineSegment StartX=110 StartY=-89.2772 StartZ=0 EndX=113 EndY=-89.2772 EndZ=0
    g20: ArcOfCircle CenterX=70 CenterY=-90.8772 CenterZ=0 NormalX=0 NormalY=0 NormalZ=1 AngleXU=0 Radius=1.6 StartAngle=1.5708 EndAngle=4.71239
    g21: LineSegment StartX=70 StartY=-92.4772 StartZ=0 EndX=73 EndY=-92.4772 EndZ=0
    g22: ArcOfCircle CenterX=73 CenterY=-90.8772 CenterZ=0 NormalX=0 NormalY=0 NormalZ=1 AngleXU=0 Radius=1.6 StartAngle=4.71239 EndAngle=7.85398
    g23: LineSegment StartX=70 StartY=-89.2772 StartZ=0 EndX=73 EndY=-89.2772 EndZ=0
    g24: LineSegment StartX=138.5 StartY=39.5198 StartZ=0 EndX=138.5 EndY=42.5198 EndZ=0
    g25: ArcOfCircle CenterX=140 CenterY=42.5198 CenterZ=0 NormalX=0 NormalY=0 NormalZ=1 AngleXU=0 Radius=1.5 StartAngle=0 EndAngle=3.14159
    g26: LineSegment StartX=141.5 StartY=39.5198 StartZ=0 EndX=141.5 EndY=42.5198 EndZ=0
    g27: ArcOfCircle CenterX=140 CenterY=39.5198 CenterZ=0 NormalX=0 NormalY=0 NormalZ=1 AngleXU=0 Radius=1.5 StartAngle=3.14159 EndAngle=6.28319
    g28: LineSegment StartX=151.5 StartY=39.5198 StartZ=0 EndX=151.5 EndY=42.5198 EndZ=0
    g29: ArcOfCircle CenterX=153 CenterY=42.5198 CenterZ=0 NormalX=0 NormalY=0 NormalZ=1 AngleXU=0 Radius=1.5 StartAngle=0 EndAngle=3.14159
    g30: LineSegment StartX=154.5 StartY=39.5198 StartZ=0 EndX=154.5 EndY=42.5198 EndZ=0
    g31: ArcOfCircle CenterX=153 CenterY=39.5198 CenterZ=0 NormalX=0 NormalY=0 NormalZ=1 AngleXU=0 Radius=1.5 StartAngle=3.14159 EndAngle=6.28319
    g32: LineSegment StartX=138.5 StartY=-48.4802 StartZ=0 EndX=138.5 EndY=-45.4802 EndZ=0
    g33: ArcOfCircle CenterX=140 CenterY=-45.4802 CenterZ=0 NormalX=0 NormalY=0 NormalZ=1 AngleXU=0 Radius=1.5 StartAngle=0 EndAngle=3.14159
    g34: LineSegment StartX=141.5 StartY=-48.4802 StartZ=0 EndX=141.5 EndY=-45.4802 EndZ=0
    g35: ArcOfCircle CenterX=140 CenterY=-48.4802 CenterZ=0 NormalX=0 NormalY=0 NormalZ=1 AngleXU=0 Radius=1.5 StartAngle=3.14159 EndAngle=6.28319
    g36: LineSegment StartX=151.5 StartY=-48.4802 StartZ=0 EndX=151.5 EndY=-45.4802 EndZ=0
    g37: ArcOfCircle CenterX=153 CenterY=-45.4802 CenterZ=0 NormalX=0 NormalY=0 NormalZ=1 AngleXU=0 Radius=1.5 StartAngle=0 EndAngle=3.14159
    g38: LineSegment StartX=154.5 StartY=-48.4802 StartZ=0 EndX=154.5 EndY=-45.4802 EndZ=0
    g39: ArcOfCircle CenterX=153 CenterY=-48.4802 CenterZ=0 NormalX=0 NormalY=0 NormalZ=1 AngleXU=0 Radius=1.5 StartAngle=3.14159 EndAngle=6.28319
    g40: Circle CenterX=-114 CenterY=76.2086 CenterZ=0 NormalX=0 NormalY=0 NormalZ=1 AngleXU=-1.5708 Radius=2
    g41: Circle CenterX=34 CenterY=76.2086 CenterZ=0 NormalX=0 NormalY=0 NormalZ=1 AngleXU=-1.5708 Radius=2
    g42: Circle CenterX=94 CenterY=96.5 CenterZ=0 NormalX=0 NormalY=0 NormalZ=-1 AngleXU=1.5708 Radius=1.7
    g43: Circle CenterX=81 CenterY=22.4383 CenterZ=0 NormalX=0 NormalY=0 NormalZ=1 AngleXU=0 Radius=1.7
    g44: Circle CenterX=125 CenterY=22.4383 CenterZ=0 NormalX=0 NormalY=0 NormalZ=1 AngleXU=0 Radius=1.7
    g45: Circle CenterX=128 CenterY=96.5 CenterZ=0 NormalX=0 NormalY=0 NormalZ=-1 AngleXU=1.5708 Radius=1.7
    g46: Circle CenterX=94 CenterY=144.5 CenterZ=0 NormalX=0 NormalY=0 NormalZ=-1 AngleXU=1.5708 Radius=1.7
    g47: Circle CenterX=128 CenterY=144.5 CenterZ=0 NormalX=0 NormalY=0 NormalZ=-1 AngleXU=1.5708 Radius=1.7
FEATURE [Sketcher::SketchObject] Unfold_Sketch_bends007  label="pump_holder_Sketch_bends"
  FullyConstrained = false
  sketch-geometry (5):
    g0: LineSegment StartX=120 StartY=-94.7229 StartZ=0 EndX=50 EndY=-94.7229 EndZ=0
    g1: LineSegment StartX=-50 StartY=-94.7229 StartZ=0 EndX=-120 EndY=-94.7229 EndZ=0
    g2: LineSegment StartX=120.17 StartY=-59.7828 StartZ=0 EndX=-120.17 EndY=-59.7828 EndZ=0
    g3: LineSegment StartX=161 StartY=60.6142 StartZ=0 EndX=-161 EndY=60.6142 EndZ=0
    g4: LineSegment StartX=161 StartY=90.8543 StartZ=0 EndX=-161 EndY=90.8543 EndZ=0
FEATURE [Part::Part2DObjectPython] Clone2D  label="pump_holder_Sketch_bends (2D)"  # Draft 2D object (typed FeaturePython)
  Fuse = false
  Objects = -> [Unfold_Sketch_bends007]
  Scale = (1,1,1)
  expr: Objects = <<pump_holder_Sketch_bends>>._self
FEATURE [Part::Part2DObjectPython] Clone2D001  label="Model-Unfold_Sketch_bends (2D)"  # Draft 2D object (typed FeaturePython)
  Fuse = false
  Objects = -> [Clone2D]
  PathResource = Model
  Placement = pos=(-205,-63.2536,-2.8e-14) rot=(0,0,1;3.14159rad)
  Scale = (1,1,1)
  expr: Placement = <<Model-Body009>>.Placement
FEATURE [App::DocumentObjectGroup] Model001
  Group = -> [Clone2D001]
FEATURE [Part::FeaturePython] Stock001  # WARN: FeaturePython — macro-defined, semantics opaque (R4)
  Base = -> Model001
  ExtXneg = 1
  ExtXpos = 1
  ExtYneg = 1
  ExtYpos = 1
  ExtZneg = 0
  ExtZpos = 1
  Placement = pos=(-120,-96.2899,0) rot=(0,0,1;0rad)
  StockType = FromBase
FEATURE [Path::FeaturePython] Engrave  # Path/CAM operation (typed FeaturePython)
  Active = true
  BaseShapes = -> [Clone2D001]
  ClearanceHeight = 6
  CoolantMode = 0
  CycleTime = 00:00:48
  FinalDepth = 1.5
  OpFinalDepth = -10
  OpStartDepth = -2.8e-14
  OpStockZMax = 1
  OpStockZMin = 0
  OpToolDiameter = 10
  SafeHeight = 4
  StartDepth = 3
  StartVertex = 0
  StepDown = 10
  ToolController = -> NZV6109015
  expr: BaseShapes = <<Model001>>.Group
  expr: ClearanceHeight = OpStockZMax + SetupSheet001.ClearanceHeightOffset
  expr: SafeHeight = OpStockZMax + SetupSheet001.SafeHeightOffset
  expr: StartDepth = 3 mm
  expr: StepDown = OpToolDiameter
FEATURE [App::DocumentObjectGroup] Operations001
  Group = -> [Engrave]
FEATURE [Path::FeaturePython] Job001  # Path/CAM operation (typed FeaturePython)
  CycleTime = 00:00:48
  Fixtures = G54
  GeometryTolerance = 0.01
  JobType = 0
  LastPostProcessDate = 2024-02-26 15:59:41.467892
  LastPostProcessOutput = <userpath>/2CAF-B51C/Job001.tap
  Model = -> Model001
  Operations = -> Operations001
  OrderOutputBy = 0
  PostProcessor = 3
  PostProcessorOutputFile = %j.tap
  SetupSheet = -> SetupSheet001
  SplitOutput = false
  Stock = -> Stock001
  Tools = -> Tools001
FEATURE [App::DocumentObjectGroup] Group003  label="jobs"
  Group = -> [Job,Job001]
FEATURE [App::FeaturePython] SetupSheet002  # Path/CAM operation (typed FeaturePython)
  ClearanceHeightExpression = OpStockZMax+SetupSheet002.ClearanceHeightOffset
  ClearanceHeightOffset = 15.7
  CoolantMode = 0
  CoolantModes = None | Flood | Mist
  FinalDepthExpression = -0.1 mm
  HorizRapid = 0
  ProfileDirection = 1
  ProfileSide = 0
  ProfileUseComp = true
  ProfileprocessCircles = true
  ProfileprocessHoles = true
  ProfileprocessPerimeter = true
  SafeHeightExpression = OpStockZMax+SetupSheet002.SafeHeightOffset
  SafeHeightOffset = 3
  StartDepthExpression = 3 mm
  StepDownExpression = 4 mm
  VertRapid = 0
FEATURE [Part::FeaturePython] ToolBit002  label="3.175mm Endmill003"  # Path/CAM toolbit (typed FeaturePython)
  BitPropertyNames = Chipload | CuttingEdgeHeight | Diameter | Flutes | Length | Material | ShankDiameter | SpindleDirection
  BitShape = <path>
  Chipload = 0
  CuttingEdgeHeight = 30
  Diameter = 3.175
  Flutes = 0
  Length = 10
  Material = 0
  ShankDiameter = 3
  ShapeName = endmill
  SpindleDirection = 0
FEATURE [Path::FeaturePython] __175mm_Endmill001  label="3.175mm Endmill002"  # Path/CAM operation (typed FeaturePython)
  HorizFeed = 33.3333
  HorizRapid = 0
  SpindleDir = 0
  SpindleSpeed = 18000
  Tool = -> ToolBit002
  ToolNumber = 1
  VertFeed = 8.33333
  VertRapid = 0
  expr: HorizRapid = SetupSheet002.HorizRapid
  expr: VertRapid = SetupSheet002.VertRapid
FEATURE [App::DocumentObjectGroup] Tools002
  Group = -> [__175mm_Endmill001]
FEATURE [Sketcher::SketchObject] Sketch114
  ExternalGeometry = -> [Unfold_Sketch_bends004,Unfold_Sketch_Outline001,Unfold_Sketch_Internal001]
  FullyConstrained = true
  sketch-geometry (15):
    g0: ArcOfCircle CenterX=0 CenterY=-7 CenterZ=0 NormalX=0 NormalY=0 NormalZ=1 AngleXU=0 Radius=5.5 StartAngle=4.71239 EndAngle=6.28319
    g1: ArcOfCircle CenterX=7.5 CenterY=-2 CenterZ=0 NormalX=0 NormalY=0 NormalZ=1 AngleXU=0 Radius=2 StartAngle=1.5708 EndAngle=3.14159
    g2: ArcOfCircle CenterX=34.2649 CenterY=-15.7371 CenterZ=0 NormalX=0 NormalY=0 NormalZ=1 AngleXU=0 Radius=2 StartAngle=5.49779 EndAngle=7.06858
    g3: ArcOfCircle CenterX=24.0933 CenterY=-25.9087 CenterZ=0 NormalX=0 NormalY=0 NormalZ=1 AngleXU=0 Radius=2 StartAngle=3.92699 EndAngle=5.49779
    g4: LineSegment StartX=0 StartY=-20 StartZ=0 EndX=15.3562 EndY=-20 EndZ=0
    g5: LineSegment StartX=25.5076 StartY=-27.3229 StartZ=0 EndX=35.6791 EndY=-17.1514 EndZ=0
    g6: LineSegment StartX=35.6791 StartY=-14.3229 StartZ=0 EndX=30.3206 EndY=-8.96441 EndZ=0
    g7: LineSegment StartX=28.3562 StartY=-6.46701 StartZ=0 EndX=28.3562 EndY=2.7e-15 EndZ=0
    g8: LineSegment StartX=28.3562 StartY=2.7e-15 StartZ=0 EndX=15.7781 EndY=2.7e-15 EndZ=0
    g9: LineSegment StartX=5.5 StartY=-7 StartZ=0 EndX=5.5 EndY=-2 EndZ=0
    g10: LineSegment StartX=15.3562 StartY=-20 StartZ=0 EndX=22.6791 EndY=-27.3229 EndZ=0
    g11: ArcOfCircle CenterX=14.1781 CenterY=0 CenterZ=0 NormalX=0 NormalY=0 NormalZ=1 AngleXU=0 Radius=1.6 StartAngle=3.14159 EndAngle=6.28319
    g12: ArcOfCircle CenterX=29.1892 CenterY=-7.83304 CenterZ=0 NormalX=0 NormalY=0 NormalZ=1 AngleXU=0 Radius=1.6 StartAngle=2.11841 EndAngle=5.49779
    g13: LineSegment StartX=12.5781 StartY=3e-15 StartZ=0 EndX=7.49999 EndY=3e-15 EndZ=0
    g14: Circle CenterX=28.336 CenterY=-18.8377 CenterZ=0 NormalX=0 NormalY=0 NormalZ=1 AngleXU=0 Radius=1.7
  constraints (37):
    c: Coincident(g0,g-12)
    c: Coincident(g0,g-13)
    c: PointOnObject(g0,g-2)
    c: Coincident(g1,g-14)
    c: Coincident(g1,g-14)
    c: Coincident(g2,g-7)
    c: Coincident(g2,g-8)
    c: Coincident(g3,g-5)
    c: Coincident(g3,g-5)
    c: PointOnObject(g4,g-2)
    c: Coincident(g10,g3)
    c: Tangent(g3,g5) = -1.5708
    c: Tangent(g2,g6) = -1.5708
    c: Coincident(g7,g-9)
    c: Vertical(g7)
    c: Coincident(g7,g8)
    c: Coincident(g13,g1) = -1.5708
    c: Tangent(g5,g2) = -1.5708
    c: Horizontal(g4)
    c: Coincident(g9,g0)
    c: Coincident(g9,g1)
    c: Coincident(g11,g-10)
    c: PointOnObject(g11,g8)
    c: Coincident(g12,g-3)
    c: Coincident(g6,g12)
    c: Coincident(g8,g11)
    c: Equal(g11,g12)
    c: Diameter(g11) = 3.2
    c: PointOnObject(g4,g-11)
    c: PointOnObject(g10,g-4)
    c: Coincident(g12,g7)
    c: Coincident(g13,g11)
    c: Horizontal(g8)
    c: Horizontal(g13)
    c: Coincident(g14,g-15)
    c: Diameter(g14) = 3.4
    c: Coincident(g10,g4)
FEATURE [Part::Mirroring] Part__Mirroring029  label="Sketch114 (Mirror #28)"
  Base = (0,0,0)
  Normal = (1,0,0)
  Source = -> Sketch114
FEATURE [Part::FeaturePython] Connect013  # WARN: FeaturePython — macro-defined, semantics opaque (R4)
  Objects = -> [Sketch114,Part__Mirroring029]
  Tolerance = 0
FEATURE [Part::Extrusion] Extrude028  label="Extrude029"
  Base = -> Connect013
  Dir = (0,0,1)
  DirMode = 2
  FaceMakerClass = Part::FaceMakerBullseye
  LengthFwd = 3
  LengthRev = 0
  Solid = true
  Symmetric = false
FEATURE [Part::FeaturePython] Clone001  label="Model-Unfold004"  # Draft clone (typed FeaturePython)
  AttacherType = Attacher::AttachEngine3D
  Fuse = false
  Objects = -> [Extrude028]
  PathResource = Model
  Placement = pos=(36.2523,27.8961,0) rot=(0,0,1;0rad)
  Scale = (1,1,1)
FEATURE [App::DocumentObjectGroup] Model002
  Group = -> [Clone001]
FEATURE [Part::FeaturePython] Stock002  # WARN: FeaturePython — macro-defined, semantics opaque (R4)
  Base = -> Model002
  ExtXneg = 0
  ExtXpos = 1
  ExtYneg = 0
  ExtYpos = 1
  ExtZneg = 0
  ExtZpos = 1
  Placement = pos=(-36.2523,-27.8961,-1) rot=(0,0,1;0rad)
  StockType = FromBase
FEATURE [Path::FeaturePython] Profile003  # Path/CAM operation (typed FeaturePython)
  Active = true
  AreaParams:
    Tolerance = 1e-07
    FitArcs = True
    Simplify = False
    CleanDistance = 0.0
    Accuracy = 0.01
    Unit = 1.0
    MinArcPoints = 4
    MaxArcPoints = 100
    ClipperScale = 10000000.0
    Fill = 0
    Coplanar = 0
    Reorient = True
    Outline = False
    Explode = False
    OpenMode = 0
    Deflection = 0.01
    SubjectFill = 0
    ClipFill = 0
    Offset = 1.5875
    ExtraPass = 0
    Stepover = 0.0
    LastStepover = 0.0
    JoinType = 0
    EndType = 0
    MiterLimit = 2.0
    RoundPrecision = 0.0
    PocketMode = 0
    ToolRadius = 1.0
    PocketExtraOffset = 0.0
    PocketStepover = 0.0
    PocketLastStepover = 0.0
    FromCenter = False
    Angle = 45.0
    AngleShift = 0.0
    Shift = 0.0
    Thicken = False
    SectionCount = -1
    Stepdown = 1.0
    SectionOffset = 0.0
    SectionTolerance = 1e-06
    SectionMode = 2
    Project = False
  Base = -> [Clone001]
  ClearanceHeight = 18.7
  CoolantMode = 0
  CycleTime = 00:00:23
  Direction = 1
  FinalDepth = -0.1
  HandleMultipleFeatures = 0
  JoinType = 0
  MiterLimit = 0.1
  OffsetExtra = 0
  OpFinalDepth = 0
  OpStartDepth = 3
  OpStockZMax = 3
  OpStockZMin = -1
  OpToolDiameter = 3.175
  PathParams = {'orientation': 0, 'feedrate': 33.333333333333336, 'feedrate_v': 8.333333333333334, 'verbose': True, 'resume_height': 5.999999999999993, 'retraction': 18.699999999999992, 'return_end': True, 'preamble': False, 'start': Vector (64.48456932206612, 9.058626684651335, 18.699999999999992)}
  SafeHeight = 6
  Side = 0
  SplitArcs = false
  StartDepth = 3
  StartPoint = (0,0,0)
  StepDown = 4
  ToolController = -> __175mm_Endmill001
  UseComp = true
  UseStartPoint = false
  processCircles = true
  processHoles = false
  processPerimeter = true
  expr: ClearanceHeight = OpStockZMax + SetupSheet002.ClearanceHeightOffset
  expr: FinalDepth = -0.1 mm
  expr: SafeHeight = OpStockZMax + SetupSheet002.SafeHeightOffset
  expr: StartDepth = 3 mm
  expr: StepDown = 4 mm
FEATURE [Path::FeaturePython] DressupTag  # Path/CAM operation (typed FeaturePython)
  Angle = 45
  Base = -> Profile003
  Disabled = [1,3]
  Height = 1.55
  Positions = (4) [(68.651,5.2253,-0.099999),(36.5041,16.9944,-0.099999),(4.6343,4.444,-0.099999),(36.2523,6.30865,-0.099999)]
  Radius = 0
  SegmentationFactor = 50
  Width = 7
FEATURE [App::DocumentObjectGroup] Operations002
  Group = -> [DressupTag]
FEATURE [Path::FeaturePython] Job002  # Path/CAM operation (typed FeaturePython)
  CycleTime = 00:00:23
  Fixtures = G54
  GeometryTolerance = 0.01
  JobType = 0
  LastPostProcessDate = 2024-08-21 14:01:13.957274
  LastPostProcessOutput = <path>
  Model = -> Model002
  Operations = -> Operations002
  OrderOutputBy = 2
  PostProcessor = 13
  PostProcessorOutputFile = <path>/%j.tap
  SetupSheet = -> SetupSheet002
  SplitOutput = true
  Stock = -> Stock002
  Tools = -> Tools002
FEATURE [TechDraw::DrawViewDimension] Dimension027
  AngleOverride = false
  Arbitrary = false
  ArbitraryTolerances = false
  BoxCorners = (2) [(-90.85,-58.35,-1e-07),(90.85,58.35,1e-07)]
  EqualTolerance = true
  ExtensionAngle = 0
  FormatSpec = %.2w
  FormatSpecOverTolerance = %+.2w
  FormatSpecUnderTolerance = %+.2w
  Inverted = false
  LineAngle = 0
  LockPosition = false
  MeasureType = 1
  OverTolerance = 0
  References2D = -> [View]
  Rotation = 0
  ScaleType = 0
  TheoreticalExact = false
  Type = 1
  UnderTolerance = 0
  X = -60.35
  Y = -61.3399
FEATURE [TechDraw::DrawViewDimension] Dimension028
  AngleOverride = false
  Arbitrary = false
  ArbitraryTolerances = false
  BoxCorners = (2) [(-90.85,-58.35,-1e-07),(90.85,58.35,1e-07)]
  EqualTolerance = true
  ExtensionAngle = 0
  FormatSpec = %.2w
  FormatSpecOverTolerance = %+.2w
  FormatSpecUnderTolerance = %+.2w
  Inverted = false
  LineAngle = 0
  LockPosition = false
  MeasureType = 1
  OverTolerance = 0
  References2D = -> [View]
  Rotation = 0
  ScaleType = 0
  TheoreticalExact = false
  Type = 2
  UnderTolerance = 0
  X = -58.4866
  Y = -40.4403
FEATURE [TechDraw::DrawViewDimension] Dimension029
  AngleOverride = false
  Arbitrary = false
  ArbitraryTolerances = false
  BoxCorners = (2) [(-90.85,-58.35,-1e-07),(90.85,58.35,1e-07)]
  EqualTolerance = true
  ExtensionAngle = 0
  FormatSpec = %.2w
  FormatSpecOverTolerance = %+.2w
  FormatSpecUnderTolerance = %+.2w
  Inverted = false
  LineAngle = 0
  LockPosition = false
  MeasureType = 1
  OverTolerance = 0
  References2D = -> [View]
  Rotation = 0
  ScaleType = 0
  TheoreticalExact = false
  Type = 0
  UnderTolerance = 0
  X = -2.09952
  Y = 27.5636
FEATURE [TechDraw::DrawViewDimension] Dimension030
  AngleOverride = false
  Arbitrary = false
  ArbitraryTolerances = false
  BoxCorners = (2) [(-90.85,-58.35,-1e-07),(90.85,58.35,1e-07)]
  EqualTolerance = true
  ExtensionAngle = 0
  FormatSpec = %.2w
  FormatSpecOverTolerance = %+.2w
  FormatSpecUnderTolerance = %+.2w
  Inverted = false
  LineAngle = 0
  LockPosition = false
  MeasureType = 1
  OverTolerance = 0
  References2D = -> [View]
  Rotation = 0
  ScaleType = 0
  TheoreticalExact = false
  Type = 1
  UnderTolerance = 0
  X = 72.5938
  Y = 72.9713
FEATURE [TechDraw::DrawViewDimension] Dimension031
  AngleOverride = false
  Arbitrary = false
  ArbitraryTolerances = false
  BoxCorners = (2) [(-90.85,-58.35,-1e-07),(90.85,58.35,1e-07)]
  EqualTolerance = true
  ExtensionAngle = 0
  FormatSpec = %.2w
  FormatSpecOverTolerance = %+.2w
  FormatSpecUnderTolerance = %+.2w
  Inverted = false
  LineAngle = 0
  LockPosition = false
  MeasureType = 1
  OverTolerance = 0
  References2D = -> [View]
  Rotation = 0
  ScaleType = 0
  TheoreticalExact = false
  Type = 2
  UnderTolerance = 0
  X = 89.0501
  Y = 39.9232
FEATURE [TechDraw::DrawViewDimension] Dimension032
  AngleOverride = false
  Arbitrary = false
  ArbitraryTolerances = false
  BoxCorners = (2) [(-90.85,-58.35,-1e-07),(90.85,58.35,1e-07)]
  EqualTolerance = true
  ExtensionAngle = 0
  FormatSpec = %.2w
  FormatSpecOverTolerance = %+.2w
  FormatSpecUnderTolerance = %+.2w
  Inverted = false
  LineAngle = 0
  LockPosition = false
  MeasureType = 1
  OverTolerance = 0
  References2D = -> [View]
  Rotation = 0
  ScaleType = 0
  TheoreticalExact = false
  Type = 6
  UnderTolerance = 0
  X = 84.433
  Y = 49.8406
FEATURE [TechDraw::DrawViewDimension] Dimension033
  AngleOverride = false
  Arbitrary = false
  ArbitraryTolerances = false
  BoxCorners = (2) [(-90.85,-58.35,-1e-07),(90.85,58.35,1e-07)]
  EqualTolerance = true
  ExtensionAngle = 0
  FormatSpec = %.2w
  FormatSpecOverTolerance = %+.2w
  FormatSpecUnderTolerance = %+.2w
  Inverted = false
  LineAngle = 0
  LockPosition = false
  MeasureType = 1
  OverTolerance = 0
  References2D = -> [View]
  Rotation = 0
  ScaleType = 0
  TheoreticalExact = false
  Type = 6
  UnderTolerance = 0
  X = 57.1754
  Y = 49.538
FEATURE [TechDraw::DrawViewDimension] Dimension034
  AngleOverride = false
  Arbitrary = false
  ArbitraryTolerances = false
  BoxCorners = (2) [(-90.85,-58.35,-1e-07),(90.85,58.35,1e-07)]
  EqualTolerance = true
  ExtensionAngle = 0
  FormatSpec = %.2w
  FormatSpecOverTolerance = %+.2w
  FormatSpecUnderTolerance = %+.2w
  Inverted = false
  LineAngle = 0
  LockPosition = false
  MeasureType = 1
  OverTolerance = 0
  References2D = -> [View]
  Rotation = 0
  ScaleType = 0
  TheoreticalExact = false
  Type = 6
  UnderTolerance = 0
  X = -21.2295
  Y = -44.4441
FEATURE [TechDraw::DrawViewDimension] Dimension035
  AngleOverride = false
  Arbitrary = false
  ArbitraryTolerances = false
  BoxCorners = (2) [(-90.85,-58.35,-1e-07),(90.85,58.35,1e-07)]
  EqualTolerance = true
  ExtensionAngle = 0
  FormatSpec = %.2w
  FormatSpecOverTolerance = %+.2w
  FormatSpecUnderTolerance = %+.2w
  Inverted = false
  LineAngle = 0
  LockPosition = false
  MeasureType = 1
  OverTolerance = 0
  References2D = -> [View]
  Rotation = 0
  ScaleType = 0
  TheoreticalExact = false
  Type = 6
  UnderTolerance = 0
  X = -38.1862
  Y = -34.9424
FEATURE [TechDraw::DrawPage] Page
  KeepUpdated = true
  NextBalloonIndex = 2
  ProjectionType = 0
  Template = -> Template
  Views = -> [View001,Balloon002,View,Dimension027,Dimension028,Dimension029,Dimension030,Dimension031,Dimension032,Dimension033,Dimension034,Dimension035]
FEATURE [App::DocumentObjectGroup] Group004  label="pump_holder_Group"
  Group = -> [Body009,Clone2D,Page,Unfold007,Unfold_Sketch007,Unfold_Sketch_Outline005,Unfold_Sketch_Internal005,Unfold_Sketch_bends007]
FEATURE [TechDraw::DrawViewDimension] Dimension036
  AngleOverride = false
  Arbitrary = false
  ArbitraryTolerances = false
  BoxCorners = (2) [(-27.1085,-34.7491,-1e-07),(27.1085,34.7491,1e-07)]
  EqualTolerance = true
  ExtensionAngle = 0
  FormatSpec = %.2w
  FormatSpecOverTolerance = %+.2w
  FormatSpecUnderTolerance = %+.2w
  Inverted = false
  LineAngle = 0
  LockPosition = false
  MeasureType = 1
  OverTolerance = 0
  References2D = -> [View002]
  Rotation = 0
  ScaleType = 0
  TheoreticalExact = false
  Type = 6
  UnderTolerance = 0
  X = 11.9045
  Y = -11.3634
FEATURE [TechDraw::DrawViewDimension] Dimension037
  AngleOverride = false
  Arbitrary = false
  ArbitraryTolerances = false
  BoxCorners = (2) [(-27.1085,-34.7491,-1e-07),(27.1085,34.7491,1e-07)]
  EqualTolerance = true
  ExtensionAngle = 0
  FormatSpec = %.2w
  FormatSpecOverTolerance = %+.2w
  FormatSpecUnderTolerance = %+.2w
  Inverted = false
  LineAngle = 0
  LockPosition = false
  MeasureType = 1
  OverTolerance = 0
  References2D = -> [View002]
  Rotation = 0
  ScaleType = 0
  TheoreticalExact = false
  Type = 0
  UnderTolerance = 0
  X = -29.9726
  Y = 50.9736
FEATURE [TechDraw::DrawViewDimension] Dimension038
  AngleOverride = false
  Arbitrary = false
  ArbitraryTolerances = false
  BoxCorners = (2) [(-27.1085,-34.7491,-1e-07),(27.1085,34.7491,1e-07)]
  EqualTolerance = true
  ExtensionAngle = 0
  FormatSpec = %.2w
  FormatSpecOverTolerance = %+.2w
  FormatSpecUnderTolerance = %+.2w
  Inverted = false
  LineAngle = 0
  LockPosition = false
  MeasureType = 1
  OverTolerance = 0
  References2D = -> [View002]
  Rotation = 0
  ScaleType = 0
  TheoreticalExact = false
  Type = 0
  UnderTolerance = 0
  X = 22.5061
  Y = 21.1672
FEATURE [TechDraw::DrawViewDimension] Dimension039
  AngleOverride = false
  Arbitrary = false
  ArbitraryTolerances = false
  BoxCorners = (2) [(-27.1085,-34.7491,-1e-07),(27.1085,34.7491,1e-07)]
  EqualTolerance = true
  ExtensionAngle = 0
  FormatSpec = %.2w
  FormatSpecOverTolerance = %+.2w
  FormatSpecUnderTolerance = %+.2w
  Inverted = false
  LineAngle = 0
  LockPosition = false
  MeasureType = 1
  OverTolerance = 0
  References2D = -> [View002]
  Rotation = 0
  ScaleType = 0
  TheoreticalExact = false
  Type = 0
  UnderTolerance = 0
  X = 25.2345
  Y = -31.3286
FEATURE [TechDraw::DrawViewDimension] Dimension040
  AngleOverride = false
  Arbitrary = false
  ArbitraryTolerances = false
  BoxCorners = (2) [(-27.1085,-34.7491,-1e-07),(27.1085,34.7491,1e-07)]
  EqualTolerance = true
  ExtensionAngle = 0
  FormatSpec = %.2w
  FormatSpecOverTolerance = %+.2w
  FormatSpecUnderTolerance = %+.2w
  Inverted = false
  LineAngle = 0
  LockPosition = false
  MeasureType = 1
  OverTolerance = 0
  References2D = -> [View002]
  Rotation = 0
  ScaleType = 0
  TheoreticalExact = false
  Type = 6
  UnderTolerance = 0
  X = -17.5035
  Y = 27.3549
FEATURE [TechDraw::DrawPage] Page001
  KeepUpdated = true
  NextBalloonIndex = 4
  ProjectionType = 0
  Template = -> Template
  Views = -> [View002,View003,Balloon,Balloon003,Balloon004,Dimension036,Dimension037,Dimension038,Dimension039,Dimension040]
FEATURE [TechDraw::DrawViewDimension] Dimension041
  AngleOverride = false
  Arbitrary = false
  ArbitraryTolerances = false
  BoxCorners = (2) [(-67.3904,-39.7929,-1e-07),(67.3904,39.7929,1e-07)]
  EqualTolerance = true
  ExtensionAngle = 0
  FormatSpec = %.2w
  FormatSpecOverTolerance = %+.2w
  FormatSpecUnderTolerance = %+.2w
  Inverted = false
  LineAngle = 0
  LockPosition = false
  MeasureType = 1
  OverTolerance = 0
  References2D = -> [View013]
  Rotation = 0
  ScaleType = 0
  TheoreticalExact = false
  Type = 6
  UnderTolerance = 0
  X = 56.1673
  Y = -18.4547
FEATURE [TechDraw::DrawViewDimension] Dimension042
  AngleOverride = false
  Arbitrary = false
  ArbitraryTolerances = false
  BoxCorners = (2) [(-103.302,-29.2459,-1e-07),(103.302,29.2459,1e-07)]
  EqualTolerance = true
  ExtensionAngle = 0
  FormatSpec = %.2w
  FormatSpecOverTolerance = %+.2w
  FormatSpecUnderTolerance = %+.2w
  Inverted = false
  LineAngle = 0
  LockPosition = false
  MeasureType = 1
  OverTolerance = 0
  References2D = -> [View012]
  Rotation = 0
  ScaleType = 0
  TheoreticalExact = false
  Type = 6
  UnderTolerance = 0
  X = 93.2785
  Y = -2.96435
FEATURE [TechDraw::DrawPage] Page004
  KeepUpdated = true
  NextBalloonIndex = 2
  ProjectionType = 0
  Template = -> Template
  Views = -> [View010,View012,View013,Dimension041,Dimension042]
FEATURE [App::DocumentObjectGroup] Group008  label="sink_Group"
  Group = -> [Page004,Unfold,Unfold_Sketch,Unfold_Sketch_Outline003,Unfold_Sketch_Internal003,Unfold_Sketch_bends]
FEATURE [TechDraw::DrawViewDimension] Dimension
  AngleOverride = false
  Arbitrary = false
  ArbitraryTolerances = false
  BoxCorners = (2) [(-27.1085,-34.7491,-1e-07),(27.1085,34.7491,1e-07)]
  EqualTolerance = true
  ExtensionAngle = 0
  FormatSpec = %.2w
  FormatSpecOverTolerance = %+.2w
  FormatSpecUnderTolerance = %+.2w
  Inverted = false
  LineAngle = 0
  LockPosition = false
  MeasureType = 1
  OverTolerance = 0
  References2D = -> [View004]
  Rotation = 0
  ScaleType = 0
  TheoreticalExact = false
  Type = 0
  UnderTolerance = 0
  X = -22.8342
  Y = -28.0083
FEATURE [TechDraw::DrawViewDimension] Dimension043
  AngleOverride = false
  Arbitrary = false
  ArbitraryTolerances = false
  BoxCorners = (2) [(-27.1085,-34.7491,-1e-07),(27.1085,34.7491,1e-07)]
  EqualTolerance = true
  ExtensionAngle = 0
  FormatSpec = %.2w
  FormatSpecOverTolerance = %+.2w
  FormatSpecUnderTolerance = %+.2w
  Inverted = false
  LineAngle = 0
  LockPosition = false
  MeasureType = 1
  OverTolerance = 0
  References2D = -> [View004]
  Rotation = 0
  ScaleType = 0
  TheoreticalExact = false
  Type = 0
  UnderTolerance = 0
  X = -13.0115
  Y = 17.9024
FEATURE [TechDraw::DrawViewDimension] Dimension044
  AngleOverride = false
  Arbitrary = false
  ArbitraryTolerances = false
  BoxCorners = (2) [(-27.1085,-34.7491,-1e-07),(27.1085,34.7491,1e-07)]
  EqualTolerance = true
  ExtensionAngle = 0
  FormatSpec = %.2w
  FormatSpecOverTolerance = %+.2w
  FormatSpecUnderTolerance = %+.2w
  Inverted = false
  LineAngle = 0
  LockPosition = false
  MeasureType = 1
  OverTolerance = 0
  References2D = -> [View004]
  Rotation = 0
  ScaleType = 0
  TheoreticalExact = false
  Type = 0
  UnderTolerance = 0
  X = 24.9988
  Y = 46.0189
FEATURE [TechDraw::DrawViewDimension] Dimension045
  AngleOverride = false
  Arbitrary = false
  ArbitraryTolerances = false
  BoxCorners = (2) [(-27.1085,-34.7491,-1e-07),(27.1085,34.7491,1e-07)]
  EqualTolerance = true
  ExtensionAngle = 0
  FormatSpec = %.2w
  FormatSpecOverTolerance = %+.2w
  FormatSpecUnderTolerance = %+.2w
  Inverted = false
  LineAngle = 0
  LockPosition = false
  MeasureType = 1
  OverTolerance = 0
  References2D = -> [View004]
  Rotation = 0
  ScaleType = 0
  TheoreticalExact = false
  Type = 6
  UnderTolerance = 0
  X = -9.28016
  Y = -4.61903
FEATURE [TechDraw::DrawViewDimension] Dimension046
  AngleOverride = false
  Arbitrary = false
  ArbitraryTolerances = false
  BoxCorners = (2) [(-27.1085,-34.7491,-1e-07),(27.1085,34.7491,1e-07)]
  EqualTolerance = true
  ExtensionAngle = 0
  FormatSpec = %.2w
  FormatSpecOverTolerance = %+.2w
  FormatSpecUnderTolerance = %+.2w
  Inverted = false
  LineAngle = 0
  LockPosition = false
  MeasureType = 1
  OverTolerance = 0
  References2D = -> [View004]
  Rotation = 0
  ScaleType = 0
  TheoreticalExact = false
  Type = 6
  UnderTolerance = 0
  X = 17.462
  Y = 23.0802
FEATURE [TechDraw::DrawPage] Page002
  KeepUpdated = true
  NextBalloonIndex = 3
  ProjectionType = 0
  Template = -> Template
  Views = -> [View004,View005,Balloon001,Dimension,Dimension043,Dimension044,Dimension045,Dimension046]
FEATURE [App::DocumentObjectGroup] Group005  label="lamp_holder_Group"
  Group = -> [Page001,Unfold002,Unfold_Sketch002,Unfold_Sketch_bends002,Part__Mirroring022,Part__Mirroring023,Page002]
FEATURE [App::DocumentObjectGroup] Group002  label="unfolds"
  Group = -> [Group004,Group005,Group007,Group008]
FEATURE [App::DocumentObjectGroup] Group  label="cuts"
  Group = -> [Group002,Group003]
note: 6 file-system paths scrubbed to <path> (originals preserved in the JSON sidecar)

RESOLVED EXTERNAL PARTS (link-assembly join: the EXTERNAL_REF files above that resolve inside this repo's crawl, each included once):
---- part ../ULZ-P03-10W.FCStd = doc fcstd_cc8d75d44389 ----
FCSTD DOCUMENT  (FreeCAD 0.22R37100 (Git))
Label: ULZ-P03-10W
License: All rights reserved
LicenseURL: http://en.wikipedia.org/wiki/All_rights_reserved
objects: Sketcher::SketchObject×1
note: 1 computed .brp shape members not serialized (recipe doc carries the construction recipe); baked Part::Feature solids carry a one-line shape summary decoded from their .brp

FEATURE [Sketcher::SketchObject] Sketch
  FullyConstrained = true
  sketch-geometry (2):
    g0: Circle CenterX=3.95 CenterY=-263 CenterZ=0 NormalX=0 NormalY=0 NormalZ=1 AngleXU=0 Radius=1.7
    g1: Circle CenterX=-3.95 CenterY=263 CenterZ=0 NormalX=0 NormalY=0 NormalZ=1 AngleXU=0 Radius=1.7
  constraints (5):
    c: Symmetric(g0,g1,g-1)
    c: DistanceY(g0,g1) = 526
    c: Equal(g0,g1)
    c: Diameter(g0) = 3.4
    c: DistanceX(g1) = -3.95
---- part ../composit_electric_shield.FCStd = doc fcstd_7e5574ddc39a (52053 chars; too large to inline — full recipe in that document) ----
---- part ../dropper.FCStd = doc fcstd_03601a3bb068 ----
FCSTD DOCUMENT  (FreeCAD 1.1R38827 (Git))
Label: dropper
License: All rights reserved
LicenseURL: http://en.wikipedia.org/wiki/All_rights_reserved
objects: Sketcher::SketchObject×9, Part::FeaturePython×4, PartDesign::Revolution×3, PartDesign::Body×2, PartDesign::CoordinateSystem×1, Spreadsheet::Sheet×1, PartDesign::SubShapeBinder×1, PartDesign::Pad×1, PartDesign::Pocket×1, PartDesign::Groove×1, App::Part×1
note: 44 computed .brp shape members not serialized (recipe doc carries the construction recipe); baked Part::Feature solids carry a one-line shape summary decoded from their .brp

FEATURE [Sketcher::SketchObject] Sketch005
  ArcFitTolerance = 0
  AttachmentSupport = -> [YZ_Plane001]
  FullyConstrained = true
  MakeInternals = false
  MapMode = 5
  Placement = pos=(0,0,0) rot=(0.57735,0.57735,0.57735;2.0944rad)
  sketch-geometry (14):
    g0: LineSegment StartX=11.3 StartY=0 StartZ=0 EndX=11.3 EndY=1 EndZ=0
    g1: LineSegment StartX=11.3 StartY=1 StartZ=0 EndX=10.7 EndY=1 EndZ=0
    g2: LineSegment StartX=10.7 StartY=1 StartZ=0 EndX=10.7 EndY=9.9 EndZ=0
    g3: LineSegment StartX=10.7 StartY=9.9 StartZ=0 EndX=6.6 EndY=9.9 EndZ=0
    g4: LineSegment StartX=6.6 StartY=9.9 StartZ=0 EndX=6.6 EndY=3 EndZ=0
    g5: LineSegment StartX=6.6 StartY=3 StartZ=0 EndX=2.5 EndY=3 EndZ=0
    g6: LineSegment StartX=2.5 StartY=3 StartZ=0 EndX=2.5 EndY=20 EndZ=0
    g7: LineSegment StartX=2.5 StartY=20 StartZ=0 EndX=1.45 EndY=20 EndZ=0
    g8: LineSegment StartX=1.45 StartY=20 StartZ=0 EndX=1.45 EndY=2.5 EndZ=0
    g9: LineSegment StartX=1.45 StartY=2.5 StartZ=0 EndX=7 EndY=-0.6 EndZ=0
    g10: LineSegment StartX=7 StartY=-0.6 StartZ=0 EndX=7 EndY=8.85 EndZ=0
    g11: LineSegment StartX=7 StartY=8.85 StartZ=0 EndX=9.5 EndY=8.85 EndZ=0
    g12: LineSegment StartX=9.5 StartY=8.85 StartZ=0 EndX=9.5 EndY=0 EndZ=0
    g13: LineSegment StartX=9.5 StartY=0 StartZ=0 EndX=11.3 EndY=0 EndZ=0
  constraints (43):
    c: PointOnObject(g0,g-1)
    c: Vertical(g0)
    c: Coincident(g0,g1)
    c: Horizontal(g1)
    c: Coincident(g1,g2)
    c: Vertical(g2)
    c: Coincident(g2,g3)
    c: Horizontal(g3)
    c: Coincident(g3,g4)
    c: Vertical(g4)
    c: Coincident(g4,g5)
    c: Coincident(g5,g6)
    c: Vertical(g6)
    c: Coincident(g6,g7)
    c: Horizontal(g7)
    c: Coincident(g7,g8)
    c: Vertical(g8)
    c: Coincident(g8,g9)
    c: Coincident(g9,g10)
    c: Vertical(g10)
    c: Coincident(g10,g11)
    c: Horizontal(g11)
    c: Coincident(g11,g12)
    c: Vertical(g12)
    c: Coincident(g12,g13)
    c: Coincident(g13,g0)
    c: Horizontal(g13)
    c: DistanceX(g0) = 11.3  'outer_r'
    c: DistanceY(g0) = 1
    c: DistanceY(g2) = 9.9
    c: DistanceX(g1,g0) = 0.6
    c: DistanceX(g3,g2) = 4.1
    c: DistanceY(g4,g3) = 6.9
    c: DistanceX(g6) = 2.5
    c: DistanceX(g7) = 1.45
    c: DistanceY(g9,g3) = 10.5
    c: DistanceX(g12,g0) = 1.8
    c: DistanceY(g11) = 8.85
    c: DistanceX(g9) = 7
    c: DistanceY(g9,g6) = 20.6
    c: Horizontal(g5)
    c: DistanceY(g8,g5) = 0.5
    c: DistanceY(g7) = 20
FEATURE [PartDesign::Revolution] Revolution002
  Angle = 360
  Angle2 = 60
  Axis = (0,0,1)
  Base = (0,0,0)
  Placement = pos=(0,0,0) rot=(1,1,1;2.0944rad)
  Profile = -> Sketch005
  ReferenceAxis = -> Sketch005 [V_Axis]
  Reversed = true
  Suppressed = false
  Type = 0
FEATURE [Sketcher::SketchObject] Sketch006
  ArcFitTolerance = 0
  AttachmentSupport = -> [YZ_Plane001]
  FullyConstrained = true
  MakeInternals = false
  MapMode = 5
  Placement = pos=(0,0,0) rot=(0.57735,0.57735,0.57735;2.0944rad)
  expr: Constraints[27] = Sketch005.Constraints.outer_r
  expr: Constraints[28] = Sketch005.Constraints[28]
  expr: Constraints[29] = Sketch005.Constraints[29]
  expr: Constraints[30] = Sketch005.Constraints[30]
  expr: Constraints[31] = Sketch005.Constraints[31]
  expr: Constraints[32] = Sketch005.Constraints[32]
  expr: Constraints[33] = Sketch005.Constraints[33]
  expr: Constraints[34] = Sketch005.Constraints[34]
  expr: Constraints[35] = Sketch005.Constraints[35]
  expr: Constraints[36] = Sketch005.Constraints[36]
  expr: Constraints[37] = Sketch005.Constraints[37]
  expr: Constraints[38] = Sketch005.Constraints[38]
  expr: Constraints[39] = Sketch005.Constraints[39]
  expr: Constraints[41] = Sketch005.Constraints[41]
  expr: Constraints[69] = Sketch005.Constraints.outer_r
  expr: Constraints[70] = Sketch005.Constraints[28]
  expr: Constraints[71] = Sketch005.Constraints[29]
  expr: Constraints[72] = Sketch005.Constraints[30]
  expr: Constraints[73] = Sketch005.Constraints[31]
  expr: Constraints[74] = Sketch005.Constraints[32]
  expr: Constraints[75] = Sketch005.Constraints[33]
  expr: Constraints[76] = Sketch005.Constraints[34]
  expr: Constraints[77] = Sketch005.Constraints[35]
  expr: Constraints[78] = Sketch005.Constraints[36]
  expr: Constraints[79] = Sketch005.Constraints[37]
  expr: Constraints[80] = Sketch005.Constraints[38]
  expr: Constraints[81] = Sketch005.Constraints[39]
  expr: Constraints[83] = Sketch005.Constraints[41]
  sketch-geometry (32):
    g0: LineSegment [constr] StartX=11.3 StartY=0 StartZ=0 EndX=11.3 EndY=1 EndZ=0
    g1: LineSegment [constr] StartX=11.3 StartY=1 StartZ=0 EndX=10.7 EndY=1 EndZ=0
    g2: LineSegment [constr] StartX=10.7 StartY=1 StartZ=0 EndX=10.7 EndY=9.9 EndZ=0
    g3: LineSegment [constr] StartX=10.7 StartY=9.9 StartZ=0 EndX=6.6 EndY=9.9 EndZ=0
    g4: LineSegment StartX=6.6 StartY=9.9 StartZ=0 EndX=6.6 EndY=3 EndZ=0
    g5: LineSegment StartX=6.6 StartY=3 StartZ=0 EndX=2.5 EndY=3 EndZ=0
    g6: LineSegment [constr] StartX=2.5 StartY=3 StartZ=0 EndX=2.5 EndY=20 EndZ=0
    g7: LineSegment [constr] StartX=2.5 StartY=20 StartZ=0 EndX=1.45 EndY=20 EndZ=0
    g8: LineSegment [constr] StartX=1.45 StartY=20 StartZ=0 EndX=1.45 EndY=2.5 EndZ=0
    g9: LineSegment [constr] StartX=1.45 StartY=2.5 StartZ=0 EndX=7 EndY=-0.6 EndZ=0
    g10: LineSegment [constr] StartX=7 StartY=-0.6 StartZ=0 EndX=7 EndY=8.85 EndZ=0
    g11: LineSegment [constr] StartX=7 StartY=8.85 StartZ=0 EndX=9.5 EndY=8.85 EndZ=0
    g12: LineSegment [constr] StartX=9.5 StartY=8.85 StartZ=0 EndX=9.5 EndY=0 EndZ=0
    g13: LineSegment [constr] StartX=9.5 StartY=0 StartZ=0 EndX=11.3 EndY=0 EndZ=0
    g14: LineSegment [constr] StartX=11.3 StartY=0 StartZ=0 EndX=11.3 EndY=1 EndZ=0
    g15: LineSegment [constr] StartX=11.3 StartY=1 StartZ=0 EndX=10.7 EndY=1 EndZ=0
    g16: LineSegment [constr] StartX=10.7 StartY=1 StartZ=0 EndX=10.7 EndY=9.9 EndZ=0
    g17: LineSegment [constr] StartX=10.7 StartY=9.9 StartZ=0 EndX=6.6 EndY=9.9 EndZ=0
    g18: LineSegment [constr] StartX=6.6 StartY=9.9 StartZ=0 EndX=6.6 EndY=3 EndZ=0
    g19: LineSegment [constr] StartX=6.6 StartY=3 StartZ=0 EndX=2.5 EndY=3 EndZ=0
    g20: LineSegment [constr] StartX=2.5 StartY=3 StartZ=0 EndX=2.5 EndY=20 EndZ=0
    g21: LineSegment [constr] StartX=2.5 StartY=20 StartZ=0 EndX=1.45 EndY=20 EndZ=0
    g22: LineSegment [constr] StartX=1.45 StartY=20 StartZ=0 EndX=1.45 EndY=2.5 EndZ=0
    g23: LineSegment [constr] StartX=1.45 StartY=2.5 StartZ=0 EndX=7 EndY=-0.6 EndZ=0
    g24: LineSegment [constr] StartX=7 StartY=-0.6 StartZ=0 EndX=7 EndY=8.85 EndZ=0
    g25: LineSegment [constr] StartX=7 StartY=8.85 StartZ=0 EndX=9.5 EndY=8.85 EndZ=0
    g26: LineSegment [constr] StartX=9.5 StartY=8.85 StartZ=0 EndX=9.5 EndY=0 EndZ=0
    g27: LineSegment [constr] StartX=9.5 StartY=0 StartZ=0 EndX=11.3 EndY=0 EndZ=0
    g28: LineSegment StartX=2.5 StartY=3 StartZ=0 EndX=2.04763 EndY=3 EndZ=0
    g29: LineSegment StartX=2.04763 StartY=3 StartZ=0 EndX=2.04763 EndY=12.6758 EndZ=0
    g30: LineSegment StartX=2.04763 StartY=12.6758 StartZ=0 EndX=6.6 EndY=9.9 EndZ=0
    g31: GeomPoint [constr] X=2.5 Y=12.4 Z=0
  constraints (94):
    c: PointOnObject(g0,g-1)
    c: Vertical(g0)
    c: Coincident(g0,g1)
    c: Horizontal(g1)
    c: Coincident(g1,g2)
    c: Vertical(g2)
    c: Coincident(g2,g3)
    c: Horizontal(g3)
    c: Coincident(g3,g4)
    c: Vertical(g4)
    c: Coincident(g4,g5)
    c: Coincident(g5,g6)
    c: Vertical(g6)
    c: Coincident(g6,g7)
    c: Horizontal(g7)
    c: Coincident(g7,g8)
    c: Vertical(g8)
    c: Coincident(g8,g9)
    c: Coincident(g9,g10)
    c: Vertical(g10)
    c: Coincident(g10,g11)
    c: Horizontal(g11)
    c: Coincident(g11,g12)
    c: Vertical(g12)
    c: Coincident(g12,g13)
    c: Coincident(g13,g0)
    c: Horizontal(g13)
    c: DistanceX(g0) = 11.3
    c: DistanceY(g0) = 1
    c: DistanceY(g2) = 9.9
    c: DistanceX(g1,g0) = 0.6
    c: DistanceX(g3,g2) = 4.1
    c: DistanceY(g4,g3) = 6.9
    c: DistanceX(g6) = 2.5
    c: DistanceX(g7) = 1.45
    c: DistanceY(g9,g3) = 10.5
    c: DistanceX(g12,g0) = 1.8
    c: DistanceY(g11) = 8.85
    c: DistanceX(g9) = 7
    c: DistanceY(g9,g6) = 20.6
    c: Horizontal(g5)
    c: DistanceY(g8,g5) = 0.5
    c: PointOnObject(g14,g-1)
    c: Vertical(g14)
    c: Coincident(g14,g15)
    c: Horizontal(g15)
    c: Coincident(g15,g16)
    c: Vertical(g16)
    c: Coincident(g16,g17)
    c: Horizontal(g17)
    c: Coincident(g17,g18)
    c: Vertical(g18)
    c: Coincident(g18,g19)
    c: Coincident(g19,g20)
    c: Vertical(g20)
    c: Coincident(g20,g21)
    c: Horizontal(g21)
    c: Coincident(g21,g22)
    c: Vertical(g22)
    c: Coincident(g22,g23)
    c: Coincident(g23,g24)
    c: Vertical(g24)
    c: Coincident(g24,g25)
    c: Horizontal(g25)
    c: Coincident(g25,g26)
    c: Vertical(g26)
    c: Coincident(g26,g27)
    c: Coincident(g27,g14)
    c: Horizontal(g27)
    c: DistanceX(g14) = 11.3
    c: DistanceY(g14) = 1
    c: DistanceY(g16) = 9.9
    c: DistanceX(g15,g14) = 0.6
    c: DistanceX(g17,g16) = 4.1
    c: DistanceY(g18,g17) = 6.9
    c: DistanceX(g20) = 2.5
    c: DistanceX(g21) = 1.45
    c: DistanceY(g23,g17) = 10.5
    c: DistanceX(g26,g14) = 1.8
    c: DistanceY(g25) = 8.85
    c: DistanceX(g23) = 7
    c: DistanceY(g23,g20) = 20.6
    c: Horizontal(g19)
    c: DistanceY(g22,g19) = 0.5
    c: Coincident(g28,g5)
    c: Horizontal(g28)
    c: Coincident(g29,g28)
    c: Vertical(g29)
    c: Coincident(g30,g29)
    c: Coincident(g30,g4)
    c: PointOnObject(g31,g30)
    c: PointOnObject(g31,g6)
    c: DistanceY(g4,g31) = 2.5
    c: DistanceX(g29,g31) = 0.452366
FEATURE [PartDesign::Body] Body001
  AllowCompound = false
  Group = -> [Sketch005,Revolution002,Sketch006]
  Origin = -> Origin001
  Placement = pos=(0,0,2.5) rot=(0,0,1;0rad)
  Tip = -> Revolution002
FEATURE [Sketcher::SketchObject] Sketch007  label="base"
  ArcFitTolerance = 0
  FullyConstrained = true
  MakeInternals = false
  expr: .Constraints.r = Sketch005.Constraints.outer_r + 0.5 mm
  sketch-geometry (1):
    g0: Circle CenterX=0 CenterY=0 CenterZ=0 NormalX=0 NormalY=0 NormalZ=1 AngleXU=0 Radius=11.8
  constraints (2):
    c: Coincident(g0,g-1)
    c: Radius(g0) = 11.8  'r'
FEATURE [Sketcher::SketchObject] Sketch002
  ArcFitTolerance = 0
  AttachmentSupport = -> [YZ_Plane]
  FullyConstrained = true
  MakeInternals = false
  MapMode = 5
  Placement = pos=(0,0,0) rot=(0.57735,0.57735,0.57735;2.0944rad)
  expr: Constraints[18] = Sketch001.Constraints[18]
  expr: Constraints[19] = Sketch001.Constraints[19]
  expr: Constraints[20] = Sketch001.Constraints[20]
  expr: Constraints[21] = Sketch001.Constraints[21]
  expr: Constraints[22] = Sketch001.Constraints[22]
  expr: Constraints[23] = Sketch001.Constraints[23]
  expr: Constraints[24] = Sketch001.Constraints[24]
  expr: Constraints[25] = Sketch001.Constraints[25]
  expr: Constraints[27] = Sketch001.Constraints[27]
  sketch-geometry (13):
    g0: LineSegment [constr] StartX=1.15 StartY=0 StartZ=0 EndX=1.15 EndY=-18.1612 EndZ=0
    g1: LineSegment StartX=1.15 StartY=-18.1612 StartZ=0 EndX=2.765 EndY=-8.77 EndZ=0
    g2: LineSegment [constr] StartX=2.765 StartY=-8.77 StartZ=0 EndX=2.2 EndY=-8.77 EndZ=0
    g3: LineSegment [constr] StartX=2.2 StartY=-8.77 StartZ=0 EndX=2.2 EndY=-5.32 EndZ=0
    g4: LineSegment [constr] StartX=2.2 StartY=-5.32 StartZ=0 EndX=3.35 EndY=-5.32 EndZ=0
    g5: LineSegment [constr] StartX=3.35 StartY=-5.32 StartZ=0 EndX=3.35 EndY=-3.66 EndZ=0
    g6: LineSegment [constr] StartX=3.35 StartY=-3.66 StartZ=0 EndX=2.65 EndY=-3.66 EndZ=0
    g7: LineSegment [constr] StartX=2.65 StartY=-3.66 StartZ=0 EndX=2.65 EndY=0 EndZ=0
    g8: LineSegment [constr] StartX=2.65 StartY=0 StartZ=0 EndX=1.15 EndY=0 EndZ=0
    g9: GeomPoint [constr] X=-2.765 Y=-8.77 Z=0
    g10: GeomPoint [constr] X=-2.765 Y=-8.77 Z=0
    g11: LineSegment StartX=1.15 StartY=-18.1612 StartZ=0 EndX=-3.0574 EndY=-18.1612 EndZ=0
    g12: LineSegment StartX=-3.0574 StartY=-18.1612 StartZ=0 EndX=2.765 EndY=-8.77 EndZ=0
  constraints (34):
    c: PointOnObject(g0,g-1)
    c: Vertical(g0)
    c: Coincident(g0,g1)
    c: Coincident(g1,g2)
    c: Horizontal(g2)
    c: Coincident(g2,g3)
    c: Vertical(g3)
    c: Coincident(g3,g4)
    c: Horizontal(g4)
    c: Coincident(g4,g5)
    c: Vertical(g5)
    c: Coincident(g5,g6)
    c: Horizontal(g6)
    c: Coincident(g6,g7)
    c: PointOnObject(g7,g-1)
    c: Vertical(g7)
    c: Coincident(g7,g8)
    c: Coincident(g8,g0)
    c: DistanceY(g2,g3) = 3.45
    c: DistanceY(g4,g5) = 1.66
    c: DistanceY(g6,g7) = 3.66
    c: DistanceX(g2) = 2.2
    c: DistanceX(g4) = 3.35
    c: DistanceX(g0) = 1.15
    c: DistanceX(g7) = 2.65
    c: DistanceX(g1) = 2.765
    c: Symmetric(g9,g1,g-2)
    c: Distance(g9,g1) = 5.45
    c: Symmetric(g10,g1,g-2)
    c: Coincident(g11,g1)
    c: Horizontal(g11)
    c: Coincident(g12,g11)
    c: Coincident(g12,g1)
    c: Distance(g9,g12) = 4.7
FEATURE [Sketcher::SketchObject] Sketch001
  ArcFitTolerance = 0
  AttachmentSupport = -> [XZ_Plane]
  FullyConstrained = true
  MakeInternals = false
  MapMode = 5
  Placement = pos=(0,0,0) rot=(1,0,0;1.5708rad)
  sketch-geometry (10):
    g0: LineSegment StartX=1.15 StartY=0 StartZ=0 EndX=1.15 EndY=-18.1612 EndZ=0
    g1: LineSegment StartX=1.15 StartY=-18.1612 StartZ=0 EndX=2.765 EndY=-8.77 EndZ=0
    g2: LineSegment StartX=2.765 StartY=-8.77 StartZ=0 EndX=2.2 EndY=-8.77 EndZ=0
    g3: LineSegment StartX=2.2 StartY=-8.77 StartZ=0 EndX=2.2 EndY=-5.32 EndZ=0
    g4: LineSegment StartX=2.2 StartY=-5.32 StartZ=0 EndX=3.35 EndY=-5.32 EndZ=0
    g5: LineSegment StartX=3.35 StartY=-5.32 StartZ=0 EndX=3.35 EndY=-3.66 EndZ=0
    g6: LineSegment StartX=3.35 StartY=-3.66 StartZ=0 EndX=2.65 EndY=-3.66 EndZ=0
    g7: LineSegment StartX=2.65 StartY=-3.66 StartZ=0 EndX=2.65 EndY=0 EndZ=0
    g8: LineSegment StartX=2.65 StartY=0 StartZ=0 EndX=1.15 EndY=0 EndZ=0
    g9: GeomPoint [constr] X=-2.765 Y=-8.77 Z=0
  constraints (28):
    c: PointOnObject(g0,g-1)
    c: Vertical(g0)
    c: Coincident(g0,g1)
    c: Coincident(g1,g2)
    c: Horizontal(g2)
    c: Coincident(g2,g3)
    c: Vertical(g3)
    c: Coincident(g3,g4)
    c: Horizontal(g4)
    c: Coincident(g4,g5)
    c: Vertical(g5)
    c: Coincident(g5,g6)
    c: Horizontal(g6)
    c: Coincident(g6,g7)
    c: PointOnObject(g7,g-1)
    c: Vertical(g7)
    c: Coincident(g7,g8)
    c: Coincident(g8,g0)
    c: DistanceY(g2,g3) = 3.45
    c: DistanceY(g4,g5) = 1.66
    c: DistanceY(g6,g7) = 3.66
    c: DistanceX(g2) = 2.2
    c: DistanceX(g4) = 3.35
    c: DistanceX(g0) = 1.15
    c: DistanceX(g7) = 2.65
    c: DistanceX(g1) = 2.765
    c: Symmetric(g9,g1,g-2)
    c: Distance(g9,g1) = 5.45
FEATURE [Sketcher::SketchObject] Sketch  label="fix_sketch"
  ArcFitTolerance = 0
  AttachmentSupport = -> [XY_Plane]
  FullyConstrained = true
  MakeInternals = false
  MapMode = 5
  sketch-geometry (5):
    g0: ArcOfCircle CenterX=0 CenterY=0 CenterZ=0 NormalX=0 NormalY=0 NormalZ=1 AngleXU=0 Radius=10.5 StartAngle=0.496317 EndAngle=1.5708
    g1: ArcOfCircle CenterX=16.5 CenterY=0 CenterZ=0 NormalX=0 NormalY=0 NormalZ=1 AngleXU=0 Radius=3.25 StartAngle=0 EndAngle=1.34547
    g2: LineSegment StartX=17.2261 StartY=3.16784 StartZ=0 EndX=9.23309 EndY=5 EndZ=0
    g3: GeomPoint [constr] X=-19.75 Y=0 Z=0
    g4: GeomPoint [constr] X=0 Y=-10.5 Z=0
  constraints (14):
    c: PointOnObject(g0,g-2)
    c: PointOnObject(g1,g-1)
    c: PointOnObject(g1,g-1)
    c: Coincident(g2,g0)
    c: Tangent(g2,g1) = -1.5708
    c: Diameter(g0) = 21
    c: DistanceX(g1) = 19.75
    c: DistanceY(g0) = 5
    c: Diameter(g1) = 6.5
    c: Coincident(g0,g-1)
    c: Symmetric(g3,g1,g-2)
    c: DistanceX(g3,g1) = 39.5  'length'
    c: Symmetric(g4,g0,g-1)
    c: DistanceY(g4,g0) = 21  'width'
FEATURE [Sketcher::SketchObject] Sketch004
  ArcFitTolerance = 0
  AttachmentSupport = -> [YZ_Plane]
  FullyConstrained = true
  MakeInternals = false
  MapMode = 5
  Placement = pos=(0,0,0) rot=(0.57735,0.57735,0.57735;2.0944rad)
  expr: Constraints[3] = Sketch003.Constraints[9]
  sketch-geometry (6):
    g0: LineSegment StartX=7.75 StartY=10.9 StartZ=0 EndX=0 EndY=10.9 EndZ=0
    g1: LineSegment StartX=0 StartY=10.9 StartZ=0 EndX=0 EndY=1.5 EndZ=0
    g2: LineSegment StartX=0 StartY=1.5 StartZ=0 EndX=7.25 EndY=1.5 EndZ=0
    g3: LineSegment StartX=7.25 StartY=1.5 StartZ=0 EndX=7.25 EndY=2.5 EndZ=0
    g4: LineSegment StartX=7.25 StartY=2.5 StartZ=0 EndX=7.75 EndY=4 EndZ=0
    g5: LineSegment StartX=7.75 StartY=4 StartZ=0 EndX=7.75 EndY=10.9 EndZ=0
  constraints (18):
    c: Coincident(g0,g1)
    c: Horizontal(g0)
    c: Vertical(g1)
    c: DistanceY(g0) = 10.9
    c: Horizontal(g2)
    c: Coincident(g2,g3)
    c: Vertical(g3)
    c: Coincident(g3,g4)
    c: Coincident(g4,g5)
    c: Vertical(g5)
    c: Coincident(g0,g5)
    c: Coincident(g1,g2)
    c: DistanceY(g1,g0) = 9.4
    c: DistanceX(g0) = 7.75
    c: DistanceY(g2,g3) = 1
    c: DistanceY(g3,g4) = 1.5
    c: DistanceX(g2,g4) = 0.5
    c: Vertical(g1,g-1)
FEATURE [Sketcher::SketchObject] Sketch003
  ArcFitTolerance = 0
  AttachmentSupport = -> [YZ_Plane]
  FullyConstrained = true
  MakeInternals = false
  MapMode = 5
  Placement = pos=(0,0,0) rot=(0.57735,0.57735,0.57735;2.0944rad)
  sketch-geometry (4):
    g0: LineSegment StartX=0 StartY=0 StartZ=0 EndX=8.825 EndY=0 EndZ=0
    g1: LineSegment StartX=8.825 StartY=0 StartZ=0 EndX=8.825 EndY=10.9 EndZ=0
    g2: LineSegment StartX=8.825 StartY=10.9 StartZ=0 EndX=0 EndY=10.9 EndZ=0
    g3: LineSegment StartX=0 StartY=10.9 StartZ=0 EndX=0 EndY=0 EndZ=0
  constraints (11):
    c: Coincident(g0,g1)
    c: Coincident(g1,g2)
    c: Coincident(g2,g3)
    c: Coincident(g3,g0)
    c: Horizontal(g0)
    c: Horizontal(g2)
    c: Vertical(g1)
    c: Vertical(g3)
    c: Coincident(g0,g-1)
    c: DistanceY(g2) = 10.9
    c: DistanceX(g0) = 8.825
FEATURE [PartDesign::CoordinateSystem] LCS_0
  AttacherType = Attacher::AttachEngine3D
  AttachmentOffset = pos=(0,0,2.45) rot=(0,0,1;0rad)
  AttachmentSupport = -> [X_Axis002]
  MapMode = 2
  Placement = pos=(0,0,2.45) rot=(0,0,1;0rad)
FEATURE [Spreadsheet::Sheet] Spreadsheet  label="Properties"
  cells = B2(top_d)==22.6 mm; C2(bot_d)==21 mm; D2(top_height)==20 mm; E2(bot_base_height)==2.4 mm; F2(total_height)==22.4 mm; G2(total_width)==38.9 mm
FEATURE [Part::FeaturePython] Mirror  label="Mirror of Sketch"  # WARN: FeaturePython — macro-defined, semantics opaque (R4)
  ExposePlacement = false
  FlipX = true
  FlipY = false
  FlipZ = false
  MarkerShape = 1
  MarkerSize = 0
  NumElements = 0
  Object = -> Sketch
  ObjectTraversal = 0
  Type = lattice2Mirror.LatticeMirror
  isLattice = 0
FEATURE [Part::FeaturePython] Mirror001  label="Mirror001 of Mirror of Sketch"  # WARN: FeaturePython — macro-defined, semantics opaque (R4)
  ExposePlacement = false
  FlipX = false
  FlipY = true
  FlipZ = false
  MarkerShape = 1
  MarkerSize = 0
  NumElements = 0
  Object = -> Mirror
  ObjectTraversal = 0
  Type = lattice2Mirror.LatticeMirror
  isLattice = 0
FEATURE [Part::FeaturePython] Mirror002  label="Mirror002 of Mirror001 of Mirror of Sketch"  # WARN: FeaturePython — macro-defined, semantics opaque (R4)
  ExposePlacement = false
  FlipX = true
  FlipY = false
  FlipZ = false
  MarkerShape = 1
  MarkerSize = 0
  NumElements = 0
  Object = -> Mirror001
  ObjectTraversal = 0
  Type = lattice2Mirror.LatticeMirror
  isLattice = 0
FEATURE [PartDesign::SubShapeBinder] Binder
  BindCopyOnChange = 0
  BindMode = 0
  ClaimChildren = true
  Context = -> Part [Body.Binder.]
  Fuse = false
  MakeFace = true
  OffsetFill = false
  OffsetIntersection = false
  OffsetJoinType = 0
  OffsetOpenResult = false
  PartialLoad = false
  Relative = true
  Support = -> [Connect]
  _Version = 2
FEATURE [PartDesign::Pad] Pad
  Direction = (0,0,1)
  Length = 2.45
  Length2 = 10
  Profile = -> Binder
  Suppressed = false
  Type = 0
FEATURE [PartDesign::Revolution] Revolution
  Angle = 360
  Angle2 = 60
  Axis = (0,2e-16,1)
  Base = (0,0,0)
  BaseFeature = -> Pad
  Profile = -> Sketch001
  ReferenceAxis = -> Sketch001 [V_Axis]
  Reversed = true
  Suppressed = false
  Type = 0
FEATURE [PartDesign::Pocket] Pocket
  BaseFeature = -> Revolution
  Direction = (-1,0,0)
  Length = 5
  Length2 = 5
  Midplane = true
  Profile = -> Sketch002
  ReferenceAxis = -> Sketch002 [N_Axis]
  Suppressed = false
  Type = 1
FEATURE [PartDesign::Revolution] Revolution001
  Angle = 360
  Angle2 = 60
  Axis = (0,0,1)
  Base = (0,0,0)
  BaseFeature = -> Pocket
  Profile = -> Sketch003
  ReferenceAxis = -> Sketch003 [V_Axis]
  Reversed = true
  Suppressed = false
  Type = 0
FEATURE [PartDesign::Groove] Groove
  Angle = 360
  Angle2 = 60
  Axis = (0,0,1)
  Base = (0,0,0)
  BaseFeature = -> Revolution001
  Profile = -> Sketch004
  ReferenceAxis = -> Sketch004 [V_Axis]
  Suppressed = false
  Type = 0
FEATURE [Sketcher::SketchObject] Sketch008  label="feed"
  ArcFitTolerance = 0
  AttachmentSupport = -> [XY_Plane]
  FullyConstrained = true
  MakeInternals = false
  MapMode = 5
  sketch-geometry (1):
    g0: Circle CenterX=0 CenterY=0 CenterZ=0 NormalX=0 NormalY=0 NormalZ=1 AngleXU=0 Radius=4
  constraints (2):
    c: Coincident(g0,g-1)
    c: Diameter(g0) = 8
FEATURE [PartDesign::Body] Body
  AllowCompound = false
  Group = -> [Sketch,Pad,Sketch001,Revolution,Sketch002,Pocket,Sketch003,Sketch004,Revolution001,Groove,Sketch008,Binder]
  Origin = -> Origin
  Tip = -> Groove
FEATURE [App::Part] Part  label="dropper"
  Group = -> [LCS_0,Body001,Body]
  Origin = -> Origin002
FEATURE [Part::FeaturePython] Connect  label="fix"  # WARN: FeaturePython — macro-defined, semantics opaque (R4)
  Objects = -> [Sketch,Mirror002,Mirror001,Mirror]
  Tolerance = 0
---- part ../magnet_fix.FCStd = doc fcstd_efc328589249 ----
FCSTD DOCUMENT  (FreeCAD 0.22R37100 (Git))
Label: magnet_fix
License: All rights reserved
LicenseURL: http://en.wikipedia.org/wiki/All_rights_reserved
objects: Sketcher::SketchObject×10, PartDesign::SubShapeBinder×4, PartDesign::Pad×4, TechDraw::DrawViewDimension×3, PartDesign::Body×2, TechDraw::DrawViewPart×2, PartDesign::Pocket×1, Spreadsheet::Sheet×1, PartDesign::CoordinateSystem×1, PartDesign::LinearPattern×1, Part::Mirroring×1, Part::FeaturePython×1, Part::Extrusion×1, Part::Compound×1, PartDesign::Boolean×1, Part::Feature×1, TechDraw::DrawSVGTemplate×1, TechDraw::DrawPage×1
note: 39 computed .brp shape members not serialized (recipe doc carries the construction recipe); baked Part::Feature solids carry a one-line shape summary decoded from their .brp

FEATURE [Sketcher::SketchObject] Sketch
  FullyConstrained = true
  sketch-geometry (5):
    g0: LineSegment StartX=-20.65 StartY=-7.3 StartZ=0 EndX=20.65 EndY=-7.3 EndZ=0
    g1: LineSegment StartX=20.65 StartY=-7.3 StartZ=0 EndX=20.65 EndY=7.3 EndZ=0
    g2: LineSegment StartX=20.65 StartY=7.3 StartZ=0 EndX=-20.65 EndY=7.3 EndZ=0
    g3: LineSegment StartX=-20.65 StartY=7.3 StartZ=0 EndX=-20.65 EndY=-7.3 EndZ=0
    g4: GeomPoint X=0 Y=0 Z=0
  constraints (12):
    c: Coincident(g0,g1)
    c: Coincident(g1,g2)
    c: Coincident(g2,g3)
    c: Coincident(g3,g0)
    c: Horizontal(g0)
    c: Horizontal(g2)
    c: Vertical(g1)
    c: Vertical(g3)
    c: Symmetric(g2,g0,g4)
    c: Coincident(g4,g-1)
    c: DistanceX(g0,g1) = 41.3
    c: DistanceY(g0,g1) = 14.6
FEATURE [Sketcher::SketchObject] Sketch001
  ExternalGeometry = -> [Sketch]
  FullyConstrained = true
  sketch-geometry (5):
    g0: LineSegment StartX=-14.1 StartY=-7.3 StartZ=0 EndX=14.1 EndY=-7.3 EndZ=0
    g1: LineSegment StartX=14.1 StartY=-7.3 StartZ=0 EndX=14.1 EndY=7.3 EndZ=0
    g2: LineSegment StartX=14.1 StartY=7.3 StartZ=0 EndX=-14.1 EndY=7.3 EndZ=0
    g3: LineSegment StartX=-14.1 StartY=7.3 StartZ=0 EndX=-14.1 EndY=-7.3 EndZ=0
    g4: GeomPoint X=0 Y=0 Z=0
  constraints (12):
    c: Coincident(g0,g1)
    c: Coincident(g1,g2)
    c: Coincident(g2,g3)
    c: Coincident(g3,g0)
    c: Horizontal(g0)
    c: Horizontal(g2)
    c: Vertical(g1)
    c: Vertical(g3)
    c: Symmetric(g2,g0,g4)
    c: Coincident(g4,g-1)
    c: Horizontal(g1,g-3)
    c: DistanceX(g2,g2) = 28.2
FEATURE [Sketcher::SketchObject] Sketch002  label="holes"
  FullyConstrained = true
  sketch-geometry (10):
    g0: ArcOfCircle CenterX=17 CenterY=-1.85 CenterZ=0 NormalX=0 NormalY=0 NormalZ=1 AngleXU=0 Radius=1.4 StartAngle=3.14159 EndAngle=6.28319
    g1: ArcOfCircle CenterX=17 CenterY=1.85 CenterZ=0 NormalX=0 NormalY=0 NormalZ=1 AngleXU=0 Radius=1.4 StartAngle=0 EndAngle=3.14159
    g2: LineSegment StartX=15.6 StartY=-1.85 StartZ=0 EndX=15.6 EndY=1.85 EndZ=0
    g3: LineSegment StartX=18.4 StartY=-1.85 StartZ=0 EndX=18.4 EndY=1.85 EndZ=0
    g4: ArcOfCircle CenterX=-17 CenterY=-1.85 CenterZ=0 NormalX=0 NormalY=0 NormalZ=1 AngleXU=0 Radius=1.4 StartAngle=3.14159 EndAngle=6.28319
    g5: ArcOfCircle CenterX=-17 CenterY=1.85 CenterZ=0 NormalX=0 NormalY=0 NormalZ=1 AngleXU=0 Radius=1.4 StartAngle=0 EndAngle=3.14159
    g6: LineSegment StartX=-18.4 StartY=-1.85 StartZ=0 EndX=-18.4 EndY=1.85 EndZ=0
    g7: LineSegment StartX=-15.6 StartY=-1.85 StartZ=0 EndX=-15.6 EndY=1.85 EndZ=0
    g8: GeomPoint X=17 Y=-3.25 Z=0
    g9: GeomPoint X=17 Y=3.25 Z=0
  constraints (22):
    c: Tangent(g0,g2) = 1.5708
    c: Tangent(g0,g3) = -1.5708
    c: Tangent(g1,g2) = 1.5708
    c: Tangent(g1,g3) = -1.5708
    c: Equal(g0,g1)
    c: Vertical(g3)
    c: Tangent(g4,g6) = 1.5708
    c: Tangent(g4,g7) = -1.5708
    c: Tangent(g5,g6) = 1.5708
    c: Tangent(g5,g7) = -1.5708
    c: Equal(g4,g5)
    c: Vertical(g6)
    c: PointOnObject(g8,g0)
    c: PointOnObject(g9,g1)
    c: Vertical(g9,g0)
    c: Symmetric(g8,g9,g-1)
    c: DistanceY(g8,g9) = 6.5
    c: DistanceX(g0,g0) = 2.8
    c: Symmetric(g4,g1,g-1)
    c: Equal(g7,g2)
    c: Equal(g5,g1)
    c: DistanceX(g4,g0) = 34
FEATURE [PartDesign::SubShapeBinder] Binder
  BindCopyOnChange = 0
  BindMode = 0
  ClaimChildren = false
  Context = -> Body [Binder.]
  Fuse = false
  MakeFace = true
  OffsetFill = false
  OffsetIntersection = false
  OffsetJoinType = 0
  OffsetOpenResult = false
  PartialLoad = false
  Relative = true
  Support = -> [Sketch]
  _Version = 2
FEATURE [PartDesign::Pad] Pad
  Direction = (0,0,1)
  Length = 3.5
  Length2 = 10
  Profile = -> Binder
  Suppressed = false
  Type = 0
FEATURE [PartDesign::SubShapeBinder] Binder001
  BindCopyOnChange = 0
  BindMode = 0
  ClaimChildren = false
  Context = -> Body [Binder001.]
  Fuse = false
  MakeFace = true
  OffsetFill = false
  OffsetIntersection = false
  OffsetJoinType = 0
  OffsetOpenResult = false
  PartialLoad = false
  Relative = true
  Support = -> [Sketch001]
  _Version = 2
FEATURE [PartDesign::Pad] Pad001
  BaseFeature = -> Pad
  Direction = (0,0,1)
  Length = 12.6
  Length2 = 10
  Profile = -> Binder001
  Suppressed = false
  Type = 0
FEATURE [PartDesign::SubShapeBinder] Binder002
  BindCopyOnChange = 0
  BindMode = 0
  ClaimChildren = false
  Context = -> Body [Binder002.]
  Fuse = false
  MakeFace = true
  OffsetFill = false
  OffsetIntersection = false
  OffsetJoinType = 0
  OffsetOpenResult = false
  PartialLoad = false
  Relative = true
  Support = -> [Sketch002]
  _Version = 2
FEATURE [PartDesign::Pocket] Pocket
  BaseFeature = -> Pad001
  Direction = (0,0,-1)
  Length = 5
  Length2 = 5
  Midplane = true
  Profile = -> Binder002
  Suppressed = false
  Type = 1
FEATURE [Sketcher::SketchObject] Sketch003
  ExternalGeometry = -> [Sketch001]
  FullyConstrained = true
  sketch-geometry (5):
    g0: LineSegment StartX=-10.75 StartY=7.3 StartZ=0 EndX=10.75 EndY=7.3 EndZ=0
    g1: LineSegment StartX=10.75 StartY=7.3 StartZ=0 EndX=10.75 EndY=9.3 EndZ=0
    g2: LineSegment StartX=10.75 StartY=9.3 StartZ=0 EndX=-10.75 EndY=9.3 EndZ=0
    g3: LineSegment StartX=-10.75 StartY=9.3 StartZ=0 EndX=-10.75 EndY=7.3 EndZ=0
    g4: GeomPoint X=0 Y=8.3 Z=0
  constraints (13):
    c: Coincident(g0,g1)
    c: Coincident(g1,g2)
    c: Coincident(g2,g3)
    c: Coincident(g3,g0)
    c: Horizontal(g0)
    c: Horizontal(g2)
    c: Vertical(g1)
    c: Vertical(g3)
    c: PointOnObject(g4,g-2)
    c: Symmetric(g0,g1,g4)
    c: DistanceX(g0,g0) = 21.5
    c: PointOnObject(g0,g-3)
    c: DistanceY(g1,g1) = 2
FEATURE [Spreadsheet::Sheet] Spreadsheet  label="Properties"
  cells = B2(length)==41.3 mm; C2(width)==16.6 mm
FEATURE [PartDesign::CoordinateSystem] Local_CS
  AttacherType = Attacher::AttachEngine3D
  AttachmentSupport = -> [XY_Plane]
  MapMode = 5
FEATURE [Sketcher::SketchObject] Sketch004
  AttachmentOffset = pos=(0,0,4) rot=(0,0,1;0rad)
  AttachmentSupport = -> [XY_Plane]
  FullyConstrained = true
  MapMode = 5
  Placement = pos=(0,0,4) rot=(0,0,1;0rad)
  sketch-geometry (4):
    g0: LineSegment StartX=-10.75 StartY=7.3 StartZ=0 EndX=10.75 EndY=7.3 EndZ=0
    g1: LineSegment StartX=10.75 StartY=7.3 StartZ=0 EndX=10.75 EndY=9.3 EndZ=0
    g2: LineSegment StartX=10.75 StartY=9.3 StartZ=0 EndX=-10.75 EndY=9.3 EndZ=0
    g3: LineSegment StartX=-10.75 StartY=9.3 StartZ=0 EndX=-10.75 EndY=7.3 EndZ=0
  constraints (11):
    c: Coincident(g0,g1)
    c: Coincident(g1,g2)
    c: Coincident(g2,g3)
    c: Coincident(g3,g0)
    c: Horizontal(g0)
    c: Vertical(g1)
    c: Vertical(g3)
    c: DistanceY(g1,g1) = 2
    c: DistanceY(g0) = 7.3
    c: Symmetric(g2,g1,g-2)
    c: DistanceX(g0,g0) = 21.5
FEATURE [PartDesign::Pad] Pad002
  BaseFeature = -> Pocket
  Direction = (0,0,1)
  Length = 1
  Length2 = 10
  Profile = -> Sketch004
  ReferenceAxis = -> Sketch004 [N_Axis]
  Suppressed = false
  Type = 0
FEATURE [PartDesign::LinearPattern] LinearPattern
  BaseFeature = -> Pad002
  Direction = -> Z_Axis
  Length = 5
  Mode = 0
  Occurrences = 2
  Offset = 5
  Originals = -> [Pad002]
  Refine = true
  Suppressed = false
FEATURE [PartDesign::Body] Body
  Group = -> [Binder,Pad,Binder001,Pad001,Binder002,Pocket,Local_CS,Sketch004,Pad002,LinearPattern]
  Origin = -> Origin
  Tip = -> LinearPattern
FEATURE [Sketcher::SketchObject] Sketch006  label="magnet_fix_reply_holes"
  ExternalGeometry = -> [Sketch003]
  FullyConstrained = true
  sketch-geometry (2):
    g0: Circle CenterX=18.75 CenterY=0 CenterZ=0 NormalX=0 NormalY=0 NormalZ=1 AngleXU=0 Radius=1.7
    g1: Circle CenterX=-18.75 CenterY=0 CenterZ=0 NormalX=0 NormalY=0 NormalZ=1 AngleXU=0 Radius=1.7
  constraints (5):
    c: PointOnObject(g0,g-1)
    c: Symmetric(g0,g1,g-2)
    c: Equal(g1,g0)
    c: Diameter(g1) = 3.4
    c: DistanceX(g-3,g0) = 8
FEATURE [Sketcher::SketchObject] Sketch005
  ExternalGeometry = -> [Sketch006]
  FullyConstrained = true
  sketch-geometry (3):
    g0: ArcOfCircle CenterX=18.75 CenterY=0 CenterZ=0 NormalX=0 NormalY=0 NormalZ=1 AngleXU=0 Radius=5 StartAngle=4.71239 EndAngle=7.85398
    g1: LineSegment StartX=0 StartY=5 StartZ=0 EndX=18.75 EndY=5 EndZ=0
    g2: LineSegment StartX=0 StartY=-5 StartZ=0 EndX=18.75 EndY=-5 EndZ=0
  constraints (8):
    c: PointOnObject(g1,g-2)
    c: Horizontal(g1)
    c: PointOnObject(g2,g-2)
    c: Horizontal(g2)
    c: Tangent(g2,g0) = -1.5708
    c: Tangent(g1,g0) = 1.5708
    c: Coincident(g0,g-3)
    c: DistanceY(g2,g1) = 10
FEATURE [Part::Mirroring] Part__Mirroring  label="Sketch005 (Mirror #1)"
  Base = (0,0,0)
  Normal = (1,0,0)
  Source = -> Sketch005
FEATURE [Part::FeaturePython] Connect  # WARN: FeaturePython — macro-defined, semantics opaque (R4)
  Objects = -> [Sketch005,Part__Mirroring]
  Tolerance = 0
FEATURE [PartDesign::SubShapeBinder] Binder003
  BindCopyOnChange = 0
  BindMode = 0
  ClaimChildren = true
  Context = -> Body001 [Binder003.]
  Fuse = false
  MakeFace = true
  OffsetFill = false
  OffsetIntersection = false
  OffsetJoinType = 0
  OffsetOpenResult = false
  PartialLoad = false
  Relative = false
  Support = -> [Connect]
  _Version = 2
FEATURE [PartDesign::Pad] Pad003
  Direction = (0,0,1)
  Length = 1
  Length2 = 10
  Profile = -> Binder003
  Refine = true
  Suppressed = false
  Type = 0
FEATURE [Part::Extrusion] Extrude
  Base = -> Sketch006
  Dir = (0,0,1)
  DirMode = 2
  FaceMakerClass = Part::FaceMakerBullseye
  LengthFwd = 10
  LengthRev = 0
  Solid = true
  Symmetric = false
FEATURE [Part::Compound] Compound
  Links = -> [Extrude]
FEATURE [PartDesign::Boolean] Boolean
  BaseFeature = -> Pad003
  Group = -> [Compound]
  Suppressed = false
  Type = 1
  UsePlacement = true
FEATURE [PartDesign::Body] Body001  label="magnet_fix_reply"
  Group = -> [Binder003,Pad003,Boolean]
  Origin = -> Origin001
  Tip = -> Boolean
FEATURE [Part::Feature] Unfold
  shape: bbox 47.5 x 10 x 1 mm, 8 faces (baked)
FEATURE [Sketcher::SketchObject] Unfold_Sketch
  FullyConstrained = false
  sketch-geometry (6):
    g0: ArcOfCircle CenterX=-18.75 CenterY=0 CenterZ=0 NormalX=0 NormalY=0 NormalZ=1 AngleXU=-3.14159 Radius=5 StartAngle=4.71239 EndAngle=7.85398
    g1: LineSegment StartX=18.75 StartY=5 StartZ=0 EndX=-18.75 EndY=5 EndZ=0
    g2: LineSegment StartX=-18.75 StartY=-5 StartZ=0 EndX=18.75 EndY=-5 EndZ=0
    g3: ArcOfCircle CenterX=18.75 CenterY=0 CenterZ=0 NormalX=0 NormalY=0 NormalZ=1 AngleXU=0 Radius=5 StartAngle=4.71239 EndAngle=7.85398
    g4: Circle CenterX=-18.75 CenterY=0 CenterZ=0 NormalX=0 NormalY=0 NormalZ=-1 AngleXU=-3.14159 Radius=1.7
    g5: Circle CenterX=18.75 CenterY=0 CenterZ=0 NormalX=0 NormalY=0 NormalZ=-1 AngleXU=-3.14159 Radius=1.7
FEATURE [Sketcher::SketchObject] Unfold_Sketch_Outline
  FullyConstrained = false
  sketch-geometry (4):
    g0: ArcOfCircle CenterX=-18.75 CenterY=0 CenterZ=0 NormalX=0 NormalY=0 NormalZ=1 AngleXU=-3.14159 Radius=5 StartAngle=4.71239 EndAngle=7.85398
    g1: LineSegment StartX=-18.75 StartY=-5 StartZ=0 EndX=18.75 EndY=-5 EndZ=0
    g2: ArcOfCircle CenterX=18.75 CenterY=0 CenterZ=0 NormalX=0 NormalY=0 NormalZ=1 AngleXU=0 Radius=5 StartAngle=4.71239 EndAngle=7.85398
    g3: LineSegment StartX=18.75 StartY=5 StartZ=0 EndX=-18.75 EndY=5 EndZ=0
FEATURE [Sketcher::SketchObject] Unfold_Sketch_Internal
  FullyConstrained = false
  sketch-geometry (2):
    g0: Circle CenterX=18.75 CenterY=0 CenterZ=0 NormalX=0 NormalY=0 NormalZ=-1 AngleXU=-3.14159 Radius=1.7
    g1: Circle CenterX=-18.75 CenterY=0 CenterZ=0 NormalX=0 NormalY=0 NormalZ=-1 AngleXU=-3.14159 Radius=1.7
FEATURE [TechDraw::DrawSVGTemplate] Template
  Height = 210
  Orientation = 1
  Template = <path>
  Width = 297
FEATURE [TechDraw::DrawViewPart] View
  CoarseView = false
  Direction = (0,0,1)
  Focus = 100
  HardHidden = false
  IsoCount = 0
  IsoHidden = false
  IsoVisible = false
  LockPosition = false
  Perspective = false
  Rotation = 0
  Scale = 4
  ScaleType = 2
  ScrubCount = 0
  SeamHidden = false
  SeamVisible = true
  SmoothHidden = false
  SmoothVisible = true
  Source = -> [Body001]
  X = 112.5
  XDirection = (1,0,0)
  Y = 45
FEATURE [TechDraw::DrawViewPart] View001
  CoarseView = false
  Direction = (0.57735,-0.57735,0.57735)
  Focus = 100
  HardHidden = false
  IsoCount = 0
  IsoHidden = false
  IsoVisible = false
  LockPosition = false
  Perspective = false
  Rotation = 0
  Scale = 4
  ScaleType = 2
  ScrubCount = 0
  SeamHidden = false
  SeamVisible = true
  SmoothHidden = false
  SmoothVisible = true
  Source = -> [Body001]
  X = 208.5
  XDirection = (0.707107,0.707107,0)
  Y = 135
FEATURE [TechDraw::DrawViewDimension] Dimension
  AngleOverride = false
  Arbitrary = false
  ArbitraryTolerances = false
  BoxCorners = (2) [(-95,-20,0),(95,20,0)]
  EqualTolerance = true
  ExtensionAngle = 0
  FormatSpec = %.2w
  FormatSpecOverTolerance = %+.2w
  FormatSpecUnderTolerance = %+.2w
  Inverted = false
  LineAngle = 0
  LockPosition = false
  MeasureType = 1
  OverTolerance = 0
  References2D = -> [View]
  Rotation = 0
  ScaleType = 0
  TheoreticalExact = false
  Type = 1
  UnderTolerance = 0
  X = 0.61437
  Y = 32.297
FEATURE [TechDraw::DrawViewDimension] Dimension001
  AngleOverride = false
  Arbitrary = false
  ArbitraryTolerances = false
  BoxCorners = (2) [(-95,-20,0),(95,20,0)]
  EqualTolerance = true
  ExtensionAngle = 0
  FormatSpec = %.2w
  FormatSpecOverTolerance = %+.2w
  FormatSpecUnderTolerance = %+.2w
  Inverted = false
  LineAngle = 0
  LockPosition = false
  MeasureType = 1
  OverTolerance = 0
  References2D = -> [View]
  Rotation = 0
  ScaleType = 0
  TheoreticalExact = false
  Type = 2
  UnderTolerance = 0
  X = 110.554
  Y = -0.759103
FEATURE [TechDraw::DrawViewDimension] Dimension002
  AngleOverride = false
  Arbitrary = false
  ArbitraryTolerances = false
  BoxCorners = (2) [(-95,-20,0),(95,20,0)]
  EqualTolerance = true
  ExtensionAngle = 0
  FormatSpec = R%.2w
  FormatSpecOverTolerance = %+.2w
  FormatSpecUnderTolerance = %+.2w
  Inverted = false
  LineAngle = 0
  LockPosition = false
  MeasureType = 1
  OverTolerance = 0
  References2D = -> [View]
  Rotation = 0
  ScaleType = 0
  TheoreticalExact = false
  Type = 4
  UnderTolerance = 0
  X = -53.9727
  Y = 5.80719
FEATURE [TechDraw::DrawPage] Page
  KeepUpdated = true
  NextBalloonIndex = 1
  ProjectionType = 0
  Template = -> Template
  Views = -> [View,View001,Dimension,Dimension001,Dimension002]
note: 1 file-system path scrubbed to <path> (originals preserved in the JSON sidecar)
---- part ../module.FCStd = doc fcstd_3955753b3a20 ----
FCSTD DOCUMENT  (FreeCAD 1.1R38827 (Git))
Label: module
License: All rights reserved
LicenseURL: http://en.wikipedia.org/wiki/All_rights_reserved
objects: Sketcher::SketchObject×2, Part::Feature×1, PartDesign::FeatureBase×1, PartDesign::Body×1, Spreadsheet::Sheet×1
note: 8 computed .brp shape members not serialized (recipe doc carries the construction recipe); baked Part::Feature solids carry a one-line shape summary decoded from their .brp

FEATURE [Part::Feature] Part__Feature  label="module002"
  shape: bbox 170 x 148 x 41.12 mm, 715 faces (baked)
FEATURE [Sketcher::SketchObject] Sketch  label="module_holes"
  ArcFitTolerance = 0
  FullyConstrained = true
  MakeInternals = false
  sketch-geometry (10):
    g0: LineSegment StartX=59.5 StartY=-3.5 StartZ=0 EndX=59.5 EndY=3.5 EndZ=0
    g1: LineSegment StartX=59.5 StartY=3.5 StartZ=0 EndX=72.5 EndY=3.5 EndZ=0
    g2: LineSegment StartX=72.5 StartY=3.5 StartZ=0 EndX=72.5 EndY=-3.5 EndZ=0
    g3: LineSegment StartX=72.5 StartY=-3.5 StartZ=0 EndX=59.5 EndY=-3.5 EndZ=0
    g4: GeomPoint [constr] X=66 Y=0 Z=0
    g5: LineSegment StartX=-72.5 StartY=-3.5 StartZ=0 EndX=-72.5 EndY=3.5 EndZ=0
    g6: LineSegment StartX=-72.5 StartY=3.5 StartZ=0 EndX=-59.5 EndY=3.5 EndZ=0
    g7: LineSegment StartX=-59.5 StartY=3.5 StartZ=0 EndX=-59.5 EndY=-3.5 EndZ=0
    g8: LineSegment StartX=-59.5 StartY=-3.5 StartZ=0 EndX=-72.5 EndY=-3.5 EndZ=0
    g9: GeomPoint [constr] X=-66 Y=0 Z=0
  constraints (25):
    c: Coincident(g0,g1)
    c: Coincident(g1,g2)
    c: Coincident(g2,g3)
    c: Coincident(g3,g0)
    c: Horizontal(g1)
    c: Horizontal(g3)
    c: Vertical(g0)
    c: Vertical(g2)
    c: Symmetric(g1,g0,g4)
    c: PointOnObject(g4,g-1)
    c: Coincident(g5,g6)
    c: Coincident(g6,g7)
    c: Coincident(g7,g8)
    c: Coincident(g8,g5)
    c: Horizontal(g6)
    c: Horizontal(g8)
    c: Vertical(g5)
    c: Vertical(g7)
    c: Symmetric(g6,g5,g9)
    c: Symmetric(g9,g4,g-2)
    c: Equal(g1,g6)
    c: Equal(g7,g2)
    c: DistanceX(g1,g1) = 13
    c: DistanceY(g2,g2) = 7
    c: DistanceX(g9,g4) = 132
FEATURE [PartDesign::FeatureBase] BaseFeature
  BaseFeature = -> Part__Feature
  Placement = pos=(0,0,0) rot=(0,0,1;1.5708rad)
  Suppressed = false
FEATURE [PartDesign::Body] Body  label="module_Body"
  AllowCompound = false
  BaseFeature = -> Part__Feature
  Group = -> [BaseFeature]
  Origin = -> Origin
  Tip = -> BaseFeature
FEATURE [Spreadsheet::Sheet] Spreadsheet  label="Properties"
  cells = B2(module_width)==148 mm; C2(module_height)==160 mm; D2(module_fixture_distance_x)==132 mm; E2(module_fixture_distance_y)==80 mm; F2(module_hole_x)==13 mm; G2(module_hole_y)==7 mm
FEATURE [Sketcher::SketchObject] Sketch001  label="module_holes001"
  ArcFitTolerance = 0
  FullyConstrained = true
  MakeInternals = false
  sketch-geometry (10):
    g0: LineSegment StartX=59 StartY=-3.5 StartZ=0 EndX=59 EndY=3.5 EndZ=0
    g1: LineSegment StartX=59 StartY=3.5 StartZ=0 EndX=73 EndY=3.5 EndZ=0
    g2: LineSegment StartX=73 StartY=3.5 StartZ=0 EndX=73 EndY=-3.5 EndZ=0
    g3: LineSegment StartX=73 StartY=-3.5 StartZ=0 EndX=59 EndY=-3.5 EndZ=0
    g4: GeomPoint [constr] X=66 Y=0 Z=0
    g5: LineSegment StartX=-73 StartY=-3.5 StartZ=0 EndX=-73 EndY=3.5 EndZ=0
    g6: LineSegment StartX=-73 StartY=3.5 StartZ=0 EndX=-59 EndY=3.5 EndZ=0
    g7: LineSegment StartX=-59 StartY=3.5 StartZ=0 EndX=-59 EndY=-3.5 EndZ=0
    g8: LineSegment StartX=-59 StartY=-3.5 StartZ=0 EndX=-73 EndY=-3.5 EndZ=0
    g9: GeomPoint [constr] X=-66 Y=0 Z=0
  constraints (25):
    c: Coincident(g0,g1)
    c: Coincident(g1,g2)
    c: Coincident(g2,g3)
    c: Coincident(g3,g0)
    c: Horizontal(g1)
    c: Horizontal(g3)
    c: Vertical(g0)
    c: Vertical(g2)
    c: Symmetric(g1,g0,g4)
    c: PointOnObject(g4,g-1)
    c: Coincident(g5,g6)
    c: Coincident(g6,g7)
    c: Coincident(g7,g8)
    c: Coincident(g8,g5)
    c: Horizontal(g6)
    c: Horizontal(g8)
    c: Vertical(g5)
    c: Vertical(g7)
    c: Symmetric(g6,g5,g9)
    c: Symmetric(g9,g4,g-2)
    c: Equal(g1,g6)
    c: Equal(g7,g2)
    c: DistanceX(g1,g1) = 14
    c: DistanceY(g2,g2) = 7
    c: DistanceX(g9,g4) = 132
---- part composit_stand10_model.FCStd = doc fcstd_23a22d658302 ----
FCSTD DOCUMENT  (FreeCAD 0.22R37100 (Git))
Label: composit_stand10_model
License: All rights reserved
LicenseURL: http://en.wikipedia.org/wiki/All_rights_reserved
objects: App::Link×19, App::DocumentObjectGroup×3, PartDesign::CoordinateSystem×1, App::FeaturePython×1, App::Part×1
note: 1 computed .brp shape members not serialized (recipe doc carries the construction recipe); baked Part::Feature solids carry a one-line shape summary decoded from their .brp
EXTERNAL_REF file=composit_stand10.FCStd obj=Local_CS020
EXTERNAL_REF file=composit_stand10.FCStd obj=Body
EXTERNAL_REF file=composit_stand10.FCStd obj=Local_CS007
EXTERNAL_REF file=composit_stand10.FCStd obj=Local_CS010
EXTERNAL_REF file=composit_stand10.FCStd obj=Body001
EXTERNAL_REF file=composit_stand10.FCStd obj=Local_CS004
EXTERNAL_REF file=composit_stand10.FCStd obj=Local_CS005
EXTERNAL_REF file=composit_stand10.FCStd obj=Body012
EXTERNAL_REF file=composit_stand10.FCStd obj=Local_CS006
EXTERNAL_REF file=composit_stand10.FCStd obj=Local_CS012
EXTERNAL_REF file=composit_stand10.FCStd obj=Body003
EXTERNAL_REF file=composit_stand10.FCStd obj=Local_CS009
EXTERNAL_REF file=composit_stand10.FCStd obj=Local_CS015
EXTERNAL_REF file=composit_stand10.FCStd obj=Body010
EXTERNAL_REF file=composit_stand10.FCStd obj=Local_CS008
EXTERNAL_REF file=composit_stand10.FCStd obj=Local_CS013
EXTERNAL_REF file=composit_stand10.FCStd obj=Body006
EXTERNAL_REF file=composit_stand10.FCStd obj=Local_CS014
EXTERNAL_REF file=composit_stand10.FCStd obj=Local_CS016
EXTERNAL_REF file=composit_stand10.FCStd obj=Body004
EXTERNAL_REF file=composit_stand10.FCStd obj=Local_CS018
EXTERNAL_REF file=composit_stand10.FCStd obj=Body014
EXTERNAL_REF file=composit_stand10.FCStd obj=Local_CS025
EXTERNAL_REF file=composit_stand10.FCStd obj=Body011
EXTERNAL_REF file=composit_stand10.FCStd obj=Local_CS026
EXTERNAL_REF file=composit_stand10.FCStd obj=Local_CS027
EXTERNAL_REF file=composit_stand10.FCStd obj=Body019
EXTERNAL_REF file=composit_stand10.FCStd obj=Local_CS028
EXTERNAL_REF file=../magnet_fix.FCStd obj=Local_CS
EXTERNAL_REF file=../magnet_fix.FCStd obj=Body
EXTERNAL_REF file=composit_stand10.FCStd obj=LCS_1
EXTERNAL_REF file=composit_stand10.FCStd obj=Part
EXTERNAL_REF file=composit_stand10.FCStd obj=Local_CS029
EXTERNAL_REF file=composit_stand10.FCStd obj=Local_CS030
EXTERNAL_REF file=composit_stand10.FCStd obj=Body021
EXTERNAL_REF file=composit_stand10.FCStd obj=Local_CS031
EXTERNAL_REF file=composit_stand10.FCStd obj=Body024
EXTERNAL_REF file=../basin_2.FCStd obj=Local_CS
EXTERNAL_REF file=composit_stand10.FCStd obj=Local_CS022
EXTERNAL_REF file=../basin_2.FCStd obj=Body
EXTERNAL_REF file=composit_stand10.FCStd obj=Local_CS033
EXTERNAL_REF file=composit_stand10.FCStd obj=Body008
EXTERNAL_REF file=composit_stand10.FCStd obj=Local_CS032
EXTERNAL_REF file=composit_stand10.FCStd obj=Local_CS034
EXTERNAL_REF file=composit_stand10.FCStd obj=Body028
EXTERNAL_REF file=composit_stand10.FCStd obj=Local_CS035
EXTERNAL_REF file=../water_sensor.FCStd obj=Assembly
EXTERNAL_REF file=../composit_electric_shield.FCStd obj=Body
EXTERNAL_REF file=../composit_electric_shield.FCStd obj=Local_CS
EXTERNAL_REF file=composit_stand10.FCStd obj=Local_CS036

FEATURE [App::DocumentObjectGroup] Parts
FEATURE [PartDesign::CoordinateSystem] LCS_Origin
  AttacherType = Attacher::AttachEngine3D
  AttachmentSupport = -> [XY_Plane]
  MapMode = 2
FEATURE [App::DocumentObjectGroup] Constraints
FEATURE [App::FeaturePython] Variables  # WARN: FeaturePython — macro-defined, semantics opaque (R4)
  Type = App::PropertyContainer
FEATURE [App::DocumentObjectGroup] Configurations
FEATURE [App::Link] face
  AttachedBy = #Local_CS020
  AttachedTo = Parent Assembly#LCS_Origin
  AttachmentOffset = pos=(0,0,0) rot=(0,0,1;3.14159rad)
  LinkPlacement = pos=(0,0,0) rot=(0,0,1;3.14159rad)
  LinkedObject = -> <external composit_stand10.FCStd>#Body
  Placement = pos=(0,0,0) rot=(0,0,1;3.14159rad)
  SolverId = Asm4EE
  expr: Placement = LCS_Origin.Placement * AttachmentOffset * composit_stand10#Local_CS020.Placement ^ -1
FEATURE [App::Link] back
  AttachedBy = #Local_CS010
  AttachedTo = face#Local_CS007
  LinkPlacement = pos=(0,0,0) rot=(0,0,1;3.14159rad)
  LinkedObject = -> <external composit_stand10.FCStd>#Body001
  Placement = pos=(0,0,0) rot=(0,0,1;3.14159rad)
  SolverId = Asm4EE
  expr: Placement = face.Placement * composit_stand10#Local_CS007.Placement * AttachmentOffset * composit_stand10#Local_CS010.Placement ^ -1
FEATURE [App::Link] sink
  AttachedBy = #Local_CS004
  AttachedTo = face#Local_CS005
  LinkPlacement = pos=(-1.1e-14,-90,140) rot=(0,0,1;3.14159rad)
  LinkedObject = -> <external composit_stand10.FCStd>#Body012
  Placement = pos=(-1.1e-14,-90,140) rot=(0,0,1;3.14159rad)
  SolverId = Asm4EE
  expr: Placement = face.Placement * composit_stand10#Local_CS005.Placement * AttachmentOffset * composit_stand10#Local_CS004.Placement ^ -1
FEATURE [App::Link] lamp_holder
  AttachedBy = #Local_CS012
  AttachedTo = face#Local_CS006
  LinkPlacement = pos=(-1.1e-14,-90,254) rot=(0,0,1;3.14159rad)
  LinkedObject = -> <external composit_stand10.FCStd>#Body003
  Placement = pos=(-1.1e-14,-90,254) rot=(0,0,1;3.14159rad)
  SolverId = Asm4EE
  expr: Placement = face.Placement * composit_stand10#Local_CS006.Placement * AttachmentOffset * composit_stand10#Local_CS012.Placement ^ -1
FEATURE [App::Link] cap_outer
  AttachedBy = #Local_CS015
  AttachedTo = face#Local_CS009
  LinkPlacement = pos=(0,0,813) rot=(0,0,1;3.14159rad)
  LinkedObject = -> <external composit_stand10.FCStd>#Body010
  Placement = pos=(0,0,813) rot=(0,0,1;3.14159rad)
  SolverId = Asm4EE
  expr: Placement = face.Placement * composit_stand10#Local_CS009.Placement * AttachmentOffset * composit_stand10#Local_CS015.Placement ^ -1
FEATURE [App::Link] dropper_fix_composit
  AttachedBy = #Local_CS013
  AttachedTo = face#Local_CS008
  LinkPlacement = pos=(-1.1e-14,-90,813.1) rot=(0,0,1;3.14159rad)
  LinkedObject = -> <external composit_stand10.FCStd>#Body006
  Placement = pos=(-1.1e-14,-90,813.1) rot=(0,0,1;3.14159rad)
  SolverId = Asm4EE
  expr: Placement = face.Placement * composit_stand10#Local_CS008.Placement * AttachmentOffset * composit_stand10#Local_CS013.Placement ^ -1
FEATURE [App::Link] dropper_fix_PP
  AttachedBy = #Local_CS016
  AttachedTo = dropper_fix_composit#Local_CS014
  LinkPlacement = pos=(-1.1e-14,-90,816.1) rot=(0,0,1;3.14159rad)
  LinkedObject = -> <external composit_stand10.FCStd>#Body004
  Placement = pos=(-1.1e-14,-90,816.1) rot=(0,0,1;3.14159rad)
  SolverId = Asm4EE
  expr: Placement = dropper_fix_composit.Placement * composit_stand10#Local_CS014.Placement * AttachmentOffset * composit_stand10#Local_CS016.Placement ^ -1
FEATURE [App::Link] bottom_composit
  AttachedBy = #Local_CS018
  AttachedTo = face#Local_CS007
  LinkPlacement = pos=(0,0,0) rot=(0,0,1;3.14159rad)
  LinkedObject = -> <external composit_stand10.FCStd>#Body014
  Placement = pos=(0,0,0) rot=(0,0,1;3.14159rad)
  SolverId = Asm4EE
  expr: Placement = face.Placement * composit_stand10#Local_CS007.Placement * AttachmentOffset * composit_stand10#Local_CS018.Placement ^ -1
FEATURE [App::Link] cap_inner
  AttachedBy = #Local_CS025
  AttachedTo = cap_outer#Local_CS015
  LinkPlacement = pos=(0,0,813) rot=(0,0,1;3.14159rad)
  LinkedObject = -> <external composit_stand10.FCStd>#Body011
  Placement = pos=(0,0,813) rot=(0,0,1;3.14159rad)
  SolverId = Asm4EE
  expr: Placement = cap_outer.Placement * composit_stand10#Local_CS015.Placement * AttachmentOffset * composit_stand10#Local_CS025.Placement ^ -1
FEATURE [App::Link] magnet_fix
  AttachedBy = #Local_CS026
  AttachedTo = face#Local_CS027
  LinkPlacement = pos=(-299.78,-218,16) rot=(0,0,1;3.14159rad)
  LinkedObject = -> <external composit_stand10.FCStd>#Body019
  Placement = pos=(-299.78,-218,16) rot=(0,0,1;3.14159rad)
  SolverId = Asm4EE
  expr: Placement = face.Placement * composit_stand10#Local_CS027.Placement * AttachmentOffset * composit_stand10#Local_CS026.Placement ^ -1
FEATURE [App::Link] Body
  AttachedBy = #Local_CS
  AttachedTo = magnet_fix#Local_CS028
  LinkPlacement = pos=(-299.78,-210.7,36) rot=(-0.707107,0,-0.707107;3.14159rad)
  LinkedObject = -> <external ../magnet_fix.FCStd>#Body
  Placement = pos=(-299.78,-210.7,36) rot=(-0.707107,0,-0.707107;3.14159rad)
  SolverId = Asm4EE
  expr: Placement = magnet_fix.Placement * composit_stand10#Local_CS028.Placement * AttachmentOffset * magnet_fix#Local_CS.Placement ^ -1
FEATURE [App::Link] modules
  AttachedBy = #LCS_1
  AttachedTo = face#Local_CS020
  AttachmentOffset = pos=(0,0,-1.4) rot=(0,0,1;0rad)
  LinkPlacement = pos=(0,0,-1.4) rot=(0,0,1;3.14159rad)
  LinkedObject = -> <external composit_stand10.FCStd>#Part
  Placement = pos=(0,0,-1.4) rot=(0,0,1;3.14159rad)
  SolverId = Asm4EE
  expr: Placement = face.Placement * composit_stand10#Local_CS020.Placement * AttachmentOffset * composit_stand10#LCS_1.Placement ^ -1
FEATURE [App::Link] front_shield
  AttachedBy = #Local_CS029
  AttachedTo = bottom_composit#Local_CS030
  LinkPlacement = pos=(-2.73e-14,-223,6) rot=(0,0,1;3.14159rad)
  LinkedObject = -> <external composit_stand10.FCStd>#Body021
  Placement = pos=(-2.73e-14,-223,6) rot=(0,0,1;3.14159rad)
  SolverId = Asm4EE
  expr: Placement = bottom_composit.Placement * composit_stand10#Local_CS030.Placement * AttachmentOffset * composit_stand10#Local_CS029.Placement ^ -1
FEATURE [App::Link] Body024
  AttachedBy = #Local_CS031
  AttachedTo = face#Local_CS020
  AttachmentOffset = pos=(0,0,6) rot=(0,0,1;0rad)
  LinkPlacement = pos=(0,0,6) rot=(0,0,1;3.14159rad)
  LinkedObject = -> <external composit_stand10.FCStd>#Body024
  Placement = pos=(0,0,6) rot=(0,0,1;3.14159rad)
  SolverId = Asm4EE
  expr: Placement = face.Placement * composit_stand10#Local_CS020.Placement * AttachmentOffset * composit_stand10#Local_CS031.Placement ^ -1
FEATURE [App::Link] Body025
  AttachedBy = #Local_CS
  AttachedTo = bottom_composit#Local_CS022
  AttachmentOffset = pos=(0,0,0) rot=(0,0,1;1.5708rad)
  LinkPlacement = pos=(-1.42e-14,-116.3,11) rot=(0,0,1;4.71239rad)
  LinkedObject = -> <external ../basin_2.FCStd>#Body
  Placement = pos=(-1.42e-14,-116.3,11) rot=(0,0,1;4.71239rad)
  SolverId = Asm4EE
  expr: Placement = bottom_composit.Placement * composit_stand10#Local_CS022.Placement * AttachmentOffset * basin_2#Local_CS.Placement ^ -1
FEATURE [App::Link] pump_holder
  AttachedBy = #Local_CS033
  AttachedTo = Body025#Local_CS
  AttachmentOffset = pos=(0,0,2) rot=(0,0,1;4.71239rad)
  LinkPlacement = pos=(2.89e-14,-19.3,13) rot=(0,0,-1;3.14159rad)
  LinkedObject = -> <external composit_stand10.FCStd>#Body008
  Placement = pos=(2.89e-14,-19.3,13) rot=(0,0,-1;3.14159rad)
  SolverId = Asm4EE
  expr: Placement = Body025.Placement * basin_2#Local_CS.Placement * AttachmentOffset * composit_stand10#Local_CS033.Placement ^ -1
FEATURE [App::Link] Body028
  AttachedBy = #Local_CS034
  AttachedTo = pump_holder#Local_CS032
  LinkPlacement = pos=(-103,-97.3,82) rot=(0,0,-1;3.14159rad)
  LinkedObject = -> <external composit_stand10.FCStd>#Body028
  Placement = pos=(-103,-97.3,82) rot=(0,0,-1;3.14159rad)
  SolverId = Asm4EE
  expr: Placement = pump_holder.Placement * composit_stand10#Local_CS032.Placement * AttachmentOffset * composit_stand10#Local_CS034.Placement ^ -1
FEATURE [App::Link] water_sensor
  AttachedBy = Origin
  AttachedTo = Body028#Local_CS035
  LinkPlacement = pos=(-103,-90.3,81) rot=(0,0,-1;3.14159rad)
  LinkedObject = -> <external ../water_sensor.FCStd>#Assembly
  Placement = pos=(-103,-90.3,81) rot=(0,0,-1;3.14159rad)
  SolverId = Asm4EE
  expr: LinkedObject = <<water_sensor>>#<<Assembly>>._self
  expr: Placement = Body028.Placement * composit_stand10#Local_CS035.Placement * AttachmentOffset
FEATURE [App::Link] composit_electric_shield_inner
  AttachedBy = #Local_CS
  AttachedTo = face#Local_CS036
  LinkPlacement = pos=(-286.163,-80,555.5) rot=(-0.57735,0.57735,0.57735;4.18879rad)
  LinkedObject = -> <external ../composit_electric_shield.FCStd>#Body
  Placement = pos=(-286.163,-80,555.5) rot=(-0.57735,0.57735,0.57735;4.18879rad)
  SolverId = Asm4EE
  expr: LinkedObject = composit_electric_shield#<<composit_electric_shield_inner>>._self
  expr: Placement = face.Placement * composit_stand10#Local_CS036.Placement * AttachmentOffset * composit_electric_shield#Local_CS.Placement ^ -1
FEATURE [App::Part] Assembly
  AssemblyType = Part::Link
  Group = -> [LCS_Origin,Constraints,Variables,Configurations,face,back,sink,lamp_holder,cap_outer,dropper_fix_composit,dropper_fix_PP,bottom_composit,cap_inner,magnet_fix,Body,modules,front_shield,Body024,Body025,pump_holder,Body028,water_sensor,composit_electric_shield_inner]
  Origin = -> Origin
  Type = Assembly
